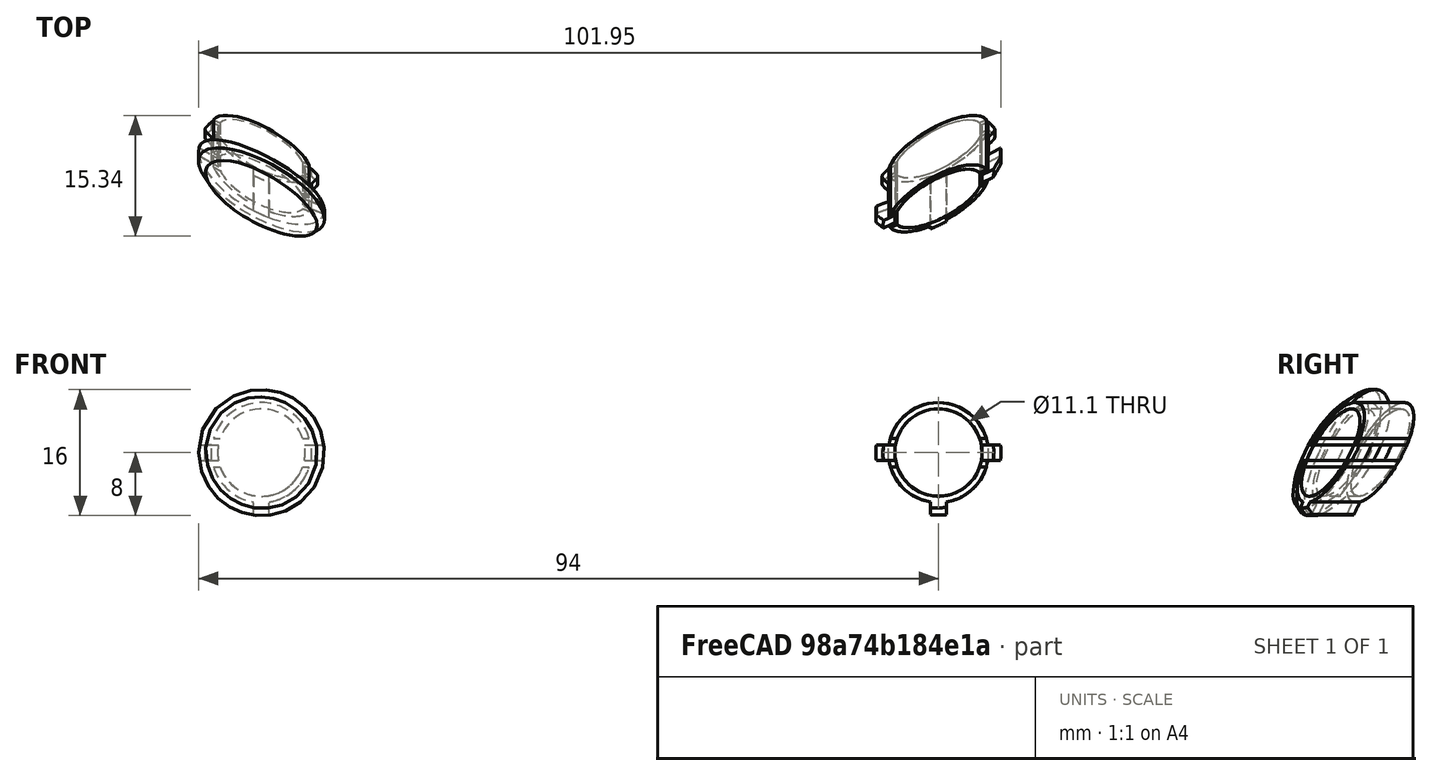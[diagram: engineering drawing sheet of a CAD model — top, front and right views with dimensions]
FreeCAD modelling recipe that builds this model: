
FCSTD DOCUMENT  (FreeCAD 0.19R24276 (Git))
Label: PB3D_XPortCover
License: All rights reserved
LicenseURL: http://en.wikipedia.org/wiki/All_rights_reserved
objects: Sketcher::SketchObject×71, PartDesign::Plane×12, PartDesign::Pad×11, PartDesign::Pocket×11, PartDesign::SubtractiveLoft×6, PartDesign::Chamfer×6, PartDesign::Body×6, PartDesign::Boolean×4, Mesh::Feature×2, Spreadsheet::Sheet×1, App::Part×1, Part::Mirroring×1
note: 162 computed .brp shape members not serialized (recipe doc carries the construction recipe); baked Part::Feature solids carry a one-line shape summary decoded from their .brp

FEATURE [Spreadsheet::Sheet] Spreadsheet  label="params"
  cells = A1=M2 Bolt Clearances; C1=M2.5 Bolt Clearances; E1=Standard Dims; A2=Hole Clear Diam; B2(m2_hole_clear_diam)==2.5mm; C2=Hole Clear Diam; D2(m25_hole_clear_diam)==2.8mm; E2=Std. Tol. Clear; F2(std_tol_clear)==0.3mm; A3=Head Clear Diam; B3(m2_head_clear_diam)==4mm; C3=Head Clear Diam; D3(m25_head_clear_diam)==5mm; E3=Std. Tol. Interfere; F3(std_tol_interfere)==0.2mm; A4=Head Min Depth; B4(m2_head_min_depth)==1.3mm; C4=Head Min Depth; D4(m25_head_min_depth)==1.6mm; E4=Std. Wall Thick; F4(std_wall_thick)==2mm; A5=Nut Clear Flat; B5(m2_nut_clear_flat)==4.2mm; C5=Nut Clear Flat; D5(m25_nut_clear_flat)==5.2mm; E5=Std. Min Wall Thick; F5(std_min_wall_thick)==0.8mm; A6=Nut Min Depth; B6(m2_nut_min_depth)==1.75mm; C6=Nut Min Depth; D6(m25_nut_min_depth)==2mm; A8=Bottom Plate Main Params; C8=Shell Main Params; E8=X Port Front; A9=Plate Length; B9(plate_length)==170mm; C9=Shell Height; D9(shell_totheight)==42mm; E9=XPort Diam; F9(xport_diam)==13mm; A10=Plate Width; B10(plate_width)==155mm; C10=Shell Vert Height; D10(shell_vertheight)==10mm; E10=XPort Height Loc; F10(xport_height_loc)==33.25mm; A11=Front Diameter; B11(front_diameter)==225mm; C11=Shell Overhang Length; D11(shell_overhang_leng)==14mm; E11=XPort Offset Loc; F11(xport_offset_loc)==43mm; A12=Tail Width; B12(tail_width)==50mm; C12=Shell Wall Thickness; D12(shell_wall_thick)==2mm; E12=XPort Plug Wall Thick; F12(xport_plug_wall_thick)==0.8mm; A13=Plate Thickness; B13(plate_thick)==3mm; E13=XPort Plug Diam; F13(xport_plug_diam)==xport_diam - std_tol_clear; C14=Shell Angled Height; D14(shell_overhang_height)==shell_totheight - shell_vertheight; E14=XPort Plug Plate Diam; F14(xport_plug_plate_diam)==16mm; A15=Front Vert. Edge; B15(front_vert_edge)==2mm; C15=Shell Angle; D15(shell_wall_angle)==atan(shell_overhang_leng / shell_overhang_height); E15=XPort Plug Plate Thick; F15(xport_plug_plate_thick)==1.6mm; A16=Back Vert. Edge; B16(back_vert_edge)==15mm; E16=XPort Clip Size; F16(xport_clip_size)==0.8mm; C17=Shell Angle Overhang Calc; A18=Std. Radius; B18(std_rad)==2mm; C18=Overhang Slope; D18(shell_overhang_slope)==shell_overhang_leng / (shell_totheight - shell_vertheight); A19=Wheel Well Radius; B19(wheel_well_rad)==7mm; C19=Overhang Offset; D19(shell_overhang_offset)==-1 * shell_vertheight * shell_overhang_slope; A20=Tail Radius; B20(tail_rad)==5mm; A22=Wheel Well Plate Width; B22(wheel_well_plate_width)==115mm; A23=Wheel Well Clearance; B23(wheel_well_clearance)==48mm; A24=Wheel Well Vert; B24(wheel_well_vert)==7mm
FEATURE [PartDesign::Plane] DatumPlane  label="Datum_ShellVert"
  AttachmentOffset = pos=(0,0,10) rot=(0,0,1;0rad)
  Length = 90.7688
  MapMode = 5
  Placement = pos=(0,0,10) rot=(0,0,1;0rad)
  ResizeMode = 0
  Support = -> [XY_Plane001]
  Width = 86.5183
  expr: .AttachmentOffset.Base.z = <<params>>.shell_vertheight
FEATURE [PartDesign::Plane] DatumPlane001  label="Datum_ShellTot"
  AttachmentOffset = pos=(0,0,42) rot=(0,0,1;0rad)
  Length = 90.7688
  MapMode = 5
  Placement = pos=(0,0,42) rot=(0,0,1;0rad)
  ResizeMode = 0
  Support = -> [XY_Plane001]
  Width = 86.5183
  expr: .AttachmentOffset.Base.z = <<params>>.shell_totheight
FEATURE [Sketcher::SketchObject] Sketch002  label="Sketch_Shell_Vert"
  FullyConstrained = true
  MapMode = 5
  Placement = pos=(0,0,10) rot=(0,0,1;0rad)
  Support = -> [DatumPlane]
  expr: Constraints[106] = <<params>>.xport_offset_loc
  expr: Constraints[121] = <<params>>.std_wall_thick
  expr: Constraints[103] = <<params>>.std_wall_thick
  expr: Constraints[63] = <<params>>.std_rad
  expr: Constraints[113] = <<params>>.xport_plug_plate_thick
  expr: Constraints[104] = <<params>>.plate_length / 2 + <<params>>.std_wall_thick
  expr: Constraints[47] = <<params>>.front_diameter
  expr: Constraints[40] = <<params>>.plate_length
  expr: Constraints[65] = <<params>>.std_rad
  expr: Constraints[76] = <<params>>.front_vert_edge
  expr: Constraints[80] = <<params>>.std_rad
  expr: Constraints[36] = <<params>>.wheel_well_plate_width
  expr: Constraints[77] = <<params>>.back_vert_edge
  expr: Constraints[78] = <<params>>.wheel_well_clearance
  expr: Constraints[42] = <<params>>.tail_width
  expr: Constraints[79] = <<params>>.plate_width
  expr: Constraints[81] = <<params>>.std_rad
  expr: Constraints[41] = <<params>>.tail_rad
  sketch-geometry (50):
    g0: LineSegment StartX=-57.5 StartY=17 StartZ=0 EndX=-57.5 EndY=-17 EndZ=0
    g1: LineSegment StartX=57.5 StartY=17 StartZ=0 EndX=57.5 EndY=-17 EndZ=0
    g2: LineSegment StartX=-57.5 StartY=0 StartZ=0 EndX=57.5 EndY=0 EndZ=0
    g3: LineSegment StartX=-64.5 StartY=-24 StartZ=0 EndX=64.5 EndY=-24 EndZ=0
    g4: LineSegment StartX=-64.5 StartY=24 StartZ=0 EndX=64.5 EndY=24 EndZ=0
    g5: LineSegment StartX=-64.5 StartY=-24 StartZ=0 EndX=-75.5 EndY=-24 EndZ=0
    g6: LineSegment StartX=64.5 StartY=-24 StartZ=0 EndX=75.5 EndY=-24 EndZ=0
    g7: ArcOfCircle CenterX=0 CenterY=52.6846 CenterZ=0 NormalX=0 NormalY=0 NormalZ=1 AngleXU=0 Radius=112.5 StartAngle=3.96017 EndAngle=5.4646
    g8: LineSegment StartX=-64.5 StartY=24 StartZ=0 EndX=-75.5 EndY=24 EndZ=0
    g9: LineSegment StartX=64.5 StartY=24 StartZ=0 EndX=75.5 EndY=24 EndZ=0
    g10: LineSegment StartX=-77.1162 StartY=42.1781 StartZ=0 EndX=-29.0404 EndY=108.13 EndZ=0
    g11: LineSegment StartX=-25 StartY=110.185 StartZ=0 EndX=25 EndY=110.185 EndZ=0
    g12: LineSegment StartX=29.0404 StartY=108.13 StartZ=0 EndX=77.1162 EndY=42.1781 EndZ=0
    g13: LineSegment StartX=0 StartY=0 StartZ=0 EndX=0 EndY=110.185 EndZ=0
    g14: ArcOfCircle CenterX=-25 CenterY=105.185 CenterZ=0 NormalX=0 NormalY=0 NormalZ=1 AngleXU=0 Radius=5 StartAngle=1.5708 EndAngle=2.5117
    g15: ArcOfCircle CenterX=25 CenterY=105.185 CenterZ=0 NormalX=0 NormalY=0 NormalZ=1 AngleXU=0 Radius=5 StartAngle=0.629894 EndAngle=1.5708
    g16: ArcOfCircle CenterX=-64.5 CenterY=17 CenterZ=0 NormalX=0 NormalY=0 NormalZ=1 AngleXU=0 Radius=7 StartAngle=0 EndAngle=1.5708
    g17: ArcOfCircle CenterX=-64.5 CenterY=-17 CenterZ=0 NormalX=0 NormalY=0 NormalZ=1 AngleXU=0 Radius=7 StartAngle=4.71239 EndAngle=6.28319
    g18: ArcOfCircle CenterX=64.5 CenterY=-17 CenterZ=0 NormalX=0 NormalY=0 NormalZ=1 AngleXU=0 Radius=7 StartAngle=3.14159 EndAngle=4.71239
    g19: ArcOfCircle CenterX=64.5 CenterY=17 CenterZ=0 NormalX=0 NormalY=0 NormalZ=1 AngleXU=0 Radius=7 StartAngle=1.5708 EndAngle=3.14159
    g20: GeomPoint X=0 Y=-59.8154 Z=0
    g21: Circle CenterX=0 CenterY=52.6846 CenterZ=0 NormalX=0 NormalY=0 NormalZ=1 AngleXU=0 Radius=112.5
    g22: LineSegment StartX=77.5 StartY=26 StartZ=0 EndX=77.5 EndY=41 EndZ=0
    g23: LineSegment StartX=77.5 StartY=-26 StartZ=0 EndX=77.5 EndY=-28 EndZ=0
    g24: LineSegment StartX=-77.5 StartY=-28 StartZ=0 EndX=-77.5 EndY=-26 EndZ=0
    g25: LineSegment StartX=-77.5 StartY=26 StartZ=0 EndX=-77.5 EndY=41 EndZ=0
    g26: ArcOfCircle CenterX=75.5 CenterY=-28 CenterZ=0 NormalX=0 NormalY=0 NormalZ=1 AngleXU=0 Radius=2 StartAngle=5.4646 EndAngle=6.28319
    g27: ArcOfCircle CenterX=75.5 CenterY=-26 CenterZ=0 NormalX=0 NormalY=0 NormalZ=1 AngleXU=0 Radius=2 StartAngle=4e-16 EndAngle=1.5708
    g28: ArcOfCircle CenterX=-75.5 CenterY=-28 CenterZ=0 NormalX=0 NormalY=0 NormalZ=1 AngleXU=0 Radius=2 StartAngle=3.14159 EndAngle=3.96017
    g29: ArcOfCircle CenterX=-75.5 CenterY=-26 CenterZ=0 NormalX=0 NormalY=0 NormalZ=1 AngleXU=0 Radius=2 StartAngle=1.5708 EndAngle=3.14159
    g30: ArcOfCircle CenterX=75.5 CenterY=26 CenterZ=0 NormalX=0 NormalY=0 NormalZ=1 AngleXU=0 Radius=2 StartAngle=4.71239 EndAngle=6.28319
    g31: ArcOfCircle CenterX=75.5 CenterY=41 CenterZ=0 NormalX=0 NormalY=0 NormalZ=1 AngleXU=0 Radius=2 StartAngle=-9e-16 EndAngle=0.629894
    g32: ArcOfCircle CenterX=-75.5 CenterY=26 CenterZ=0 NormalX=0 NormalY=0 NormalZ=1 AngleXU=0 Radius=2 StartAngle=3.14159 EndAngle=4.71239
    g33: ArcOfCircle CenterX=-75.5 CenterY=41 CenterZ=0 NormalX=0 NormalY=0 NormalZ=1 AngleXU=0 Radius=2 StartAngle=2.5117 EndAngle=3.14159
    g34: LineSegment StartX=77.5 StartY=26 StartZ=0 EndX=77.5 EndY=-26 EndZ=0
    g35: LineSegment StartX=-77.5 StartY=26 StartZ=0 EndX=-77.5 EndY=-26 EndZ=0
    g36: LineSegment StartX=77.5 StartY=41 StartZ=0 EndX=77.5 EndY=-28 EndZ=0
    g37: LineSegment StartX=-77.5 StartY=41 StartZ=0 EndX=-77.5 EndY=-28 EndZ=0
    g38: ArcOfCircle CenterX=0 CenterY=52.6846 CenterZ=0 NormalX=0 NormalY=0 NormalZ=1 AngleXU=0 Radius=112.5 StartAngle=4.71239 EndAngle=5.4646
    g39: LineSegment StartX=-2 StartY=2 StartZ=0 EndX=-2 EndY=-87 EndZ=0
    g40: LineSegment StartX=76.8665 StartY=-38.9967 StartZ=0 EndX=76.8665 EndY=-87 EndZ=0
    g41: LineSegment StartX=-2 StartY=-87 StartZ=0 EndX=76.8665 EndY=-87 EndZ=0
    g42: LineSegment StartX=76.8665 StartY=-29.4604 StartZ=0 EndX=76.8665 EndY=2 EndZ=0
    g43: LineSegment StartX=-2 StartY=2 StartZ=0 EndX=76.8665 EndY=2 EndZ=0
    g44: LineSegment StartX=0 StartY=-70.7909 StartZ=0 EndX=76.8665 EndY=-38.9967 EndZ=0
    g45: GeomPoint X=43 Y=-51.2734 Z=0
    g46: LineSegment StartX=0 StartY=52.6846 StartZ=0 EndX=43 EndY=-51.2734 EndZ=0
    g47: LineSegment StartX=43.6116 StartY=-52.7519 StartZ=0 EndX=43 EndY=-51.2734 EndZ=0
    g48: LineSegment StartX=76.8665 StartY=-38.9967 StartZ=0 EndX=76.8665 EndY=-29.4604 EndZ=0
    g49: LineSegment StartX=-2.07e-14 StartY=-59.8154 StartZ=0 EndX=0 EndY=-70.7909 EndZ=0
  constraints (122):
    c: Vertical(g0)
    c: Vertical(g1)
    c: Horizontal(g2)
    c: Symmetric(g2,g2,g-1)
    c: Horizontal(g3)
    c: Horizontal(g5)
    c: Horizontal(g6)
    c: PointOnObject(g7,g-2)
    c: Horizontal(g8)
    c: Horizontal(g9)
    c: Horizontal(g11)
    c: Coincident(g13,g-1)
    c: PointOnObject(g13,g-2)
    c: Tangent(g10,g14) = 1.5708
    c: Tangent(g11,g14) = 1.5708
    c: Tangent(g11,g15) = 1.5708
    c: Tangent(g12,g15) = 1.5708
    c: Tangent(g8,g16) = -1.5708
    c: Tangent(g0,g16) = 1.5708
    c: Tangent(g5,g17) = 1.5708
    c: Tangent(g0,g17) = 1.5708
    c: Tangent(g1,g18) = -1.5708
    c: Tangent(g6,g18) = -1.5708
    c: Tangent(g1,g19) = -1.5708
    c: Tangent(g9,g19) = 1.5708
    c: Equal(g15,g14)
    c: Symmetric(g11,g11,g13)
    c: Equal(g18,g19)
    c: Equal(g19,g16)
    c: Equal(g16,g17)
    c: PointOnObject(g20,g-2)
    c: PointOnObject(g20,g7)
    c: Coincident(g4,g8)
    c: Coincident(g4,g9)
    c: Coincident(g3,g6)
    c: Coincident(g3,g5)
    c: DistanceX(g2,g2) = 115
    c: Symmetric(g0,g0,g2)
    c: Symmetric(g1,g1,g2)
    c: Radius(g19) = 7
    c: DistanceY(g20,g11) = 170
    c: Radius(g15) = 5
    c: DistanceX(g11,g11) = 50
    c: Equal(g9,g8)
    c: Equal(g9,g6)
    c: Coincident(g21,g7)
    c: PointOnObject(g20,g21)
    c: Diameter(g21) = 225
    c: Vertical(g22)
    c: Vertical(g23)
    c: Vertical(g24)
    c: Vertical(g25)
    c: Equal(g5,g8)
    c: Equal(g10,g12)
    c: Tangent(g7,g26) = -1.5708
    c: Tangent(g23,g26) = 1.5708
    c: Tangent(g23,g27) = 1.5708
    c: Tangent(g6,g27) = 1.5708
    c: Tangent(g7,g28) = -1.5708
    c: Tangent(g24,g28) = 1.5708
    c: Tangent(g24,g29) = 1.5708
    c: Tangent(g5,g29) = -1.5708
    c: Equal(g29,g27)
    c: Radius(g27) = 2
    c: Equal(g26,g28)
    c: Radius(g26) = 2
    c: Tangent(g9,g30) = -1.5708
    c: Tangent(g22,g30) = -1.5708
    c: Tangent(g22,g31) = -1.5708
    c: Tangent(g12,g31) = 1.5708
    c: Tangent(g8,g32) = 1.5708
    c: Tangent(g25,g32) = 1.5708
    c: Tangent(g10,g33) = 1.5708
    c: Tangent(g25,g33) = 1.5708
    c: Equal(g30,g32)
    c: Equal(g31,g33)
    c: DistanceY(g23,g23) = 2
    c: DistanceY(g22,g22) = 15
    c: DistanceY(g6,g9) = 48
    c: DistanceX(g24,g23) = 155
    c: Radius(g30) = 2
    c: Radius(g31) = 2
    c: Coincident(g34,g22)
    c: Coincident(g34,g23)
    c: Coincident(g35,g25)
    c: Coincident(g35,g24)
    c: Coincident(g37,g28)
    c: Coincident(g37,g33)
    c: Coincident(g36,g31)
    c: Coincident(g36,g26)
    c: Coincident(g38,g7)
    c: PointOnObject(g38,g-2)
    c: Coincident(g38,g7)
    c: Vertical(g39)
    c: Vertical(g40)
    c: Coincident(g41,g39)
    c: Coincident(g41,g40)
    c: Horizontal(g41)
    c: Coincident(g42,g38)
    c: Vertical(g42)
    c: Coincident(g43,g39)
    c: Coincident(g43,g42)
    c: Horizontal(g43)
    c: DistanceY(g-1,g39) = 2
    c: DistanceY(g39,g-1) = 87
    c: PointOnObject(g45,g38)
    c: DistanceX(g-1,g45) = 43
    c: Coincident(g46,g45)
    c: Coincident(g46,g38)
    c: Coincident(g47,g45)
    c: PointOnObject(g47,g44)
    c: Parallel(g46,g47)
    c: Perpendicular(g47,g44)
    c: Distance(g47) = 1.6
    c: PointOnObject(g44,g-2)
    c: Coincident(g40,g44)
    c: Coincident(g48,g40)
    c: Coincident(g48,g38)
    c: Vertical(g48)
    c: Coincident(g49,g38)
    c: Coincident(g49,g44)
    c: DistanceX(g39,g44) = 2
FEATURE [Sketcher::SketchObject] Sketch003  label="Sketch_Shell_Top"
  FullyConstrained = true
  MapMode = 5
  Placement = pos=(0,0,42) rot=(0,0,1;0rad)
  Support = -> [DatumPlane001]
  expr: Constraints[132] = <<params>>.std_wall_thick
  expr: Constraints[133] = <<params>>.plate_length / 2 + <<params>>.std_wall_thick
  expr: Constraints[79] = <<params>>.plate_width
  expr: Constraints[36] = <<params>>.wheel_well_plate_width - 2 * Spreadsheet.shell_overhang_leng
  expr: Constraints[41] = <<params>>.tail_rad
  expr: Constraints[140] = <<params>>.xport_offset_loc
  expr: Constraints[81] = <<params>>.std_rad
  expr: Constraints[150] = <<params>>.xport_plug_plate_thick
  expr: Constraints[65] = <<params>>.std_rad
  expr: Constraints[40] = <<params>>.plate_length
  expr: Constraints[88] = Spreadsheet.shell_overhang_leng
  expr: Constraints[78] = <<params>>.wheel_well_clearance
  expr: Constraints[42] = <<params>>.tail_width
  expr: Constraints[151] = <<params>>.std_wall_thick
  expr: Constraints[77] = <<params>>.back_vert_edge
  expr: Constraints[76] = <<params>>.front_vert_edge
  expr: Constraints[47] = <<params>>.front_diameter
  expr: Constraints[113] = Spreadsheet.shell_overhang_leng
  expr: Constraints[114] = <<params>>.shell_overhang_leng
  expr: Constraints[63] = <<params>>.std_rad
  expr: Constraints[117] = <<params>>.shell_overhang_leng
  expr: Constraints[80] = <<params>>.std_rad
  expr: Constraints[152] = <<params>>.shell_overhang_leng
  sketch-geometry (64):
    g0: LineSegment StartX=-43.5 StartY=17 StartZ=0 EndX=-43.5 EndY=-17 EndZ=0
    g1: LineSegment StartX=43.5 StartY=17 StartZ=0 EndX=43.5 EndY=-17 EndZ=0
    g2: LineSegment StartX=-43.5 StartY=0 StartZ=0 EndX=43.5 EndY=0 EndZ=0
    g3: LineSegment StartX=-50.5 StartY=-24 StartZ=0 EndX=50.5 EndY=-24 EndZ=0
    g4: LineSegment StartX=-50.5 StartY=24 StartZ=0 EndX=50.5 EndY=24 EndZ=0
    g5: LineSegment StartX=-50.5 StartY=-24 StartZ=0 EndX=-75.5 EndY=-24 EndZ=0
    g6: LineSegment StartX=50.5 StartY=-24 StartZ=0 EndX=75.5 EndY=-24 EndZ=0
    g7: ArcOfCircle CenterX=0 CenterY=52.6846 CenterZ=0 NormalX=0 NormalY=0 NormalZ=1 AngleXU=0 Radius=112.5 StartAngle=3.96017 EndAngle=5.4646
    g8: LineSegment StartX=-50.5 StartY=24 StartZ=0 EndX=-75.5 EndY=24 EndZ=0
    g9: LineSegment StartX=50.5 StartY=24 StartZ=0 EndX=75.5 EndY=24 EndZ=0
    g10: LineSegment StartX=-77.1162 StartY=42.1781 StartZ=0 EndX=-29.0404 EndY=108.13 EndZ=0
    g11: LineSegment StartX=-25 StartY=110.185 StartZ=0 EndX=25 EndY=110.185 EndZ=0
    g12: LineSegment StartX=29.0404 StartY=108.13 StartZ=0 EndX=77.1162 EndY=42.1781 EndZ=0
    g13: LineSegment StartX=0 StartY=0 StartZ=0 EndX=0 EndY=110.185 EndZ=0
    g14: ArcOfCircle CenterX=-25 CenterY=105.185 CenterZ=0 NormalX=0 NormalY=0 NormalZ=1 AngleXU=0 Radius=5 StartAngle=1.5708 EndAngle=2.5117
    g15: ArcOfCircle CenterX=25 CenterY=105.185 CenterZ=0 NormalX=0 NormalY=0 NormalZ=1 AngleXU=0 Radius=5 StartAngle=0.629894 EndAngle=1.5708
    g16: ArcOfCircle CenterX=-50.5 CenterY=17 CenterZ=0 NormalX=0 NormalY=0 NormalZ=1 AngleXU=0 Radius=7 StartAngle=0 EndAngle=1.5708
    g17: ArcOfCircle CenterX=-50.5 CenterY=-17 CenterZ=0 NormalX=0 NormalY=0 NormalZ=1 AngleXU=0 Radius=7 StartAngle=4.71239 EndAngle=6.28319
    g18: ArcOfCircle CenterX=50.5 CenterY=-17 CenterZ=0 NormalX=0 NormalY=0 NormalZ=1 AngleXU=0 Radius=7 StartAngle=3.14159 EndAngle=4.71239
    g19: ArcOfCircle CenterX=50.5 CenterY=17 CenterZ=0 NormalX=0 NormalY=0 NormalZ=1 AngleXU=0 Radius=7 StartAngle=1.5708 EndAngle=3.14159
    g20: GeomPoint X=0 Y=-59.8154 Z=0
    g21: Circle CenterX=0 CenterY=52.6846 CenterZ=0 NormalX=0 NormalY=0 NormalZ=1 AngleXU=0 Radius=112.5
    g22: LineSegment StartX=77.5 StartY=26 StartZ=0 EndX=77.5 EndY=41 EndZ=0
    g23: LineSegment StartX=77.5 StartY=-26 StartZ=0 EndX=77.5 EndY=-28 EndZ=0
    g24: LineSegment StartX=-77.5 StartY=-28 StartZ=0 EndX=-77.5 EndY=-26 EndZ=0
    g25: LineSegment StartX=-77.5 StartY=26 StartZ=0 EndX=-77.5 EndY=41 EndZ=0
    g26: ArcOfCircle CenterX=75.5 CenterY=-28 CenterZ=0 NormalX=0 NormalY=0 NormalZ=1 AngleXU=0 Radius=2 StartAngle=5.4646 EndAngle=6.28319
    g27: ArcOfCircle CenterX=75.5 CenterY=-26 CenterZ=0 NormalX=0 NormalY=0 NormalZ=1 AngleXU=0 Radius=2 StartAngle=-9e-16 EndAngle=1.5708
    g28: ArcOfCircle CenterX=-75.5 CenterY=-28 CenterZ=0 NormalX=0 NormalY=0 NormalZ=1 AngleXU=0 Radius=2 StartAngle=3.14159 EndAngle=3.96017
    g29: ArcOfCircle CenterX=-75.5 CenterY=-26 CenterZ=0 NormalX=0 NormalY=0 NormalZ=1 AngleXU=0 Radius=2 StartAngle=1.5708 EndAngle=3.14159
    g30: ArcOfCircle CenterX=75.5 CenterY=26 CenterZ=0 NormalX=0 NormalY=0 NormalZ=1 AngleXU=0 Radius=2 StartAngle=4.71239 EndAngle=6.28319
    g31: ArcOfCircle CenterX=75.5 CenterY=41 CenterZ=0 NormalX=0 NormalY=0 NormalZ=1 AngleXU=0 Radius=2 StartAngle=1.7e-15 EndAngle=0.629894
    g32: ArcOfCircle CenterX=-75.5 CenterY=26 CenterZ=0 NormalX=0 NormalY=0 NormalZ=1 AngleXU=0 Radius=2 StartAngle=3.14159 EndAngle=4.71239
    g33: ArcOfCircle CenterX=-75.5 CenterY=41 CenterZ=0 NormalX=0 NormalY=0 NormalZ=1 AngleXU=0 Radius=2 StartAngle=2.5117 EndAngle=3.14159
    g34: LineSegment StartX=77.5 StartY=26 StartZ=0 EndX=77.5 EndY=-26 EndZ=0
    g35: LineSegment StartX=-77.5 StartY=26 StartZ=0 EndX=-77.5 EndY=-26 EndZ=0
    g36: LineSegment StartX=-17.8805 StartY=96.1846 StartZ=0 EndX=17.8805 EndY=96.1846 EndZ=0
    g37: GeomPoint X=0 Y=96.1846 Z=0
    g38: LineSegment StartX=-21.921 StartY=94.1299 StartZ=0 EndX=-63.1162 EndY=37.617 EndZ=0
    g39: LineSegment StartX=-63.5 StartY=36.4389 StartZ=0 EndX=-63.5 EndY=-21.6794 EndZ=0
    g40: LineSegment StartX=21.921 StartY=94.1299 StartZ=0 EndX=63.1162 EndY=37.617 EndZ=0
    g41: LineSegment StartX=63.5 StartY=36.4389 StartZ=0 EndX=63.5 EndY=-21.6794 EndZ=0
    g42: ArcOfCircle CenterX=0 CenterY=52.6846 CenterZ=0 NormalX=0 NormalY=0 NormalZ=1 AngleXU=0 Radius=98.5 StartAngle=4.02139 EndAngle=5.40339
    g43: LineSegment StartX=-63.5 StartY=36.4389 StartZ=0 EndX=63.5 EndY=36.4389 EndZ=0
    g44: GeomPoint X=0 Y=-45.8154 Z=0
    g45: ArcOfCircle CenterX=-17.8805 CenterY=91.1846 CenterZ=0 NormalX=0 NormalY=0 NormalZ=1 AngleXU=0 Radius=5 StartAngle=1.5708 EndAngle=2.5117
    g46: ArcOfCircle CenterX=17.8805 CenterY=91.1846 CenterZ=0 NormalX=0 NormalY=0 NormalZ=1 AngleXU=0 Radius=5 StartAngle=0.629894 EndAngle=1.5708
    g47: ArcOfCircle CenterX=61.5 CenterY=36.4389 CenterZ=0 NormalX=0 NormalY=0 NormalZ=1 AngleXU=0 Radius=2 StartAngle=-9e-16 EndAngle=0.629894
    g48: ArcOfCircle CenterX=-61.5 CenterY=36.4389 CenterZ=0 NormalX=0 NormalY=0 NormalZ=1 AngleXU=0 Radius=2 StartAngle=2.5117 EndAngle=3.14159
    g49: ArcOfCircle CenterX=-61.5 CenterY=-21.6794 CenterZ=0 NormalX=0 NormalY=0 NormalZ=1 AngleXU=0 Radius=2 StartAngle=3.14159 EndAngle=4.02139
    g50: LineSegment StartX=-29.0404 StartY=108.13 StartZ=0 EndX=-17.7272 EndY=99.883 EndZ=0
    g51: ArcOfCircle CenterX=0 CenterY=52.6846 CenterZ=0 NormalX=0 NormalY=0 NormalZ=1 AngleXU=0 Radius=98.5 StartAngle=4.71239 EndAngle=5.40339
    g52: LineSegment StartX=-2 StartY=2 StartZ=0 EndX=-2 EndY=-87 EndZ=0
    g53: LineSegment StartX=-2 StartY=-87 StartZ=0 EndX=62.7746 EndY=-87 EndZ=0
    g54: LineSegment StartX=62.7746 StartY=-87 StartZ=0 EndX=62.7746 EndY=-28.1173 EndZ=0
    g55: LineSegment StartX=62.7746 StartY=-23.2206 StartZ=0 EndX=62.7746 EndY=2 EndZ=0
    g56: LineSegment StartX=62.7746 StartY=2 StartZ=0 EndX=-2 EndY=2 EndZ=0
    g57: LineSegment StartX=0 StartY=-58.5771 StartZ=0 EndX=62.7746 EndY=-28.1173 EndZ=0
    g58: LineSegment StartX=62.7746 StartY=-23.2206 StartZ=0 EndX=62.7746 EndY=-28.1173 EndZ=0
    g59: GeomPoint X=43 Y=-35.934 Z=0
    g60: LineSegment StartX=0 StartY=52.6846 StartZ=0 EndX=43 EndY=-35.934 EndZ=0
    g61: LineSegment StartX=43 StartY=-35.934 StartZ=0 EndX=43.6985 EndY=-37.3735 EndZ=0
    g62: LineSegment StartX=0 StartY=-58.5771 StartZ=0 EndX=0 EndY=-45.8154 EndZ=0
    g63: ArcOfCircle CenterX=61.5 CenterY=-21.6794 CenterZ=0 NormalX=0 NormalY=0 NormalZ=1 AngleXU=0 Radius=2 StartAngle=5.40338 EndAngle=6.28319
  constraints (159):
    c: Vertical(g0)
    c: Vertical(g1)
    c: Horizontal(g2)
    c: Symmetric(g2,g2,g-1)
    c: Horizontal(g3)
    c: Horizontal(g5)
    c: Horizontal(g6)
    c: PointOnObject(g7,g-2)
    c: Horizontal(g8)
    c: Horizontal(g9)
    c: Horizontal(g11)
    c: Coincident(g13,g-1)
    c: PointOnObject(g13,g-2)
    c: Tangent(g10,g14) = 1.5708
    c: Tangent(g11,g14) = 1.5708
    c: Tangent(g11,g15) = 1.5708
    c: Tangent(g12,g15) = 1.5708
    c: Tangent(g8,g16) = -1.5708
    c: Tangent(g0,g16) = 1.5708
    c: Tangent(g5,g17) = 1.5708
    c: Tangent(g0,g17) = 1.5708
    c: Tangent(g1,g18) = -1.5708
    c: Tangent(g6,g18) = -1.5708
    c: Tangent(g1,g19) = -1.5708
    c: Tangent(g9,g19) = 1.5708
    c: Equal(g15,g14)
    c: Symmetric(g11,g11,g13)
    c: Equal(g18,g19)
    c: Equal(g19,g16)
    c: Equal(g16,g17)
    c: PointOnObject(g20,g-2)
    c: PointOnObject(g20,g7)
    c: Coincident(g4,g8)
    c: Coincident(g4,g9)
    c: Coincident(g3,g6)
    c: Coincident(g3,g5)
    c: DistanceX(g2,g2) = 87
    c: Symmetric(g0,g0,g2)
    c: Symmetric(g1,g1,g2)
    c: Radius(g19) = 7
    c: DistanceY(g20,g11) = 170
    c: Radius(g15) = 5
    c: DistanceX(g11,g11) = 50
    c: Equal(g9,g8)
    c: Equal(g9,g6)
    c: Coincident(g21,g7)
    c: PointOnObject(g20,g21)
    c: Diameter(g21) = 225
    c: Vertical(g22)
    c: Vertical(g23)
    c: Vertical(g24)
    c: Vertical(g25)
    c: Equal(g5,g8)
    c: Equal(g10,g12)
    c: Tangent(g7,g26) = -1.5708
    c: Tangent(g23,g26) = 1.5708
    c: Tangent(g23,g27) = 1.5708
    c: Tangent(g6,g27) = 1.5708
    c: Tangent(g7,g28) = -1.5708
    c: Tangent(g24,g28) = 1.5708
    c: Tangent(g24,g29) = 1.5708
    c: Tangent(g5,g29) = -1.5708
    c: Equal(g29,g27)
    c: Radius(g27) = 2
    c: Equal(g26,g28)
    c: Radius(g26) = 2
    c: Tangent(g9,g30) = -1.5708
    c: Tangent(g22,g30) = -1.5708
    c: Tangent(g22,g31) = -1.5708
    c: Tangent(g12,g31) = 1.5708
    c: Tangent(g8,g32) = 1.5708
    c: Tangent(g25,g32) = 1.5708
    c: Tangent(g10,g33) = 1.5708
    c: Tangent(g25,g33) = 1.5708
    c: Equal(g30,g32)
    c: Equal(g31,g33)
    c: DistanceY(g23,g23) = 2
    c: DistanceY(g22,g22) = 15
    c: DistanceY(g6,g9) = 48
    c: DistanceX(g24,g23) = 155
    c: Radius(g30) = 2
    c: Radius(g31) = 2
    c: Coincident(g34,g22)
    c: Coincident(g34,g23)
    c: Coincident(g35,g25)
    c: Coincident(g35,g24)
    c: Horizontal(g36)
    c: PointOnObject(g37,g13)
    c: DistanceY(g37,g13) = 14
    c: Vertical(g39)
    c: Vertical(g41)
    c: Horizontal(g43)
    c: Parallel(g40,g12)
    c: PointOnObject(g44,g-2)
    c: PointOnObject(g44,g42)
    c: Tangent(g38,g45) = -1.5708
    c: Tangent(g36,g45) = 1.5708
    c: Tangent(g40,g46) = 1.5708
    c: Tangent(g36,g46) = 1.5708
    c: Tangent(g41,g47) = 1.5708
    c: Tangent(g40,g47) = 1.5708
    c: Tangent(g39,g48) = -1.5708
    c: Tangent(g38,g48) = -1.5708
    c: Tangent(g42,g49) = -1.5708
    c: Tangent(g39,g49) = -1.5708
    c: Coincident(g43,g39)
    c: Coincident(g43,g41)
    c: Equal(g15,g46)
    c: Equal(g46,g45)
    c: Symmetric(g36,g36,g37)
    c: Equal(g31,g47)
    c: Equal(g49,g29)
    c: Equal(g48,g32)
    c: DistanceY(g20,g44) = 14
    c: DistanceX(g41,g22) = 14
    c: PointOnObject(g50,g38)
    c: Perpendicular(g38,g50)
    c: Distance(g50) = 14
    c: Coincident(g50,g10)
    c: Coincident(g51,g42)
    c: Coincident(g51,g42)
    c: PointOnObject(g51,g-2)
    c: Vertical(g52)
    c: Coincident(g53,g52)
    c: Horizontal(g53)
    c: Coincident(g54,g53)
    c: Vertical(g54)
    c: Coincident(g55,g51)
    c: Vertical(g55)
    c: Coincident(g56,g55)
    c: Coincident(g56,g52)
    c: Horizontal(g56)
    c: DistanceY(g-1,g52) = 2
    c: DistanceY(g52,g-1) = 87
    c: Coincident(g54,g57)
    c: Coincident(g58,g51)
    c: Coincident(g58,g54)
    c: Vertical(g58)
    c: PointOnObject(g57,g-2)
    c: PointOnObject(g59,g42)
    c: DistanceX(g-1,g59) = 43
    c: Coincident(g60,g51)
    c: Coincident(g60,g59)
    c: Coincident(g61,g59)
    c: PointOnObject(g61,g57)
    c: Parallel(g61,g60)
    c: Perpendicular(g57,g61)
    c: Vertical(g62)
    c: Coincident(g62,g51)
    c: PointOnObject(g62,g57)
    c: Distance(g61) = 1.6
    c: DistanceX(g52,g-1) = 2
    c: DistanceX(g25,g39) = 14
    c: Coincident(g63,g41)
    c: Coincident(g63,g51)
    c: Tangent(g63,g41)
    c: Tangent(g63,g51)
    c: Equal(g49,g63)
    c: Coincident(g51,g7)
FEATURE [Sketcher::SketchObject] Sketch
  FullyConstrained = true
  MapMode = 5
  Placement = pos=(0,0,0) rot=(1,0,0;1.5708rad)
  Support = -> [XZ_Plane001]
  expr: Constraints[2] = <<params>>.xport_height_loc
  expr: Constraints[1] = <<params>>.xport_offset_loc
  expr: Constraints[0] = <<params>>.xport_plug_plate_diam
  sketch-geometry (1):
    g0: Circle CenterX=43 CenterY=33.25 CenterZ=0 NormalX=0 NormalY=0 NormalZ=1 AngleXU=0 Radius=8
  constraints (3):
    c: Diameter(g0) = 16
    c: DistanceX(g-1,g0) = 43
    c: DistanceY(g-1,g0) = 33.25
FEATURE [PartDesign::Pad] Pad  label="Pad_CoverPlate"
  Direction = (1,1,1)
  Length = 85
  Length2 = 100
  Placement = pos=(0,0,0) rot=(1,0,0;1.5708rad)
  Profile = -> Sketch
  Type = 0
  expr: Length = <<params>>.plate_length / 2
FEATURE [PartDesign::Plane] DatumPlane002  label="Datum_ShellVert001"
  AttachmentOffset = pos=(0,0,10) rot=(0,0,1;0rad)
  Length = 90.6584
  MapMode = 5
  Placement = pos=(0,0,10) rot=(0,0,1;0rad)
  ResizeMode = 0
  Support = -> [XY_Plane002]
  Width = 85.9187
  expr: .AttachmentOffset.Base.z = <<params>>.shell_vertheight
FEATURE [Sketcher::SketchObject] Sketch004
  FullyConstrained = true
  MapMode = 5
  Placement = pos=(0,0,0) rot=(1,0,0;1.5708rad)
  Support = -> [XZ_Plane002]
  expr: Constraints[0] = <<params>>.xport_plug_diam
  expr: Constraints[1] = <<params>>.xport_offset_loc
  expr: Constraints[2] = <<params>>.xport_height_loc
  sketch-geometry (1):
    g0: Circle CenterX=43 CenterY=33.25 CenterZ=0 NormalX=0 NormalY=0 NormalZ=1 AngleXU=0 Radius=6.35
  constraints (3):
    c: Diameter(g0) = 12.7
    c: DistanceX(g-1,g0) = 43
    c: DistanceY(g-1,g0) = 33.25
FEATURE [Sketcher::SketchObject] Sketch005  label="Sketch_Shell_Vert001"
  FullyConstrained = true
  MapMode = 5
  Placement = pos=(0,0,10) rot=(0,0,1;0rad)
  Support = -> [DatumPlane002]
  expr: Constraints[41] = <<params>>.tail_rad
  expr: Constraints[81] = <<params>>.std_rad
  expr: Constraints[80] = <<params>>.std_rad
  expr: Constraints[77] = <<params>>.back_vert_edge
  expr: Constraints[76] = <<params>>.front_vert_edge
  expr: Constraints[63] = <<params>>.std_rad
  expr: Constraints[47] = <<params>>.front_diameter
  expr: Constraints[36] = <<params>>.wheel_well_plate_width
  expr: Constraints[79] = <<params>>.plate_width
  expr: Constraints[78] = <<params>>.wheel_well_clearance
  expr: Constraints[42] = <<params>>.tail_width
  expr: Constraints[65] = <<params>>.std_rad
  expr: Constraints[40] = <<params>>.plate_length
  sketch-geometry (38):
    g0: LineSegment StartX=-57.5 StartY=17 StartZ=0 EndX=-57.5 EndY=-17 EndZ=0
    g1: LineSegment StartX=57.5 StartY=17 StartZ=0 EndX=57.5 EndY=-17 EndZ=0
    g2: LineSegment StartX=-57.5 StartY=0 StartZ=0 EndX=57.5 EndY=0 EndZ=0
    g3: LineSegment StartX=-64.5 StartY=-24 StartZ=0 EndX=64.5 EndY=-24 EndZ=0
    g4: LineSegment StartX=-64.5 StartY=24 StartZ=0 EndX=64.5 EndY=24 EndZ=0
    g5: LineSegment StartX=-64.5 StartY=-24 StartZ=0 EndX=-75.5 EndY=-24 EndZ=0
    g6: LineSegment StartX=64.5 StartY=-24 StartZ=0 EndX=75.5 EndY=-24 EndZ=0
    g7: ArcOfCircle CenterX=0 CenterY=52.6846 CenterZ=0 NormalX=0 NormalY=0 NormalZ=1 AngleXU=0 Radius=112.5 StartAngle=3.96017 EndAngle=5.4646
    g8: LineSegment StartX=-64.5 StartY=24 StartZ=0 EndX=-75.5 EndY=24 EndZ=0
    g9: LineSegment StartX=64.5 StartY=24 StartZ=0 EndX=75.5 EndY=24 EndZ=0
    g10: LineSegment StartX=-77.1162 StartY=42.1781 StartZ=0 EndX=-29.0404 EndY=108.13 EndZ=0
    g11: LineSegment StartX=-25 StartY=110.185 StartZ=0 EndX=25 EndY=110.185 EndZ=0
    g12: LineSegment StartX=29.0404 StartY=108.13 StartZ=0 EndX=77.1162 EndY=42.1781 EndZ=0
    g13: LineSegment StartX=0 StartY=0 StartZ=0 EndX=0 EndY=110.185 EndZ=0
    g14: ArcOfCircle CenterX=-25 CenterY=105.185 CenterZ=0 NormalX=0 NormalY=0 NormalZ=1 AngleXU=0 Radius=5 StartAngle=1.5708 EndAngle=2.5117
    g15: ArcOfCircle CenterX=25 CenterY=105.185 CenterZ=0 NormalX=0 NormalY=0 NormalZ=1 AngleXU=0 Radius=5 StartAngle=0.629894 EndAngle=1.5708
    g16: ArcOfCircle CenterX=-64.5 CenterY=17 CenterZ=0 NormalX=0 NormalY=0 NormalZ=1 AngleXU=0 Radius=7 StartAngle=0 EndAngle=1.5708
    g17: ArcOfCircle CenterX=-64.5 CenterY=-17 CenterZ=0 NormalX=0 NormalY=0 NormalZ=1 AngleXU=0 Radius=7 StartAngle=4.71239 EndAngle=6.28319
    g18: ArcOfCircle CenterX=64.5 CenterY=-17 CenterZ=0 NormalX=0 NormalY=0 NormalZ=1 AngleXU=0 Radius=7 StartAngle=3.14159 EndAngle=4.71239
    g19: ArcOfCircle CenterX=64.5 CenterY=17 CenterZ=0 NormalX=0 NormalY=0 NormalZ=1 AngleXU=0 Radius=7 StartAngle=1.5708 EndAngle=3.14159
    g20: GeomPoint X=0 Y=-59.8154 Z=0
    g21: Circle CenterX=0 CenterY=52.6846 CenterZ=0 NormalX=0 NormalY=0 NormalZ=1 AngleXU=0 Radius=112.5
    g22: LineSegment StartX=77.5 StartY=26 StartZ=0 EndX=77.5 EndY=41 EndZ=0
    g23: LineSegment StartX=77.5 StartY=-26 StartZ=0 EndX=77.5 EndY=-28 EndZ=0
    g24: LineSegment StartX=-77.5 StartY=-28 StartZ=0 EndX=-77.5 EndY=-26 EndZ=0
    g25: LineSegment StartX=-77.5 StartY=26 StartZ=0 EndX=-77.5 EndY=41 EndZ=0
    g26: ArcOfCircle CenterX=75.5 CenterY=-28 CenterZ=0 NormalX=0 NormalY=0 NormalZ=1 AngleXU=0 Radius=2 StartAngle=5.4646 EndAngle=6.28319
    g27: ArcOfCircle CenterX=75.5 CenterY=-26 CenterZ=0 NormalX=0 NormalY=0 NormalZ=1 AngleXU=0 Radius=2 StartAngle=-9e-16 EndAngle=1.5708
    g28: ArcOfCircle CenterX=-75.5 CenterY=-28 CenterZ=0 NormalX=0 NormalY=0 NormalZ=1 AngleXU=0 Radius=2 StartAngle=3.14159 EndAngle=3.96017
    g29: ArcOfCircle CenterX=-75.5 CenterY=-26 CenterZ=0 NormalX=0 NormalY=0 NormalZ=1 AngleXU=0 Radius=2 StartAngle=1.5708 EndAngle=3.14159
    g30: ArcOfCircle CenterX=75.5 CenterY=26 CenterZ=0 NormalX=0 NormalY=0 NormalZ=1 AngleXU=0 Radius=2 StartAngle=4.71239 EndAngle=6.28319
    g31: ArcOfCircle CenterX=75.5 CenterY=41 CenterZ=0 NormalX=0 NormalY=0 NormalZ=1 AngleXU=0 Radius=2 StartAngle=0 EndAngle=0.629894
    g32: ArcOfCircle CenterX=-75.5 CenterY=26 CenterZ=0 NormalX=0 NormalY=0 NormalZ=1 AngleXU=0 Radius=2 StartAngle=3.14159 EndAngle=4.71239
    g33: ArcOfCircle CenterX=-75.5 CenterY=41 CenterZ=0 NormalX=0 NormalY=0 NormalZ=1 AngleXU=0 Radius=2 StartAngle=2.5117 EndAngle=3.14159
    g34: LineSegment StartX=77.5 StartY=26 StartZ=0 EndX=77.5 EndY=-26 EndZ=0
    g35: LineSegment StartX=-77.5 StartY=26 StartZ=0 EndX=-77.5 EndY=-26 EndZ=0
    g36: LineSegment StartX=77.5 StartY=41 StartZ=0 EndX=77.5 EndY=-28 EndZ=0
    g37: LineSegment StartX=-77.5 StartY=41 StartZ=0 EndX=-77.5 EndY=-28 EndZ=0
  constraints (90):
    c: Vertical(g0)
    c: Vertical(g1)
    c: Horizontal(g2)
    c: Symmetric(g2,g2,g-1)
    c: Horizontal(g3)
    c: Horizontal(g5)
    c: Horizontal(g6)
    c: PointOnObject(g7,g-2)
    c: Horizontal(g8)
    c: Horizontal(g9)
    c: Horizontal(g11)
    c: Coincident(g13,g-1)
    c: PointOnObject(g13,g-2)
    c: Tangent(g10,g14) = 1.5708
    c: Tangent(g11,g14) = 1.5708
    c: Tangent(g11,g15) = 1.5708
    c: Tangent(g12,g15) = 1.5708
    c: Tangent(g8,g16) = -1.5708
    c: Tangent(g0,g16) = 1.5708
    c: Tangent(g5,g17) = 1.5708
    c: Tangent(g0,g17) = 1.5708
    c: Tangent(g1,g18) = -1.5708
    c: Tangent(g6,g18) = -1.5708
    c: Tangent(g1,g19) = -1.5708
    c: Tangent(g9,g19) = 1.5708
    c: Equal(g15,g14)
    c: Symmetric(g11,g11,g13)
    c: Equal(g18,g19)
    c: Equal(g19,g16)
    c: Equal(g16,g17)
    c: PointOnObject(g20,g-2)
    c: PointOnObject(g20,g7)
    c: Coincident(g4,g8)
    c: Coincident(g4,g9)
    c: Coincident(g3,g6)
    c: Coincident(g3,g5)
    c: DistanceX(g2,g2) = 115
    c: Symmetric(g0,g0,g2)
    c: Symmetric(g1,g1,g2)
    c: Radius(g19) = 7
    c: DistanceY(g20,g11) = 170
    c: Radius(g15) = 5
    c: DistanceX(g11,g11) = 50
    c: Equal(g9,g8)
    c: Equal(g9,g6)
    c: Coincident(g21,g7)
    c: PointOnObject(g20,g21)
    c: Diameter(g21) = 225
    c: Vertical(g22)
    c: Vertical(g23)
    c: Vertical(g24)
    c: Vertical(g25)
    c: Equal(g5,g8)
    c: Equal(g10,g12)
    c: Tangent(g7,g26) = -1.5708
    c: Tangent(g23,g26) = 1.5708
    c: Tangent(g23,g27) = 1.5708
    c: Tangent(g6,g27) = 1.5708
    c: Tangent(g7,g28) = -1.5708
    c: Tangent(g24,g28) = 1.5708
    c: Tangent(g24,g29) = 1.5708
    c: Tangent(g5,g29) = -1.5708
    c: Equal(g29,g27)
    c: Radius(g27) = 2
    c: Equal(g26,g28)
    c: Radius(g26) = 2
    c: Tangent(g9,g30) = -1.5708
    c: Tangent(g22,g30) = -1.5708
    c: Tangent(g22,g31) = -1.5708
    c: Tangent(g12,g31) = 1.5708
    c: Tangent(g8,g32) = 1.5708
    c: Tangent(g25,g32) = 1.5708
    c: Tangent(g10,g33) = 1.5708
    c: Tangent(g25,g33) = 1.5708
    c: Equal(g30,g32)
    c: Equal(g31,g33)
    c: DistanceY(g23,g23) = 2
    c: DistanceY(g22,g22) = 15
    c: DistanceY(g6,g9) = 48
    c: DistanceX(g24,g23) = 155
    c: Radius(g30) = 2
    c: Radius(g31) = 2
    c: Coincident(g34,g22)
    c: Coincident(g34,g23)
    c: Coincident(g35,g25)
    c: Coincident(g35,g24)
    c: Coincident(g37,g28)
    c: Coincident(g37,g33)
    c: Coincident(g36,g31)
    c: Coincident(g36,g26)
FEATURE [PartDesign::Plane] DatumPlane003  label="Datum_ShellTot001"
  AttachmentOffset = pos=(0,0,42) rot=(0,0,1;0rad)
  Length = 90.6584
  MapMode = 5
  Placement = pos=(0,0,42) rot=(0,0,1;0rad)
  ResizeMode = 0
  Support = -> [XY_Plane002]
  Width = 85.9187
  expr: .AttachmentOffset.Base.z = <<params>>.shell_totheight
FEATURE [Sketcher::SketchObject] Sketch006  label="Sketch_Shell_Top001"
  FullyConstrained = true
  MapMode = 5
  Placement = pos=(0,0,42) rot=(0,0,1;0rad)
  Support = -> [DatumPlane003]
  expr: Constraints[123] = <<params>>.shell_overhang_leng
  expr: Constraints[119] = Spreadsheet.shell_overhang_leng
  expr: Constraints[80] = <<params>>.std_rad
  expr: Constraints[77] = <<params>>.back_vert_edge
  expr: Constraints[120] = Spreadsheet.shell_overhang_leng
  expr: Constraints[63] = <<params>>.std_rad
  expr: Constraints[81] = <<params>>.std_rad
  expr: Constraints[88] = Spreadsheet.shell_overhang_leng
  expr: Constraints[40] = <<params>>.plate_length
  expr: Constraints[65] = <<params>>.std_rad
  expr: Constraints[42] = <<params>>.tail_width
  expr: Constraints[78] = <<params>>.wheel_well_clearance
  expr: Constraints[79] = <<params>>.plate_width
  expr: Constraints[36] = <<params>>.wheel_well_plate_width - 2 * Spreadsheet.shell_overhang_leng
  expr: Constraints[47] = <<params>>.front_diameter
  expr: Constraints[76] = <<params>>.front_vert_edge
  expr: Constraints[41] = <<params>>.tail_rad
  sketch-geometry (52):
    g0: LineSegment StartX=-43.5 StartY=17 StartZ=0 EndX=-43.5 EndY=-17 EndZ=0
    g1: LineSegment StartX=43.5 StartY=17 StartZ=0 EndX=43.5 EndY=-17 EndZ=0
    g2: LineSegment StartX=-43.5 StartY=0 StartZ=0 EndX=43.5 EndY=0 EndZ=0
    g3: LineSegment StartX=-50.5 StartY=-24 StartZ=0 EndX=50.5 EndY=-24 EndZ=0
    g4: LineSegment StartX=-50.5 StartY=24 StartZ=0 EndX=50.5 EndY=24 EndZ=0
    g5: LineSegment StartX=-50.5 StartY=-24 StartZ=0 EndX=-75.5 EndY=-24 EndZ=0
    g6: LineSegment StartX=50.5 StartY=-24 StartZ=0 EndX=75.5 EndY=-24 EndZ=0
    g7: ArcOfCircle CenterX=0 CenterY=52.6846 CenterZ=0 NormalX=0 NormalY=0 NormalZ=1 AngleXU=0 Radius=112.5 StartAngle=3.96017 EndAngle=5.4646
    g8: LineSegment StartX=-50.5 StartY=24 StartZ=0 EndX=-75.5 EndY=24 EndZ=0
    g9: LineSegment StartX=50.5 StartY=24 StartZ=0 EndX=75.5 EndY=24 EndZ=0
    g10: LineSegment StartX=-77.1162 StartY=42.1781 StartZ=0 EndX=-29.0404 EndY=108.13 EndZ=0
    g11: LineSegment StartX=-25 StartY=110.185 StartZ=0 EndX=25 EndY=110.185 EndZ=0
    g12: LineSegment StartX=29.0404 StartY=108.13 StartZ=0 EndX=77.1162 EndY=42.1781 EndZ=0
    g13: LineSegment StartX=0 StartY=0 StartZ=0 EndX=0 EndY=110.185 EndZ=0
    g14: ArcOfCircle CenterX=-25 CenterY=105.185 CenterZ=0 NormalX=0 NormalY=0 NormalZ=1 AngleXU=0 Radius=5 StartAngle=1.5708 EndAngle=2.5117
    g15: ArcOfCircle CenterX=25 CenterY=105.185 CenterZ=0 NormalX=0 NormalY=0 NormalZ=1 AngleXU=0 Radius=5 StartAngle=0.629894 EndAngle=1.5708
    g16: ArcOfCircle CenterX=-50.5 CenterY=17 CenterZ=0 NormalX=0 NormalY=0 NormalZ=1 AngleXU=0 Radius=7 StartAngle=0 EndAngle=1.5708
    g17: ArcOfCircle CenterX=-50.5 CenterY=-17 CenterZ=0 NormalX=0 NormalY=0 NormalZ=1 AngleXU=0 Radius=7 StartAngle=4.71239 EndAngle=6.28319
    g18: ArcOfCircle CenterX=50.5 CenterY=-17 CenterZ=0 NormalX=0 NormalY=0 NormalZ=1 AngleXU=0 Radius=7 StartAngle=3.14159 EndAngle=4.71239
    g19: ArcOfCircle CenterX=50.5 CenterY=17 CenterZ=0 NormalX=0 NormalY=0 NormalZ=1 AngleXU=0 Radius=7 StartAngle=1.5708 EndAngle=3.14159
    g20: GeomPoint X=0 Y=-59.8154 Z=0
    g21: Circle CenterX=0 CenterY=52.6846 CenterZ=0 NormalX=0 NormalY=0 NormalZ=1 AngleXU=0 Radius=112.5
    g22: LineSegment StartX=77.5 StartY=26 StartZ=0 EndX=77.5 EndY=41 EndZ=0
    g23: LineSegment StartX=77.5 StartY=-26 StartZ=0 EndX=77.5 EndY=-28 EndZ=0
    g24: LineSegment StartX=-77.5 StartY=-28 StartZ=0 EndX=-77.5 EndY=-26 EndZ=0
    g25: LineSegment StartX=-77.5 StartY=26 StartZ=0 EndX=-77.5 EndY=41 EndZ=0
    g26: ArcOfCircle CenterX=75.5 CenterY=-28 CenterZ=0 NormalX=0 NormalY=0 NormalZ=1 AngleXU=0 Radius=2 StartAngle=5.4646 EndAngle=6.28319
    g27: ArcOfCircle CenterX=75.5 CenterY=-26 CenterZ=0 NormalX=0 NormalY=0 NormalZ=1 AngleXU=0 Radius=2 StartAngle=0 EndAngle=1.5708
    g28: ArcOfCircle CenterX=-75.5 CenterY=-28 CenterZ=0 NormalX=0 NormalY=0 NormalZ=1 AngleXU=0 Radius=2 StartAngle=3.14159 EndAngle=3.96017
    g29: ArcOfCircle CenterX=-75.5 CenterY=-26 CenterZ=0 NormalX=0 NormalY=0 NormalZ=1 AngleXU=0 Radius=2 StartAngle=1.5708 EndAngle=3.14159
    g30: ArcOfCircle CenterX=75.5 CenterY=26 CenterZ=0 NormalX=0 NormalY=0 NormalZ=1 AngleXU=0 Radius=2 StartAngle=4.71239 EndAngle=6.28319
    g31: ArcOfCircle CenterX=75.5 CenterY=41 CenterZ=0 NormalX=0 NormalY=0 NormalZ=1 AngleXU=0 Radius=2 StartAngle=4e-16 EndAngle=0.629894
    g32: ArcOfCircle CenterX=-75.5 CenterY=26 CenterZ=0 NormalX=0 NormalY=0 NormalZ=1 AngleXU=0 Radius=2 StartAngle=3.14159 EndAngle=4.71239
    g33: ArcOfCircle CenterX=-75.5 CenterY=41 CenterZ=0 NormalX=0 NormalY=0 NormalZ=1 AngleXU=0 Radius=2 StartAngle=2.5117 EndAngle=3.14159
    g34: LineSegment StartX=77.5 StartY=26 StartZ=0 EndX=77.5 EndY=-26 EndZ=0
    g35: LineSegment StartX=-77.5 StartY=26 StartZ=0 EndX=-77.5 EndY=-26 EndZ=0
    g36: LineSegment StartX=-17.8805 StartY=96.1846 StartZ=0 EndX=17.8805 EndY=96.1846 EndZ=0
    g37: GeomPoint X=0 Y=96.1846 Z=0
    g38: LineSegment StartX=-21.921 StartY=94.1299 StartZ=0 EndX=-63.1162 EndY=37.617 EndZ=0
    g39: LineSegment StartX=-63.5 StartY=36.4389 StartZ=0 EndX=-63.5 EndY=-24 EndZ=0
    g40: LineSegment StartX=21.921 StartY=94.1299 StartZ=0 EndX=63.1162 EndY=37.617 EndZ=0
    g41: LineSegment StartX=63.5 StartY=36.4389 StartZ=0 EndX=63.5 EndY=-24 EndZ=0
    g42: ArcOfCircle CenterX=0 CenterY=61.5293 CenterZ=0 NormalX=0 NormalY=0 NormalZ=1 AngleXU=0 Radius=107.345 StartAngle=4.08899 EndAngle=5.33579
    g43: LineSegment StartX=-63.5 StartY=36.4389 StartZ=0 EndX=63.5 EndY=36.4389 EndZ=0
    g44: GeomPoint X=0 Y=-45.8154 Z=0
    g45: ArcOfCircle CenterX=-17.8805 CenterY=91.1846 CenterZ=0 NormalX=0 NormalY=0 NormalZ=1 AngleXU=0 Radius=5 StartAngle=1.5708 EndAngle=2.5117
    g46: ArcOfCircle CenterX=17.8805 CenterY=91.1846 CenterZ=0 NormalX=0 NormalY=0 NormalZ=1 AngleXU=0 Radius=5 StartAngle=0.629894 EndAngle=1.5708
    g47: ArcOfCircle CenterX=61.5 CenterY=36.4389 CenterZ=0 NormalX=0 NormalY=0 NormalZ=1 AngleXU=0 Radius=2 StartAngle=-9e-16 EndAngle=0.629894
    g48: ArcOfCircle CenterX=-61.5 CenterY=36.4389 CenterZ=0 NormalX=0 NormalY=0 NormalZ=1 AngleXU=0 Radius=2 StartAngle=2.5117 EndAngle=3.14159
    g49: ArcOfCircle CenterX=61.5 CenterY=-24 CenterZ=0 NormalX=0 NormalY=0 NormalZ=1 AngleXU=0 Radius=2 StartAngle=5.33579 EndAngle=6.28319
    g50: ArcOfCircle CenterX=-61.5 CenterY=-24 CenterZ=0 NormalX=0 NormalY=0 NormalZ=1 AngleXU=0 Radius=2 StartAngle=3.14159 EndAngle=4.08899
    g51: LineSegment StartX=-29.0404 StartY=108.13 StartZ=0 EndX=-17.7272 EndY=99.883 EndZ=0
  constraints (125):
    c: Vertical(g0)
    c: Vertical(g1)
    c: Horizontal(g2)
    c: Symmetric(g2,g2,g-1)
    c: Horizontal(g3)
    c: Horizontal(g5)
    c: Horizontal(g6)
    c: PointOnObject(g7,g-2)
    c: Horizontal(g8)
    c: Horizontal(g9)
    c: Horizontal(g11)
    c: Coincident(g13,g-1)
    c: PointOnObject(g13,g-2)
    c: Tangent(g10,g14) = 1.5708
    c: Tangent(g11,g14) = 1.5708
    c: Tangent(g11,g15) = 1.5708
    c: Tangent(g12,g15) = 1.5708
    c: Tangent(g8,g16) = -1.5708
    c: Tangent(g0,g16) = 1.5708
    c: Tangent(g5,g17) = 1.5708
    c: Tangent(g0,g17) = 1.5708
    c: Tangent(g1,g18) = -1.5708
    c: Tangent(g6,g18) = -1.5708
    c: Tangent(g1,g19) = -1.5708
    c: Tangent(g9,g19) = 1.5708
    c: Equal(g15,g14)
    c: Symmetric(g11,g11,g13)
    c: Equal(g18,g19)
    c: Equal(g19,g16)
    c: Equal(g16,g17)
    c: PointOnObject(g20,g-2)
    c: PointOnObject(g20,g7)
    c: Coincident(g4,g8)
    c: Coincident(g4,g9)
    c: Coincident(g3,g6)
    c: Coincident(g3,g5)
    c: DistanceX(g2,g2) = 87
    c: Symmetric(g0,g0,g2)
    c: Symmetric(g1,g1,g2)
    c: Radius(g19) = 7
    c: DistanceY(g20,g11) = 170
    c: Radius(g15) = 5
    c: DistanceX(g11,g11) = 50
    c: Equal(g9,g8)
    c: Equal(g9,g6)
    c: Coincident(g21,g7)
    c: PointOnObject(g20,g21)
    c: Diameter(g21) = 225
    c: Vertical(g22)
    c: Vertical(g23)
    c: Vertical(g24)
    c: Vertical(g25)
    c: Equal(g5,g8)
    c: Equal(g10,g12)
    c: Tangent(g7,g26) = -1.5708
    c: Tangent(g23,g26) = 1.5708
    c: Tangent(g23,g27) = 1.5708
    c: Tangent(g6,g27) = 1.5708
    c: Tangent(g7,g28) = -1.5708
    c: Tangent(g24,g28) = 1.5708
    c: Tangent(g24,g29) = 1.5708
    c: Tangent(g5,g29) = -1.5708
    c: Equal(g29,g27)
    c: Radius(g27) = 2
    c: Equal(g26,g28)
    c: Radius(g26) = 2
    c: Tangent(g9,g30) = -1.5708
    c: Tangent(g22,g30) = -1.5708
    c: Tangent(g22,g31) = -1.5708
    c: Tangent(g12,g31) = 1.5708
    c: Tangent(g8,g32) = 1.5708
    c: Tangent(g25,g32) = 1.5708
    c: Tangent(g10,g33) = 1.5708
    c: Tangent(g25,g33) = 1.5708
    c: Equal(g30,g32)
    c: Equal(g31,g33)
    c: DistanceY(g23,g23) = 2
    c: DistanceY(g22,g22) = 15
    c: DistanceY(g6,g9) = 48
    c: DistanceX(g24,g23) = 155
    c: Radius(g30) = 2
    c: Radius(g31) = 2
    c: Coincident(g34,g22)
    c: Coincident(g34,g23)
    c: Coincident(g35,g25)
    c: Coincident(g35,g24)
    c: Horizontal(g36)
    c: PointOnObject(g37,g13)
    c: DistanceY(g37,g13) = 14
    c: Vertical(g39)
    c: Vertical(g41)
    c: PointOnObject(g42,g13)
    c: Horizontal(g43)
    c: Parallel(g40,g12)
    c: PointOnObject(g44,g-2)
    c: PointOnObject(g44,g42)
    c: Tangent(g38,g45) = -1.5708
    c: Tangent(g36,g45) = 1.5708
    c: Tangent(g40,g46) = 1.5708
    c: Tangent(g36,g46) = 1.5708
    c: Tangent(g41,g47) = 1.5708
    c: Tangent(g40,g47) = 1.5708
    c: Tangent(g39,g48) = -1.5708
    c: Tangent(g38,g48) = -1.5708
    c: Tangent(g42,g49) = -1.5708
    c: Tangent(g41,g49) = 1.5708
    c: Tangent(g42,g50) = -1.5708
    c: Tangent(g39,g50) = -1.5708
    c: Coincident(g43,g39)
    c: Coincident(g43,g41)
    c: Equal(g15,g46)
    c: Equal(g46,g45)
    c: Symmetric(g36,g36,g37)
    c: Equal(g31,g47)
    c: Equal(g26,g49)
    c: Equal(g50,g29)
    c: Equal(g48,g32)
    c: PointOnObject(g41,g6)
    c: PointOnObject(g50,g5)
    c: DistanceY(g20,g44) = 14
    c: DistanceX(g41,g22) = 14
    c: PointOnObject(g51,g38)
    c: Perpendicular(g38,g51)
    c: Distance(g51) = 14
    c: Coincident(g51,g10)
FEATURE [PartDesign::Pad] Pad001  label="Pad_Plug"
  Direction = (1,1,1)
  Length = 85
  Length2 = 100
  Placement = pos=(0,0,0) rot=(1,0,0;1.5708rad)
  Profile = -> Sketch004
  Type = 0
  expr: Length = <<params>>.plate_length / 2
FEATURE [PartDesign::SubtractiveLoft] SubtractiveLoft
  BaseFeature = -> Pad
  Closed = false
  Placement = pos=(0,0,0) rot=(1,0,0;1.5708rad)
  Profile = -> Sketch002
  Ruled = false
  Sections = -> [Sketch003]
FEATURE [Sketcher::SketchObject] Sketch009  label="Sketch_Shell_Top003"
  FullyConstrained = true
  MapMode = 5
  Placement = pos=(0,0,42) rot=(0,0,1;0rad)
  Support = -> [DatumPlane003]
  expr: Constraints[41] = <<params>>.tail_rad
  expr: Constraints[76] = <<params>>.front_vert_edge
  expr: Constraints[47] = <<params>>.front_diameter
  expr: Constraints[36] = <<params>>.wheel_well_plate_width - 2 * Spreadsheet.shell_overhang_leng
  expr: Constraints[79] = <<params>>.plate_width
  expr: Constraints[42] = <<params>>.tail_width
  expr: Constraints[78] = <<params>>.wheel_well_clearance
  expr: Constraints[65] = <<params>>.std_rad
  expr: Constraints[40] = <<params>>.plate_length
  expr: Constraints[88] = Spreadsheet.shell_overhang_leng
  expr: Constraints[81] = <<params>>.std_rad
  expr: Constraints[63] = <<params>>.std_rad
  expr: Constraints[77] = <<params>>.back_vert_edge
  expr: Constraints[120] = Spreadsheet.shell_overhang_leng
  expr: Constraints[80] = <<params>>.std_rad
  expr: Constraints[119] = Spreadsheet.shell_overhang_leng
  expr: Constraints[123] = <<params>>.shell_overhang_leng
  sketch-geometry (52):
    g0: LineSegment StartX=-43.5 StartY=17 StartZ=0 EndX=-43.5 EndY=-17 EndZ=0
    g1: LineSegment StartX=43.5 StartY=17 StartZ=0 EndX=43.5 EndY=-17 EndZ=0
    g2: LineSegment StartX=-43.5 StartY=0 StartZ=0 EndX=43.5 EndY=0 EndZ=0
    g3: LineSegment StartX=-50.5 StartY=-24 StartZ=0 EndX=50.5 EndY=-24 EndZ=0
    g4: LineSegment StartX=-50.5 StartY=24 StartZ=0 EndX=50.5 EndY=24 EndZ=0
    g5: LineSegment StartX=-50.5 StartY=-24 StartZ=0 EndX=-75.5 EndY=-24 EndZ=0
    g6: LineSegment StartX=50.5 StartY=-24 StartZ=0 EndX=75.5 EndY=-24 EndZ=0
    g7: ArcOfCircle CenterX=0 CenterY=52.6846 CenterZ=0 NormalX=0 NormalY=0 NormalZ=1 AngleXU=0 Radius=112.5 StartAngle=3.96017 EndAngle=5.4646
    g8: LineSegment StartX=-50.5 StartY=24 StartZ=0 EndX=-75.5 EndY=24 EndZ=0
    g9: LineSegment StartX=50.5 StartY=24 StartZ=0 EndX=75.5 EndY=24 EndZ=0
    g10: LineSegment StartX=-77.1162 StartY=42.1781 StartZ=0 EndX=-29.0404 EndY=108.13 EndZ=0
    g11: LineSegment StartX=-25 StartY=110.185 StartZ=0 EndX=25 EndY=110.185 EndZ=0
    g12: LineSegment StartX=29.0404 StartY=108.13 StartZ=0 EndX=77.1162 EndY=42.1781 EndZ=0
    g13: LineSegment StartX=0 StartY=0 StartZ=0 EndX=0 EndY=110.185 EndZ=0
    g14: ArcOfCircle CenterX=-25 CenterY=105.185 CenterZ=0 NormalX=0 NormalY=0 NormalZ=1 AngleXU=0 Radius=5 StartAngle=1.5708 EndAngle=2.5117
    g15: ArcOfCircle CenterX=25 CenterY=105.185 CenterZ=0 NormalX=0 NormalY=0 NormalZ=1 AngleXU=0 Radius=5 StartAngle=0.629894 EndAngle=1.5708
    g16: ArcOfCircle CenterX=-50.5 CenterY=17 CenterZ=0 NormalX=0 NormalY=0 NormalZ=1 AngleXU=0 Radius=7 StartAngle=0 EndAngle=1.5708
    g17: ArcOfCircle CenterX=-50.5 CenterY=-17 CenterZ=0 NormalX=0 NormalY=0 NormalZ=1 AngleXU=0 Radius=7 StartAngle=4.71239 EndAngle=6.28319
    g18: ArcOfCircle CenterX=50.5 CenterY=-17 CenterZ=0 NormalX=0 NormalY=0 NormalZ=1 AngleXU=0 Radius=7 StartAngle=3.14159 EndAngle=4.71239
    g19: ArcOfCircle CenterX=50.5 CenterY=17 CenterZ=0 NormalX=0 NormalY=0 NormalZ=1 AngleXU=0 Radius=7 StartAngle=1.5708 EndAngle=3.14159
    g20: GeomPoint X=0 Y=-59.8154 Z=0
    g21: Circle CenterX=0 CenterY=52.6846 CenterZ=0 NormalX=0 NormalY=0 NormalZ=1 AngleXU=0 Radius=112.5
    g22: LineSegment StartX=77.5 StartY=26 StartZ=0 EndX=77.5 EndY=41 EndZ=0
    g23: LineSegment StartX=77.5 StartY=-26 StartZ=0 EndX=77.5 EndY=-28 EndZ=0
    g24: LineSegment StartX=-77.5 StartY=-28 StartZ=0 EndX=-77.5 EndY=-26 EndZ=0
    g25: LineSegment StartX=-77.5 StartY=26 StartZ=0 EndX=-77.5 EndY=41 EndZ=0
    g26: ArcOfCircle CenterX=75.5 CenterY=-28 CenterZ=0 NormalX=0 NormalY=0 NormalZ=1 AngleXU=0 Radius=2 StartAngle=5.4646 EndAngle=6.28319
    g27: ArcOfCircle CenterX=75.5 CenterY=-26 CenterZ=0 NormalX=0 NormalY=0 NormalZ=1 AngleXU=0 Radius=2 StartAngle=-9e-16 EndAngle=1.5708
    g28: ArcOfCircle CenterX=-75.5 CenterY=-28 CenterZ=0 NormalX=0 NormalY=0 NormalZ=1 AngleXU=0 Radius=2 StartAngle=3.14159 EndAngle=3.96017
    g29: ArcOfCircle CenterX=-75.5 CenterY=-26 CenterZ=0 NormalX=0 NormalY=0 NormalZ=1 AngleXU=0 Radius=2 StartAngle=1.5708 EndAngle=3.14159
    g30: ArcOfCircle CenterX=75.5 CenterY=26 CenterZ=0 NormalX=0 NormalY=0 NormalZ=1 AngleXU=0 Radius=2 StartAngle=4.71239 EndAngle=6.28319
    g31: ArcOfCircle CenterX=75.5 CenterY=41 CenterZ=0 NormalX=0 NormalY=0 NormalZ=1 AngleXU=0 Radius=2 StartAngle=0 EndAngle=0.629894
    g32: ArcOfCircle CenterX=-75.5 CenterY=26 CenterZ=0 NormalX=0 NormalY=0 NormalZ=1 AngleXU=0 Radius=2 StartAngle=3.14159 EndAngle=4.71239
    g33: ArcOfCircle CenterX=-75.5 CenterY=41 CenterZ=0 NormalX=0 NormalY=0 NormalZ=1 AngleXU=0 Radius=2 StartAngle=2.5117 EndAngle=3.14159
    g34: LineSegment StartX=77.5 StartY=26 StartZ=0 EndX=77.5 EndY=-26 EndZ=0
    g35: LineSegment StartX=-77.5 StartY=26 StartZ=0 EndX=-77.5 EndY=-26 EndZ=0
    g36: LineSegment StartX=-17.8805 StartY=96.1846 StartZ=0 EndX=17.8805 EndY=96.1846 EndZ=0
    g37: GeomPoint X=0 Y=96.1846 Z=0
    g38: LineSegment StartX=-21.921 StartY=94.1299 StartZ=0 EndX=-63.1162 EndY=37.617 EndZ=0
    g39: LineSegment StartX=-63.5 StartY=36.4389 StartZ=0 EndX=-63.5 EndY=-24 EndZ=0
    g40: LineSegment StartX=21.921 StartY=94.1299 StartZ=0 EndX=63.1162 EndY=37.617 EndZ=0
    g41: LineSegment StartX=63.5 StartY=36.4389 StartZ=0 EndX=63.5 EndY=-24 EndZ=0
    g42: ArcOfCircle CenterX=0 CenterY=61.5293 CenterZ=0 NormalX=0 NormalY=0 NormalZ=1 AngleXU=0 Radius=107.345 StartAngle=4.08899 EndAngle=5.33579
    g43: LineSegment StartX=-63.5 StartY=36.4389 StartZ=0 EndX=63.5 EndY=36.4389 EndZ=0
    g44: GeomPoint X=0 Y=-45.8154 Z=0
    g45: ArcOfCircle CenterX=-17.8805 CenterY=91.1846 CenterZ=0 NormalX=0 NormalY=0 NormalZ=1 AngleXU=0 Radius=5 StartAngle=1.5708 EndAngle=2.5117
    g46: ArcOfCircle CenterX=17.8805 CenterY=91.1846 CenterZ=0 NormalX=0 NormalY=0 NormalZ=1 AngleXU=0 Radius=5 StartAngle=0.629894 EndAngle=1.5708
    g47: ArcOfCircle CenterX=61.5 CenterY=36.4389 CenterZ=0 NormalX=0 NormalY=0 NormalZ=1 AngleXU=0 Radius=2 StartAngle=-9e-16 EndAngle=0.629894
    g48: ArcOfCircle CenterX=-61.5 CenterY=36.4389 CenterZ=0 NormalX=0 NormalY=0 NormalZ=1 AngleXU=0 Radius=2 StartAngle=2.5117 EndAngle=3.14159
    g49: ArcOfCircle CenterX=61.5 CenterY=-24 CenterZ=0 NormalX=0 NormalY=0 NormalZ=1 AngleXU=0 Radius=2 StartAngle=5.33579 EndAngle=6.28319
    g50: ArcOfCircle CenterX=-61.5 CenterY=-24 CenterZ=0 NormalX=0 NormalY=0 NormalZ=1 AngleXU=0 Radius=2 StartAngle=3.14159 EndAngle=4.08899
    g51: LineSegment StartX=-29.0404 StartY=108.13 StartZ=0 EndX=-17.7272 EndY=99.883 EndZ=0
  constraints (125):
    c: Vertical(g0)
    c: Vertical(g1)
    c: Horizontal(g2)
    c: Symmetric(g2,g2,g-1)
    c: Horizontal(g3)
    c: Horizontal(g5)
    c: Horizontal(g6)
    c: PointOnObject(g7,g-2)
    c: Horizontal(g8)
    c: Horizontal(g9)
    c: Horizontal(g11)
    c: Coincident(g13,g-1)
    c: PointOnObject(g13,g-2)
    c: Tangent(g10,g14) = 1.5708
    c: Tangent(g11,g14) = 1.5708
    c: Tangent(g11,g15) = 1.5708
    c: Tangent(g12,g15) = 1.5708
    c: Tangent(g8,g16) = -1.5708
    c: Tangent(g0,g16) = 1.5708
    c: Tangent(g5,g17) = 1.5708
    c: Tangent(g0,g17) = 1.5708
    c: Tangent(g1,g18) = -1.5708
    c: Tangent(g6,g18) = -1.5708
    c: Tangent(g1,g19) = -1.5708
    c: Tangent(g9,g19) = 1.5708
    c: Equal(g15,g14)
    c: Symmetric(g11,g11,g13)
    c: Equal(g18,g19)
    c: Equal(g19,g16)
    c: Equal(g16,g17)
    c: PointOnObject(g20,g-2)
    c: PointOnObject(g20,g7)
    c: Coincident(g4,g8)
    c: Coincident(g4,g9)
    c: Coincident(g3,g6)
    c: Coincident(g3,g5)
    c: DistanceX(g2,g2) = 87
    c: Symmetric(g0,g0,g2)
    c: Symmetric(g1,g1,g2)
    c: Radius(g19) = 7
    c: DistanceY(g20,g11) = 170
    c: Radius(g15) = 5
    c: DistanceX(g11,g11) = 50
    c: Equal(g9,g8)
    c: Equal(g9,g6)
    c: Coincident(g21,g7)
    c: PointOnObject(g20,g21)
    c: Diameter(g21) = 225
    c: Vertical(g22)
    c: Vertical(g23)
    c: Vertical(g24)
    c: Vertical(g25)
    c: Equal(g5,g8)
    c: Equal(g10,g12)
    c: Tangent(g7,g26) = -1.5708
    c: Tangent(g23,g26) = 1.5708
    c: Tangent(g23,g27) = 1.5708
    c: Tangent(g6,g27) = 1.5708
    c: Tangent(g7,g28) = -1.5708
    c: Tangent(g24,g28) = 1.5708
    c: Tangent(g24,g29) = 1.5708
    c: Tangent(g5,g29) = -1.5708
    c: Equal(g29,g27)
    c: Radius(g27) = 2
    c: Equal(g26,g28)
    c: Radius(g26) = 2
    c: Tangent(g9,g30) = -1.5708
    c: Tangent(g22,g30) = -1.5708
    c: Tangent(g22,g31) = -1.5708
    c: Tangent(g12,g31) = 1.5708
    c: Tangent(g8,g32) = 1.5708
    c: Tangent(g25,g32) = 1.5708
    c: Tangent(g10,g33) = 1.5708
    c: Tangent(g25,g33) = 1.5708
    c: Equal(g30,g32)
    c: Equal(g31,g33)
    c: DistanceY(g23,g23) = 2
    c: DistanceY(g22,g22) = 15
    c: DistanceY(g6,g9) = 48
    c: DistanceX(g24,g23) = 155
    c: Radius(g30) = 2
    c: Radius(g31) = 2
    c: Coincident(g34,g22)
    c: Coincident(g34,g23)
    c: Coincident(g35,g25)
    c: Coincident(g35,g24)
    c: Horizontal(g36)
    c: PointOnObject(g37,g13)
    c: DistanceY(g37,g13) = 14
    c: Vertical(g39)
    c: Vertical(g41)
    c: PointOnObject(g42,g13)
    c: Horizontal(g43)
    c: Parallel(g40,g12)
    c: PointOnObject(g44,g-2)
    c: PointOnObject(g44,g42)
    c: Tangent(g38,g45) = -1.5708
    c: Tangent(g36,g45) = 1.5708
    c: Tangent(g40,g46) = 1.5708
    c: Tangent(g36,g46) = 1.5708
    c: Tangent(g41,g47) = 1.5708
    c: Tangent(g40,g47) = 1.5708
    c: Tangent(g39,g48) = -1.5708
    c: Tangent(g38,g48) = -1.5708
    c: Tangent(g42,g49) = -1.5708
    c: Tangent(g41,g49) = 1.5708
    c: Tangent(g42,g50) = -1.5708
    c: Tangent(g39,g50) = -1.5708
    c: Coincident(g43,g39)
    c: Coincident(g43,g41)
    c: Equal(g15,g46)
    c: Equal(g46,g45)
    c: Symmetric(g36,g36,g37)
    c: Equal(g31,g47)
    c: Equal(g26,g49)
    c: Equal(g50,g29)
    c: Equal(g48,g32)
    c: PointOnObject(g41,g6)
    c: PointOnObject(g50,g5)
    c: DistanceY(g20,g44) = 14
    c: DistanceX(g41,g22) = 14
    c: PointOnObject(g51,g38)
    c: Perpendicular(g38,g51)
    c: Distance(g51) = 14
    c: Coincident(g51,g10)
FEATURE [Sketcher::SketchObject] Sketch010  label="Sketch_Shell_Vert003"
  FullyConstrained = true
  MapMode = 5
  Placement = pos=(0,0,10) rot=(0,0,1;0rad)
  Support = -> [DatumPlane002]
  expr: Constraints[40] = <<params>>.plate_length
  expr: Constraints[65] = <<params>>.std_rad
  expr: Constraints[42] = <<params>>.tail_width
  expr: Constraints[78] = <<params>>.wheel_well_clearance
  expr: Constraints[79] = <<params>>.plate_width
  expr: Constraints[36] = <<params>>.wheel_well_plate_width
  expr: Constraints[47] = <<params>>.front_diameter
  expr: Constraints[63] = <<params>>.std_rad
  expr: Constraints[76] = <<params>>.front_vert_edge
  expr: Constraints[77] = <<params>>.back_vert_edge
  expr: Constraints[80] = <<params>>.std_rad
  expr: Constraints[81] = <<params>>.std_rad
  expr: Constraints[41] = <<params>>.tail_rad
  sketch-geometry (38):
    g0: LineSegment StartX=-57.5 StartY=17 StartZ=0 EndX=-57.5 EndY=-17 EndZ=0
    g1: LineSegment StartX=57.5 StartY=17 StartZ=0 EndX=57.5 EndY=-17 EndZ=0
    g2: LineSegment StartX=-57.5 StartY=0 StartZ=0 EndX=57.5 EndY=0 EndZ=0
    g3: LineSegment StartX=-64.5 StartY=-24 StartZ=0 EndX=64.5 EndY=-24 EndZ=0
    g4: LineSegment StartX=-64.5 StartY=24 StartZ=0 EndX=64.5 EndY=24 EndZ=0
    g5: LineSegment StartX=-64.5 StartY=-24 StartZ=0 EndX=-75.5 EndY=-24 EndZ=0
    g6: LineSegment StartX=64.5 StartY=-24 StartZ=0 EndX=75.5 EndY=-24 EndZ=0
    g7: ArcOfCircle CenterX=0 CenterY=52.6846 CenterZ=0 NormalX=0 NormalY=0 NormalZ=1 AngleXU=0 Radius=112.5 StartAngle=3.96017 EndAngle=5.4646
    g8: LineSegment StartX=-64.5 StartY=24 StartZ=0 EndX=-75.5 EndY=24 EndZ=0
    g9: LineSegment StartX=64.5 StartY=24 StartZ=0 EndX=75.5 EndY=24 EndZ=0
    g10: LineSegment StartX=-77.1162 StartY=42.1781 StartZ=0 EndX=-29.0404 EndY=108.13 EndZ=0
    g11: LineSegment StartX=-25 StartY=110.185 StartZ=0 EndX=25 EndY=110.185 EndZ=0
    g12: LineSegment StartX=29.0404 StartY=108.13 StartZ=0 EndX=77.1162 EndY=42.1781 EndZ=0
    g13: LineSegment StartX=0 StartY=0 StartZ=0 EndX=0 EndY=110.185 EndZ=0
    g14: ArcOfCircle CenterX=-25 CenterY=105.185 CenterZ=0 NormalX=0 NormalY=0 NormalZ=1 AngleXU=0 Radius=5 StartAngle=1.5708 EndAngle=2.5117
    g15: ArcOfCircle CenterX=25 CenterY=105.185 CenterZ=0 NormalX=0 NormalY=0 NormalZ=1 AngleXU=0 Radius=5 StartAngle=0.629894 EndAngle=1.5708
    g16: ArcOfCircle CenterX=-64.5 CenterY=17 CenterZ=0 NormalX=0 NormalY=0 NormalZ=1 AngleXU=0 Radius=7 StartAngle=0 EndAngle=1.5708
    g17: ArcOfCircle CenterX=-64.5 CenterY=-17 CenterZ=0 NormalX=0 NormalY=0 NormalZ=1 AngleXU=0 Radius=7 StartAngle=4.71239 EndAngle=6.28319
    g18: ArcOfCircle CenterX=64.5 CenterY=-17 CenterZ=0 NormalX=0 NormalY=0 NormalZ=1 AngleXU=0 Radius=7 StartAngle=3.14159 EndAngle=4.71239
    g19: ArcOfCircle CenterX=64.5 CenterY=17 CenterZ=0 NormalX=0 NormalY=0 NormalZ=1 AngleXU=0 Radius=7 StartAngle=1.5708 EndAngle=3.14159
    g20: GeomPoint X=0 Y=-59.8154 Z=0
    g21: Circle CenterX=0 CenterY=52.6846 CenterZ=0 NormalX=0 NormalY=0 NormalZ=1 AngleXU=0 Radius=112.5
    g22: LineSegment StartX=77.5 StartY=26 StartZ=0 EndX=77.5 EndY=41 EndZ=0
    g23: LineSegment StartX=77.5 StartY=-26 StartZ=0 EndX=77.5 EndY=-28 EndZ=0
    g24: LineSegment StartX=-77.5 StartY=-28 StartZ=0 EndX=-77.5 EndY=-26 EndZ=0
    g25: LineSegment StartX=-77.5 StartY=26 StartZ=0 EndX=-77.5 EndY=41 EndZ=0
    g26: ArcOfCircle CenterX=75.5 CenterY=-28 CenterZ=0 NormalX=0 NormalY=0 NormalZ=1 AngleXU=0 Radius=2 StartAngle=5.4646 EndAngle=6.28319
    g27: ArcOfCircle CenterX=75.5 CenterY=-26 CenterZ=0 NormalX=0 NormalY=0 NormalZ=1 AngleXU=0 Radius=2 StartAngle=-9e-16 EndAngle=1.5708
    g28: ArcOfCircle CenterX=-75.5 CenterY=-28 CenterZ=0 NormalX=0 NormalY=0 NormalZ=1 AngleXU=0 Radius=2 StartAngle=3.14159 EndAngle=3.96017
    g29: ArcOfCircle CenterX=-75.5 CenterY=-26 CenterZ=0 NormalX=0 NormalY=0 NormalZ=1 AngleXU=0 Radius=2 StartAngle=1.5708 EndAngle=3.14159
    g30: ArcOfCircle CenterX=75.5 CenterY=26 CenterZ=0 NormalX=0 NormalY=0 NormalZ=1 AngleXU=0 Radius=2 StartAngle=4.71239 EndAngle=6.28319
    g31: ArcOfCircle CenterX=75.5 CenterY=41 CenterZ=0 NormalX=0 NormalY=0 NormalZ=1 AngleXU=0 Radius=2 StartAngle=0 EndAngle=0.629894
    g32: ArcOfCircle CenterX=-75.5 CenterY=26 CenterZ=0 NormalX=0 NormalY=0 NormalZ=1 AngleXU=0 Radius=2 StartAngle=3.14159 EndAngle=4.71239
    g33: ArcOfCircle CenterX=-75.5 CenterY=41 CenterZ=0 NormalX=0 NormalY=0 NormalZ=1 AngleXU=0 Radius=2 StartAngle=2.5117 EndAngle=3.14159
    g34: LineSegment StartX=77.5 StartY=26 StartZ=0 EndX=77.5 EndY=-26 EndZ=0
    g35: LineSegment StartX=-77.5 StartY=26 StartZ=0 EndX=-77.5 EndY=-26 EndZ=0
    g36: LineSegment StartX=77.5 StartY=41 StartZ=0 EndX=77.5 EndY=-28 EndZ=0
    g37: LineSegment StartX=-77.5 StartY=41 StartZ=0 EndX=-77.5 EndY=-28 EndZ=0
  constraints (90):
    c: Vertical(g0)
    c: Vertical(g1)
    c: Horizontal(g2)
    c: Symmetric(g2,g2,g-1)
    c: Horizontal(g3)
    c: Horizontal(g5)
    c: Horizontal(g6)
    c: PointOnObject(g7,g-2)
    c: Horizontal(g8)
    c: Horizontal(g9)
    c: Horizontal(g11)
    c: Coincident(g13,g-1)
    c: PointOnObject(g13,g-2)
    c: Tangent(g10,g14) = 1.5708
    c: Tangent(g11,g14) = 1.5708
    c: Tangent(g11,g15) = 1.5708
    c: Tangent(g12,g15) = 1.5708
    c: Tangent(g8,g16) = -1.5708
    c: Tangent(g0,g16) = 1.5708
    c: Tangent(g5,g17) = 1.5708
    c: Tangent(g0,g17) = 1.5708
    c: Tangent(g1,g18) = -1.5708
    c: Tangent(g6,g18) = -1.5708
    c: Tangent(g1,g19) = -1.5708
    c: Tangent(g9,g19) = 1.5708
    c: Equal(g15,g14)
    c: Symmetric(g11,g11,g13)
    c: Equal(g18,g19)
    c: Equal(g19,g16)
    c: Equal(g16,g17)
    c: PointOnObject(g20,g-2)
    c: PointOnObject(g20,g7)
    c: Coincident(g4,g8)
    c: Coincident(g4,g9)
    c: Coincident(g3,g6)
    c: Coincident(g3,g5)
    c: DistanceX(g2,g2) = 115
    c: Symmetric(g0,g0,g2)
    c: Symmetric(g1,g1,g2)
    c: Radius(g19) = 7
    c: DistanceY(g20,g11) = 170
    c: Radius(g15) = 5
    c: DistanceX(g11,g11) = 50
    c: Equal(g9,g8)
    c: Equal(g9,g6)
    c: Coincident(g21,g7)
    c: PointOnObject(g20,g21)
    c: Diameter(g21) = 225
    c: Vertical(g22)
    c: Vertical(g23)
    c: Vertical(g24)
    c: Vertical(g25)
    c: Equal(g5,g8)
    c: Equal(g10,g12)
    c: Tangent(g7,g26) = -1.5708
    c: Tangent(g23,g26) = 1.5708
    c: Tangent(g23,g27) = 1.5708
    c: Tangent(g6,g27) = 1.5708
    c: Tangent(g7,g28) = -1.5708
    c: Tangent(g24,g28) = 1.5708
    c: Tangent(g24,g29) = 1.5708
    c: Tangent(g5,g29) = -1.5708
    c: Equal(g29,g27)
    c: Radius(g27) = 2
    c: Equal(g26,g28)
    c: Radius(g26) = 2
    c: Tangent(g9,g30) = -1.5708
    c: Tangent(g22,g30) = -1.5708
    c: Tangent(g22,g31) = -1.5708
    c: Tangent(g12,g31) = 1.5708
    c: Tangent(g8,g32) = 1.5708
    c: Tangent(g25,g32) = 1.5708
    c: Tangent(g10,g33) = 1.5708
    c: Tangent(g25,g33) = 1.5708
    c: Equal(g30,g32)
    c: Equal(g31,g33)
    c: DistanceY(g23,g23) = 2
    c: DistanceY(g22,g22) = 15
    c: DistanceY(g6,g9) = 48
    c: DistanceX(g24,g23) = 155
    c: Radius(g30) = 2
    c: Radius(g31) = 2
    c: Coincident(g34,g22)
    c: Coincident(g34,g23)
    c: Coincident(g35,g25)
    c: Coincident(g35,g24)
    c: Coincident(g37,g28)
    c: Coincident(g37,g33)
    c: Coincident(g36,g31)
    c: Coincident(g36,g26)
FEATURE [Sketcher::SketchObject] Sketch013  label="Sketch_ClipsToTrim"
  FullyConstrained = true
  MapMode = 5
  Placement = pos=(0,0,0) rot=(1,0,0;1.5708rad)
  Support = -> [XZ_Plane001]
  expr: Constraints[0] = <<params>>.xport_plug_plate_diam
  expr: Constraints[1] = <<params>>.xport_offset_loc
  expr: Constraints[2] = <<params>>.xport_height_loc
  sketch-geometry (1):
    g0: Circle CenterX=43 CenterY=33.25 CenterZ=0 NormalX=0 NormalY=0 NormalZ=1 AngleXU=0 Radius=8
  constraints (3):
    c: Diameter(g0) = 16
    c: DistanceX(g-1,g0) = 43
    c: DistanceY(g-1,g0) = 33.25
FEATURE [Sketcher::SketchObject] Sketch014  label="Sketch_Shell_Vert_CutPlug"
  FullyConstrained = true
  MapMode = 5
  Placement = pos=(0,0,10) rot=(0,0,1;0rad)
  Support = -> [DatumPlane]
  expr: Constraints[168] = <<params>>.xport_clip_size
  expr: Constraints[41] = <<params>>.tail_rad
  expr: Constraints[81] = <<params>>.std_rad
  expr: Constraints[100] = <<params>>.std_wall_thick
  expr: Constraints[76] = <<params>>.front_vert_edge
  expr: Constraints[118] = <<params>>.std_wall_thick
  expr: Constraints[79] = <<params>>.plate_width
  expr: Constraints[78] = <<params>>.wheel_well_clearance
  expr: Constraints[42] = <<params>>.tail_width
  expr: Constraints[135] = <<params>>.xport_plug_diam / 2
  expr: Constraints[65] = <<params>>.std_rad
  expr: Constraints[40] = <<params>>.plate_length
  expr: Constraints[36] = <<params>>.wheel_well_plate_width
  expr: Constraints[80] = <<params>>.std_rad
  expr: Constraints[101] = <<params>>.plate_length / 2 + <<params>>.std_wall_thick
  expr: Constraints[103] = <<params>>.xport_offset_loc
  expr: Constraints[63] = <<params>>.std_rad
  expr: Constraints[170] = <<params>>.xport_clip_size
  expr: Constraints[47] = <<params>>.front_diameter
  expr: Constraints[134] = <<params>>.xport_plug_diam / 2
  expr: Constraints[137] = <<params>>.shell_wall_thick + <<params>>.std_tol_clear
  expr: Constraints[77] = <<params>>.back_vert_edge
  expr: Constraints[110] = <<params>>.xport_plug_plate_thick
  sketch-geometry (68):
    g0: LineSegment StartX=-57.5 StartY=17 StartZ=0 EndX=-57.5 EndY=-17 EndZ=0
    g1: LineSegment StartX=57.5 StartY=17 StartZ=0 EndX=57.5 EndY=-17 EndZ=0
    g2: LineSegment StartX=-57.5 StartY=0 StartZ=0 EndX=57.5 EndY=0 EndZ=0
    g3: LineSegment StartX=-64.5 StartY=-24 StartZ=0 EndX=64.5 EndY=-24 EndZ=0
    g4: LineSegment StartX=-64.5 StartY=24 StartZ=0 EndX=64.5 EndY=24 EndZ=0
    g5: LineSegment StartX=-64.5 StartY=-24 StartZ=0 EndX=-75.5 EndY=-24 EndZ=0
    g6: LineSegment StartX=64.5 StartY=-24 StartZ=0 EndX=75.5 EndY=-24 EndZ=0
    g7: ArcOfCircle CenterX=0 CenterY=52.6846 CenterZ=0 NormalX=0 NormalY=0 NormalZ=1 AngleXU=0 Radius=112.5 StartAngle=3.96017 EndAngle=5.4646
    g8: LineSegment StartX=-64.5 StartY=24 StartZ=0 EndX=-75.5 EndY=24 EndZ=0
    g9: LineSegment StartX=64.5 StartY=24 StartZ=0 EndX=75.5 EndY=24 EndZ=0
    g10: LineSegment StartX=-77.1162 StartY=42.1781 StartZ=0 EndX=-29.0404 EndY=108.13 EndZ=0
    g11: LineSegment StartX=-25 StartY=110.185 StartZ=0 EndX=25 EndY=110.185 EndZ=0
    g12: LineSegment StartX=29.0404 StartY=108.13 StartZ=0 EndX=77.1162 EndY=42.1781 EndZ=0
    g13: LineSegment StartX=0 StartY=0 StartZ=0 EndX=0 EndY=110.185 EndZ=0
    g14: ArcOfCircle CenterX=-25 CenterY=105.185 CenterZ=0 NormalX=0 NormalY=0 NormalZ=1 AngleXU=0 Radius=5 StartAngle=1.5708 EndAngle=2.5117
    g15: ArcOfCircle CenterX=25 CenterY=105.185 CenterZ=0 NormalX=0 NormalY=0 NormalZ=1 AngleXU=0 Radius=5 StartAngle=0.629894 EndAngle=1.5708
    g16: ArcOfCircle CenterX=-64.5 CenterY=17 CenterZ=0 NormalX=0 NormalY=0 NormalZ=1 AngleXU=0 Radius=7 StartAngle=0 EndAngle=1.5708
    g17: ArcOfCircle CenterX=-64.5 CenterY=-17 CenterZ=0 NormalX=0 NormalY=0 NormalZ=1 AngleXU=0 Radius=7 StartAngle=4.71239 EndAngle=6.28319
    g18: ArcOfCircle CenterX=64.5 CenterY=-17 CenterZ=0 NormalX=0 NormalY=0 NormalZ=1 AngleXU=0 Radius=7 StartAngle=3.14159 EndAngle=4.71239
    g19: ArcOfCircle CenterX=64.5 CenterY=17 CenterZ=0 NormalX=0 NormalY=0 NormalZ=1 AngleXU=0 Radius=7 StartAngle=1.5708 EndAngle=3.14159
    g20: GeomPoint X=0 Y=-59.8154 Z=0
    g21: Circle CenterX=0 CenterY=52.6846 CenterZ=0 NormalX=0 NormalY=0 NormalZ=1 AngleXU=0 Radius=112.5
    g22: LineSegment StartX=77.5 StartY=26 StartZ=0 EndX=77.5 EndY=41 EndZ=0
    g23: LineSegment StartX=77.5 StartY=-26 StartZ=0 EndX=77.5 EndY=-28 EndZ=0
    g24: LineSegment StartX=-77.5 StartY=-28 StartZ=0 EndX=-77.5 EndY=-26 EndZ=0
    g25: LineSegment StartX=-77.5 StartY=26 StartZ=0 EndX=-77.5 EndY=41 EndZ=0
    g26: ArcOfCircle CenterX=75.5 CenterY=-28 CenterZ=0 NormalX=0 NormalY=0 NormalZ=1 AngleXU=0 Radius=2 StartAngle=5.4646 EndAngle=6.28319
    g27: ArcOfCircle CenterX=75.5 CenterY=-26 CenterZ=0 NormalX=0 NormalY=0 NormalZ=1 AngleXU=0 Radius=2 StartAngle=0 EndAngle=1.5708
    g28: ArcOfCircle CenterX=-75.5 CenterY=-28 CenterZ=0 NormalX=0 NormalY=0 NormalZ=1 AngleXU=0 Radius=2 StartAngle=3.14159 EndAngle=3.96017
    g29: ArcOfCircle CenterX=-75.5 CenterY=-26 CenterZ=0 NormalX=0 NormalY=0 NormalZ=1 AngleXU=0 Radius=2 StartAngle=1.5708 EndAngle=3.14159
    g30: ArcOfCircle CenterX=75.5 CenterY=26 CenterZ=0 NormalX=0 NormalY=0 NormalZ=1 AngleXU=0 Radius=2 StartAngle=4.71239 EndAngle=6.28319
    g31: ArcOfCircle CenterX=75.5 CenterY=41 CenterZ=0 NormalX=0 NormalY=0 NormalZ=1 AngleXU=0 Radius=2 StartAngle=4e-16 EndAngle=0.629894
    g32: ArcOfCircle CenterX=-75.5 CenterY=26 CenterZ=0 NormalX=0 NormalY=0 NormalZ=1 AngleXU=0 Radius=2 StartAngle=3.14159 EndAngle=4.71239
    g33: ArcOfCircle CenterX=-75.5 CenterY=41 CenterZ=0 NormalX=0 NormalY=0 NormalZ=1 AngleXU=0 Radius=2 StartAngle=2.5117 EndAngle=3.14159
    g34: LineSegment StartX=77.5 StartY=26 StartZ=0 EndX=77.5 EndY=-26 EndZ=0
    g35: LineSegment StartX=-77.5 StartY=26 StartZ=0 EndX=-77.5 EndY=-26 EndZ=0
    g36: LineSegment StartX=77.5 StartY=41 StartZ=0 EndX=77.5 EndY=-28 EndZ=0
    g37: LineSegment StartX=-77.5 StartY=41 StartZ=0 EndX=-77.5 EndY=-28 EndZ=0
    g38: ArcOfCircle CenterX=0 CenterY=52.6846 CenterZ=0 NormalX=0 NormalY=0 NormalZ=1 AngleXU=0 Radius=112.5 StartAngle=4.71239 EndAngle=5.4646
    g39: LineSegment StartX=-2 StartY=2 StartZ=0 EndX=-2 EndY=-87 EndZ=0
    g40: LineSegment StartX=76.8665 StartY=-38.9967 StartZ=0 EndX=76.8665 EndY=-87 EndZ=0
    g41: LineSegment StartX=-2 StartY=-87 StartZ=0 EndX=76.8665 EndY=-87 EndZ=0
    g42: LineSegment StartX=-2 StartY=2 StartZ=0 EndX=77.5 EndY=2 EndZ=0
    g43: LineSegment StartX=0 StartY=-70.7909 StartZ=0 EndX=76.8665 EndY=-38.9967 EndZ=0
    g44: GeomPoint X=43 Y=-51.2734 Z=0
    g45: LineSegment StartX=0 StartY=52.6846 StartZ=0 EndX=43 EndY=-51.2734 EndZ=0
    g46: LineSegment StartX=43.6116 StartY=-52.7519 StartZ=0 EndX=43 EndY=-51.2734 EndZ=0
    g47: LineSegment StartX=76.8665 StartY=-38.9967 StartZ=0 EndX=76.8665 EndY=-29.4604 EndZ=0
    g48: LineSegment StartX=-2.07e-14 StartY=-59.8154 StartZ=0 EndX=0 EndY=-70.7909 EndZ=0
    g49: LineSegment StartX=0 StartY=-70.7909 StartZ=0 EndX=-2.07e-14 EndY=-59.8154 EndZ=0
    g50: LineSegment StartX=77.5 StartY=2 StartZ=0 EndX=77.5 EndY=-28.863 EndZ=0
    g51: ArcOfCircle CenterX=0 CenterY=52.6846 CenterZ=0 NormalX=0 NormalY=0 NormalZ=1 AngleXU=0 Radius=112.5 StartAngle=4.71239 EndAngle=5.04422
    g52: ArcOfCircle CenterX=0 CenterY=52.6846 CenterZ=0 NormalX=0 NormalY=0 NormalZ=1 AngleXU=0 Radius=112.5 StartAngle=5.1665 EndAngle=5.47234
    g53: LineSegment StartX=36.65 StartY=-53.6781 StartZ=0 EndX=36.65 EndY=-51.3781 EndZ=0
    g54: LineSegment StartX=49.35 StartY=-48.4135 StartZ=0 EndX=49.35 EndY=-46.1135 EndZ=0
    g55: LineSegment StartX=36.65 StartY=-51.3781 StartZ=0 EndX=35.9672 EndY=-50.6953 EndZ=0
    g56: LineSegment StartX=35.9672 StartY=-50.1296 StartZ=0 EndX=36.65 EndY=-49.4468 EndZ=0
    g57: ArcOfCircle CenterX=36.25 CenterY=-50.4125 CenterZ=0 NormalX=0 NormalY=0 NormalZ=1 AngleXU=0 Radius=0.4 StartAngle=2.35619 EndAngle=3.92699
    g58: LineSegment StartX=49.35 StartY=-46.1135 StartZ=0 EndX=50.0328 EndY=-45.4307 EndZ=0
    g59: LineSegment StartX=50.0328 StartY=-44.865 StartZ=0 EndX=49.35 EndY=-44.1822 EndZ=0
    g60: ArcOfCircle CenterX=49.75 CenterY=-45.1479 CenterZ=0 NormalX=0 NormalY=0 NormalZ=1 AngleXU=0 Radius=0.4 StartAngle=5.49779 EndAngle=7.06858
    g61: LineSegment StartX=36.65 StartY=-51.3781 StartZ=0 EndX=36.65 EndY=-49.4468 EndZ=0
    g62: LineSegment StartX=49.35 StartY=-46.1135 StartZ=0 EndX=49.35 EndY=-44.1822 EndZ=0
    g63: LineSegment StartX=36.65 StartY=-49.4468 StartZ=0 EndX=49.35 EndY=-44.1822 EndZ=0
    g64: GeomPoint X=50.15 Y=-45.1479 Z=0
    g65: GeomPoint X=35.85 Y=-50.4125 Z=0
    g66: LineSegment StartX=35.85 StartY=-50.4125 StartZ=0 EndX=36.65 EndY=-50.4125 EndZ=0
    g67: LineSegment StartX=50.15 StartY=-45.1479 StartZ=0 EndX=49.35 EndY=-45.1479 EndZ=0
  constraints (171):
    c: Vertical(g0)
    c: Vertical(g1)
    c: Horizontal(g2)
    c: Symmetric(g2,g2,g-1)
    c: Horizontal(g3)
    c: Horizontal(g5)
    c: Horizontal(g6)
    c: PointOnObject(g7,g-2)
    c: Horizontal(g8)
    c: Horizontal(g9)
    c: Horizontal(g11)
    c: Coincident(g13,g-1)
    c: PointOnObject(g13,g-2)
    c: Tangent(g10,g14) = 1.5708
    c: Tangent(g11,g14) = 1.5708
    c: Tangent(g11,g15) = 1.5708
    c: Tangent(g12,g15) = 1.5708
    c: Tangent(g8,g16) = -1.5708
    c: Tangent(g0,g16) = 1.5708
    c: Tangent(g5,g17) = 1.5708
    c: Tangent(g0,g17) = 1.5708
    c: Tangent(g1,g18) = -1.5708
    c: Tangent(g6,g18) = -1.5708
    c: Tangent(g1,g19) = -1.5708
    c: Tangent(g9,g19) = 1.5708
    c: Equal(g15,g14)
    c: Symmetric(g11,g11,g13)
    c: Equal(g18,g19)
    c: Equal(g19,g16)
    c: Equal(g16,g17)
    c: PointOnObject(g20,g-2)
    c: PointOnObject(g20,g7)
    c: Coincident(g4,g8)
    c: Coincident(g4,g9)
    c: Coincident(g3,g6)
    c: Coincident(g3,g5)
    c: DistanceX(g2,g2) = 115
    c: Symmetric(g0,g0,g2)
    c: Symmetric(g1,g1,g2)
    c: Radius(g19) = 7
    c: DistanceY(g20,g11) = 170
    c: Radius(g15) = 5
    c: DistanceX(g11,g11) = 50
    c: Equal(g9,g8)
    c: Equal(g9,g6)
    c: Coincident(g21,g7)
    c: PointOnObject(g20,g21)
    c: Diameter(g21) = 225
    c: Vertical(g22)
    c: Vertical(g23)
    c: Vertical(g24)
    c: Vertical(g25)
    c: Equal(g5,g8)
    c: Equal(g10,g12)
    c: Tangent(g7,g26) = -1.5708
    c: Tangent(g23,g26) = 1.5708
    c: Tangent(g23,g27) = 1.5708
    c: Tangent(g6,g27) = 1.5708
    c: Tangent(g7,g28) = -1.5708
    c: Tangent(g24,g28) = 1.5708
    c: Tangent(g24,g29) = 1.5708
    c: Tangent(g5,g29) = -1.5708
    c: Equal(g29,g27)
    c: Radius(g27) = 2
    c: Equal(g26,g28)
    c: Radius(g26) = 2
    c: Tangent(g9,g30) = -1.5708
    c: Tangent(g22,g30) = -1.5708
    c: Tangent(g22,g31) = -1.5708
    c: Tangent(g12,g31) = 1.5708
    c: Tangent(g8,g32) = 1.5708
    c: Tangent(g25,g32) = 1.5708
    c: Tangent(g10,g33) = 1.5708
    c: Tangent(g25,g33) = 1.5708
    c: Equal(g30,g32)
    c: Equal(g31,g33)
    c: DistanceY(g23,g23) = 2
    c: DistanceY(g22,g22) = 15
    c: DistanceY(g6,g9) = 48
    c: DistanceX(g24,g23) = 155
    c: Radius(g30) = 2
    c: Radius(g31) = 2
    c: Coincident(g34,g22)
    c: Coincident(g34,g23)
    c: Coincident(g35,g25)
    c: Coincident(g35,g24)
    c: Coincident(g37,g28)
    c: Coincident(g37,g33)
    c: Coincident(g36,g31)
    c: Coincident(g36,g26)
    c: Coincident(g38,g7)
    c: PointOnObject(g38,g-2)
    c: Coincident(g38,g7)
    c: Vertical(g39)
    c: Vertical(g40)
    c: Coincident(g41,g39)
    c: Coincident(g41,g40)
    c: Horizontal(g41)
    c: Coincident(g42,g39)
    c: Horizontal(g42)
    c: DistanceY(g-1,g39) = 2
    c: DistanceY(g39,g-1) = 87
    c: PointOnObject(g44,g38)
    c: DistanceX(g-1,g44) = 43
    c: Coincident(g45,g44)
    c: Coincident(g45,g38)
    c: Coincident(g46,g44)
    c: PointOnObject(g46,g43)
    c: Parallel(g45,g46)
    c: Perpendicular(g46,g43)
    c: Distance(g46) = 1.6
    c: PointOnObject(g43,g-2)
    c: Coincident(g40,g43)
    c: Coincident(g47,g40)
    c: Coincident(g47,g38)
    c: Vertical(g47)
    c: Coincident(g48,g38)
    c: Coincident(g48,g43)
    c: DistanceX(g39,g43) = 2
    c: Coincident(g49,g43)
    c: PointOnObject(g49,g-2)
    c: PointOnObject(g42,g34)
    c: PointOnObject(g50,g34)
    c: Coincident(g50,g42)
    c: PointOnObject(g51,g13)
    c: Coincident(g51,g49)
    c: Coincident(g52,g51)
    c: Coincident(g52,g50)
    c: Coincident(g53,g51)
    c: Vertical(g53)
    c: Coincident(g54,g52)
    c: Vertical(g54)
    c: Equal(g51,g7)
    c: Equal(g52,g21)
    c: DistanceX(g51,g44) = 6.35
    c: DistanceX(g44,g52) = 6.35
    c: Equal(g54,g53)
    c: DistanceY(g54,g54) = 2.3
    c: PointOnObject(g49,g7)
    c: Coincident(g55,g53)
    c: Tangent(g55,g57) = 1.5708
    c: Tangent(g56,g57) = 1.5708
    c: Coincident(g58,g54)
    c: Tangent(g58,g60) = -1.5708
    c: Tangent(g59,g60) = -1.5708
    c: Coincident(g61,g53)
    c: Coincident(g61,g56)
    c: Vertical(g61)
    c: Coincident(g62,g54)
    c: Coincident(g62,g59)
    c: Vertical(g62)
    c: Equal(g58,g59)
    c: Equal(g55,g56)
    c: Equal(g60,g57)
    c: Coincident(g63,g56)
    c: Coincident(g63,g59)
    c: Angle(g59,g58) = 1.5708
    c: Angle(g55,g56) = 1.5708
    c: PointOnObject(g64,g60)
    c: PointOnObject(g65,g57)
    c: Coincident(g66,g65)
    c: PointOnObject(g66,g61)
    c: Horizontal(g66)
    c: PointOnObject(g57,g66)
    c: Coincident(g67,g64)
    c: PointOnObject(g67,g62)
    c: Horizontal(g67)
    c: PointOnObject(g60,g67)
    c: DistanceX(g67,g64) = 0.8
    c: Equal(g67,g66)
    c: Diameter(g60) = 0.8
FEATURE [Sketcher::SketchObject] Sketch015  label="Sketch_Shell_Top_CutPlug"
  FullyConstrained = true
  MapMode = 5
  Placement = pos=(0,0,42) rot=(0,0,1;0rad)
  Support = -> [DatumPlane001]
  expr: Constraints[47] = <<params>>.front_diameter
  expr: Constraints[36] = <<params>>.wheel_well_plate_width - 2 * Spreadsheet.shell_overhang_leng
  expr: Constraints[116] = Spreadsheet.shell_overhang_leng
  expr: Constraints[88] = Spreadsheet.shell_overhang_leng
  expr: Constraints[81] = <<params>>.std_rad
  expr: Constraints[65] = <<params>>.std_rad
  expr: Constraints[186] = <<params>>.xport_clip_size
  expr: Constraints[129] = <<params>>.std_wall_thick
  expr: Constraints[41] = <<params>>.tail_rad
  expr: Constraints[187] = <<params>>.xport_clip_size
  expr: Constraints[76] = <<params>>.front_vert_edge
  expr: Constraints[40] = <<params>>.plate_length
  expr: Constraints[189] = <<params>>.shell_overhang_leng
  expr: Constraints[80] = <<params>>.std_rad
  expr: Constraints[117] = <<params>>.shell_overhang_leng
  expr: Constraints[130] = <<params>>.plate_length / 2 + <<params>>.std_wall_thick
  expr: Constraints[152] = <<params>>.xport_plug_diam / 2
  expr: Constraints[153] = <<params>>.xport_plug_diam / 2
  expr: Constraints[78] = <<params>>.wheel_well_clearance
  expr: Constraints[42] = <<params>>.tail_width
  expr: Constraints[143] = <<params>>.std_wall_thick
  expr: Constraints[63] = <<params>>.std_rad
  expr: Constraints[155] = <<params>>.shell_wall_thick + <<params>>.std_tol_interfere
  expr: Constraints[77] = <<params>>.back_vert_edge
  expr: Constraints[120] = <<params>>.shell_overhang_leng
  expr: Constraints[136] = <<params>>.xport_offset_loc
  expr: Constraints[79] = <<params>>.plate_width
  expr: Constraints[142] = <<params>>.xport_plug_plate_thick
  sketch-geometry (80):
    g0: LineSegment StartX=-43.5 StartY=17 StartZ=0 EndX=-43.5 EndY=-17 EndZ=0
    g1: LineSegment StartX=43.5 StartY=17 StartZ=0 EndX=43.5 EndY=-17 EndZ=0
    g2: LineSegment StartX=-43.5 StartY=0 StartZ=0 EndX=43.5 EndY=0 EndZ=0
    g3: LineSegment StartX=-50.5 StartY=-24 StartZ=0 EndX=50.5 EndY=-24 EndZ=0
    g4: LineSegment StartX=-50.5 StartY=24 StartZ=0 EndX=50.5 EndY=24 EndZ=0
    g5: LineSegment StartX=-50.5 StartY=-24 StartZ=0 EndX=-75.5 EndY=-24 EndZ=0
    g6: LineSegment StartX=50.5 StartY=-24 StartZ=0 EndX=75.5 EndY=-24 EndZ=0
    g7: ArcOfCircle CenterX=0 CenterY=52.6846 CenterZ=0 NormalX=0 NormalY=0 NormalZ=1 AngleXU=0 Radius=112.5 StartAngle=3.96017 EndAngle=5.4646
    g8: LineSegment StartX=-50.5 StartY=24 StartZ=0 EndX=-75.5 EndY=24 EndZ=0
    g9: LineSegment StartX=50.5 StartY=24 StartZ=0 EndX=75.5 EndY=24 EndZ=0
    g10: LineSegment StartX=-77.1162 StartY=42.1781 StartZ=0 EndX=-29.0404 EndY=108.13 EndZ=0
    g11: LineSegment StartX=-25 StartY=110.185 StartZ=0 EndX=25 EndY=110.185 EndZ=0
    g12: LineSegment StartX=29.0404 StartY=108.13 StartZ=0 EndX=77.1162 EndY=42.1781 EndZ=0
    g13: LineSegment StartX=0 StartY=0 StartZ=0 EndX=0 EndY=110.185 EndZ=0
    g14: ArcOfCircle CenterX=-25 CenterY=105.185 CenterZ=0 NormalX=0 NormalY=0 NormalZ=1 AngleXU=0 Radius=5 StartAngle=1.5708 EndAngle=2.5117
    g15: ArcOfCircle CenterX=25 CenterY=105.185 CenterZ=0 NormalX=0 NormalY=0 NormalZ=1 AngleXU=0 Radius=5 StartAngle=0.629894 EndAngle=1.5708
    g16: ArcOfCircle CenterX=-50.5 CenterY=17 CenterZ=0 NormalX=0 NormalY=0 NormalZ=1 AngleXU=0 Radius=7 StartAngle=0 EndAngle=1.5708
    g17: ArcOfCircle CenterX=-50.5 CenterY=-17 CenterZ=0 NormalX=0 NormalY=0 NormalZ=1 AngleXU=0 Radius=7 StartAngle=4.71239 EndAngle=6.28319
    g18: ArcOfCircle CenterX=50.5 CenterY=-17 CenterZ=0 NormalX=0 NormalY=0 NormalZ=1 AngleXU=0 Radius=7 StartAngle=3.14159 EndAngle=4.71239
    g19: ArcOfCircle CenterX=50.5 CenterY=17 CenterZ=0 NormalX=0 NormalY=0 NormalZ=1 AngleXU=0 Radius=7 StartAngle=1.5708 EndAngle=3.14159
    g20: GeomPoint X=0 Y=-59.8154 Z=0
    g21: Circle CenterX=0 CenterY=52.6846 CenterZ=0 NormalX=0 NormalY=0 NormalZ=1 AngleXU=0 Radius=112.5
    g22: LineSegment StartX=77.5 StartY=26 StartZ=0 EndX=77.5 EndY=41 EndZ=0
    g23: LineSegment StartX=77.5 StartY=-26 StartZ=0 EndX=77.5 EndY=-28 EndZ=0
    g24: LineSegment StartX=-77.5 StartY=-28 StartZ=0 EndX=-77.5 EndY=-26 EndZ=0
    g25: LineSegment StartX=-77.5 StartY=26 StartZ=0 EndX=-77.5 EndY=41 EndZ=0
    g26: ArcOfCircle CenterX=75.5 CenterY=-28 CenterZ=0 NormalX=0 NormalY=0 NormalZ=1 AngleXU=0 Radius=2 StartAngle=5.4646 EndAngle=6.28319
    g27: ArcOfCircle CenterX=75.5 CenterY=-26 CenterZ=0 NormalX=0 NormalY=0 NormalZ=1 AngleXU=0 Radius=2 StartAngle=0 EndAngle=1.5708
    g28: ArcOfCircle CenterX=-75.5 CenterY=-28 CenterZ=0 NormalX=0 NormalY=0 NormalZ=1 AngleXU=0 Radius=2 StartAngle=3.14159 EndAngle=3.96017
    g29: ArcOfCircle CenterX=-75.5 CenterY=-26 CenterZ=0 NormalX=0 NormalY=0 NormalZ=1 AngleXU=0 Radius=2 StartAngle=1.5708 EndAngle=3.14159
    g30: ArcOfCircle CenterX=75.5 CenterY=26 CenterZ=0 NormalX=0 NormalY=0 NormalZ=1 AngleXU=0 Radius=2 StartAngle=4.71239 EndAngle=6.28319
    g31: ArcOfCircle CenterX=75.5 CenterY=41 CenterZ=0 NormalX=0 NormalY=0 NormalZ=1 AngleXU=0 Radius=2 StartAngle=9e-16 EndAngle=0.629894
    g32: ArcOfCircle CenterX=-75.5 CenterY=26 CenterZ=0 NormalX=0 NormalY=0 NormalZ=1 AngleXU=0 Radius=2 StartAngle=3.14159 EndAngle=4.71239
    g33: ArcOfCircle CenterX=-75.5 CenterY=41 CenterZ=0 NormalX=0 NormalY=0 NormalZ=1 AngleXU=0 Radius=2 StartAngle=2.5117 EndAngle=3.14159
    g34: LineSegment StartX=77.5 StartY=26 StartZ=0 EndX=77.5 EndY=-26 EndZ=0
    g35: LineSegment StartX=-77.5 StartY=26 StartZ=0 EndX=-77.5 EndY=-26 EndZ=0
    g36: LineSegment StartX=-17.8805 StartY=96.1846 StartZ=0 EndX=17.8805 EndY=96.1846 EndZ=0
    g37: GeomPoint X=0 Y=96.1846 Z=0
    g38: LineSegment StartX=-21.921 StartY=94.1299 StartZ=0 EndX=-63.1162 EndY=37.617 EndZ=0
    g39: LineSegment StartX=-63.5 StartY=36.4389 StartZ=0 EndX=-63.5 EndY=-21.6794 EndZ=0
    g40: LineSegment StartX=21.921 StartY=94.1299 StartZ=0 EndX=63.1162 EndY=37.617 EndZ=0
    g41: LineSegment StartX=63.5 StartY=36.4389 StartZ=0 EndX=63.5 EndY=-21.6794 EndZ=0
    g42: ArcOfCircle CenterX=0 CenterY=52.6846 CenterZ=0 NormalX=0 NormalY=0 NormalZ=1 AngleXU=0 Radius=98.5 StartAngle=4.02139 EndAngle=5.40339
    g43: LineSegment StartX=-63.5 StartY=36.4389 StartZ=0 EndX=63.5 EndY=36.4389 EndZ=0
    g44: GeomPoint X=0 Y=-45.8154 Z=0
    g45: ArcOfCircle CenterX=-17.8805 CenterY=91.1846 CenterZ=0 NormalX=0 NormalY=0 NormalZ=1 AngleXU=0 Radius=5 StartAngle=1.5708 EndAngle=2.5117
    g46: ArcOfCircle CenterX=17.8805 CenterY=91.1846 CenterZ=0 NormalX=0 NormalY=0 NormalZ=1 AngleXU=0 Radius=5 StartAngle=0.629894 EndAngle=1.5708
    g47: ArcOfCircle CenterX=61.5 CenterY=36.4389 CenterZ=0 NormalX=0 NormalY=0 NormalZ=1 AngleXU=0 Radius=2 StartAngle=0 EndAngle=0.629894
    g48: ArcOfCircle CenterX=-61.5 CenterY=36.4389 CenterZ=0 NormalX=0 NormalY=0 NormalZ=1 AngleXU=0 Radius=2 StartAngle=2.5117 EndAngle=3.14159
    g49: ArcOfCircle CenterX=61.5 CenterY=-21.6794 CenterZ=0 NormalX=0 NormalY=0 NormalZ=1 AngleXU=0 Radius=2 StartAngle=5.40339 EndAngle=6.28319
    g50: ArcOfCircle CenterX=-61.5 CenterY=-21.6794 CenterZ=0 NormalX=0 NormalY=0 NormalZ=1 AngleXU=0 Radius=2 StartAngle=3.14159 EndAngle=4.02139
    g51: LineSegment StartX=-29.0404 StartY=108.13 StartZ=0 EndX=-17.7272 EndY=99.883 EndZ=0
    g52: LineSegment StartX=-2 StartY=2 StartZ=0 EndX=-2 EndY=-87 EndZ=0
    g53: LineSegment StartX=-2 StartY=-87 StartZ=0 EndX=63.5 EndY=-87 EndZ=0
    g54: LineSegment StartX=63.5 StartY=-87 StartZ=0 EndX=63.5 EndY=-27.7653 EndZ=0
    g55: LineSegment StartX=63.5 StartY=2 StartZ=0 EndX=-2 EndY=2 EndZ=0
    g56: LineSegment StartX=0 StartY=-58.5771 StartZ=0 EndX=63.5 EndY=-27.7653 EndZ=0
    g57: LineSegment StartX=63.5 StartY=-22.6148 StartZ=0 EndX=63.5 EndY=-27.7653 EndZ=0
    g58: GeomPoint X=43 Y=-35.934 Z=0
    g59: LineSegment StartX=0 StartY=52.6846 StartZ=0 EndX=43 EndY=-35.934 EndZ=0
    g60: LineSegment StartX=43 StartY=-35.934 StartZ=0 EndX=43.6985 EndY=-37.3735 EndZ=0
    g61: LineSegment StartX=0 StartY=-58.5771 StartZ=0 EndX=-1.81e-14 EndY=-45.8154 EndZ=0
    g62: LineSegment StartX=63.5 StartY=2 StartZ=0 EndX=63.5 EndY=-22.6148 EndZ=0
    g63: LineSegment StartX=36.65 StartY=-38.7431 StartZ=0 EndX=36.65 EndY=-36.5431 EndZ=0
    g64: LineSegment StartX=49.35 StartY=-30.3611 StartZ=0 EndX=49.35 EndY=-32.5611 EndZ=0
    g65: LineSegment StartX=36.65 StartY=-36.5431 StartZ=0 EndX=35.9672 EndY=-35.8603 EndZ=0
    g66: LineSegment StartX=35.9672 StartY=-35.2946 StartZ=0 EndX=36.65 EndY=-34.6118 EndZ=0
    g67: LineSegment StartX=49.35 StartY=-30.3611 StartZ=0 EndX=50.0328 EndY=-29.6783 EndZ=0
    g68: LineSegment StartX=50.0328 StartY=-29.1126 StartZ=0 EndX=49.35 EndY=-28.4297 EndZ=0
    g69: LineSegment StartX=49.35 StartY=-28.4297 StartZ=0 EndX=36.65 EndY=-34.6118 EndZ=0
    g70: ArcOfCircle CenterX=36.25 CenterY=-35.5775 CenterZ=0 NormalX=0 NormalY=0 NormalZ=1 AngleXU=0 Radius=0.4 StartAngle=2.35619 EndAngle=3.92699
    g71: ArcOfCircle CenterX=49.75 CenterY=-29.3954 CenterZ=0 NormalX=0 NormalY=0 NormalZ=1 AngleXU=0 Radius=0.4 StartAngle=5.49779 EndAngle=7.06858
    g72: LineSegment StartX=36.65 StartY=-36.5431 StartZ=0 EndX=36.65 EndY=-34.6118 EndZ=0
    g73: GeomPoint X=35.85 Y=-35.5775 Z=0
    g74: GeomPoint X=50.15 Y=-29.3954 Z=0
    g75: LineSegment StartX=49.35 StartY=-30.3611 StartZ=0 EndX=49.35 EndY=-28.4297 EndZ=0
    g76: LineSegment StartX=50.15 StartY=-29.3954 StartZ=0 EndX=49.35 EndY=-29.3954 EndZ=0
    g77: LineSegment StartX=36.65 StartY=-35.5775 StartZ=0 EndX=35.85 EndY=-35.5775 EndZ=0
    g78: ArcOfCircle CenterX=0 CenterY=52.6846 CenterZ=0 NormalX=0 NormalY=0 NormalZ=1 AngleXU=0 Radius=98.5 StartAngle=4.71239 EndAngle=5.09364
    g79: ArcOfCircle CenterX=0 CenterY=52.6846 CenterZ=0 NormalX=0 NormalY=0 NormalZ=1 AngleXU=0 Radius=98.5 StartAngle=5.23716 EndAngle=5.41298
  constraints (201):
    c: Vertical(g0)
    c: Vertical(g1)
    c: Horizontal(g2)
    c: Symmetric(g2,g2,g-1)
    c: Horizontal(g3)
    c: Horizontal(g5)
    c: Horizontal(g6)
    c: PointOnObject(g7,g-2)
    c: Horizontal(g8)
    c: Horizontal(g9)
    c: Horizontal(g11)
    c: Coincident(g13,g-1)
    c: PointOnObject(g13,g-2)
    c: Tangent(g10,g14) = 1.5708
    c: Tangent(g11,g14) = 1.5708
    c: Tangent(g11,g15) = 1.5708
    c: Tangent(g12,g15) = 1.5708
    c: Tangent(g8,g16) = -1.5708
    c: Tangent(g0,g16) = 1.5708
    c: Tangent(g5,g17) = 1.5708
    c: Tangent(g0,g17) = 1.5708
    c: Tangent(g1,g18) = -1.5708
    c: Tangent(g6,g18) = -1.5708
    c: Tangent(g1,g19) = -1.5708
    c: Tangent(g9,g19) = 1.5708
    c: Equal(g15,g14)
    c: Symmetric(g11,g11,g13)
    c: Equal(g18,g19)
    c: Equal(g19,g16)
    c: Equal(g16,g17)
    c: PointOnObject(g20,g-2)
    c: PointOnObject(g20,g7)
    c: Coincident(g4,g8)
    c: Coincident(g4,g9)
    c: Coincident(g3,g6)
    c: Coincident(g3,g5)
    c: DistanceX(g2,g2) = 87
    c: Symmetric(g0,g0,g2)
    c: Symmetric(g1,g1,g2)
    c: Radius(g19) = 7
    c: DistanceY(g20,g11) = 170
    c: Radius(g15) = 5
    c: DistanceX(g11,g11) = 50
    c: Equal(g9,g8)
    c: Equal(g9,g6)
    c: Coincident(g21,g7)
    c: PointOnObject(g20,g21)
    c: Diameter(g21) = 225
    c: Vertical(g22)
    c: Vertical(g23)
    c: Vertical(g24)
    c: Vertical(g25)
    c: Equal(g5,g8)
    c: Equal(g10,g12)
    c: Tangent(g7,g26) = -1.5708
    c: Tangent(g23,g26) = 1.5708
    c: Tangent(g23,g27) = 1.5708
    c: Tangent(g6,g27) = 1.5708
    c: Tangent(g7,g28) = -1.5708
    c: Tangent(g24,g28) = 1.5708
    c: Tangent(g24,g29) = 1.5708
    c: Tangent(g5,g29) = -1.5708
    c: Equal(g29,g27)
    c: Radius(g27) = 2
    c: Equal(g26,g28)
    c: Radius(g26) = 2
    c: Tangent(g9,g30) = -1.5708
    c: Tangent(g22,g30) = -1.5708
    c: Tangent(g22,g31) = -1.5708
    c: Tangent(g12,g31) = 1.5708
    c: Tangent(g8,g32) = 1.5708
    c: Tangent(g25,g32) = 1.5708
    c: Tangent(g10,g33) = 1.5708
    c: Tangent(g25,g33) = 1.5708
    c: Equal(g30,g32)
    c: Equal(g31,g33)
    c: DistanceY(g23,g23) = 2
    c: DistanceY(g22,g22) = 15
    c: DistanceY(g6,g9) = 48
    c: DistanceX(g24,g23) = 155
    c: Radius(g30) = 2
    c: Radius(g31) = 2
    c: Coincident(g34,g22)
    c: Coincident(g34,g23)
    c: Coincident(g35,g25)
    c: Coincident(g35,g24)
    c: Horizontal(g36)
    c: PointOnObject(g37,g13)
    c: DistanceY(g37,g13) = 14
    c: Vertical(g39)
    c: Vertical(g41)
    c: Horizontal(g43)
    c: Parallel(g40,g12)
    c: PointOnObject(g44,g-2)
    c: PointOnObject(g44,g42)
    c: Tangent(g38,g45) = -1.5708
    c: Tangent(g36,g45) = 1.5708
    c: Tangent(g40,g46) = 1.5708
    c: Tangent(g36,g46) = 1.5708
    c: Tangent(g41,g47) = 1.5708
    c: Tangent(g40,g47) = 1.5708
    c: Tangent(g39,g48) = -1.5708
    c: Tangent(g38,g48) = -1.5708
    c: Tangent(g42,g49) = -1.5708
    c: Tangent(g41,g49) = 1.5708
    c: Tangent(g42,g50) = -1.5708
    c: Tangent(g39,g50) = -1.5708
    c: Coincident(g43,g39)
    c: Coincident(g43,g41)
    c: Equal(g15,g46)
    c: Equal(g46,g45)
    c: Symmetric(g36,g36,g37)
    c: Equal(g31,g47)
    c: Equal(g26,g49)
    c: Equal(g50,g29)
    c: Equal(g48,g32)
    c: DistanceY(g20,g44) = 14
    c: DistanceX(g41,g22) = 14
    c: PointOnObject(g51,g38)
    c: Perpendicular(g38,g51)
    c: Distance(g51) = 14
    c: Coincident(g51,g10)
    c: Vertical(g52)
    c: Coincident(g53,g52)
    c: Horizontal(g53)
    c: Coincident(g54,g53)
    c: Vertical(g54)
    c: Coincident(g55,g52)
    c: Horizontal(g55)
    c: DistanceY(g-1,g52) = 2
    c: DistanceY(g52,g-1) = 87
    c: Coincident(g54,g56)
    c: Coincident(g57,g54)
    c: Vertical(g57)
    c: PointOnObject(g56,g-2)
    c: PointOnObject(g58,g42)
    c: DistanceX(g-1,g58) = 43
    c: Coincident(g59,g58)
    c: Coincident(g60,g58)
    c: PointOnObject(g60,g56)
    c: Parallel(g60,g59)
    c: Perpendicular(g56,g60)
    c: Distance(g60) = 1.6
    c: DistanceX(g52,g-1) = 2
    c: Coincident(g61,g56)
    c: PointOnObject(g61,g-2)
    c: Vertical(g62)
    c: Coincident(g62,g55)
    c: PointOnObject(g55,g41)
    c: Vertical(g63)
    c: Vertical(g64)
    c: Equal(g64,g63)
    c: DistanceX(g63,g58) = 6.35
    c: DistanceX(g58,g64) = 6.35
    c: PointOnObject(g61,g42)
    c: DistanceY(g64,g64) = 2.2
    c: Coincident(g65,g63)
    c: Coincident(g67,g64)
    c: Coincident(g69,g68)
    c: Coincident(g69,g66)
    c: Tangent(g65,g70) = 1.5708
    c: Tangent(g66,g70) = 1.5708
    c: Tangent(g67,g71) = -1.5708
    c: Tangent(g68,g71) = -1.5708
    c: Coincident(g72,g63)
    c: Coincident(g72,g66)
    c: PointOnObject(g73,g70)
    c: PointOnObject(g74,g71)
    c: Coincident(g75,g64)
    c: Coincident(g75,g68)
    c: Vertical(g75)
    c: Coincident(g76,g74)
    c: PointOnObject(g76,g75)
    c: Horizontal(g76)
    c: PointOnObject(g71,g76)
    c: Equal(g67,g68)
    c: Equal(g68,g66)
    c: Equal(g65,g66)
    c: Equal(g71,g70)
    c: Vertical(g72)
    c: PointOnObject(g77,g72)
    c: Coincident(g77,g73)
    c: Horizontal(g77)
    c: PointOnObject(g70,g77)
    c: Angle(g65,g66) = 1.5708
    c: Angle(g68,g67) = 1.5708
    c: DistanceX(g76,g74) = 0.8
    c: Diameter(g71) = 0.8
    c: Coincident(g42,g7)
    c: DistanceX(g25,g39) = 14
    c: Coincident(g59,g7)
    c: Coincident(g57,g62)
    c: PointOnObject(g63,g42)
    c: PointOnObject(g64,g42)
    c: PointOnObject(g62,g42)
    c: Coincident(g78,g7)
    c: Coincident(g79,g78)
    c: Coincident(g79,g62)
    c: Coincident(g78,g61)
    c: PointOnObject(g78,g63)
    c: PointOnObject(g79,g64)
FEATURE [Sketcher::SketchObject] Sketch016  label="Sketch_HollowPlug"
  FullyConstrained = true
  MapMode = 5
  Placement = pos=(0,0,0) rot=(1,0,0;1.5708rad)
  Support = -> [XZ_Plane002]
  expr: Constraints[2] = <<params>>.xport_height_loc
  expr: Constraints[1] = <<params>>.xport_offset_loc
  expr: Constraints[0] = <<params>>.xport_plug_diam - 2 * <<params>>.xport_plug_wall_thick
  sketch-geometry (1):
    g0: Circle CenterX=43 CenterY=33.25 CenterZ=0 NormalX=0 NormalY=0 NormalZ=1 AngleXU=0 Radius=5.55
  constraints (3):
    c: Diameter(g0) = 11.1
    c: DistanceX(g-1,g0) = 43
    c: DistanceY(g-1,g0) = 33.25
FEATURE [Sketcher::SketchObject] Sketch017  label="Sketch_ClipsToTrim001"
  FullyConstrained = true
  MapMode = 5
  Placement = pos=(0,0,0) rot=(1,0,0;1.5708rad)
  Support = -> [XZ_Plane002]
  expr: Constraints[34] = <<params>>.std_wall_thick
  expr: Constraints[0] = <<params>>.xport_plug_diam + 4 * <<params>>.xport_clip_size
  expr: Constraints[1] = <<params>>.xport_offset_loc
  expr: Constraints[2] = <<params>>.xport_height_loc
  expr: Constraints[15] = <<params>>.std_wall_thick
  sketch-geometry (11):
    g0: Circle CenterX=43 CenterY=33.25 CenterZ=0 NormalX=0 NormalY=0 NormalZ=1 AngleXU=0 Radius=7.95
    g1: LineSegment StartX=35.1131 StartY=34.25 StartZ=0 EndX=50.8869 EndY=34.25 EndZ=0
    g2: LineSegment StartX=35.1131 StartY=32.25 StartZ=0 EndX=50.8869 EndY=32.25 EndZ=0
    g3: ArcOfCircle CenterX=43 CenterY=33.25 CenterZ=0 NormalX=0 NormalY=0 NormalZ=1 AngleXU=0 Radius=7.95 StartAngle=3.01547 EndAngle=3.26771
    g4: ArcOfCircle CenterX=43 CenterY=33.25 CenterZ=0 NormalX=0 NormalY=0 NormalZ=1 AngleXU=0 Radius=7.95 StartAngle=6.15707 EndAngle=6.40931
    g5: LineSegment StartX=35.1131 StartY=32.25 StartZ=0 EndX=42 EndY=32.25 EndZ=0
    g6: LineSegment StartX=44 StartY=32.25 StartZ=0 EndX=50.8869 EndY=32.25 EndZ=0
    g7: LineSegment StartX=43 StartY=33.25 StartZ=0 EndX=43 EndY=32.25 EndZ=0
    g8: LineSegment StartX=42 StartY=32.25 StartZ=0 EndX=42 EndY=25.3631 EndZ=0
    g9: LineSegment StartX=44 StartY=32.25 StartZ=0 EndX=44 EndY=25.3631 EndZ=0
    g10: ArcOfCircle CenterX=43 CenterY=33.25 CenterZ=0 NormalX=0 NormalY=0 NormalZ=1 AngleXU=0 Radius=7.95 StartAngle=4.58627 EndAngle=4.83851
  constraints (35):
    c: Diameter(g0) = 15.9
    c: DistanceX(g-1,g0) = 43
    c: DistanceY(g-1,g0) = 33.25
    c: PointOnObject(g1,g0)
    c: PointOnObject(g1,g0)
    c: Horizontal(g1)
    c: PointOnObject(g2,g0)
    c: Horizontal(g2)
    c: Symmetric(g1,g2,g0)
    c: Coincident(g3,g0)
    c: Coincident(g4,g3)
    c: Coincident(g3,g1)
    c: Coincident(g4,g1)
    c: PointOnObject(g4,g2)
    c: PointOnObject(g3,g2)
    c: DistanceY(g2,g1) = 2
    c: Horizontal(g5)
    c: Horizontal(g6)
    c: Coincident(g7,g3)
    c: PointOnObject(g7,g2)
    c: Vertical(g7)
    c: Symmetric(g5,g6,g7)
    c: PointOnObject(g5,g2)
    c: PointOnObject(g5,g0)
    c: PointOnObject(g6,g0)
    c: Coincident(g8,g5)
    c: PointOnObject(g8,g0)
    c: Vertical(g8)
    c: Coincident(g9,g6)
    c: Vertical(g9)
    c: PointOnObject(g9,g0)
    c: Coincident(g10,g3)
    c: Coincident(g10,g8)
    c: PointOnObject(g10,g9)
    c: DistanceX(g8,g9) = 2
FEATURE [PartDesign::Pad] Pad002  label="Pad_ClipsToTrim"
  BaseFeature = -> Pad001
  Direction = (1,1,1)
  Length = 85
  Length2 = 100
  Placement = pos=(0,0,0) rot=(1,0,0;1.5708rad)
  Profile = -> Sketch017
  Type = 0
  expr: Length = <<params>>.plate_length / 2
FEATURE [PartDesign::Pocket] Pocket  label="Pocket_HollowTube"
  BaseFeature = -> Pad002
  Length = 5
  Length2 = 100
  Midplane = true
  Placement = pos=(0,0,0) rot=(1,0,0;1.5708rad)
  Profile = -> Sketch016
  Type = 1
FEATURE [PartDesign::SubtractiveLoft] SubtractiveLoft001  label="SubtractiveLoft_CutClips"
  BaseFeature = -> Pocket
  Closed = false
  Placement = pos=(0,0,0) rot=(1,0,0;1.5708rad)
  Profile = -> Sketch014
  Ruled = false
  Sections = -> [Sketch015]
FEATURE [Sketcher::SketchObject] Sketch018  label="Sketch_SplitPlug_P1_1"
  FullyConstrained = true
  MapMode = 5
  Placement = pos=(0,0,0) rot=(1,0,0;1.5708rad)
  Support = -> [XZ_Plane002]
  expr: Constraints[6] = <<params>>.std_wall_thick / 2 + <<params>>.std_min_wall_thick
  expr: Constraints[2] = <<params>>.xport_height_loc
  expr: Constraints[1] = <<params>>.xport_offset_loc
  expr: Constraints[0] = <<params>>.xport_plug_diam + 4 * <<params>>.xport_clip_size
  sketch-geometry (3):
    g0: Circle CenterX=43 CenterY=33.25 CenterZ=0 NormalX=0 NormalY=0 NormalZ=1 AngleXU=0 Radius=7.95
    g1: LineSegment StartX=35.2565 StartY=35.05 StartZ=0 EndX=50.7435 EndY=35.05 EndZ=0
    g2: ArcOfCircle CenterX=43 CenterY=33.25 CenterZ=0 NormalX=0 NormalY=0 NormalZ=1 AngleXU=0 Radius=7.95 StartAngle=2.9132 EndAngle=6.51158
  constraints (10):
    c: Diameter(g0) = 15.9
    c: DistanceX(g-1,g0) = 43
    c: DistanceY(g-1,g0) = 33.25
    c: PointOnObject(g1,g0)
    c: PointOnObject(g1,g0)
    c: Horizontal(g1)
    c: DistanceY(g0,g1) = 1.8
    c: Coincident(g2,g0)
    c: Coincident(g2,g1)
    c: PointOnObject(g2,g1)
FEATURE [Sketcher::SketchObject] Sketch053  label="Sketch_SplitPlug_P2_001"
  FullyConstrained = true
  MapMode = 5
  Placement = pos=(0,0,0) rot=(1,0,0;1.5708rad)
  Support = -> [XZ_Plane002]
  expr: Constraints[2] = <<params>>.xport_height_loc
  expr: Constraints[1] = <<params>>.xport_offset_loc
  expr: Constraints[0] = <<params>>.xport_plug_diam + 4 * <<params>>.xport_clip_size
  expr: Constraints[15] = <<params>>.std_wall_thick
  sketch-geometry (5):
    g0: Circle CenterX=43 CenterY=33.25 CenterZ=0 NormalX=0 NormalY=0 NormalZ=1 AngleXU=0 Radius=7.95
    g1: LineSegment StartX=35.1131 StartY=34.25 StartZ=0 EndX=50.8869 EndY=34.25 EndZ=0
    g2: LineSegment StartX=35.1131 StartY=32.25 StartZ=0 EndX=50.8869 EndY=32.25 EndZ=0
    g3: ArcOfCircle CenterX=43 CenterY=33.25 CenterZ=0 NormalX=0 NormalY=0 NormalZ=1 AngleXU=0 Radius=7.95 StartAngle=0.12612 EndAngle=3.01547
    g4: ArcOfCircle CenterX=43 CenterY=33.25 CenterZ=0 NormalX=0 NormalY=0 NormalZ=1 AngleXU=0 Radius=7.95 StartAngle=3.26771 EndAngle=6.15707
  constraints (16):
    c: Diameter(g0) = 15.9
    c: DistanceX(g-1,g0) = 43
    c: DistanceY(g-1,g0) = 33.25
    c: PointOnObject(g1,g0)
    c: PointOnObject(g1,g0)
    c: Horizontal(g1)
    c: PointOnObject(g2,g0)
    c: Horizontal(g2)
    c: Coincident(g3,g0)
    c: Coincident(g4,g3)
    c: Coincident(g3,g1)
    c: PointOnObject(g3,g1)
    c: Coincident(g4,g2)
    c: PointOnObject(g4,g2)
    c: Symmetric(g1,g2,g3)
    c: DistanceY(g2,g1) = 2
FEATURE [Sketcher::SketchObject] Sketch054  label="Sketch_SplitPlug_P2_002"
  FullyConstrained = true
  MapMode = 5
  Placement = pos=(0,0,0) rot=(1,0,0;1.5708rad)
  Support = -> [XZ_Plane002]
  expr: Constraints[15] = <<params>>.std_wall_thick
  expr: Constraints[0] = <<params>>.xport_plug_diam + 4 * <<params>>.xport_clip_size
  expr: Constraints[1] = <<params>>.xport_offset_loc
  expr: Constraints[2] = <<params>>.xport_height_loc
  sketch-geometry (8):
    g0: Circle CenterX=43 CenterY=33.25 CenterZ=0 NormalX=0 NormalY=0 NormalZ=1 AngleXU=0 Radius=7.95
    g1: LineSegment StartX=35.1131 StartY=34.25 StartZ=0 EndX=50.8869 EndY=34.25 EndZ=0
    g2: LineSegment StartX=35.1131 StartY=32.25 StartZ=0 EndX=50.8869 EndY=32.25 EndZ=0
    g3: ArcOfCircle CenterX=43 CenterY=33.25 CenterZ=0 NormalX=0 NormalY=0 NormalZ=1 AngleXU=0 Radius=7.95 StartAngle=0.12612 EndAngle=3.01547
    g4: ArcOfCircle CenterX=43 CenterY=33.25 CenterZ=0 NormalX=0 NormalY=0 NormalZ=1 AngleXU=0 Radius=7.95 StartAngle=3.26771 EndAngle=6.15707
    g5: LineSegment StartX=35.1131 StartY=32.25 StartZ=0 EndX=43 EndY=32.25 EndZ=0
    g6: LineSegment StartX=43 StartY=32.25 StartZ=0 EndX=43 EndY=41.2 EndZ=0
    g7: ArcOfCircle CenterX=43 CenterY=33.25 CenterZ=0 NormalX=0 NormalY=0 NormalZ=1 AngleXU=0 Radius=7.95 StartAngle=6.15707 EndAngle=7.85398
  constraints (26):
    c: Diameter(g0) = 15.9
    c: DistanceX(g-1,g0) = 43
    c: DistanceY(g-1,g0) = 33.25
    c: PointOnObject(g1,g0)
    c: PointOnObject(g1,g0)
    c: Horizontal(g1)
    c: PointOnObject(g2,g0)
    c: Horizontal(g2)
    c: Coincident(g3,g0)
    c: Coincident(g4,g3)
    c: Coincident(g3,g1)
    c: PointOnObject(g3,g1)
    c: Coincident(g4,g2)
    c: PointOnObject(g4,g2)
    c: Symmetric(g1,g2,g3)
    c: DistanceY(g2,g1) = 2
    c: Horizontal(g5)
    c: PointOnObject(g6,g0)
    c: Vertical(g6)
    c: PointOnObject(g4,g6)
    c: Coincident(g6,g5)
    c: PointOnObject(g5,g2)
    c: PointOnObject(g5,g4)
    c: Coincident(g7,g4)
    c: Coincident(g7,g6)
    c: PointOnObject(g7,g2)
FEATURE [Sketcher::SketchObject] Sketch055  label="Sketch_SplitPlug_P3_001"
  FullyConstrained = true
  MapMode = 5
  Placement = pos=(0,0,0) rot=(1,0,0;1.5708rad)
  Support = -> [XZ_Plane002]
  expr: Constraints[15] = <<params>>.std_wall_thick
  expr: Constraints[0] = <<params>>.xport_plug_diam + 4 * <<params>>.xport_clip_size
  expr: Constraints[1] = <<params>>.xport_offset_loc
  expr: Constraints[2] = <<params>>.xport_height_loc
  sketch-geometry (5):
    g0: Circle CenterX=43 CenterY=33.25 CenterZ=0 NormalX=0 NormalY=0 NormalZ=1 AngleXU=0 Radius=7.95
    g1: LineSegment StartX=35.1131 StartY=34.25 StartZ=0 EndX=50.8869 EndY=34.25 EndZ=0
    g2: LineSegment StartX=35.1131 StartY=32.25 StartZ=0 EndX=50.8869 EndY=32.25 EndZ=0
    g3: ArcOfCircle CenterX=43 CenterY=33.25 CenterZ=0 NormalX=0 NormalY=0 NormalZ=1 AngleXU=0 Radius=7.95 StartAngle=0.12612 EndAngle=3.01547
    g4: ArcOfCircle CenterX=43 CenterY=33.25 CenterZ=0 NormalX=0 NormalY=0 NormalZ=1 AngleXU=0 Radius=7.95 StartAngle=3.26771 EndAngle=6.15707
  constraints (16):
    c: Diameter(g0) = 15.9
    c: DistanceX(g-1,g0) = 43
    c: DistanceY(g-1,g0) = 33.25
    c: PointOnObject(g1,g0)
    c: PointOnObject(g1,g0)
    c: Horizontal(g1)
    c: PointOnObject(g2,g0)
    c: Horizontal(g2)
    c: Coincident(g3,g0)
    c: Coincident(g4,g3)
    c: Coincident(g3,g1)
    c: PointOnObject(g3,g1)
    c: Coincident(g4,g2)
    c: PointOnObject(g4,g2)
    c: Symmetric(g1,g2,g3)
    c: DistanceY(g2,g1) = 2
FEATURE [Sketcher::SketchObject] Sketch056  label="Sketch_SplitPlug_P3_002"
  FullyConstrained = true
  MapMode = 5
  Placement = pos=(0,0,0) rot=(1,0,0;1.5708rad)
  Support = -> [XZ_Plane002]
  expr: Constraints[2] = <<params>>.xport_height_loc
  expr: Constraints[1] = <<params>>.xport_offset_loc
  expr: Constraints[0] = <<params>>.xport_plug_diam + 4 * <<params>>.xport_clip_size
  expr: Constraints[15] = <<params>>.std_wall_thick
  sketch-geometry (8):
    g0: Circle CenterX=43 CenterY=33.25 CenterZ=0 NormalX=0 NormalY=0 NormalZ=1 AngleXU=0 Radius=7.95
    g1: LineSegment StartX=35.1131 StartY=34.25 StartZ=0 EndX=50.8869 EndY=34.25 EndZ=0
    g2: LineSegment StartX=35.1131 StartY=32.25 StartZ=0 EndX=50.8869 EndY=32.25 EndZ=0
    g3: ArcOfCircle CenterX=43 CenterY=33.25 CenterZ=0 NormalX=0 NormalY=0 NormalZ=1 AngleXU=0 Radius=7.95 StartAngle=0.12612 EndAngle=3.01547
    g4: ArcOfCircle CenterX=43 CenterY=33.25 CenterZ=0 NormalX=0 NormalY=0 NormalZ=1 AngleXU=0 Radius=7.95 StartAngle=3.26771 EndAngle=6.15707
    g5: ArcOfCircle CenterX=43 CenterY=33.25 CenterZ=0 NormalX=0 NormalY=0 NormalZ=1 AngleXU=0 Radius=7.95 StartAngle=1.5708 EndAngle=3.26771
    g6: LineSegment StartX=43 StartY=32.25 StartZ=0 EndX=43 EndY=41.2 EndZ=0
    g7: LineSegment StartX=43 StartY=32.25 StartZ=0 EndX=50.8869 EndY=32.25 EndZ=0
  constraints (26):
    c: Diameter(g0) = 15.9
    c: DistanceX(g-1,g0) = 43
    c: DistanceY(g-1,g0) = 33.25
    c: PointOnObject(g1,g0)
    c: PointOnObject(g1,g0)
    c: Horizontal(g1)
    c: PointOnObject(g2,g0)
    c: Horizontal(g2)
    c: Coincident(g3,g0)
    c: Coincident(g4,g3)
    c: Coincident(g3,g1)
    c: PointOnObject(g3,g1)
    c: Coincident(g4,g2)
    c: PointOnObject(g4,g2)
    c: Symmetric(g1,g2,g3)
    c: DistanceY(g2,g1) = 2
    c: Coincident(g5,g4)
    c: Coincident(g5,g4)
    c: PointOnObject(g6,g2)
    c: PointOnObject(g6,g3)
    c: Vertical(g6)
    c: PointOnObject(g4,g6)
    c: PointOnObject(g5,g6)
    c: Horizontal(g7)
    c: Coincident(g7,g6)
    c: PointOnObject(g7,g0)
FEATURE [Sketcher::SketchObject] Sketch057  label="Sketch_SplitPlug_P4_1"
  FullyConstrained = true
  MapMode = 5
  Placement = pos=(0,0,0) rot=(1,0,0;1.5708rad)
  Support = -> [XZ_Plane002]
  expr: Constraints[9] = <<params>>.std_wall_thick / 2 + <<params>>.std_min_wall_thick
  expr: Constraints[2] = <<params>>.xport_height_loc
  expr: Constraints[1] = <<params>>.xport_offset_loc
  expr: Constraints[0] = <<params>>.xport_plug_diam + 4 * <<params>>.xport_clip_size
  sketch-geometry (3):
    g0: Circle CenterX=43 CenterY=33.25 CenterZ=0 NormalX=0 NormalY=0 NormalZ=1 AngleXU=0 Radius=7.95
    g1: LineSegment StartX=35.2565 StartY=31.45 StartZ=0 EndX=50.7435 EndY=31.45 EndZ=0
    g2: ArcOfCircle CenterX=43 CenterY=33.25 CenterZ=0 NormalX=0 NormalY=0 NormalZ=1 AngleXU=0 Radius=7.95 StartAngle=6.05479 EndAngle=9.65317
  constraints (10):
    c: Diameter(g0) = 15.9
    c: DistanceX(g-1,g0) = 43
    c: DistanceY(g-1,g0) = 33.25
    c: PointOnObject(g1,g0)
    c: PointOnObject(g1,g0)
    c: Horizontal(g1)
    c: Coincident(g2,g0)
    c: Coincident(g2,g1)
    c: PointOnObject(g2,g1)
    c: DistanceY(g1,g2) = 1.8
FEATURE [PartDesign::Chamfer] Chamfer  label="Chamfer_PlateEdge"
  Angle = 45
  Base = -> SubtractiveLoft [Edge5,Edge4]
  BaseFeature = -> SubtractiveLoft
  ChamferType = 0
  FlipDirection = false
  Placement = pos=(0,0,0) rot=(1,0,0;1.5708rad)
  Size = 1
  Size2 = 1
  SupportTransform = false
FEATURE [PartDesign::Chamfer] Chamfer001  label="Chamfer_FrontEdge"
  Angle = 45
  Base = -> SubtractiveLoft001 [Edge13,Edge17,Edge8]
  BaseFeature = -> SubtractiveLoft001
  ChamferType = 0
  FlipDirection = false
  Placement = pos=(0,0,0) rot=(1,0,0;1.5708rad)
  Size = 1
  Size2 = 1
  SupportTransform = false
FEATURE [PartDesign::Body] Body001  label="PB3D_XPort_CoverPlug_Template"
  Group = -> [DatumPlane002,DatumPlane003,Sketch005,Sketch006,Sketch004,Pad001,Sketch014,Sketch015,Sketch016,Sketch017,Pad002,Pocket,SubtractiveLoft001,Sketch018,Sketch053,Sketch054,Sketch055,Sketch056,Sketch057,Chamfer001]
  Origin = -> Origin002
  Tip = -> Chamfer001
FEATURE [Sketcher::SketchObject] Sketch058  label="Sketch_HollowPlug001"
  FullyConstrained = true
  MapMode = 5
  Placement = pos=(0,0,0) rot=(1,0,0;1.5708rad)
  Support = -> [XZ_Plane003]
  expr: Constraints[0] = <<params>>.xport_plug_diam - 2 * <<params>>.xport_plug_wall_thick
  expr: Constraints[1] = <<params>>.xport_offset_loc
  expr: Constraints[2] = <<params>>.xport_height_loc
  sketch-geometry (1):
    g0: Circle CenterX=43 CenterY=33.25 CenterZ=0 NormalX=0 NormalY=0 NormalZ=1 AngleXU=0 Radius=5.55
  constraints (3):
    c: Diameter(g0) = 11.1
    c: DistanceX(g-1,g0) = 43
    c: DistanceY(g-1,g0) = 33.25
FEATURE [Sketcher::SketchObject] Sketch059  label="Sketch_Shell_Top_CutPlug001"
  FullyConstrained = true
  MapMode = 5
  Placement = pos=(0,0,42) rot=(0,0,1;0rad)
  expr: Constraints[142] = <<params>>.xport_plug_plate_thick
  expr: Constraints[79] = <<params>>.plate_width
  expr: Constraints[136] = <<params>>.xport_offset_loc
  expr: Constraints[120] = <<params>>.shell_overhang_leng
  expr: Constraints[77] = <<params>>.back_vert_edge
  expr: Constraints[155] = <<params>>.shell_wall_thick + <<params>>.std_tol_interfere
  expr: Constraints[63] = <<params>>.std_rad
  expr: Constraints[143] = <<params>>.std_wall_thick
  expr: Constraints[42] = <<params>>.tail_width
  expr: Constraints[78] = <<params>>.wheel_well_clearance
  expr: Constraints[153] = <<params>>.xport_plug_diam / 2
  expr: Constraints[152] = <<params>>.xport_plug_diam / 2
  expr: Constraints[80] = <<params>>.std_rad
  expr: Constraints[117] = <<params>>.shell_overhang_leng
  expr: Constraints[76] = <<params>>.front_vert_edge
  expr: Constraints[130] = <<params>>.plate_length / 2 + <<params>>.std_wall_thick
  expr: Constraints[41] = <<params>>.tail_rad
  expr: Constraints[187] = <<params>>.xport_clip_size
  expr: Constraints[129] = <<params>>.std_wall_thick
  expr: Constraints[40] = <<params>>.plate_length
  expr: Constraints[189] = <<params>>.shell_overhang_leng
  expr: Constraints[65] = <<params>>.std_rad
  expr: Constraints[186] = <<params>>.xport_clip_size
  expr: Constraints[81] = <<params>>.std_rad
  expr: Constraints[88] = Spreadsheet.shell_overhang_leng
  expr: Constraints[116] = Spreadsheet.shell_overhang_leng
  expr: Constraints[36] = <<params>>.wheel_well_plate_width - 2 * Spreadsheet.shell_overhang_leng
  expr: Constraints[47] = <<params>>.front_diameter
  sketch-geometry (80):
    g0: LineSegment StartX=-43.5 StartY=17 StartZ=0 EndX=-43.5 EndY=-17 EndZ=0
    g1: LineSegment StartX=43.5 StartY=17 StartZ=0 EndX=43.5 EndY=-17 EndZ=0
    g2: LineSegment StartX=-43.5 StartY=0 StartZ=0 EndX=43.5 EndY=0 EndZ=0
    g3: LineSegment StartX=-50.5 StartY=-24 StartZ=0 EndX=50.5 EndY=-24 EndZ=0
    g4: LineSegment StartX=-50.5 StartY=24 StartZ=0 EndX=50.5 EndY=24 EndZ=0
    g5: LineSegment StartX=-50.5 StartY=-24 StartZ=0 EndX=-75.5 EndY=-24 EndZ=0
    g6: LineSegment StartX=50.5 StartY=-24 StartZ=0 EndX=75.5 EndY=-24 EndZ=0
    g7: ArcOfCircle CenterX=0 CenterY=52.6846 CenterZ=0 NormalX=0 NormalY=0 NormalZ=1 AngleXU=0 Radius=112.5 StartAngle=3.96017 EndAngle=5.4646
    g8: LineSegment StartX=-50.5 StartY=24 StartZ=0 EndX=-75.5 EndY=24 EndZ=0
    g9: LineSegment StartX=50.5 StartY=24 StartZ=0 EndX=75.5 EndY=24 EndZ=0
    g10: LineSegment StartX=-77.1162 StartY=42.1781 StartZ=0 EndX=-29.0404 EndY=108.13 EndZ=0
    g11: LineSegment StartX=-25 StartY=110.185 StartZ=0 EndX=25 EndY=110.185 EndZ=0
    g12: LineSegment StartX=29.0404 StartY=108.13 StartZ=0 EndX=77.1162 EndY=42.1781 EndZ=0
    g13: LineSegment StartX=0 StartY=0 StartZ=0 EndX=0 EndY=110.185 EndZ=0
    g14: ArcOfCircle CenterX=-25 CenterY=105.185 CenterZ=0 NormalX=0 NormalY=0 NormalZ=1 AngleXU=0 Radius=5 StartAngle=1.5708 EndAngle=2.5117
    g15: ArcOfCircle CenterX=25 CenterY=105.185 CenterZ=0 NormalX=0 NormalY=0 NormalZ=1 AngleXU=0 Radius=5 StartAngle=0.629894 EndAngle=1.5708
    g16: ArcOfCircle CenterX=-50.5 CenterY=17 CenterZ=0 NormalX=0 NormalY=0 NormalZ=1 AngleXU=0 Radius=7 StartAngle=0 EndAngle=1.5708
    g17: ArcOfCircle CenterX=-50.5 CenterY=-17 CenterZ=0 NormalX=0 NormalY=0 NormalZ=1 AngleXU=0 Radius=7 StartAngle=4.71239 EndAngle=6.28319
    g18: ArcOfCircle CenterX=50.5 CenterY=-17 CenterZ=0 NormalX=0 NormalY=0 NormalZ=1 AngleXU=0 Radius=7 StartAngle=3.14159 EndAngle=4.71239
    g19: ArcOfCircle CenterX=50.5 CenterY=17 CenterZ=0 NormalX=0 NormalY=0 NormalZ=1 AngleXU=0 Radius=7 StartAngle=1.5708 EndAngle=3.14159
    g20: GeomPoint X=0 Y=-59.8154 Z=0
    g21: Circle CenterX=0 CenterY=52.6846 CenterZ=0 NormalX=0 NormalY=0 NormalZ=1 AngleXU=0 Radius=112.5
    g22: LineSegment StartX=77.5 StartY=26 StartZ=0 EndX=77.5 EndY=41 EndZ=0
    g23: LineSegment StartX=77.5 StartY=-26 StartZ=0 EndX=77.5 EndY=-28 EndZ=0
    g24: LineSegment StartX=-77.5 StartY=-28 StartZ=0 EndX=-77.5 EndY=-26 EndZ=0
    g25: LineSegment StartX=-77.5 StartY=26 StartZ=0 EndX=-77.5 EndY=41 EndZ=0
    g26: ArcOfCircle CenterX=75.5 CenterY=-28 CenterZ=0 NormalX=0 NormalY=0 NormalZ=1 AngleXU=0 Radius=2 StartAngle=5.4646 EndAngle=6.28319
    g27: ArcOfCircle CenterX=75.5 CenterY=-26 CenterZ=0 NormalX=0 NormalY=0 NormalZ=1 AngleXU=0 Radius=2 StartAngle=0 EndAngle=1.5708
    g28: ArcOfCircle CenterX=-75.5 CenterY=-28 CenterZ=0 NormalX=0 NormalY=0 NormalZ=1 AngleXU=0 Radius=2 StartAngle=3.14159 EndAngle=3.96017
    g29: ArcOfCircle CenterX=-75.5 CenterY=-26 CenterZ=0 NormalX=0 NormalY=0 NormalZ=1 AngleXU=0 Radius=2 StartAngle=1.5708 EndAngle=3.14159
    g30: ArcOfCircle CenterX=75.5 CenterY=26 CenterZ=0 NormalX=0 NormalY=0 NormalZ=1 AngleXU=0 Radius=2 StartAngle=4.71239 EndAngle=6.28319
    g31: ArcOfCircle CenterX=75.5 CenterY=41 CenterZ=0 NormalX=0 NormalY=0 NormalZ=1 AngleXU=0 Radius=2 StartAngle=9e-16 EndAngle=0.629894
    g32: ArcOfCircle CenterX=-75.5 CenterY=26 CenterZ=0 NormalX=0 NormalY=0 NormalZ=1 AngleXU=0 Radius=2 StartAngle=3.14159 EndAngle=4.71239
    g33: ArcOfCircle CenterX=-75.5 CenterY=41 CenterZ=0 NormalX=0 NormalY=0 NormalZ=1 AngleXU=0 Radius=2 StartAngle=2.5117 EndAngle=3.14159
    g34: LineSegment StartX=77.5 StartY=26 StartZ=0 EndX=77.5 EndY=-26 EndZ=0
    g35: LineSegment StartX=-77.5 StartY=26 StartZ=0 EndX=-77.5 EndY=-26 EndZ=0
    g36: LineSegment StartX=-17.8805 StartY=96.1846 StartZ=0 EndX=17.8805 EndY=96.1846 EndZ=0
    g37: GeomPoint X=0 Y=96.1846 Z=0
    g38: LineSegment StartX=-21.921 StartY=94.1299 StartZ=0 EndX=-63.1162 EndY=37.617 EndZ=0
    g39: LineSegment StartX=-63.5 StartY=36.4389 StartZ=0 EndX=-63.5 EndY=-21.6794 EndZ=0
    g40: LineSegment StartX=21.921 StartY=94.1299 StartZ=0 EndX=63.1162 EndY=37.617 EndZ=0
    g41: LineSegment StartX=63.5 StartY=36.4389 StartZ=0 EndX=63.5 EndY=-21.6794 EndZ=0
    g42: ArcOfCircle CenterX=0 CenterY=52.6846 CenterZ=0 NormalX=0 NormalY=0 NormalZ=1 AngleXU=0 Radius=98.5 StartAngle=4.02139 EndAngle=5.40339
    g43: LineSegment StartX=-63.5 StartY=36.4389 StartZ=0 EndX=63.5 EndY=36.4389 EndZ=0
    g44: GeomPoint X=0 Y=-45.8154 Z=0
    g45: ArcOfCircle CenterX=-17.8805 CenterY=91.1846 CenterZ=0 NormalX=0 NormalY=0 NormalZ=1 AngleXU=0 Radius=5 StartAngle=1.5708 EndAngle=2.5117
    g46: ArcOfCircle CenterX=17.8805 CenterY=91.1846 CenterZ=0 NormalX=0 NormalY=0 NormalZ=1 AngleXU=0 Radius=5 StartAngle=0.629894 EndAngle=1.5708
    g47: ArcOfCircle CenterX=61.5 CenterY=36.4389 CenterZ=0 NormalX=0 NormalY=0 NormalZ=1 AngleXU=0 Radius=2 StartAngle=0 EndAngle=0.629894
    g48: ArcOfCircle CenterX=-61.5 CenterY=36.4389 CenterZ=0 NormalX=0 NormalY=0 NormalZ=1 AngleXU=0 Radius=2 StartAngle=2.5117 EndAngle=3.14159
    g49: ArcOfCircle CenterX=61.5 CenterY=-21.6794 CenterZ=0 NormalX=0 NormalY=0 NormalZ=1 AngleXU=0 Radius=2 StartAngle=5.40339 EndAngle=6.28319
    g50: ArcOfCircle CenterX=-61.5 CenterY=-21.6794 CenterZ=0 NormalX=0 NormalY=0 NormalZ=1 AngleXU=0 Radius=2 StartAngle=3.14159 EndAngle=4.02139
    g51: LineSegment StartX=-29.0404 StartY=108.13 StartZ=0 EndX=-17.7272 EndY=99.883 EndZ=0
    g52: LineSegment StartX=-2 StartY=2 StartZ=0 EndX=-2 EndY=-87 EndZ=0
    g53: LineSegment StartX=-2 StartY=-87 StartZ=0 EndX=63.5 EndY=-87 EndZ=0
    g54: LineSegment StartX=63.5 StartY=-87 StartZ=0 EndX=63.5 EndY=-27.7653 EndZ=0
    g55: LineSegment StartX=63.5 StartY=2 StartZ=0 EndX=-2 EndY=2 EndZ=0
    g56: LineSegment StartX=0 StartY=-58.5771 StartZ=0 EndX=63.5 EndY=-27.7653 EndZ=0
    g57: LineSegment StartX=63.5 StartY=-22.6148 StartZ=0 EndX=63.5 EndY=-27.7653 EndZ=0
    g58: GeomPoint X=43 Y=-35.934 Z=0
    g59: LineSegment StartX=0 StartY=52.6846 StartZ=0 EndX=43 EndY=-35.934 EndZ=0
    g60: LineSegment StartX=43 StartY=-35.934 StartZ=0 EndX=43.6985 EndY=-37.3735 EndZ=0
    g61: LineSegment StartX=0 StartY=-58.5771 StartZ=0 EndX=-1.81e-14 EndY=-45.8154 EndZ=0
    g62: LineSegment StartX=63.5 StartY=2 StartZ=0 EndX=63.5 EndY=-22.6148 EndZ=0
    g63: LineSegment StartX=36.65 StartY=-38.7431 StartZ=0 EndX=36.65 EndY=-36.5431 EndZ=0
    g64: LineSegment StartX=49.35 StartY=-30.3611 StartZ=0 EndX=49.35 EndY=-32.5611 EndZ=0
    g65: LineSegment StartX=36.65 StartY=-36.5431 StartZ=0 EndX=35.9672 EndY=-35.8603 EndZ=0
    g66: LineSegment StartX=35.9672 StartY=-35.2946 StartZ=0 EndX=36.65 EndY=-34.6118 EndZ=0
    g67: LineSegment StartX=49.35 StartY=-30.3611 StartZ=0 EndX=50.0328 EndY=-29.6783 EndZ=0
    g68: LineSegment StartX=50.0328 StartY=-29.1126 StartZ=0 EndX=49.35 EndY=-28.4297 EndZ=0
    g69: LineSegment StartX=49.35 StartY=-28.4297 StartZ=0 EndX=36.65 EndY=-34.6118 EndZ=0
    g70: ArcOfCircle CenterX=36.25 CenterY=-35.5775 CenterZ=0 NormalX=0 NormalY=0 NormalZ=1 AngleXU=0 Radius=0.4 StartAngle=2.35619 EndAngle=3.92699
    g71: ArcOfCircle CenterX=49.75 CenterY=-29.3954 CenterZ=0 NormalX=0 NormalY=0 NormalZ=1 AngleXU=0 Radius=0.4 StartAngle=5.49779 EndAngle=7.06858
    g72: LineSegment StartX=36.65 StartY=-36.5431 StartZ=0 EndX=36.65 EndY=-34.6118 EndZ=0
    g73: GeomPoint X=35.85 Y=-35.5775 Z=0
    g74: GeomPoint X=50.15 Y=-29.3954 Z=0
    g75: LineSegment StartX=49.35 StartY=-30.3611 StartZ=0 EndX=49.35 EndY=-28.4297 EndZ=0
    g76: LineSegment StartX=50.15 StartY=-29.3954 StartZ=0 EndX=49.35 EndY=-29.3954 EndZ=0
    g77: LineSegment StartX=36.65 StartY=-35.5775 StartZ=0 EndX=35.85 EndY=-35.5775 EndZ=0
    g78: ArcOfCircle CenterX=0 CenterY=52.6846 CenterZ=0 NormalX=0 NormalY=0 NormalZ=1 AngleXU=0 Radius=98.5 StartAngle=4.71239 EndAngle=5.09364
    g79: ArcOfCircle CenterX=0 CenterY=52.6846 CenterZ=0 NormalX=0 NormalY=0 NormalZ=1 AngleXU=0 Radius=98.5 StartAngle=5.23716 EndAngle=5.41298
  constraints (201):
    c: Vertical(g0)
    c: Vertical(g1)
    c: Horizontal(g2)
    c: Symmetric(g2,g2,g-1)
    c: Horizontal(g3)
    c: Horizontal(g5)
    c: Horizontal(g6)
    c: PointOnObject(g7,g-2)
    c: Horizontal(g8)
    c: Horizontal(g9)
    c: Horizontal(g11)
    c: Coincident(g13,g-1)
    c: PointOnObject(g13,g-2)
    c: Tangent(g10,g14) = 1.5708
    c: Tangent(g11,g14) = 1.5708
    c: Tangent(g11,g15) = 1.5708
    c: Tangent(g12,g15) = 1.5708
    c: Tangent(g8,g16) = -1.5708
    c: Tangent(g0,g16) = 1.5708
    c: Tangent(g5,g17) = 1.5708
    c: Tangent(g0,g17) = 1.5708
    c: Tangent(g1,g18) = -1.5708
    c: Tangent(g6,g18) = -1.5708
    c: Tangent(g1,g19) = -1.5708
    c: Tangent(g9,g19) = 1.5708
    c: Equal(g15,g14)
    c: Symmetric(g11,g11,g13)
    c: Equal(g18,g19)
    c: Equal(g19,g16)
    c: Equal(g16,g17)
    c: PointOnObject(g20,g-2)
    c: PointOnObject(g20,g7)
    c: Coincident(g4,g8)
    c: Coincident(g4,g9)
    c: Coincident(g3,g6)
    c: Coincident(g3,g5)
    c: DistanceX(g2,g2) = 87
    c: Symmetric(g0,g0,g2)
    c: Symmetric(g1,g1,g2)
    c: Radius(g19) = 7
    c: DistanceY(g20,g11) = 170
    c: Radius(g15) = 5
    c: DistanceX(g11,g11) = 50
    c: Equal(g9,g8)
    c: Equal(g9,g6)
    c: Coincident(g21,g7)
    c: PointOnObject(g20,g21)
    c: Diameter(g21) = 225
    c: Vertical(g22)
    c: Vertical(g23)
    c: Vertical(g24)
    c: Vertical(g25)
    c: Equal(g5,g8)
    c: Equal(g10,g12)
    c: Tangent(g7,g26) = -1.5708
    c: Tangent(g23,g26) = 1.5708
    c: Tangent(g23,g27) = 1.5708
    c: Tangent(g6,g27) = 1.5708
    c: Tangent(g7,g28) = -1.5708
    c: Tangent(g24,g28) = 1.5708
    c: Tangent(g24,g29) = 1.5708
    c: Tangent(g5,g29) = -1.5708
    c: Equal(g29,g27)
    c: Radius(g27) = 2
    c: Equal(g26,g28)
    c: Radius(g26) = 2
    c: Tangent(g9,g30) = -1.5708
    c: Tangent(g22,g30) = -1.5708
    c: Tangent(g22,g31) = -1.5708
    c: Tangent(g12,g31) = 1.5708
    c: Tangent(g8,g32) = 1.5708
    c: Tangent(g25,g32) = 1.5708
    c: Tangent(g10,g33) = 1.5708
    c: Tangent(g25,g33) = 1.5708
    c: Equal(g30,g32)
    c: Equal(g31,g33)
    c: DistanceY(g23,g23) = 2
    c: DistanceY(g22,g22) = 15
    c: DistanceY(g6,g9) = 48
    c: DistanceX(g24,g23) = 155
    c: Radius(g30) = 2
    c: Radius(g31) = 2
    c: Coincident(g34,g22)
    c: Coincident(g34,g23)
    c: Coincident(g35,g25)
    c: Coincident(g35,g24)
    c: Horizontal(g36)
    c: PointOnObject(g37,g13)
    c: DistanceY(g37,g13) = 14
    c: Vertical(g39)
    c: Vertical(g41)
    c: Horizontal(g43)
    c: Parallel(g40,g12)
    c: PointOnObject(g44,g-2)
    c: PointOnObject(g44,g42)
    c: Tangent(g38,g45) = -1.5708
    c: Tangent(g36,g45) = 1.5708
    c: Tangent(g40,g46) = 1.5708
    c: Tangent(g36,g46) = 1.5708
    c: Tangent(g41,g47) = 1.5708
    c: Tangent(g40,g47) = 1.5708
    c: Tangent(g39,g48) = -1.5708
    c: Tangent(g38,g48) = -1.5708
    c: Tangent(g42,g49) = -1.5708
    c: Tangent(g41,g49) = 1.5708
    c: Tangent(g42,g50) = -1.5708
    c: Tangent(g39,g50) = -1.5708
    c: Coincident(g43,g39)
    c: Coincident(g43,g41)
    c: Equal(g15,g46)
    c: Equal(g46,g45)
    c: Symmetric(g36,g36,g37)
    c: Equal(g31,g47)
    c: Equal(g26,g49)
    c: Equal(g50,g29)
    c: Equal(g48,g32)
    c: DistanceY(g20,g44) = 14
    c: DistanceX(g41,g22) = 14
    c: PointOnObject(g51,g38)
    c: Perpendicular(g38,g51)
    c: Distance(g51) = 14
    c: Coincident(g51,g10)
    c: Vertical(g52)
    c: Coincident(g53,g52)
    c: Horizontal(g53)
    c: Coincident(g54,g53)
    c: Vertical(g54)
    c: Coincident(g55,g52)
    c: Horizontal(g55)
    c: DistanceY(g-1,g52) = 2
    c: DistanceY(g52,g-1) = 87
    c: Coincident(g54,g56)
    c: Coincident(g57,g54)
    c: Vertical(g57)
    c: PointOnObject(g56,g-2)
    c: PointOnObject(g58,g42)
    c: DistanceX(g-1,g58) = 43
    c: Coincident(g59,g58)
    c: Coincident(g60,g58)
    c: PointOnObject(g60,g56)
    c: Parallel(g60,g59)
    c: Perpendicular(g56,g60)
    c: Distance(g60) = 1.6
    c: DistanceX(g52,g-1) = 2
    c: Coincident(g61,g56)
    c: PointOnObject(g61,g-2)
    c: Vertical(g62)
    c: Coincident(g62,g55)
    c: PointOnObject(g55,g41)
    c: Vertical(g63)
    c: Vertical(g64)
    c: Equal(g64,g63)
    c: DistanceX(g63,g58) = 6.35
    c: DistanceX(g58,g64) = 6.35
    c: PointOnObject(g61,g42)
    c: DistanceY(g64,g64) = 2.2
    c: Coincident(g65,g63)
    c: Coincident(g67,g64)
    c: Coincident(g69,g68)
    c: Coincident(g69,g66)
    c: Tangent(g65,g70) = 1.5708
    c: Tangent(g66,g70) = 1.5708
    c: Tangent(g67,g71) = -1.5708
    c: Tangent(g68,g71) = -1.5708
    c: Coincident(g72,g63)
    c: Coincident(g72,g66)
    c: PointOnObject(g73,g70)
    c: PointOnObject(g74,g71)
    c: Coincident(g75,g64)
    c: Coincident(g75,g68)
    c: Vertical(g75)
    c: Coincident(g76,g74)
    c: PointOnObject(g76,g75)
    c: Horizontal(g76)
    c: PointOnObject(g71,g76)
    c: Equal(g67,g68)
    c: Equal(g68,g66)
    c: Equal(g65,g66)
    c: Equal(g71,g70)
    c: Vertical(g72)
    c: PointOnObject(g77,g72)
    c: Coincident(g77,g73)
    c: Horizontal(g77)
    c: PointOnObject(g70,g77)
    c: Angle(g65,g66) = 1.5708
    c: Angle(g68,g67) = 1.5708
    c: DistanceX(g76,g74) = 0.8
    c: Diameter(g71) = 0.8
    c: Coincident(g42,g7)
    c: DistanceX(g25,g39) = 14
    c: Coincident(g59,g7)
    c: Coincident(g57,g62)
    c: PointOnObject(g63,g42)
    c: PointOnObject(g64,g42)
    c: PointOnObject(g62,g42)
    c: Coincident(g78,g7)
    c: Coincident(g79,g78)
    c: Coincident(g79,g62)
    c: Coincident(g78,g61)
    c: PointOnObject(g78,g63)
    c: PointOnObject(g79,g64)
FEATURE [Sketcher::SketchObject] Sketch062  label="Sketch_Shell_Vert_CutPlug001"
  FullyConstrained = true
  MapMode = 5
  Placement = pos=(0,0,10) rot=(0,0,1;0rad)
  expr: Constraints[110] = <<params>>.xport_plug_plate_thick
  expr: Constraints[77] = <<params>>.back_vert_edge
  expr: Constraints[137] = <<params>>.shell_wall_thick + <<params>>.std_tol_clear
  expr: Constraints[134] = <<params>>.xport_plug_diam / 2
  expr: Constraints[47] = <<params>>.front_diameter
  expr: Constraints[170] = <<params>>.xport_clip_size
  expr: Constraints[63] = <<params>>.std_rad
  expr: Constraints[103] = <<params>>.xport_offset_loc
  expr: Constraints[101] = <<params>>.plate_length / 2 + <<params>>.std_wall_thick
  expr: Constraints[80] = <<params>>.std_rad
  expr: Constraints[36] = <<params>>.wheel_well_plate_width
  expr: Constraints[40] = <<params>>.plate_length
  expr: Constraints[65] = <<params>>.std_rad
  expr: Constraints[78] = <<params>>.wheel_well_clearance
  expr: Constraints[42] = <<params>>.tail_width
  expr: Constraints[135] = <<params>>.xport_plug_diam / 2
  expr: Constraints[79] = <<params>>.plate_width
  expr: Constraints[76] = <<params>>.front_vert_edge
  expr: Constraints[118] = <<params>>.std_wall_thick
  expr: Constraints[100] = <<params>>.std_wall_thick
  expr: Constraints[81] = <<params>>.std_rad
  expr: Constraints[41] = <<params>>.tail_rad
  expr: Constraints[168] = <<params>>.xport_clip_size
  sketch-geometry (68):
    g0: LineSegment StartX=-57.5 StartY=17 StartZ=0 EndX=-57.5 EndY=-17 EndZ=0
    g1: LineSegment StartX=57.5 StartY=17 StartZ=0 EndX=57.5 EndY=-17 EndZ=0
    g2: LineSegment StartX=-57.5 StartY=0 StartZ=0 EndX=57.5 EndY=0 EndZ=0
    g3: LineSegment StartX=-64.5 StartY=-24 StartZ=0 EndX=64.5 EndY=-24 EndZ=0
    g4: LineSegment StartX=-64.5 StartY=24 StartZ=0 EndX=64.5 EndY=24 EndZ=0
    g5: LineSegment StartX=-64.5 StartY=-24 StartZ=0 EndX=-75.5 EndY=-24 EndZ=0
    g6: LineSegment StartX=64.5 StartY=-24 StartZ=0 EndX=75.5 EndY=-24 EndZ=0
    g7: ArcOfCircle CenterX=0 CenterY=52.6846 CenterZ=0 NormalX=0 NormalY=0 NormalZ=1 AngleXU=0 Radius=112.5 StartAngle=3.96017 EndAngle=5.4646
    g8: LineSegment StartX=-64.5 StartY=24 StartZ=0 EndX=-75.5 EndY=24 EndZ=0
    g9: LineSegment StartX=64.5 StartY=24 StartZ=0 EndX=75.5 EndY=24 EndZ=0
    g10: LineSegment StartX=-77.1162 StartY=42.1781 StartZ=0 EndX=-29.0404 EndY=108.13 EndZ=0
    g11: LineSegment StartX=-25 StartY=110.185 StartZ=0 EndX=25 EndY=110.185 EndZ=0
    g12: LineSegment StartX=29.0404 StartY=108.13 StartZ=0 EndX=77.1162 EndY=42.1781 EndZ=0
    g13: LineSegment StartX=0 StartY=0 StartZ=0 EndX=0 EndY=110.185 EndZ=0
    g14: ArcOfCircle CenterX=-25 CenterY=105.185 CenterZ=0 NormalX=0 NormalY=0 NormalZ=1 AngleXU=0 Radius=5 StartAngle=1.5708 EndAngle=2.5117
    g15: ArcOfCircle CenterX=25 CenterY=105.185 CenterZ=0 NormalX=0 NormalY=0 NormalZ=1 AngleXU=0 Radius=5 StartAngle=0.629894 EndAngle=1.5708
    g16: ArcOfCircle CenterX=-64.5 CenterY=17 CenterZ=0 NormalX=0 NormalY=0 NormalZ=1 AngleXU=0 Radius=7 StartAngle=0 EndAngle=1.5708
    g17: ArcOfCircle CenterX=-64.5 CenterY=-17 CenterZ=0 NormalX=0 NormalY=0 NormalZ=1 AngleXU=0 Radius=7 StartAngle=4.71239 EndAngle=6.28319
    g18: ArcOfCircle CenterX=64.5 CenterY=-17 CenterZ=0 NormalX=0 NormalY=0 NormalZ=1 AngleXU=0 Radius=7 StartAngle=3.14159 EndAngle=4.71239
    g19: ArcOfCircle CenterX=64.5 CenterY=17 CenterZ=0 NormalX=0 NormalY=0 NormalZ=1 AngleXU=0 Radius=7 StartAngle=1.5708 EndAngle=3.14159
    g20: GeomPoint X=0 Y=-59.8154 Z=0
    g21: Circle CenterX=0 CenterY=52.6846 CenterZ=0 NormalX=0 NormalY=0 NormalZ=1 AngleXU=0 Radius=112.5
    g22: LineSegment StartX=77.5 StartY=26 StartZ=0 EndX=77.5 EndY=41 EndZ=0
    g23: LineSegment StartX=77.5 StartY=-26 StartZ=0 EndX=77.5 EndY=-28 EndZ=0
    g24: LineSegment StartX=-77.5 StartY=-28 StartZ=0 EndX=-77.5 EndY=-26 EndZ=0
    g25: LineSegment StartX=-77.5 StartY=26 StartZ=0 EndX=-77.5 EndY=41 EndZ=0
    g26: ArcOfCircle CenterX=75.5 CenterY=-28 CenterZ=0 NormalX=0 NormalY=0 NormalZ=1 AngleXU=0 Radius=2 StartAngle=5.4646 EndAngle=6.28319
    g27: ArcOfCircle CenterX=75.5 CenterY=-26 CenterZ=0 NormalX=0 NormalY=0 NormalZ=1 AngleXU=0 Radius=2 StartAngle=0 EndAngle=1.5708
    g28: ArcOfCircle CenterX=-75.5 CenterY=-28 CenterZ=0 NormalX=0 NormalY=0 NormalZ=1 AngleXU=0 Radius=2 StartAngle=3.14159 EndAngle=3.96017
    g29: ArcOfCircle CenterX=-75.5 CenterY=-26 CenterZ=0 NormalX=0 NormalY=0 NormalZ=1 AngleXU=0 Radius=2 StartAngle=1.5708 EndAngle=3.14159
    g30: ArcOfCircle CenterX=75.5 CenterY=26 CenterZ=0 NormalX=0 NormalY=0 NormalZ=1 AngleXU=0 Radius=2 StartAngle=4.71239 EndAngle=6.28319
    g31: ArcOfCircle CenterX=75.5 CenterY=41 CenterZ=0 NormalX=0 NormalY=0 NormalZ=1 AngleXU=0 Radius=2 StartAngle=4e-16 EndAngle=0.629894
    g32: ArcOfCircle CenterX=-75.5 CenterY=26 CenterZ=0 NormalX=0 NormalY=0 NormalZ=1 AngleXU=0 Radius=2 StartAngle=3.14159 EndAngle=4.71239
    g33: ArcOfCircle CenterX=-75.5 CenterY=41 CenterZ=0 NormalX=0 NormalY=0 NormalZ=1 AngleXU=0 Radius=2 StartAngle=2.5117 EndAngle=3.14159
    g34: LineSegment StartX=77.5 StartY=26 StartZ=0 EndX=77.5 EndY=-26 EndZ=0
    g35: LineSegment StartX=-77.5 StartY=26 StartZ=0 EndX=-77.5 EndY=-26 EndZ=0
    g36: LineSegment StartX=77.5 StartY=41 StartZ=0 EndX=77.5 EndY=-28 EndZ=0
    g37: LineSegment StartX=-77.5 StartY=41 StartZ=0 EndX=-77.5 EndY=-28 EndZ=0
    g38: ArcOfCircle CenterX=0 CenterY=52.6846 CenterZ=0 NormalX=0 NormalY=0 NormalZ=1 AngleXU=0 Radius=112.5 StartAngle=4.71239 EndAngle=5.4646
    g39: LineSegment StartX=-2 StartY=2 StartZ=0 EndX=-2 EndY=-87 EndZ=0
    g40: LineSegment StartX=76.8665 StartY=-38.9967 StartZ=0 EndX=76.8665 EndY=-87 EndZ=0
    g41: LineSegment StartX=-2 StartY=-87 StartZ=0 EndX=76.8665 EndY=-87 EndZ=0
    g42: LineSegment StartX=-2 StartY=2 StartZ=0 EndX=77.5 EndY=2 EndZ=0
    g43: LineSegment StartX=0 StartY=-70.7909 StartZ=0 EndX=76.8665 EndY=-38.9967 EndZ=0
    g44: GeomPoint X=43 Y=-51.2734 Z=0
    g45: LineSegment StartX=0 StartY=52.6846 StartZ=0 EndX=43 EndY=-51.2734 EndZ=0
    g46: LineSegment StartX=43.6116 StartY=-52.7519 StartZ=0 EndX=43 EndY=-51.2734 EndZ=0
    g47: LineSegment StartX=76.8665 StartY=-38.9967 StartZ=0 EndX=76.8665 EndY=-29.4604 EndZ=0
    g48: LineSegment StartX=-2.07e-14 StartY=-59.8154 StartZ=0 EndX=0 EndY=-70.7909 EndZ=0
    g49: LineSegment StartX=0 StartY=-70.7909 StartZ=0 EndX=-2.07e-14 EndY=-59.8154 EndZ=0
    g50: LineSegment StartX=77.5 StartY=2 StartZ=0 EndX=77.5 EndY=-28.863 EndZ=0
    g51: ArcOfCircle CenterX=0 CenterY=52.6846 CenterZ=0 NormalX=0 NormalY=0 NormalZ=1 AngleXU=0 Radius=112.5 StartAngle=4.71239 EndAngle=5.04422
    g52: ArcOfCircle CenterX=0 CenterY=52.6846 CenterZ=0 NormalX=0 NormalY=0 NormalZ=1 AngleXU=0 Radius=112.5 StartAngle=5.1665 EndAngle=5.47234
    g53: LineSegment StartX=36.65 StartY=-53.6781 StartZ=0 EndX=36.65 EndY=-51.3781 EndZ=0
    g54: LineSegment StartX=49.35 StartY=-48.4135 StartZ=0 EndX=49.35 EndY=-46.1135 EndZ=0
    g55: LineSegment StartX=36.65 StartY=-51.3781 StartZ=0 EndX=35.9672 EndY=-50.6953 EndZ=0
    g56: LineSegment StartX=35.9672 StartY=-50.1296 StartZ=0 EndX=36.65 EndY=-49.4468 EndZ=0
    g57: ArcOfCircle CenterX=36.25 CenterY=-50.4125 CenterZ=0 NormalX=0 NormalY=0 NormalZ=1 AngleXU=0 Radius=0.4 StartAngle=2.35619 EndAngle=3.92699
    g58: LineSegment StartX=49.35 StartY=-46.1135 StartZ=0 EndX=50.0328 EndY=-45.4307 EndZ=0
    g59: LineSegment StartX=50.0328 StartY=-44.865 StartZ=0 EndX=49.35 EndY=-44.1822 EndZ=0
    g60: ArcOfCircle CenterX=49.75 CenterY=-45.1479 CenterZ=0 NormalX=0 NormalY=0 NormalZ=1 AngleXU=0 Radius=0.4 StartAngle=5.49779 EndAngle=7.06858
    g61: LineSegment StartX=36.65 StartY=-51.3781 StartZ=0 EndX=36.65 EndY=-49.4468 EndZ=0
    g62: LineSegment StartX=49.35 StartY=-46.1135 StartZ=0 EndX=49.35 EndY=-44.1822 EndZ=0
    g63: LineSegment StartX=36.65 StartY=-49.4468 StartZ=0 EndX=49.35 EndY=-44.1822 EndZ=0
    g64: GeomPoint X=50.15 Y=-45.1479 Z=0
    g65: GeomPoint X=35.85 Y=-50.4125 Z=0
    g66: LineSegment StartX=35.85 StartY=-50.4125 StartZ=0 EndX=36.65 EndY=-50.4125 EndZ=0
    g67: LineSegment StartX=50.15 StartY=-45.1479 StartZ=0 EndX=49.35 EndY=-45.1479 EndZ=0
  constraints (171):
    c: Vertical(g0)
    c: Vertical(g1)
    c: Horizontal(g2)
    c: Symmetric(g2,g2,g-1)
    c: Horizontal(g3)
    c: Horizontal(g5)
    c: Horizontal(g6)
    c: PointOnObject(g7,g-2)
    c: Horizontal(g8)
    c: Horizontal(g9)
    c: Horizontal(g11)
    c: Coincident(g13,g-1)
    c: PointOnObject(g13,g-2)
    c: Tangent(g10,g14) = 1.5708
    c: Tangent(g11,g14) = 1.5708
    c: Tangent(g11,g15) = 1.5708
    c: Tangent(g12,g15) = 1.5708
    c: Tangent(g8,g16) = -1.5708
    c: Tangent(g0,g16) = 1.5708
    c: Tangent(g5,g17) = 1.5708
    c: Tangent(g0,g17) = 1.5708
    c: Tangent(g1,g18) = -1.5708
    c: Tangent(g6,g18) = -1.5708
    c: Tangent(g1,g19) = -1.5708
    c: Tangent(g9,g19) = 1.5708
    c: Equal(g15,g14)
    c: Symmetric(g11,g11,g13)
    c: Equal(g18,g19)
    c: Equal(g19,g16)
    c: Equal(g16,g17)
    c: PointOnObject(g20,g-2)
    c: PointOnObject(g20,g7)
    c: Coincident(g4,g8)
    c: Coincident(g4,g9)
    c: Coincident(g3,g6)
    c: Coincident(g3,g5)
    c: DistanceX(g2,g2) = 115
    c: Symmetric(g0,g0,g2)
    c: Symmetric(g1,g1,g2)
    c: Radius(g19) = 7
    c: DistanceY(g20,g11) = 170
    c: Radius(g15) = 5
    c: DistanceX(g11,g11) = 50
    c: Equal(g9,g8)
    c: Equal(g9,g6)
    c: Coincident(g21,g7)
    c: PointOnObject(g20,g21)
    c: Diameter(g21) = 225
    c: Vertical(g22)
    c: Vertical(g23)
    c: Vertical(g24)
    c: Vertical(g25)
    c: Equal(g5,g8)
    c: Equal(g10,g12)
    c: Tangent(g7,g26) = -1.5708
    c: Tangent(g23,g26) = 1.5708
    c: Tangent(g23,g27) = 1.5708
    c: Tangent(g6,g27) = 1.5708
    c: Tangent(g7,g28) = -1.5708
    c: Tangent(g24,g28) = 1.5708
    c: Tangent(g24,g29) = 1.5708
    c: Tangent(g5,g29) = -1.5708
    c: Equal(g29,g27)
    c: Radius(g27) = 2
    c: Equal(g26,g28)
    c: Radius(g26) = 2
    c: Tangent(g9,g30) = -1.5708
    c: Tangent(g22,g30) = -1.5708
    c: Tangent(g22,g31) = -1.5708
    c: Tangent(g12,g31) = 1.5708
    c: Tangent(g8,g32) = 1.5708
    c: Tangent(g25,g32) = 1.5708
    c: Tangent(g10,g33) = 1.5708
    c: Tangent(g25,g33) = 1.5708
    c: Equal(g30,g32)
    c: Equal(g31,g33)
    c: DistanceY(g23,g23) = 2
    c: DistanceY(g22,g22) = 15
    c: DistanceY(g6,g9) = 48
    c: DistanceX(g24,g23) = 155
    c: Radius(g30) = 2
    c: Radius(g31) = 2
    c: Coincident(g34,g22)
    c: Coincident(g34,g23)
    c: Coincident(g35,g25)
    c: Coincident(g35,g24)
    c: Coincident(g37,g28)
    c: Coincident(g37,g33)
    c: Coincident(g36,g31)
    c: Coincident(g36,g26)
    c: Coincident(g38,g7)
    c: PointOnObject(g38,g-2)
    c: Coincident(g38,g7)
    c: Vertical(g39)
    c: Vertical(g40)
    c: Coincident(g41,g39)
    c: Coincident(g41,g40)
    c: Horizontal(g41)
    c: Coincident(g42,g39)
    c: Horizontal(g42)
    c: DistanceY(g-1,g39) = 2
    c: DistanceY(g39,g-1) = 87
    c: PointOnObject(g44,g38)
    c: DistanceX(g-1,g44) = 43
    c: Coincident(g45,g44)
    c: Coincident(g45,g38)
    c: Coincident(g46,g44)
    c: PointOnObject(g46,g43)
    c: Parallel(g45,g46)
    c: Perpendicular(g46,g43)
    c: Distance(g46) = 1.6
    c: PointOnObject(g43,g-2)
    c: Coincident(g40,g43)
    c: Coincident(g47,g40)
    c: Coincident(g47,g38)
    c: Vertical(g47)
    c: Coincident(g48,g38)
    c: Coincident(g48,g43)
    c: DistanceX(g39,g43) = 2
    c: Coincident(g49,g43)
    c: PointOnObject(g49,g-2)
    c: PointOnObject(g42,g34)
    c: PointOnObject(g50,g34)
    c: Coincident(g50,g42)
    c: PointOnObject(g51,g13)
    c: Coincident(g51,g49)
    c: Coincident(g52,g51)
    c: Coincident(g52,g50)
    c: Coincident(g53,g51)
    c: Vertical(g53)
    c: Coincident(g54,g52)
    c: Vertical(g54)
    c: Equal(g51,g7)
    c: Equal(g52,g21)
    c: DistanceX(g51,g44) = 6.35
    c: DistanceX(g44,g52) = 6.35
    c: Equal(g54,g53)
    c: DistanceY(g54,g54) = 2.3
    c: PointOnObject(g49,g7)
    c: Coincident(g55,g53)
    c: Tangent(g55,g57) = 1.5708
    c: Tangent(g56,g57) = 1.5708
    c: Coincident(g58,g54)
    c: Tangent(g58,g60) = -1.5708
    c: Tangent(g59,g60) = -1.5708
    c: Coincident(g61,g53)
    c: Coincident(g61,g56)
    c: Vertical(g61)
    c: Coincident(g62,g54)
    c: Coincident(g62,g59)
    c: Vertical(g62)
    c: Equal(g58,g59)
    c: Equal(g55,g56)
    c: Equal(g60,g57)
    c: Coincident(g63,g56)
    c: Coincident(g63,g59)
    c: Angle(g59,g58) = 1.5708
    c: Angle(g55,g56) = 1.5708
    c: PointOnObject(g64,g60)
    c: PointOnObject(g65,g57)
    c: Coincident(g66,g65)
    c: PointOnObject(g66,g61)
    c: Horizontal(g66)
    c: PointOnObject(g57,g66)
    c: Coincident(g67,g64)
    c: PointOnObject(g67,g62)
    c: Horizontal(g67)
    c: PointOnObject(g60,g67)
    c: DistanceX(g67,g64) = 0.8
    c: Equal(g67,g66)
    c: Diameter(g60) = 0.8
FEATURE [Sketcher::SketchObject] Sketch063  label="Sketch_ClipsToTrim002"
  FullyConstrained = true
  MapMode = 5
  Placement = pos=(0,0,0) rot=(1,0,0;1.5708rad)
  Support = -> [XZ_Plane003]
  expr: Constraints[15] = <<params>>.std_wall_thick
  expr: Constraints[2] = <<params>>.xport_height_loc
  expr: Constraints[1] = <<params>>.xport_offset_loc
  expr: Constraints[0] = <<params>>.xport_plug_diam + 4 * <<params>>.xport_clip_size
  expr: Constraints[34] = <<params>>.std_wall_thick
  sketch-geometry (11):
    g0: Circle CenterX=43 CenterY=33.25 CenterZ=0 NormalX=0 NormalY=0 NormalZ=1 AngleXU=0 Radius=7.95
    g1: LineSegment StartX=35.1131 StartY=34.25 StartZ=0 EndX=50.8869 EndY=34.25 EndZ=0
    g2: LineSegment StartX=35.1131 StartY=32.25 StartZ=0 EndX=50.8869 EndY=32.25 EndZ=0
    g3: ArcOfCircle CenterX=43 CenterY=33.25 CenterZ=0 NormalX=0 NormalY=0 NormalZ=1 AngleXU=0 Radius=7.95 StartAngle=3.01547 EndAngle=3.26771
    g4: ArcOfCircle CenterX=43 CenterY=33.25 CenterZ=0 NormalX=0 NormalY=0 NormalZ=1 AngleXU=0 Radius=7.95 StartAngle=6.15707 EndAngle=6.40931
    g5: LineSegment StartX=35.1131 StartY=32.25 StartZ=0 EndX=42 EndY=32.25 EndZ=0
    g6: LineSegment StartX=44 StartY=32.25 StartZ=0 EndX=50.8869 EndY=32.25 EndZ=0
    g7: LineSegment StartX=43 StartY=33.25 StartZ=0 EndX=43 EndY=32.25 EndZ=0
    g8: LineSegment StartX=42 StartY=32.25 StartZ=0 EndX=42 EndY=25.3631 EndZ=0
    g9: LineSegment StartX=44 StartY=32.25 StartZ=0 EndX=44 EndY=25.3631 EndZ=0
    g10: ArcOfCircle CenterX=43 CenterY=33.25 CenterZ=0 NormalX=0 NormalY=0 NormalZ=1 AngleXU=0 Radius=7.95 StartAngle=4.58627 EndAngle=4.83851
  constraints (35):
    c: Diameter(g0) = 15.9
    c: DistanceX(g-1,g0) = 43
    c: DistanceY(g-1,g0) = 33.25
    c: PointOnObject(g1,g0)
    c: PointOnObject(g1,g0)
    c: Horizontal(g1)
    c: PointOnObject(g2,g0)
    c: Horizontal(g2)
    c: Symmetric(g1,g2,g0)
    c: Coincident(g3,g0)
    c: Coincident(g4,g3)
    c: Coincident(g3,g1)
    c: Coincident(g4,g1)
    c: PointOnObject(g4,g2)
    c: PointOnObject(g3,g2)
    c: DistanceY(g2,g1) = 2
    c: Horizontal(g5)
    c: Horizontal(g6)
    c: Coincident(g7,g3)
    c: PointOnObject(g7,g2)
    c: Vertical(g7)
    c: Symmetric(g5,g6,g7)
    c: PointOnObject(g5,g2)
    c: PointOnObject(g5,g0)
    c: PointOnObject(g6,g0)
    c: Coincident(g8,g5)
    c: PointOnObject(g8,g0)
    c: Vertical(g8)
    c: Coincident(g9,g6)
    c: Vertical(g9)
    c: PointOnObject(g9,g0)
    c: Coincident(g10,g3)
    c: Coincident(g10,g8)
    c: PointOnObject(g10,g9)
    c: DistanceX(g8,g9) = 2
FEATURE [Sketcher::SketchObject] Sketch064  label="Sketch_SplitPlug_P2_003"
  FullyConstrained = true
  MapMode = 5
  Placement = pos=(0,0,0) rot=(1,0,0;1.5708rad)
  Support = -> [XZ_Plane003]
  expr: Constraints[15] = <<params>>.std_wall_thick
  expr: Constraints[0] = <<params>>.xport_plug_diam + 4 * <<params>>.xport_clip_size
  expr: Constraints[1] = <<params>>.xport_offset_loc
  expr: Constraints[2] = <<params>>.xport_height_loc
  sketch-geometry (5):
    g0: Circle CenterX=43 CenterY=33.25 CenterZ=0 NormalX=0 NormalY=0 NormalZ=1 AngleXU=0 Radius=7.95
    g1: LineSegment StartX=35.1131 StartY=34.25 StartZ=0 EndX=50.8869 EndY=34.25 EndZ=0
    g2: LineSegment StartX=35.1131 StartY=32.25 StartZ=0 EndX=50.8869 EndY=32.25 EndZ=0
    g3: ArcOfCircle CenterX=43 CenterY=33.25 CenterZ=0 NormalX=0 NormalY=0 NormalZ=1 AngleXU=0 Radius=7.95 StartAngle=0.12612 EndAngle=3.01547
    g4: ArcOfCircle CenterX=43 CenterY=33.25 CenterZ=0 NormalX=0 NormalY=0 NormalZ=1 AngleXU=0 Radius=7.95 StartAngle=3.26771 EndAngle=6.15707
  constraints (16):
    c: Diameter(g0) = 15.9
    c: DistanceX(g-1,g0) = 43
    c: DistanceY(g-1,g0) = 33.25
    c: PointOnObject(g1,g0)
    c: PointOnObject(g1,g0)
    c: Horizontal(g1)
    c: PointOnObject(g2,g0)
    c: Horizontal(g2)
    c: Coincident(g3,g0)
    c: Coincident(g4,g3)
    c: Coincident(g3,g1)
    c: PointOnObject(g3,g1)
    c: Coincident(g4,g2)
    c: PointOnObject(g4,g2)
    c: Symmetric(g1,g2,g3)
    c: DistanceY(g2,g1) = 2
FEATURE [Sketcher::SketchObject] Sketch065  label="Sketch_SplitPlug_P3_003"
  FullyConstrained = true
  MapMode = 5
  Placement = pos=(0,0,0) rot=(1,0,0;1.5708rad)
  Support = -> [XZ_Plane003]
  expr: Constraints[15] = <<params>>.std_wall_thick
  expr: Constraints[0] = <<params>>.xport_plug_diam + 4 * <<params>>.xport_clip_size
  expr: Constraints[1] = <<params>>.xport_offset_loc
  expr: Constraints[2] = <<params>>.xport_height_loc
  sketch-geometry (8):
    g0: Circle CenterX=43 CenterY=33.25 CenterZ=0 NormalX=0 NormalY=0 NormalZ=1 AngleXU=0 Radius=7.95
    g1: LineSegment StartX=35.1131 StartY=34.25 StartZ=0 EndX=50.8869 EndY=34.25 EndZ=0
    g2: LineSegment StartX=35.1131 StartY=32.25 StartZ=0 EndX=50.8869 EndY=32.25 EndZ=0
    g3: ArcOfCircle CenterX=43 CenterY=33.25 CenterZ=0 NormalX=0 NormalY=0 NormalZ=1 AngleXU=0 Radius=7.95 StartAngle=0.12612 EndAngle=3.01547
    g4: ArcOfCircle CenterX=43 CenterY=33.25 CenterZ=0 NormalX=0 NormalY=0 NormalZ=1 AngleXU=0 Radius=7.95 StartAngle=3.26771 EndAngle=6.15707
    g5: ArcOfCircle CenterX=43 CenterY=33.25 CenterZ=0 NormalX=0 NormalY=0 NormalZ=1 AngleXU=0 Radius=7.95 StartAngle=1.5708 EndAngle=3.26771
    g6: LineSegment StartX=43 StartY=32.25 StartZ=0 EndX=43 EndY=41.2 EndZ=0
    g7: LineSegment StartX=43 StartY=32.25 StartZ=0 EndX=50.8869 EndY=32.25 EndZ=0
  constraints (26):
    c: Diameter(g0) = 15.9
    c: DistanceX(g-1,g0) = 43
    c: DistanceY(g-1,g0) = 33.25
    c: PointOnObject(g1,g0)
    c: PointOnObject(g1,g0)
    c: Horizontal(g1)
    c: PointOnObject(g2,g0)
    c: Horizontal(g2)
    c: Coincident(g3,g0)
    c: Coincident(g4,g3)
    c: Coincident(g3,g1)
    c: PointOnObject(g3,g1)
    c: Coincident(g4,g2)
    c: PointOnObject(g4,g2)
    c: Symmetric(g1,g2,g3)
    c: DistanceY(g2,g1) = 2
    c: Coincident(g5,g4)
    c: Coincident(g5,g4)
    c: PointOnObject(g6,g2)
    c: PointOnObject(g6,g3)
    c: Vertical(g6)
    c: PointOnObject(g4,g6)
    c: PointOnObject(g5,g6)
    c: Horizontal(g7)
    c: Coincident(g7,g6)
    c: PointOnObject(g7,g0)
FEATURE [Sketcher::SketchObject] Sketch066  label="Sketch_SplitPlug_P2_004"
  FullyConstrained = true
  MapMode = 5
  Placement = pos=(0,0,0) rot=(1,0,0;1.5708rad)
  Support = -> [XZ_Plane003]
  expr: Constraints[2] = <<params>>.xport_height_loc
  expr: Constraints[1] = <<params>>.xport_offset_loc
  expr: Constraints[0] = <<params>>.xport_plug_diam + 4 * <<params>>.xport_clip_size
  expr: Constraints[15] = <<params>>.std_wall_thick
  sketch-geometry (8):
    g0: Circle CenterX=43 CenterY=33.25 CenterZ=0 NormalX=0 NormalY=0 NormalZ=1 AngleXU=0 Radius=7.95
    g1: LineSegment StartX=35.1131 StartY=34.25 StartZ=0 EndX=50.8869 EndY=34.25 EndZ=0
    g2: LineSegment StartX=35.1131 StartY=32.25 StartZ=0 EndX=50.8869 EndY=32.25 EndZ=0
    g3: ArcOfCircle CenterX=43 CenterY=33.25 CenterZ=0 NormalX=0 NormalY=0 NormalZ=1 AngleXU=0 Radius=7.95 StartAngle=0.12612 EndAngle=3.01547
    g4: ArcOfCircle CenterX=43 CenterY=33.25 CenterZ=0 NormalX=0 NormalY=0 NormalZ=1 AngleXU=0 Radius=7.95 StartAngle=3.26771 EndAngle=6.15707
    g5: LineSegment StartX=35.1131 StartY=32.25 StartZ=0 EndX=43 EndY=32.25 EndZ=0
    g6: LineSegment StartX=43 StartY=32.25 StartZ=0 EndX=43 EndY=41.2 EndZ=0
    g7: ArcOfCircle CenterX=43 CenterY=33.25 CenterZ=0 NormalX=0 NormalY=0 NormalZ=1 AngleXU=0 Radius=7.95 StartAngle=6.15707 EndAngle=7.85398
  constraints (26):
    c: Diameter(g0) = 15.9
    c: DistanceX(g-1,g0) = 43
    c: DistanceY(g-1,g0) = 33.25
    c: PointOnObject(g1,g0)
    c: PointOnObject(g1,g0)
    c: Horizontal(g1)
    c: PointOnObject(g2,g0)
    c: Horizontal(g2)
    c: Coincident(g3,g0)
    c: Coincident(g4,g3)
    c: Coincident(g3,g1)
    c: PointOnObject(g3,g1)
    c: Coincident(g4,g2)
    c: PointOnObject(g4,g2)
    c: Symmetric(g1,g2,g3)
    c: DistanceY(g2,g1) = 2
    c: Horizontal(g5)
    c: PointOnObject(g6,g0)
    c: Vertical(g6)
    c: PointOnObject(g4,g6)
    c: Coincident(g6,g5)
    c: PointOnObject(g5,g2)
    c: PointOnObject(g5,g4)
    c: Coincident(g7,g4)
    c: Coincident(g7,g6)
    c: PointOnObject(g7,g2)
FEATURE [Sketcher::SketchObject] Sketch067  label="Sketch_SplitPlug_P1_002"
  FullyConstrained = true
  MapMode = 5
  Placement = pos=(0,0,0) rot=(1,0,0;1.5708rad)
  Support = -> [XZ_Plane003]
  expr: Constraints[0] = <<params>>.xport_plug_diam + 4 * <<params>>.xport_clip_size
  expr: Constraints[1] = <<params>>.xport_offset_loc
  expr: Constraints[2] = <<params>>.xport_height_loc
  expr: Constraints[6] = <<params>>.std_wall_thick / 2 + <<params>>.std_min_wall_thick
  sketch-geometry (3):
    g0: Circle CenterX=43 CenterY=33.25 CenterZ=0 NormalX=0 NormalY=0 NormalZ=1 AngleXU=0 Radius=7.95
    g1: LineSegment StartX=35.2565 StartY=35.05 StartZ=0 EndX=50.7435 EndY=35.05 EndZ=0
    g2: ArcOfCircle CenterX=43 CenterY=33.25 CenterZ=0 NormalX=0 NormalY=0 NormalZ=1 AngleXU=0 Radius=7.95 StartAngle=2.9132 EndAngle=6.51158
  constraints (10):
    c: Diameter(g0) = 15.9
    c: DistanceX(g-1,g0) = 43
    c: DistanceY(g-1,g0) = 33.25
    c: PointOnObject(g1,g0)
    c: PointOnObject(g1,g0)
    c: Horizontal(g1)
    c: DistanceY(g0,g1) = 1.8
    c: Coincident(g2,g0)
    c: Coincident(g2,g1)
    c: PointOnObject(g2,g1)
FEATURE [Sketcher::SketchObject] Sketch068  label="Sketch_SplitPlug_P3_004"
  FullyConstrained = true
  MapMode = 5
  Placement = pos=(0,0,0) rot=(1,0,0;1.5708rad)
  Support = -> [XZ_Plane003]
  expr: Constraints[2] = <<params>>.xport_height_loc
  expr: Constraints[1] = <<params>>.xport_offset_loc
  expr: Constraints[0] = <<params>>.xport_plug_diam + 4 * <<params>>.xport_clip_size
  expr: Constraints[15] = <<params>>.std_wall_thick
  sketch-geometry (5):
    g0: Circle CenterX=43 CenterY=33.25 CenterZ=0 NormalX=0 NormalY=0 NormalZ=1 AngleXU=0 Radius=7.95
    g1: LineSegment StartX=35.1131 StartY=34.25 StartZ=0 EndX=50.8869 EndY=34.25 EndZ=0
    g2: LineSegment StartX=35.1131 StartY=32.25 StartZ=0 EndX=50.8869 EndY=32.25 EndZ=0
    g3: ArcOfCircle CenterX=43 CenterY=33.25 CenterZ=0 NormalX=0 NormalY=0 NormalZ=1 AngleXU=0 Radius=7.95 StartAngle=0.12612 EndAngle=3.01547
    g4: ArcOfCircle CenterX=43 CenterY=33.25 CenterZ=0 NormalX=0 NormalY=0 NormalZ=1 AngleXU=0 Radius=7.95 StartAngle=3.26771 EndAngle=6.15707
  constraints (16):
    c: Diameter(g0) = 15.9
    c: DistanceX(g-1,g0) = 43
    c: DistanceY(g-1,g0) = 33.25
    c: PointOnObject(g1,g0)
    c: PointOnObject(g1,g0)
    c: Horizontal(g1)
    c: PointOnObject(g2,g0)
    c: Horizontal(g2)
    c: Coincident(g3,g0)
    c: Coincident(g4,g3)
    c: Coincident(g3,g1)
    c: PointOnObject(g3,g1)
    c: Coincident(g4,g2)
    c: PointOnObject(g4,g2)
    c: Symmetric(g1,g2,g3)
    c: DistanceY(g2,g1) = 2
FEATURE [Sketcher::SketchObject] Sketch069  label="Sketch_SplitPlug_P4_002"
  FullyConstrained = true
  MapMode = 5
  Placement = pos=(0,0,0) rot=(1,0,0;1.5708rad)
  Support = -> [XZ_Plane003]
  expr: Constraints[0] = <<params>>.xport_plug_diam + 4 * <<params>>.xport_clip_size
  expr: Constraints[1] = <<params>>.xport_offset_loc
  expr: Constraints[2] = <<params>>.xport_height_loc
  expr: Constraints[9] = <<params>>.std_wall_thick / 2 + <<params>>.std_min_wall_thick
  sketch-geometry (3):
    g0: Circle CenterX=43 CenterY=33.25 CenterZ=0 NormalX=0 NormalY=0 NormalZ=1 AngleXU=0 Radius=7.95
    g1: LineSegment StartX=35.2565 StartY=31.45 StartZ=0 EndX=50.7435 EndY=31.45 EndZ=0
    g2: ArcOfCircle CenterX=43 CenterY=33.25 CenterZ=0 NormalX=0 NormalY=0 NormalZ=1 AngleXU=0 Radius=7.95 StartAngle=6.05479 EndAngle=9.65317
  constraints (10):
    c: Diameter(g0) = 15.9
    c: DistanceX(g-1,g0) = 43
    c: DistanceY(g-1,g0) = 33.25
    c: PointOnObject(g1,g0)
    c: PointOnObject(g1,g0)
    c: Horizontal(g1)
    c: Coincident(g2,g0)
    c: Coincident(g2,g1)
    c: PointOnObject(g2,g1)
    c: DistanceY(g1,g2) = 1.8
FEATURE [Sketcher::SketchObject] Sketch070
  FullyConstrained = true
  MapMode = 5
  Placement = pos=(0,0,0) rot=(1,0,0;1.5708rad)
  Support = -> [XZ_Plane003]
  expr: Constraints[2] = <<params>>.xport_height_loc
  expr: Constraints[1] = <<params>>.xport_offset_loc
  expr: Constraints[0] = <<params>>.xport_plug_diam
  sketch-geometry (1):
    g0: Circle CenterX=43 CenterY=33.25 CenterZ=0 NormalX=0 NormalY=0 NormalZ=1 AngleXU=0 Radius=6.35
  constraints (3):
    c: Diameter(g0) = 12.7
    c: DistanceX(g-1,g0) = 43
    c: DistanceY(g-1,g0) = 33.25
FEATURE [PartDesign::Pad] Pad004  label="Pad_Plug001"
  Direction = (1,1,1)
  Length = 85
  Length2 = 100
  Placement = pos=(0,0,0) rot=(1,0,0;1.5708rad)
  Profile = -> Sketch070
  Type = 0
  expr: Length = <<params>>.plate_length / 2
FEATURE [PartDesign::Pad] Pad003  label="Pad_ClipsToTrim001"
  BaseFeature = -> Pad004
  Direction = (1,1,1)
  Length = 85
  Length2 = 100
  Placement = pos=(0,0,0) rot=(1,0,0;1.5708rad)
  Profile = -> Sketch063
  Type = 0
  expr: Length = <<params>>.plate_length / 2
FEATURE [PartDesign::Pocket] Pocket001  label="Pocket_HollowTube001"
  BaseFeature = -> Pad003
  Length = 5
  Length2 = 100
  Midplane = true
  Placement = pos=(0,0,0) rot=(1,0,0;1.5708rad)
  Profile = -> Sketch058
  Type = 1
FEATURE [PartDesign::SubtractiveLoft] SubtractiveLoft002  label="SubtractiveLoft_CutClips001"
  BaseFeature = -> Pocket001
  Closed = false
  Placement = pos=(0,0,0) rot=(1,0,0;1.5708rad)
  Profile = -> Sketch062
  Ruled = false
  Sections = -> [Sketch059]
FEATURE [PartDesign::Chamfer] Chamfer002  label="Chamfer_FrontEdge001"
  Angle = 45
  Base = -> SubtractiveLoft002 [Edge13,Edge17,Edge8]
  BaseFeature = -> SubtractiveLoft002
  ChamferType = 0
  FlipDirection = false
  Placement = pos=(0,0,0) rot=(1,0,0;1.5708rad)
  Size = 1
  Size2 = 1
  SupportTransform = false
FEATURE [PartDesign::Plane] DatumPlane006  label="Datum_ShellVert003"
  AttachmentOffset = pos=(0,0,10) rot=(0,0,1;0rad)
  Length = 88.3878
  MapMode = 5
  Placement = pos=(0,0,10) rot=(0,0,1;0rad)
  ResizeMode = 0
  Support = -> [XY_Plane003]
  Width = 83.2826
  expr: .AttachmentOffset.Base.z = <<params>>.shell_vertheight
FEATURE [Sketcher::SketchObject] Sketch060  label="Sketch_Shell_Vert004"
  FullyConstrained = true
  MapMode = 5
  Placement = pos=(0,0,10) rot=(0,0,1;0rad)
  Support = -> [DatumPlane006]
  expr: Constraints[40] = <<params>>.plate_length
  expr: Constraints[65] = <<params>>.std_rad
  expr: Constraints[42] = <<params>>.tail_width
  expr: Constraints[78] = <<params>>.wheel_well_clearance
  expr: Constraints[79] = <<params>>.plate_width
  expr: Constraints[36] = <<params>>.wheel_well_plate_width
  expr: Constraints[47] = <<params>>.front_diameter
  expr: Constraints[63] = <<params>>.std_rad
  expr: Constraints[76] = <<params>>.front_vert_edge
  expr: Constraints[77] = <<params>>.back_vert_edge
  expr: Constraints[80] = <<params>>.std_rad
  expr: Constraints[81] = <<params>>.std_rad
  expr: Constraints[41] = <<params>>.tail_rad
  sketch-geometry (38):
    g0: LineSegment StartX=-57.5 StartY=17 StartZ=0 EndX=-57.5 EndY=-17 EndZ=0
    g1: LineSegment StartX=57.5 StartY=17 StartZ=0 EndX=57.5 EndY=-17 EndZ=0
    g2: LineSegment StartX=-57.5 StartY=0 StartZ=0 EndX=57.5 EndY=0 EndZ=0
    g3: LineSegment StartX=-64.5 StartY=-24 StartZ=0 EndX=64.5 EndY=-24 EndZ=0
    g4: LineSegment StartX=-64.5 StartY=24 StartZ=0 EndX=64.5 EndY=24 EndZ=0
    g5: LineSegment StartX=-64.5 StartY=-24 StartZ=0 EndX=-75.5 EndY=-24 EndZ=0
    g6: LineSegment StartX=64.5 StartY=-24 StartZ=0 EndX=75.5 EndY=-24 EndZ=0
    g7: ArcOfCircle CenterX=0 CenterY=52.6846 CenterZ=0 NormalX=0 NormalY=0 NormalZ=1 AngleXU=0 Radius=112.5 StartAngle=3.96017 EndAngle=5.4646
    g8: LineSegment StartX=-64.5 StartY=24 StartZ=0 EndX=-75.5 EndY=24 EndZ=0
    g9: LineSegment StartX=64.5 StartY=24 StartZ=0 EndX=75.5 EndY=24 EndZ=0
    g10: LineSegment StartX=-77.1162 StartY=42.1781 StartZ=0 EndX=-29.0404 EndY=108.13 EndZ=0
    g11: LineSegment StartX=-25 StartY=110.185 StartZ=0 EndX=25 EndY=110.185 EndZ=0
    g12: LineSegment StartX=29.0404 StartY=108.13 StartZ=0 EndX=77.1162 EndY=42.1781 EndZ=0
    g13: LineSegment StartX=0 StartY=0 StartZ=0 EndX=0 EndY=110.185 EndZ=0
    g14: ArcOfCircle CenterX=-25 CenterY=105.185 CenterZ=0 NormalX=0 NormalY=0 NormalZ=1 AngleXU=0 Radius=5 StartAngle=1.5708 EndAngle=2.5117
    g15: ArcOfCircle CenterX=25 CenterY=105.185 CenterZ=0 NormalX=0 NormalY=0 NormalZ=1 AngleXU=0 Radius=5 StartAngle=0.629894 EndAngle=1.5708
    g16: ArcOfCircle CenterX=-64.5 CenterY=17 CenterZ=0 NormalX=0 NormalY=0 NormalZ=1 AngleXU=0 Radius=7 StartAngle=0 EndAngle=1.5708
    g17: ArcOfCircle CenterX=-64.5 CenterY=-17 CenterZ=0 NormalX=0 NormalY=0 NormalZ=1 AngleXU=0 Radius=7 StartAngle=4.71239 EndAngle=6.28319
    g18: ArcOfCircle CenterX=64.5 CenterY=-17 CenterZ=0 NormalX=0 NormalY=0 NormalZ=1 AngleXU=0 Radius=7 StartAngle=3.14159 EndAngle=4.71239
    g19: ArcOfCircle CenterX=64.5 CenterY=17 CenterZ=0 NormalX=0 NormalY=0 NormalZ=1 AngleXU=0 Radius=7 StartAngle=1.5708 EndAngle=3.14159
    g20: GeomPoint X=0 Y=-59.8154 Z=0
    g21: Circle CenterX=0 CenterY=52.6846 CenterZ=0 NormalX=0 NormalY=0 NormalZ=1 AngleXU=0 Radius=112.5
    g22: LineSegment StartX=77.5 StartY=26 StartZ=0 EndX=77.5 EndY=41 EndZ=0
    g23: LineSegment StartX=77.5 StartY=-26 StartZ=0 EndX=77.5 EndY=-28 EndZ=0
    g24: LineSegment StartX=-77.5 StartY=-28 StartZ=0 EndX=-77.5 EndY=-26 EndZ=0
    g25: LineSegment StartX=-77.5 StartY=26 StartZ=0 EndX=-77.5 EndY=41 EndZ=0
    g26: ArcOfCircle CenterX=75.5 CenterY=-28 CenterZ=0 NormalX=0 NormalY=0 NormalZ=1 AngleXU=0 Radius=2 StartAngle=5.4646 EndAngle=6.28319
    g27: ArcOfCircle CenterX=75.5 CenterY=-26 CenterZ=0 NormalX=0 NormalY=0 NormalZ=1 AngleXU=0 Radius=2 StartAngle=-9e-16 EndAngle=1.5708
    g28: ArcOfCircle CenterX=-75.5 CenterY=-28 CenterZ=0 NormalX=0 NormalY=0 NormalZ=1 AngleXU=0 Radius=2 StartAngle=3.14159 EndAngle=3.96017
    g29: ArcOfCircle CenterX=-75.5 CenterY=-26 CenterZ=0 NormalX=0 NormalY=0 NormalZ=1 AngleXU=0 Radius=2 StartAngle=1.5708 EndAngle=3.14159
    g30: ArcOfCircle CenterX=75.5 CenterY=26 CenterZ=0 NormalX=0 NormalY=0 NormalZ=1 AngleXU=0 Radius=2 StartAngle=4.71239 EndAngle=6.28319
    g31: ArcOfCircle CenterX=75.5 CenterY=41 CenterZ=0 NormalX=0 NormalY=0 NormalZ=1 AngleXU=0 Radius=2 StartAngle=0 EndAngle=0.629894
    g32: ArcOfCircle CenterX=-75.5 CenterY=26 CenterZ=0 NormalX=0 NormalY=0 NormalZ=1 AngleXU=0 Radius=2 StartAngle=3.14159 EndAngle=4.71239
    g33: ArcOfCircle CenterX=-75.5 CenterY=41 CenterZ=0 NormalX=0 NormalY=0 NormalZ=1 AngleXU=0 Radius=2 StartAngle=2.5117 EndAngle=3.14159
    g34: LineSegment StartX=77.5 StartY=26 StartZ=0 EndX=77.5 EndY=-26 EndZ=0
    g35: LineSegment StartX=-77.5 StartY=26 StartZ=0 EndX=-77.5 EndY=-26 EndZ=0
    g36: LineSegment StartX=77.5 StartY=41 StartZ=0 EndX=77.5 EndY=-28 EndZ=0
    g37: LineSegment StartX=-77.5 StartY=41 StartZ=0 EndX=-77.5 EndY=-28 EndZ=0
  constraints (90):
    c: Vertical(g0)
    c: Vertical(g1)
    c: Horizontal(g2)
    c: Symmetric(g2,g2,g-1)
    c: Horizontal(g3)
    c: Horizontal(g5)
    c: Horizontal(g6)
    c: PointOnObject(g7,g-2)
    c: Horizontal(g8)
    c: Horizontal(g9)
    c: Horizontal(g11)
    c: Coincident(g13,g-1)
    c: PointOnObject(g13,g-2)
    c: Tangent(g10,g14) = 1.5708
    c: Tangent(g11,g14) = 1.5708
    c: Tangent(g11,g15) = 1.5708
    c: Tangent(g12,g15) = 1.5708
    c: Tangent(g8,g16) = -1.5708
    c: Tangent(g0,g16) = 1.5708
    c: Tangent(g5,g17) = 1.5708
    c: Tangent(g0,g17) = 1.5708
    c: Tangent(g1,g18) = -1.5708
    c: Tangent(g6,g18) = -1.5708
    c: Tangent(g1,g19) = -1.5708
    c: Tangent(g9,g19) = 1.5708
    c: Equal(g15,g14)
    c: Symmetric(g11,g11,g13)
    c: Equal(g18,g19)
    c: Equal(g19,g16)
    c: Equal(g16,g17)
    c: PointOnObject(g20,g-2)
    c: PointOnObject(g20,g7)
    c: Coincident(g4,g8)
    c: Coincident(g4,g9)
    c: Coincident(g3,g6)
    c: Coincident(g3,g5)
    c: DistanceX(g2,g2) = 115
    c: Symmetric(g0,g0,g2)
    c: Symmetric(g1,g1,g2)
    c: Radius(g19) = 7
    c: DistanceY(g20,g11) = 170
    c: Radius(g15) = 5
    c: DistanceX(g11,g11) = 50
    c: Equal(g9,g8)
    c: Equal(g9,g6)
    c: Coincident(g21,g7)
    c: PointOnObject(g20,g21)
    c: Diameter(g21) = 225
    c: Vertical(g22)
    c: Vertical(g23)
    c: Vertical(g24)
    c: Vertical(g25)
    c: Equal(g5,g8)
    c: Equal(g10,g12)
    c: Tangent(g7,g26) = -1.5708
    c: Tangent(g23,g26) = 1.5708
    c: Tangent(g23,g27) = 1.5708
    c: Tangent(g6,g27) = 1.5708
    c: Tangent(g7,g28) = -1.5708
    c: Tangent(g24,g28) = 1.5708
    c: Tangent(g24,g29) = 1.5708
    c: Tangent(g5,g29) = -1.5708
    c: Equal(g29,g27)
    c: Radius(g27) = 2
    c: Equal(g26,g28)
    c: Radius(g26) = 2
    c: Tangent(g9,g30) = -1.5708
    c: Tangent(g22,g30) = -1.5708
    c: Tangent(g22,g31) = -1.5708
    c: Tangent(g12,g31) = 1.5708
    c: Tangent(g8,g32) = 1.5708
    c: Tangent(g25,g32) = 1.5708
    c: Tangent(g10,g33) = 1.5708
    c: Tangent(g25,g33) = 1.5708
    c: Equal(g30,g32)
    c: Equal(g31,g33)
    c: DistanceY(g23,g23) = 2
    c: DistanceY(g22,g22) = 15
    c: DistanceY(g6,g9) = 48
    c: DistanceX(g24,g23) = 155
    c: Radius(g30) = 2
    c: Radius(g31) = 2
    c: Coincident(g34,g22)
    c: Coincident(g34,g23)
    c: Coincident(g35,g25)
    c: Coincident(g35,g24)
    c: Coincident(g37,g28)
    c: Coincident(g37,g33)
    c: Coincident(g36,g31)
    c: Coincident(g36,g26)
FEATURE [PartDesign::Plane] DatumPlane007  label="Datum_ShellTot003"
  AttachmentOffset = pos=(0,0,42) rot=(0,0,1;0rad)
  Length = 88.3878
  MapMode = 5
  Placement = pos=(0,0,42) rot=(0,0,1;0rad)
  ResizeMode = 0
  Support = -> [XY_Plane003]
  Width = 83.2826
  expr: .AttachmentOffset.Base.z = <<params>>.shell_totheight
FEATURE [Sketcher::SketchObject] Sketch061  label="Sketch_Shell_Top004"
  FullyConstrained = true
  MapMode = 5
  Placement = pos=(0,0,42) rot=(0,0,1;0rad)
  Support = -> [DatumPlane007]
  expr: Constraints[41] = <<params>>.tail_rad
  expr: Constraints[76] = <<params>>.front_vert_edge
  expr: Constraints[47] = <<params>>.front_diameter
  expr: Constraints[36] = <<params>>.wheel_well_plate_width - 2 * Spreadsheet.shell_overhang_leng
  expr: Constraints[79] = <<params>>.plate_width
  expr: Constraints[42] = <<params>>.tail_width
  expr: Constraints[78] = <<params>>.wheel_well_clearance
  expr: Constraints[65] = <<params>>.std_rad
  expr: Constraints[40] = <<params>>.plate_length
  expr: Constraints[88] = Spreadsheet.shell_overhang_leng
  expr: Constraints[81] = <<params>>.std_rad
  expr: Constraints[63] = <<params>>.std_rad
  expr: Constraints[77] = <<params>>.back_vert_edge
  expr: Constraints[120] = Spreadsheet.shell_overhang_leng
  expr: Constraints[80] = <<params>>.std_rad
  expr: Constraints[119] = Spreadsheet.shell_overhang_leng
  expr: Constraints[123] = <<params>>.shell_overhang_leng
  sketch-geometry (52):
    g0: LineSegment StartX=-43.5 StartY=17 StartZ=0 EndX=-43.5 EndY=-17 EndZ=0
    g1: LineSegment StartX=43.5 StartY=17 StartZ=0 EndX=43.5 EndY=-17 EndZ=0
    g2: LineSegment StartX=-43.5 StartY=0 StartZ=0 EndX=43.5 EndY=0 EndZ=0
    g3: LineSegment StartX=-50.5 StartY=-24 StartZ=0 EndX=50.5 EndY=-24 EndZ=0
    g4: LineSegment StartX=-50.5 StartY=24 StartZ=0 EndX=50.5 EndY=24 EndZ=0
    g5: LineSegment StartX=-50.5 StartY=-24 StartZ=0 EndX=-75.5 EndY=-24 EndZ=0
    g6: LineSegment StartX=50.5 StartY=-24 StartZ=0 EndX=75.5 EndY=-24 EndZ=0
    g7: ArcOfCircle CenterX=0 CenterY=52.6846 CenterZ=0 NormalX=0 NormalY=0 NormalZ=1 AngleXU=0 Radius=112.5 StartAngle=3.96017 EndAngle=5.4646
    g8: LineSegment StartX=-50.5 StartY=24 StartZ=0 EndX=-75.5 EndY=24 EndZ=0
    g9: LineSegment StartX=50.5 StartY=24 StartZ=0 EndX=75.5 EndY=24 EndZ=0
    g10: LineSegment StartX=-77.1162 StartY=42.1781 StartZ=0 EndX=-29.0404 EndY=108.13 EndZ=0
    g11: LineSegment StartX=-25 StartY=110.185 StartZ=0 EndX=25 EndY=110.185 EndZ=0
    g12: LineSegment StartX=29.0404 StartY=108.13 StartZ=0 EndX=77.1162 EndY=42.1781 EndZ=0
    g13: LineSegment StartX=0 StartY=0 StartZ=0 EndX=0 EndY=110.185 EndZ=0
    g14: ArcOfCircle CenterX=-25 CenterY=105.185 CenterZ=0 NormalX=0 NormalY=0 NormalZ=1 AngleXU=0 Radius=5 StartAngle=1.5708 EndAngle=2.5117
    g15: ArcOfCircle CenterX=25 CenterY=105.185 CenterZ=0 NormalX=0 NormalY=0 NormalZ=1 AngleXU=0 Radius=5 StartAngle=0.629894 EndAngle=1.5708
    g16: ArcOfCircle CenterX=-50.5 CenterY=17 CenterZ=0 NormalX=0 NormalY=0 NormalZ=1 AngleXU=0 Radius=7 StartAngle=0 EndAngle=1.5708
    g17: ArcOfCircle CenterX=-50.5 CenterY=-17 CenterZ=0 NormalX=0 NormalY=0 NormalZ=1 AngleXU=0 Radius=7 StartAngle=4.71239 EndAngle=6.28319
    g18: ArcOfCircle CenterX=50.5 CenterY=-17 CenterZ=0 NormalX=0 NormalY=0 NormalZ=1 AngleXU=0 Radius=7 StartAngle=3.14159 EndAngle=4.71239
    g19: ArcOfCircle CenterX=50.5 CenterY=17 CenterZ=0 NormalX=0 NormalY=0 NormalZ=1 AngleXU=0 Radius=7 StartAngle=1.5708 EndAngle=3.14159
    g20: GeomPoint X=0 Y=-59.8154 Z=0
    g21: Circle CenterX=0 CenterY=52.6846 CenterZ=0 NormalX=0 NormalY=0 NormalZ=1 AngleXU=0 Radius=112.5
    g22: LineSegment StartX=77.5 StartY=26 StartZ=0 EndX=77.5 EndY=41 EndZ=0
    g23: LineSegment StartX=77.5 StartY=-26 StartZ=0 EndX=77.5 EndY=-28 EndZ=0
    g24: LineSegment StartX=-77.5 StartY=-28 StartZ=0 EndX=-77.5 EndY=-26 EndZ=0
    g25: LineSegment StartX=-77.5 StartY=26 StartZ=0 EndX=-77.5 EndY=41 EndZ=0
    g26: ArcOfCircle CenterX=75.5 CenterY=-28 CenterZ=0 NormalX=0 NormalY=0 NormalZ=1 AngleXU=0 Radius=2 StartAngle=5.4646 EndAngle=6.28319
    g27: ArcOfCircle CenterX=75.5 CenterY=-26 CenterZ=0 NormalX=0 NormalY=0 NormalZ=1 AngleXU=0 Radius=2 StartAngle=0 EndAngle=1.5708
    g28: ArcOfCircle CenterX=-75.5 CenterY=-28 CenterZ=0 NormalX=0 NormalY=0 NormalZ=1 AngleXU=0 Radius=2 StartAngle=3.14159 EndAngle=3.96017
    g29: ArcOfCircle CenterX=-75.5 CenterY=-26 CenterZ=0 NormalX=0 NormalY=0 NormalZ=1 AngleXU=0 Radius=2 StartAngle=1.5708 EndAngle=3.14159
    g30: ArcOfCircle CenterX=75.5 CenterY=26 CenterZ=0 NormalX=0 NormalY=0 NormalZ=1 AngleXU=0 Radius=2 StartAngle=4.71239 EndAngle=6.28319
    g31: ArcOfCircle CenterX=75.5 CenterY=41 CenterZ=0 NormalX=0 NormalY=0 NormalZ=1 AngleXU=0 Radius=2 StartAngle=4e-16 EndAngle=0.629894
    g32: ArcOfCircle CenterX=-75.5 CenterY=26 CenterZ=0 NormalX=0 NormalY=0 NormalZ=1 AngleXU=0 Radius=2 StartAngle=3.14159 EndAngle=4.71239
    g33: ArcOfCircle CenterX=-75.5 CenterY=41 CenterZ=0 NormalX=0 NormalY=0 NormalZ=1 AngleXU=0 Radius=2 StartAngle=2.5117 EndAngle=3.14159
    g34: LineSegment StartX=77.5 StartY=26 StartZ=0 EndX=77.5 EndY=-26 EndZ=0
    g35: LineSegment StartX=-77.5 StartY=26 StartZ=0 EndX=-77.5 EndY=-26 EndZ=0
    g36: LineSegment StartX=-17.8805 StartY=96.1846 StartZ=0 EndX=17.8805 EndY=96.1846 EndZ=0
    g37: GeomPoint X=0 Y=96.1846 Z=0
    g38: LineSegment StartX=-21.921 StartY=94.1299 StartZ=0 EndX=-63.1162 EndY=37.617 EndZ=0
    g39: LineSegment StartX=-63.5 StartY=36.4389 StartZ=0 EndX=-63.5 EndY=-24 EndZ=0
    g40: LineSegment StartX=21.921 StartY=94.1299 StartZ=0 EndX=63.1162 EndY=37.617 EndZ=0
    g41: LineSegment StartX=63.5 StartY=36.4389 StartZ=0 EndX=63.5 EndY=-24 EndZ=0
    g42: ArcOfCircle CenterX=0 CenterY=61.5293 CenterZ=0 NormalX=0 NormalY=0 NormalZ=1 AngleXU=0 Radius=107.345 StartAngle=4.08899 EndAngle=5.33579
    g43: LineSegment StartX=-63.5 StartY=36.4389 StartZ=0 EndX=63.5 EndY=36.4389 EndZ=0
    g44: GeomPoint X=0 Y=-45.8154 Z=0
    g45: ArcOfCircle CenterX=-17.8805 CenterY=91.1846 CenterZ=0 NormalX=0 NormalY=0 NormalZ=1 AngleXU=0 Radius=5 StartAngle=1.5708 EndAngle=2.5117
    g46: ArcOfCircle CenterX=17.8805 CenterY=91.1846 CenterZ=0 NormalX=0 NormalY=0 NormalZ=1 AngleXU=0 Radius=5 StartAngle=0.629894 EndAngle=1.5708
    g47: ArcOfCircle CenterX=61.5 CenterY=36.4389 CenterZ=0 NormalX=0 NormalY=0 NormalZ=1 AngleXU=0 Radius=2 StartAngle=-9e-16 EndAngle=0.629894
    g48: ArcOfCircle CenterX=-61.5 CenterY=36.4389 CenterZ=0 NormalX=0 NormalY=0 NormalZ=1 AngleXU=0 Radius=2 StartAngle=2.5117 EndAngle=3.14159
    g49: ArcOfCircle CenterX=61.5 CenterY=-24 CenterZ=0 NormalX=0 NormalY=0 NormalZ=1 AngleXU=0 Radius=2 StartAngle=5.33579 EndAngle=6.28319
    g50: ArcOfCircle CenterX=-61.5 CenterY=-24 CenterZ=0 NormalX=0 NormalY=0 NormalZ=1 AngleXU=0 Radius=2 StartAngle=3.14159 EndAngle=4.08899
    g51: LineSegment StartX=-29.0404 StartY=108.13 StartZ=0 EndX=-17.7272 EndY=99.883 EndZ=0
  constraints (125):
    c: Vertical(g0)
    c: Vertical(g1)
    c: Horizontal(g2)
    c: Symmetric(g2,g2,g-1)
    c: Horizontal(g3)
    c: Horizontal(g5)
    c: Horizontal(g6)
    c: PointOnObject(g7,g-2)
    c: Horizontal(g8)
    c: Horizontal(g9)
    c: Horizontal(g11)
    c: Coincident(g13,g-1)
    c: PointOnObject(g13,g-2)
    c: Tangent(g10,g14) = 1.5708
    c: Tangent(g11,g14) = 1.5708
    c: Tangent(g11,g15) = 1.5708
    c: Tangent(g12,g15) = 1.5708
    c: Tangent(g8,g16) = -1.5708
    c: Tangent(g0,g16) = 1.5708
    c: Tangent(g5,g17) = 1.5708
    c: Tangent(g0,g17) = 1.5708
    c: Tangent(g1,g18) = -1.5708
    c: Tangent(g6,g18) = -1.5708
    c: Tangent(g1,g19) = -1.5708
    c: Tangent(g9,g19) = 1.5708
    c: Equal(g15,g14)
    c: Symmetric(g11,g11,g13)
    c: Equal(g18,g19)
    c: Equal(g19,g16)
    c: Equal(g16,g17)
    c: PointOnObject(g20,g-2)
    c: PointOnObject(g20,g7)
    c: Coincident(g4,g8)
    c: Coincident(g4,g9)
    c: Coincident(g3,g6)
    c: Coincident(g3,g5)
    c: DistanceX(g2,g2) = 87
    c: Symmetric(g0,g0,g2)
    c: Symmetric(g1,g1,g2)
    c: Radius(g19) = 7
    c: DistanceY(g20,g11) = 170
    c: Radius(g15) = 5
    c: DistanceX(g11,g11) = 50
    c: Equal(g9,g8)
    c: Equal(g9,g6)
    c: Coincident(g21,g7)
    c: PointOnObject(g20,g21)
    c: Diameter(g21) = 225
    c: Vertical(g22)
    c: Vertical(g23)
    c: Vertical(g24)
    c: Vertical(g25)
    c: Equal(g5,g8)
    c: Equal(g10,g12)
    c: Tangent(g7,g26) = -1.5708
    c: Tangent(g23,g26) = 1.5708
    c: Tangent(g23,g27) = 1.5708
    c: Tangent(g6,g27) = 1.5708
    c: Tangent(g7,g28) = -1.5708
    c: Tangent(g24,g28) = 1.5708
    c: Tangent(g24,g29) = 1.5708
    c: Tangent(g5,g29) = -1.5708
    c: Equal(g29,g27)
    c: Radius(g27) = 2
    c: Equal(g26,g28)
    c: Radius(g26) = 2
    c: Tangent(g9,g30) = -1.5708
    c: Tangent(g22,g30) = -1.5708
    c: Tangent(g22,g31) = -1.5708
    c: Tangent(g12,g31) = 1.5708
    c: Tangent(g8,g32) = 1.5708
    c: Tangent(g25,g32) = 1.5708
    c: Tangent(g10,g33) = 1.5708
    c: Tangent(g25,g33) = 1.5708
    c: Equal(g30,g32)
    c: Equal(g31,g33)
    c: DistanceY(g23,g23) = 2
    c: DistanceY(g22,g22) = 15
    c: DistanceY(g6,g9) = 48
    c: DistanceX(g24,g23) = 155
    c: Radius(g30) = 2
    c: Radius(g31) = 2
    c: Coincident(g34,g22)
    c: Coincident(g34,g23)
    c: Coincident(g35,g25)
    c: Coincident(g35,g24)
    c: Horizontal(g36)
    c: PointOnObject(g37,g13)
    c: DistanceY(g37,g13) = 14
    c: Vertical(g39)
    c: Vertical(g41)
    c: PointOnObject(g42,g13)
    c: Horizontal(g43)
    c: Parallel(g40,g12)
    c: PointOnObject(g44,g-2)
    c: PointOnObject(g44,g42)
    c: Tangent(g38,g45) = -1.5708
    c: Tangent(g36,g45) = 1.5708
    c: Tangent(g40,g46) = 1.5708
    c: Tangent(g36,g46) = 1.5708
    c: Tangent(g41,g47) = 1.5708
    c: Tangent(g40,g47) = 1.5708
    c: Tangent(g39,g48) = -1.5708
    c: Tangent(g38,g48) = -1.5708
    c: Tangent(g42,g49) = -1.5708
    c: Tangent(g41,g49) = 1.5708
    c: Tangent(g42,g50) = -1.5708
    c: Tangent(g39,g50) = -1.5708
    c: Coincident(g43,g39)
    c: Coincident(g43,g41)
    c: Equal(g15,g46)
    c: Equal(g46,g45)
    c: Symmetric(g36,g36,g37)
    c: Equal(g31,g47)
    c: Equal(g26,g49)
    c: Equal(g50,g29)
    c: Equal(g48,g32)
    c: PointOnObject(g41,g6)
    c: PointOnObject(g50,g5)
    c: DistanceY(g20,g44) = 14
    c: DistanceX(g41,g22) = 14
    c: PointOnObject(g51,g38)
    c: Perpendicular(g38,g51)
    c: Distance(g51) = 14
    c: Coincident(g51,g10)
FEATURE [Sketcher::SketchObject] Sketch071  label="Sketch_HollowPlug002"
  FullyConstrained = true
  MapMode = 5
  Placement = pos=(0,0,0) rot=(1,0,0;1.5708rad)
  Support = -> [XZ_Plane004]
  expr: Constraints[0] = <<params>>.xport_plug_diam - 2 * <<params>>.xport_plug_wall_thick
  expr: Constraints[1] = <<params>>.xport_offset_loc
  expr: Constraints[2] = <<params>>.xport_height_loc
  sketch-geometry (1):
    g0: Circle CenterX=43 CenterY=33.25 CenterZ=0 NormalX=0 NormalY=0 NormalZ=1 AngleXU=0 Radius=5.55
  constraints (3):
    c: Diameter(g0) = 11.1
    c: DistanceX(g-1,g0) = 43
    c: DistanceY(g-1,g0) = 33.25
FEATURE [Sketcher::SketchObject] Sketch072  label="Sketch_Shell_Top_CutPlug002"
  FullyConstrained = true
  MapMode = 5
  Placement = pos=(0,0,42) rot=(0,0,1;0rad)
  expr: Constraints[142] = <<params>>.xport_plug_plate_thick
  expr: Constraints[79] = <<params>>.plate_width
  expr: Constraints[136] = <<params>>.xport_offset_loc
  expr: Constraints[120] = <<params>>.shell_overhang_leng
  expr: Constraints[77] = <<params>>.back_vert_edge
  expr: Constraints[155] = <<params>>.shell_wall_thick + <<params>>.std_tol_interfere
  expr: Constraints[63] = <<params>>.std_rad
  expr: Constraints[143] = <<params>>.std_wall_thick
  expr: Constraints[42] = <<params>>.tail_width
  expr: Constraints[78] = <<params>>.wheel_well_clearance
  expr: Constraints[153] = <<params>>.xport_plug_diam / 2
  expr: Constraints[152] = <<params>>.xport_plug_diam / 2
  expr: Constraints[80] = <<params>>.std_rad
  expr: Constraints[117] = <<params>>.shell_overhang_leng
  expr: Constraints[76] = <<params>>.front_vert_edge
  expr: Constraints[130] = <<params>>.plate_length / 2 + <<params>>.std_wall_thick
  expr: Constraints[41] = <<params>>.tail_rad
  expr: Constraints[187] = <<params>>.xport_clip_size
  expr: Constraints[129] = <<params>>.std_wall_thick
  expr: Constraints[40] = <<params>>.plate_length
  expr: Constraints[189] = <<params>>.shell_overhang_leng
  expr: Constraints[65] = <<params>>.std_rad
  expr: Constraints[186] = <<params>>.xport_clip_size
  expr: Constraints[81] = <<params>>.std_rad
  expr: Constraints[88] = Spreadsheet.shell_overhang_leng
  expr: Constraints[116] = Spreadsheet.shell_overhang_leng
  expr: Constraints[36] = <<params>>.wheel_well_plate_width - 2 * Spreadsheet.shell_overhang_leng
  expr: Constraints[47] = <<params>>.front_diameter
  sketch-geometry (80):
    g0: LineSegment StartX=-43.5 StartY=17 StartZ=0 EndX=-43.5 EndY=-17 EndZ=0
    g1: LineSegment StartX=43.5 StartY=17 StartZ=0 EndX=43.5 EndY=-17 EndZ=0
    g2: LineSegment StartX=-43.5 StartY=0 StartZ=0 EndX=43.5 EndY=0 EndZ=0
    g3: LineSegment StartX=-50.5 StartY=-24 StartZ=0 EndX=50.5 EndY=-24 EndZ=0
    g4: LineSegment StartX=-50.5 StartY=24 StartZ=0 EndX=50.5 EndY=24 EndZ=0
    g5: LineSegment StartX=-50.5 StartY=-24 StartZ=0 EndX=-75.5 EndY=-24 EndZ=0
    g6: LineSegment StartX=50.5 StartY=-24 StartZ=0 EndX=75.5 EndY=-24 EndZ=0
    g7: ArcOfCircle CenterX=0 CenterY=52.6846 CenterZ=0 NormalX=0 NormalY=0 NormalZ=1 AngleXU=0 Radius=112.5 StartAngle=3.96017 EndAngle=5.4646
    g8: LineSegment StartX=-50.5 StartY=24 StartZ=0 EndX=-75.5 EndY=24 EndZ=0
    g9: LineSegment StartX=50.5 StartY=24 StartZ=0 EndX=75.5 EndY=24 EndZ=0
    g10: LineSegment StartX=-77.1162 StartY=42.1781 StartZ=0 EndX=-29.0404 EndY=108.13 EndZ=0
    g11: LineSegment StartX=-25 StartY=110.185 StartZ=0 EndX=25 EndY=110.185 EndZ=0
    g12: LineSegment StartX=29.0404 StartY=108.13 StartZ=0 EndX=77.1162 EndY=42.1781 EndZ=0
    g13: LineSegment StartX=0 StartY=0 StartZ=0 EndX=0 EndY=110.185 EndZ=0
    g14: ArcOfCircle CenterX=-25 CenterY=105.185 CenterZ=0 NormalX=0 NormalY=0 NormalZ=1 AngleXU=0 Radius=5 StartAngle=1.5708 EndAngle=2.5117
    g15: ArcOfCircle CenterX=25 CenterY=105.185 CenterZ=0 NormalX=0 NormalY=0 NormalZ=1 AngleXU=0 Radius=5 StartAngle=0.629894 EndAngle=1.5708
    g16: ArcOfCircle CenterX=-50.5 CenterY=17 CenterZ=0 NormalX=0 NormalY=0 NormalZ=1 AngleXU=0 Radius=7 StartAngle=0 EndAngle=1.5708
    g17: ArcOfCircle CenterX=-50.5 CenterY=-17 CenterZ=0 NormalX=0 NormalY=0 NormalZ=1 AngleXU=0 Radius=7 StartAngle=4.71239 EndAngle=6.28319
    g18: ArcOfCircle CenterX=50.5 CenterY=-17 CenterZ=0 NormalX=0 NormalY=0 NormalZ=1 AngleXU=0 Radius=7 StartAngle=3.14159 EndAngle=4.71239
    g19: ArcOfCircle CenterX=50.5 CenterY=17 CenterZ=0 NormalX=0 NormalY=0 NormalZ=1 AngleXU=0 Radius=7 StartAngle=1.5708 EndAngle=3.14159
    g20: GeomPoint X=0 Y=-59.8154 Z=0
    g21: Circle CenterX=0 CenterY=52.6846 CenterZ=0 NormalX=0 NormalY=0 NormalZ=1 AngleXU=0 Radius=112.5
    g22: LineSegment StartX=77.5 StartY=26 StartZ=0 EndX=77.5 EndY=41 EndZ=0
    g23: LineSegment StartX=77.5 StartY=-26 StartZ=0 EndX=77.5 EndY=-28 EndZ=0
    g24: LineSegment StartX=-77.5 StartY=-28 StartZ=0 EndX=-77.5 EndY=-26 EndZ=0
    g25: LineSegment StartX=-77.5 StartY=26 StartZ=0 EndX=-77.5 EndY=41 EndZ=0
    g26: ArcOfCircle CenterX=75.5 CenterY=-28 CenterZ=0 NormalX=0 NormalY=0 NormalZ=1 AngleXU=0 Radius=2 StartAngle=5.4646 EndAngle=6.28319
    g27: ArcOfCircle CenterX=75.5 CenterY=-26 CenterZ=0 NormalX=0 NormalY=0 NormalZ=1 AngleXU=0 Radius=2 StartAngle=0 EndAngle=1.5708
    g28: ArcOfCircle CenterX=-75.5 CenterY=-28 CenterZ=0 NormalX=0 NormalY=0 NormalZ=1 AngleXU=0 Radius=2 StartAngle=3.14159 EndAngle=3.96017
    g29: ArcOfCircle CenterX=-75.5 CenterY=-26 CenterZ=0 NormalX=0 NormalY=0 NormalZ=1 AngleXU=0 Radius=2 StartAngle=1.5708 EndAngle=3.14159
    g30: ArcOfCircle CenterX=75.5 CenterY=26 CenterZ=0 NormalX=0 NormalY=0 NormalZ=1 AngleXU=0 Radius=2 StartAngle=4.71239 EndAngle=6.28319
    g31: ArcOfCircle CenterX=75.5 CenterY=41 CenterZ=0 NormalX=0 NormalY=0 NormalZ=1 AngleXU=0 Radius=2 StartAngle=9e-16 EndAngle=0.629894
    g32: ArcOfCircle CenterX=-75.5 CenterY=26 CenterZ=0 NormalX=0 NormalY=0 NormalZ=1 AngleXU=0 Radius=2 StartAngle=3.14159 EndAngle=4.71239
    g33: ArcOfCircle CenterX=-75.5 CenterY=41 CenterZ=0 NormalX=0 NormalY=0 NormalZ=1 AngleXU=0 Radius=2 StartAngle=2.5117 EndAngle=3.14159
    g34: LineSegment StartX=77.5 StartY=26 StartZ=0 EndX=77.5 EndY=-26 EndZ=0
    g35: LineSegment StartX=-77.5 StartY=26 StartZ=0 EndX=-77.5 EndY=-26 EndZ=0
    g36: LineSegment StartX=-17.8805 StartY=96.1846 StartZ=0 EndX=17.8805 EndY=96.1846 EndZ=0
    g37: GeomPoint X=0 Y=96.1846 Z=0
    g38: LineSegment StartX=-21.921 StartY=94.1299 StartZ=0 EndX=-63.1162 EndY=37.617 EndZ=0
    g39: LineSegment StartX=-63.5 StartY=36.4389 StartZ=0 EndX=-63.5 EndY=-21.6794 EndZ=0
    g40: LineSegment StartX=21.921 StartY=94.1299 StartZ=0 EndX=63.1162 EndY=37.617 EndZ=0
    g41: LineSegment StartX=63.5 StartY=36.4389 StartZ=0 EndX=63.5 EndY=-21.6794 EndZ=0
    g42: ArcOfCircle CenterX=0 CenterY=52.6846 CenterZ=0 NormalX=0 NormalY=0 NormalZ=1 AngleXU=0 Radius=98.5 StartAngle=4.02139 EndAngle=5.40339
    g43: LineSegment StartX=-63.5 StartY=36.4389 StartZ=0 EndX=63.5 EndY=36.4389 EndZ=0
    g44: GeomPoint X=0 Y=-45.8154 Z=0
    g45: ArcOfCircle CenterX=-17.8805 CenterY=91.1846 CenterZ=0 NormalX=0 NormalY=0 NormalZ=1 AngleXU=0 Radius=5 StartAngle=1.5708 EndAngle=2.5117
    g46: ArcOfCircle CenterX=17.8805 CenterY=91.1846 CenterZ=0 NormalX=0 NormalY=0 NormalZ=1 AngleXU=0 Radius=5 StartAngle=0.629894 EndAngle=1.5708
    g47: ArcOfCircle CenterX=61.5 CenterY=36.4389 CenterZ=0 NormalX=0 NormalY=0 NormalZ=1 AngleXU=0 Radius=2 StartAngle=0 EndAngle=0.629894
    g48: ArcOfCircle CenterX=-61.5 CenterY=36.4389 CenterZ=0 NormalX=0 NormalY=0 NormalZ=1 AngleXU=0 Radius=2 StartAngle=2.5117 EndAngle=3.14159
    g49: ArcOfCircle CenterX=61.5 CenterY=-21.6794 CenterZ=0 NormalX=0 NormalY=0 NormalZ=1 AngleXU=0 Radius=2 StartAngle=5.40339 EndAngle=6.28319
    g50: ArcOfCircle CenterX=-61.5 CenterY=-21.6794 CenterZ=0 NormalX=0 NormalY=0 NormalZ=1 AngleXU=0 Radius=2 StartAngle=3.14159 EndAngle=4.02139
    g51: LineSegment StartX=-29.0404 StartY=108.13 StartZ=0 EndX=-17.7272 EndY=99.883 EndZ=0
    g52: LineSegment StartX=-2 StartY=2 StartZ=0 EndX=-2 EndY=-87 EndZ=0
    g53: LineSegment StartX=-2 StartY=-87 StartZ=0 EndX=63.5 EndY=-87 EndZ=0
    g54: LineSegment StartX=63.5 StartY=-87 StartZ=0 EndX=63.5 EndY=-27.7653 EndZ=0
    g55: LineSegment StartX=63.5 StartY=2 StartZ=0 EndX=-2 EndY=2 EndZ=0
    g56: LineSegment StartX=0 StartY=-58.5771 StartZ=0 EndX=63.5 EndY=-27.7653 EndZ=0
    g57: LineSegment StartX=63.5 StartY=-22.6148 StartZ=0 EndX=63.5 EndY=-27.7653 EndZ=0
    g58: GeomPoint X=43 Y=-35.934 Z=0
    g59: LineSegment StartX=0 StartY=52.6846 StartZ=0 EndX=43 EndY=-35.934 EndZ=0
    g60: LineSegment StartX=43 StartY=-35.934 StartZ=0 EndX=43.6985 EndY=-37.3735 EndZ=0
    g61: LineSegment StartX=0 StartY=-58.5771 StartZ=0 EndX=-1.81e-14 EndY=-45.8154 EndZ=0
    g62: LineSegment StartX=63.5 StartY=2 StartZ=0 EndX=63.5 EndY=-22.6148 EndZ=0
    g63: LineSegment StartX=36.65 StartY=-38.7431 StartZ=0 EndX=36.65 EndY=-36.5431 EndZ=0
    g64: LineSegment StartX=49.35 StartY=-30.3611 StartZ=0 EndX=49.35 EndY=-32.5611 EndZ=0
    g65: LineSegment StartX=36.65 StartY=-36.5431 StartZ=0 EndX=35.9672 EndY=-35.8603 EndZ=0
    g66: LineSegment StartX=35.9672 StartY=-35.2946 StartZ=0 EndX=36.65 EndY=-34.6118 EndZ=0
    g67: LineSegment StartX=49.35 StartY=-30.3611 StartZ=0 EndX=50.0328 EndY=-29.6783 EndZ=0
    g68: LineSegment StartX=50.0328 StartY=-29.1126 StartZ=0 EndX=49.35 EndY=-28.4297 EndZ=0
    g69: LineSegment StartX=49.35 StartY=-28.4297 StartZ=0 EndX=36.65 EndY=-34.6118 EndZ=0
    g70: ArcOfCircle CenterX=36.25 CenterY=-35.5775 CenterZ=0 NormalX=0 NormalY=0 NormalZ=1 AngleXU=0 Radius=0.4 StartAngle=2.35619 EndAngle=3.92699
    g71: ArcOfCircle CenterX=49.75 CenterY=-29.3954 CenterZ=0 NormalX=0 NormalY=0 NormalZ=1 AngleXU=0 Radius=0.4 StartAngle=5.49779 EndAngle=7.06858
    g72: LineSegment StartX=36.65 StartY=-36.5431 StartZ=0 EndX=36.65 EndY=-34.6118 EndZ=0
    g73: GeomPoint X=35.85 Y=-35.5775 Z=0
    g74: GeomPoint X=50.15 Y=-29.3954 Z=0
    g75: LineSegment StartX=49.35 StartY=-30.3611 StartZ=0 EndX=49.35 EndY=-28.4297 EndZ=0
    g76: LineSegment StartX=50.15 StartY=-29.3954 StartZ=0 EndX=49.35 EndY=-29.3954 EndZ=0
    g77: LineSegment StartX=36.65 StartY=-35.5775 StartZ=0 EndX=35.85 EndY=-35.5775 EndZ=0
    g78: ArcOfCircle CenterX=0 CenterY=52.6846 CenterZ=0 NormalX=0 NormalY=0 NormalZ=1 AngleXU=0 Radius=98.5 StartAngle=4.71239 EndAngle=5.09364
    g79: ArcOfCircle CenterX=0 CenterY=52.6846 CenterZ=0 NormalX=0 NormalY=0 NormalZ=1 AngleXU=0 Radius=98.5 StartAngle=5.23716 EndAngle=5.41298
  constraints (201):
    c: Vertical(g0)
    c: Vertical(g1)
    c: Horizontal(g2)
    c: Symmetric(g2,g2,g-1)
    c: Horizontal(g3)
    c: Horizontal(g5)
    c: Horizontal(g6)
    c: PointOnObject(g7,g-2)
    c: Horizontal(g8)
    c: Horizontal(g9)
    c: Horizontal(g11)
    c: Coincident(g13,g-1)
    c: PointOnObject(g13,g-2)
    c: Tangent(g10,g14) = 1.5708
    c: Tangent(g11,g14) = 1.5708
    c: Tangent(g11,g15) = 1.5708
    c: Tangent(g12,g15) = 1.5708
    c: Tangent(g8,g16) = -1.5708
    c: Tangent(g0,g16) = 1.5708
    c: Tangent(g5,g17) = 1.5708
    c: Tangent(g0,g17) = 1.5708
    c: Tangent(g1,g18) = -1.5708
    c: Tangent(g6,g18) = -1.5708
    c: Tangent(g1,g19) = -1.5708
    c: Tangent(g9,g19) = 1.5708
    c: Equal(g15,g14)
    c: Symmetric(g11,g11,g13)
    c: Equal(g18,g19)
    c: Equal(g19,g16)
    c: Equal(g16,g17)
    c: PointOnObject(g20,g-2)
    c: PointOnObject(g20,g7)
    c: Coincident(g4,g8)
    c: Coincident(g4,g9)
    c: Coincident(g3,g6)
    c: Coincident(g3,g5)
    c: DistanceX(g2,g2) = 87
    c: Symmetric(g0,g0,g2)
    c: Symmetric(g1,g1,g2)
    c: Radius(g19) = 7
    c: DistanceY(g20,g11) = 170
    c: Radius(g15) = 5
    c: DistanceX(g11,g11) = 50
    c: Equal(g9,g8)
    c: Equal(g9,g6)
    c: Coincident(g21,g7)
    c: PointOnObject(g20,g21)
    c: Diameter(g21) = 225
    c: Vertical(g22)
    c: Vertical(g23)
    c: Vertical(g24)
    c: Vertical(g25)
    c: Equal(g5,g8)
    c: Equal(g10,g12)
    c: Tangent(g7,g26) = -1.5708
    c: Tangent(g23,g26) = 1.5708
    c: Tangent(g23,g27) = 1.5708
    c: Tangent(g6,g27) = 1.5708
    c: Tangent(g7,g28) = -1.5708
    c: Tangent(g24,g28) = 1.5708
    c: Tangent(g24,g29) = 1.5708
    c: Tangent(g5,g29) = -1.5708
    c: Equal(g29,g27)
    c: Radius(g27) = 2
    c: Equal(g26,g28)
    c: Radius(g26) = 2
    c: Tangent(g9,g30) = -1.5708
    c: Tangent(g22,g30) = -1.5708
    c: Tangent(g22,g31) = -1.5708
    c: Tangent(g12,g31) = 1.5708
    c: Tangent(g8,g32) = 1.5708
    c: Tangent(g25,g32) = 1.5708
    c: Tangent(g10,g33) = 1.5708
    c: Tangent(g25,g33) = 1.5708
    c: Equal(g30,g32)
    c: Equal(g31,g33)
    c: DistanceY(g23,g23) = 2
    c: DistanceY(g22,g22) = 15
    c: DistanceY(g6,g9) = 48
    c: DistanceX(g24,g23) = 155
    c: Radius(g30) = 2
    c: Radius(g31) = 2
    c: Coincident(g34,g22)
    c: Coincident(g34,g23)
    c: Coincident(g35,g25)
    c: Coincident(g35,g24)
    c: Horizontal(g36)
    c: PointOnObject(g37,g13)
    c: DistanceY(g37,g13) = 14
    c: Vertical(g39)
    c: Vertical(g41)
    c: Horizontal(g43)
    c: Parallel(g40,g12)
    c: PointOnObject(g44,g-2)
    c: PointOnObject(g44,g42)
    c: Tangent(g38,g45) = -1.5708
    c: Tangent(g36,g45) = 1.5708
    c: Tangent(g40,g46) = 1.5708
    c: Tangent(g36,g46) = 1.5708
    c: Tangent(g41,g47) = 1.5708
    c: Tangent(g40,g47) = 1.5708
    c: Tangent(g39,g48) = -1.5708
    c: Tangent(g38,g48) = -1.5708
    c: Tangent(g42,g49) = -1.5708
    c: Tangent(g41,g49) = 1.5708
    c: Tangent(g42,g50) = -1.5708
    c: Tangent(g39,g50) = -1.5708
    c: Coincident(g43,g39)
    c: Coincident(g43,g41)
    c: Equal(g15,g46)
    c: Equal(g46,g45)
    c: Symmetric(g36,g36,g37)
    c: Equal(g31,g47)
    c: Equal(g26,g49)
    c: Equal(g50,g29)
    c: Equal(g48,g32)
    c: DistanceY(g20,g44) = 14
    c: DistanceX(g41,g22) = 14
    c: PointOnObject(g51,g38)
    c: Perpendicular(g38,g51)
    c: Distance(g51) = 14
    c: Coincident(g51,g10)
    c: Vertical(g52)
    c: Coincident(g53,g52)
    c: Horizontal(g53)
    c: Coincident(g54,g53)
    c: Vertical(g54)
    c: Coincident(g55,g52)
    c: Horizontal(g55)
    c: DistanceY(g-1,g52) = 2
    c: DistanceY(g52,g-1) = 87
    c: Coincident(g54,g56)
    c: Coincident(g57,g54)
    c: Vertical(g57)
    c: PointOnObject(g56,g-2)
    c: PointOnObject(g58,g42)
    c: DistanceX(g-1,g58) = 43
    c: Coincident(g59,g58)
    c: Coincident(g60,g58)
    c: PointOnObject(g60,g56)
    c: Parallel(g60,g59)
    c: Perpendicular(g56,g60)
    c: Distance(g60) = 1.6
    c: DistanceX(g52,g-1) = 2
    c: Coincident(g61,g56)
    c: PointOnObject(g61,g-2)
    c: Vertical(g62)
    c: Coincident(g62,g55)
    c: PointOnObject(g55,g41)
    c: Vertical(g63)
    c: Vertical(g64)
    c: Equal(g64,g63)
    c: DistanceX(g63,g58) = 6.35
    c: DistanceX(g58,g64) = 6.35
    c: PointOnObject(g61,g42)
    c: DistanceY(g64,g64) = 2.2
    c: Coincident(g65,g63)
    c: Coincident(g67,g64)
    c: Coincident(g69,g68)
    c: Coincident(g69,g66)
    c: Tangent(g65,g70) = 1.5708
    c: Tangent(g66,g70) = 1.5708
    c: Tangent(g67,g71) = -1.5708
    c: Tangent(g68,g71) = -1.5708
    c: Coincident(g72,g63)
    c: Coincident(g72,g66)
    c: PointOnObject(g73,g70)
    c: PointOnObject(g74,g71)
    c: Coincident(g75,g64)
    c: Coincident(g75,g68)
    c: Vertical(g75)
    c: Coincident(g76,g74)
    c: PointOnObject(g76,g75)
    c: Horizontal(g76)
    c: PointOnObject(g71,g76)
    c: Equal(g67,g68)
    c: Equal(g68,g66)
    c: Equal(g65,g66)
    c: Equal(g71,g70)
    c: Vertical(g72)
    c: PointOnObject(g77,g72)
    c: Coincident(g77,g73)
    c: Horizontal(g77)
    c: PointOnObject(g70,g77)
    c: Angle(g65,g66) = 1.5708
    c: Angle(g68,g67) = 1.5708
    c: DistanceX(g76,g74) = 0.8
    c: Diameter(g71) = 0.8
    c: Coincident(g42,g7)
    c: DistanceX(g25,g39) = 14
    c: Coincident(g59,g7)
    c: Coincident(g57,g62)
    c: PointOnObject(g63,g42)
    c: PointOnObject(g64,g42)
    c: PointOnObject(g62,g42)
    c: Coincident(g78,g7)
    c: Coincident(g79,g78)
    c: Coincident(g79,g62)
    c: Coincident(g78,g61)
    c: PointOnObject(g78,g63)
    c: PointOnObject(g79,g64)
FEATURE [Sketcher::SketchObject] Sketch075  label="Sketch_Shell_Vert_CutPlug002"
  FullyConstrained = true
  MapMode = 5
  Placement = pos=(0,0,10) rot=(0,0,1;0rad)
  expr: Constraints[110] = <<params>>.xport_plug_plate_thick
  expr: Constraints[77] = <<params>>.back_vert_edge
  expr: Constraints[137] = <<params>>.shell_wall_thick + <<params>>.std_tol_clear
  expr: Constraints[134] = <<params>>.xport_plug_diam / 2
  expr: Constraints[47] = <<params>>.front_diameter
  expr: Constraints[170] = <<params>>.xport_clip_size
  expr: Constraints[63] = <<params>>.std_rad
  expr: Constraints[103] = <<params>>.xport_offset_loc
  expr: Constraints[101] = <<params>>.plate_length / 2 + <<params>>.std_wall_thick
  expr: Constraints[80] = <<params>>.std_rad
  expr: Constraints[36] = <<params>>.wheel_well_plate_width
  expr: Constraints[40] = <<params>>.plate_length
  expr: Constraints[65] = <<params>>.std_rad
  expr: Constraints[78] = <<params>>.wheel_well_clearance
  expr: Constraints[42] = <<params>>.tail_width
  expr: Constraints[135] = <<params>>.xport_plug_diam / 2
  expr: Constraints[79] = <<params>>.plate_width
  expr: Constraints[76] = <<params>>.front_vert_edge
  expr: Constraints[118] = <<params>>.std_wall_thick
  expr: Constraints[100] = <<params>>.std_wall_thick
  expr: Constraints[81] = <<params>>.std_rad
  expr: Constraints[41] = <<params>>.tail_rad
  expr: Constraints[168] = <<params>>.xport_clip_size
  sketch-geometry (68):
    g0: LineSegment StartX=-57.5 StartY=17 StartZ=0 EndX=-57.5 EndY=-17 EndZ=0
    g1: LineSegment StartX=57.5 StartY=17 StartZ=0 EndX=57.5 EndY=-17 EndZ=0
    g2: LineSegment StartX=-57.5 StartY=0 StartZ=0 EndX=57.5 EndY=0 EndZ=0
    g3: LineSegment StartX=-64.5 StartY=-24 StartZ=0 EndX=64.5 EndY=-24 EndZ=0
    g4: LineSegment StartX=-64.5 StartY=24 StartZ=0 EndX=64.5 EndY=24 EndZ=0
    g5: LineSegment StartX=-64.5 StartY=-24 StartZ=0 EndX=-75.5 EndY=-24 EndZ=0
    g6: LineSegment StartX=64.5 StartY=-24 StartZ=0 EndX=75.5 EndY=-24 EndZ=0
    g7: ArcOfCircle CenterX=0 CenterY=52.6846 CenterZ=0 NormalX=0 NormalY=0 NormalZ=1 AngleXU=0 Radius=112.5 StartAngle=3.96017 EndAngle=5.4646
    g8: LineSegment StartX=-64.5 StartY=24 StartZ=0 EndX=-75.5 EndY=24 EndZ=0
    g9: LineSegment StartX=64.5 StartY=24 StartZ=0 EndX=75.5 EndY=24 EndZ=0
    g10: LineSegment StartX=-77.1162 StartY=42.1781 StartZ=0 EndX=-29.0404 EndY=108.13 EndZ=0
    g11: LineSegment StartX=-25 StartY=110.185 StartZ=0 EndX=25 EndY=110.185 EndZ=0
    g12: LineSegment StartX=29.0404 StartY=108.13 StartZ=0 EndX=77.1162 EndY=42.1781 EndZ=0
    g13: LineSegment StartX=0 StartY=0 StartZ=0 EndX=0 EndY=110.185 EndZ=0
    g14: ArcOfCircle CenterX=-25 CenterY=105.185 CenterZ=0 NormalX=0 NormalY=0 NormalZ=1 AngleXU=0 Radius=5 StartAngle=1.5708 EndAngle=2.5117
    g15: ArcOfCircle CenterX=25 CenterY=105.185 CenterZ=0 NormalX=0 NormalY=0 NormalZ=1 AngleXU=0 Radius=5 StartAngle=0.629894 EndAngle=1.5708
    g16: ArcOfCircle CenterX=-64.5 CenterY=17 CenterZ=0 NormalX=0 NormalY=0 NormalZ=1 AngleXU=0 Radius=7 StartAngle=0 EndAngle=1.5708
    g17: ArcOfCircle CenterX=-64.5 CenterY=-17 CenterZ=0 NormalX=0 NormalY=0 NormalZ=1 AngleXU=0 Radius=7 StartAngle=4.71239 EndAngle=6.28319
    g18: ArcOfCircle CenterX=64.5 CenterY=-17 CenterZ=0 NormalX=0 NormalY=0 NormalZ=1 AngleXU=0 Radius=7 StartAngle=3.14159 EndAngle=4.71239
    g19: ArcOfCircle CenterX=64.5 CenterY=17 CenterZ=0 NormalX=0 NormalY=0 NormalZ=1 AngleXU=0 Radius=7 StartAngle=1.5708 EndAngle=3.14159
    g20: GeomPoint X=0 Y=-59.8154 Z=0
    g21: Circle CenterX=0 CenterY=52.6846 CenterZ=0 NormalX=0 NormalY=0 NormalZ=1 AngleXU=0 Radius=112.5
    g22: LineSegment StartX=77.5 StartY=26 StartZ=0 EndX=77.5 EndY=41 EndZ=0
    g23: LineSegment StartX=77.5 StartY=-26 StartZ=0 EndX=77.5 EndY=-28 EndZ=0
    g24: LineSegment StartX=-77.5 StartY=-28 StartZ=0 EndX=-77.5 EndY=-26 EndZ=0
    g25: LineSegment StartX=-77.5 StartY=26 StartZ=0 EndX=-77.5 EndY=41 EndZ=0
    g26: ArcOfCircle CenterX=75.5 CenterY=-28 CenterZ=0 NormalX=0 NormalY=0 NormalZ=1 AngleXU=0 Radius=2 StartAngle=5.4646 EndAngle=6.28319
    g27: ArcOfCircle CenterX=75.5 CenterY=-26 CenterZ=0 NormalX=0 NormalY=0 NormalZ=1 AngleXU=0 Radius=2 StartAngle=0 EndAngle=1.5708
    g28: ArcOfCircle CenterX=-75.5 CenterY=-28 CenterZ=0 NormalX=0 NormalY=0 NormalZ=1 AngleXU=0 Radius=2 StartAngle=3.14159 EndAngle=3.96017
    g29: ArcOfCircle CenterX=-75.5 CenterY=-26 CenterZ=0 NormalX=0 NormalY=0 NormalZ=1 AngleXU=0 Radius=2 StartAngle=1.5708 EndAngle=3.14159
    g30: ArcOfCircle CenterX=75.5 CenterY=26 CenterZ=0 NormalX=0 NormalY=0 NormalZ=1 AngleXU=0 Radius=2 StartAngle=4.71239 EndAngle=6.28319
    g31: ArcOfCircle CenterX=75.5 CenterY=41 CenterZ=0 NormalX=0 NormalY=0 NormalZ=1 AngleXU=0 Radius=2 StartAngle=4e-16 EndAngle=0.629894
    g32: ArcOfCircle CenterX=-75.5 CenterY=26 CenterZ=0 NormalX=0 NormalY=0 NormalZ=1 AngleXU=0 Radius=2 StartAngle=3.14159 EndAngle=4.71239
    g33: ArcOfCircle CenterX=-75.5 CenterY=41 CenterZ=0 NormalX=0 NormalY=0 NormalZ=1 AngleXU=0 Radius=2 StartAngle=2.5117 EndAngle=3.14159
    g34: LineSegment StartX=77.5 StartY=26 StartZ=0 EndX=77.5 EndY=-26 EndZ=0
    g35: LineSegment StartX=-77.5 StartY=26 StartZ=0 EndX=-77.5 EndY=-26 EndZ=0
    g36: LineSegment StartX=77.5 StartY=41 StartZ=0 EndX=77.5 EndY=-28 EndZ=0
    g37: LineSegment StartX=-77.5 StartY=41 StartZ=0 EndX=-77.5 EndY=-28 EndZ=0
    g38: ArcOfCircle CenterX=0 CenterY=52.6846 CenterZ=0 NormalX=0 NormalY=0 NormalZ=1 AngleXU=0 Radius=112.5 StartAngle=4.71239 EndAngle=5.4646
    g39: LineSegment StartX=-2 StartY=2 StartZ=0 EndX=-2 EndY=-87 EndZ=0
    g40: LineSegment StartX=76.8665 StartY=-38.9967 StartZ=0 EndX=76.8665 EndY=-87 EndZ=0
    g41: LineSegment StartX=-2 StartY=-87 StartZ=0 EndX=76.8665 EndY=-87 EndZ=0
    g42: LineSegment StartX=-2 StartY=2 StartZ=0 EndX=77.5 EndY=2 EndZ=0
    g43: LineSegment StartX=0 StartY=-70.7909 StartZ=0 EndX=76.8665 EndY=-38.9967 EndZ=0
    g44: GeomPoint X=43 Y=-51.2734 Z=0
    g45: LineSegment StartX=0 StartY=52.6846 StartZ=0 EndX=43 EndY=-51.2734 EndZ=0
    g46: LineSegment StartX=43.6116 StartY=-52.7519 StartZ=0 EndX=43 EndY=-51.2734 EndZ=0
    g47: LineSegment StartX=76.8665 StartY=-38.9967 StartZ=0 EndX=76.8665 EndY=-29.4604 EndZ=0
    g48: LineSegment StartX=-2.07e-14 StartY=-59.8154 StartZ=0 EndX=0 EndY=-70.7909 EndZ=0
    g49: LineSegment StartX=0 StartY=-70.7909 StartZ=0 EndX=-2.07e-14 EndY=-59.8154 EndZ=0
    g50: LineSegment StartX=77.5 StartY=2 StartZ=0 EndX=77.5 EndY=-28.863 EndZ=0
    g51: ArcOfCircle CenterX=0 CenterY=52.6846 CenterZ=0 NormalX=0 NormalY=0 NormalZ=1 AngleXU=0 Radius=112.5 StartAngle=4.71239 EndAngle=5.04422
    g52: ArcOfCircle CenterX=0 CenterY=52.6846 CenterZ=0 NormalX=0 NormalY=0 NormalZ=1 AngleXU=0 Radius=112.5 StartAngle=5.1665 EndAngle=5.47234
    g53: LineSegment StartX=36.65 StartY=-53.6781 StartZ=0 EndX=36.65 EndY=-51.3781 EndZ=0
    g54: LineSegment StartX=49.35 StartY=-48.4135 StartZ=0 EndX=49.35 EndY=-46.1135 EndZ=0
    g55: LineSegment StartX=36.65 StartY=-51.3781 StartZ=0 EndX=35.9672 EndY=-50.6953 EndZ=0
    g56: LineSegment StartX=35.9672 StartY=-50.1296 StartZ=0 EndX=36.65 EndY=-49.4468 EndZ=0
    g57: ArcOfCircle CenterX=36.25 CenterY=-50.4125 CenterZ=0 NormalX=0 NormalY=0 NormalZ=1 AngleXU=0 Radius=0.4 StartAngle=2.35619 EndAngle=3.92699
    g58: LineSegment StartX=49.35 StartY=-46.1135 StartZ=0 EndX=50.0328 EndY=-45.4307 EndZ=0
    g59: LineSegment StartX=50.0328 StartY=-44.865 StartZ=0 EndX=49.35 EndY=-44.1822 EndZ=0
    g60: ArcOfCircle CenterX=49.75 CenterY=-45.1479 CenterZ=0 NormalX=0 NormalY=0 NormalZ=1 AngleXU=0 Radius=0.4 StartAngle=5.49779 EndAngle=7.06858
    g61: LineSegment StartX=36.65 StartY=-51.3781 StartZ=0 EndX=36.65 EndY=-49.4468 EndZ=0
    g62: LineSegment StartX=49.35 StartY=-46.1135 StartZ=0 EndX=49.35 EndY=-44.1822 EndZ=0
    g63: LineSegment StartX=36.65 StartY=-49.4468 StartZ=0 EndX=49.35 EndY=-44.1822 EndZ=0
    g64: GeomPoint X=50.15 Y=-45.1479 Z=0
    g65: GeomPoint X=35.85 Y=-50.4125 Z=0
    g66: LineSegment StartX=35.85 StartY=-50.4125 StartZ=0 EndX=36.65 EndY=-50.4125 EndZ=0
    g67: LineSegment StartX=50.15 StartY=-45.1479 StartZ=0 EndX=49.35 EndY=-45.1479 EndZ=0
  constraints (171):
    c: Vertical(g0)
    c: Vertical(g1)
    c: Horizontal(g2)
    c: Symmetric(g2,g2,g-1)
    c: Horizontal(g3)
    c: Horizontal(g5)
    c: Horizontal(g6)
    c: PointOnObject(g7,g-2)
    c: Horizontal(g8)
    c: Horizontal(g9)
    c: Horizontal(g11)
    c: Coincident(g13,g-1)
    c: PointOnObject(g13,g-2)
    c: Tangent(g10,g14) = 1.5708
    c: Tangent(g11,g14) = 1.5708
    c: Tangent(g11,g15) = 1.5708
    c: Tangent(g12,g15) = 1.5708
    c: Tangent(g8,g16) = -1.5708
    c: Tangent(g0,g16) = 1.5708
    c: Tangent(g5,g17) = 1.5708
    c: Tangent(g0,g17) = 1.5708
    c: Tangent(g1,g18) = -1.5708
    c: Tangent(g6,g18) = -1.5708
    c: Tangent(g1,g19) = -1.5708
    c: Tangent(g9,g19) = 1.5708
    c: Equal(g15,g14)
    c: Symmetric(g11,g11,g13)
    c: Equal(g18,g19)
    c: Equal(g19,g16)
    c: Equal(g16,g17)
    c: PointOnObject(g20,g-2)
    c: PointOnObject(g20,g7)
    c: Coincident(g4,g8)
    c: Coincident(g4,g9)
    c: Coincident(g3,g6)
    c: Coincident(g3,g5)
    c: DistanceX(g2,g2) = 115
    c: Symmetric(g0,g0,g2)
    c: Symmetric(g1,g1,g2)
    c: Radius(g19) = 7
    c: DistanceY(g20,g11) = 170
    c: Radius(g15) = 5
    c: DistanceX(g11,g11) = 50
    c: Equal(g9,g8)
    c: Equal(g9,g6)
    c: Coincident(g21,g7)
    c: PointOnObject(g20,g21)
    c: Diameter(g21) = 225
    c: Vertical(g22)
    c: Vertical(g23)
    c: Vertical(g24)
    c: Vertical(g25)
    c: Equal(g5,g8)
    c: Equal(g10,g12)
    c: Tangent(g7,g26) = -1.5708
    c: Tangent(g23,g26) = 1.5708
    c: Tangent(g23,g27) = 1.5708
    c: Tangent(g6,g27) = 1.5708
    c: Tangent(g7,g28) = -1.5708
    c: Tangent(g24,g28) = 1.5708
    c: Tangent(g24,g29) = 1.5708
    c: Tangent(g5,g29) = -1.5708
    c: Equal(g29,g27)
    c: Radius(g27) = 2
    c: Equal(g26,g28)
    c: Radius(g26) = 2
    c: Tangent(g9,g30) = -1.5708
    c: Tangent(g22,g30) = -1.5708
    c: Tangent(g22,g31) = -1.5708
    c: Tangent(g12,g31) = 1.5708
    c: Tangent(g8,g32) = 1.5708
    c: Tangent(g25,g32) = 1.5708
    c: Tangent(g10,g33) = 1.5708
    c: Tangent(g25,g33) = 1.5708
    c: Equal(g30,g32)
    c: Equal(g31,g33)
    c: DistanceY(g23,g23) = 2
    c: DistanceY(g22,g22) = 15
    c: DistanceY(g6,g9) = 48
    c: DistanceX(g24,g23) = 155
    c: Radius(g30) = 2
    c: Radius(g31) = 2
    c: Coincident(g34,g22)
    c: Coincident(g34,g23)
    c: Coincident(g35,g25)
    c: Coincident(g35,g24)
    c: Coincident(g37,g28)
    c: Coincident(g37,g33)
    c: Coincident(g36,g31)
    c: Coincident(g36,g26)
    c: Coincident(g38,g7)
    c: PointOnObject(g38,g-2)
    c: Coincident(g38,g7)
    c: Vertical(g39)
    c: Vertical(g40)
    c: Coincident(g41,g39)
    c: Coincident(g41,g40)
    c: Horizontal(g41)
    c: Coincident(g42,g39)
    c: Horizontal(g42)
    c: DistanceY(g-1,g39) = 2
    c: DistanceY(g39,g-1) = 87
    c: PointOnObject(g44,g38)
    c: DistanceX(g-1,g44) = 43
    c: Coincident(g45,g44)
    c: Coincident(g45,g38)
    c: Coincident(g46,g44)
    c: PointOnObject(g46,g43)
    c: Parallel(g45,g46)
    c: Perpendicular(g46,g43)
    c: Distance(g46) = 1.6
    c: PointOnObject(g43,g-2)
    c: Coincident(g40,g43)
    c: Coincident(g47,g40)
    c: Coincident(g47,g38)
    c: Vertical(g47)
    c: Coincident(g48,g38)
    c: Coincident(g48,g43)
    c: DistanceX(g39,g43) = 2
    c: Coincident(g49,g43)
    c: PointOnObject(g49,g-2)
    c: PointOnObject(g42,g34)
    c: PointOnObject(g50,g34)
    c: Coincident(g50,g42)
    c: PointOnObject(g51,g13)
    c: Coincident(g51,g49)
    c: Coincident(g52,g51)
    c: Coincident(g52,g50)
    c: Coincident(g53,g51)
    c: Vertical(g53)
    c: Coincident(g54,g52)
    c: Vertical(g54)
    c: Equal(g51,g7)
    c: Equal(g52,g21)
    c: DistanceX(g51,g44) = 6.35
    c: DistanceX(g44,g52) = 6.35
    c: Equal(g54,g53)
    c: DistanceY(g54,g54) = 2.3
    c: PointOnObject(g49,g7)
    c: Coincident(g55,g53)
    c: Tangent(g55,g57) = 1.5708
    c: Tangent(g56,g57) = 1.5708
    c: Coincident(g58,g54)
    c: Tangent(g58,g60) = -1.5708
    c: Tangent(g59,g60) = -1.5708
    c: Coincident(g61,g53)
    c: Coincident(g61,g56)
    c: Vertical(g61)
    c: Coincident(g62,g54)
    c: Coincident(g62,g59)
    c: Vertical(g62)
    c: Equal(g58,g59)
    c: Equal(g55,g56)
    c: Equal(g60,g57)
    c: Coincident(g63,g56)
    c: Coincident(g63,g59)
    c: Angle(g59,g58) = 1.5708
    c: Angle(g55,g56) = 1.5708
    c: PointOnObject(g64,g60)
    c: PointOnObject(g65,g57)
    c: Coincident(g66,g65)
    c: PointOnObject(g66,g61)
    c: Horizontal(g66)
    c: PointOnObject(g57,g66)
    c: Coincident(g67,g64)
    c: PointOnObject(g67,g62)
    c: Horizontal(g67)
    c: PointOnObject(g60,g67)
    c: DistanceX(g67,g64) = 0.8
    c: Equal(g67,g66)
    c: Diameter(g60) = 0.8
FEATURE [Sketcher::SketchObject] Sketch076  label="Sketch_ClipsToTrim003"
  FullyConstrained = true
  MapMode = 5
  Placement = pos=(0,0,0) rot=(1,0,0;1.5708rad)
  Support = -> [XZ_Plane004]
  expr: Constraints[15] = <<params>>.std_wall_thick
  expr: Constraints[2] = <<params>>.xport_height_loc
  expr: Constraints[1] = <<params>>.xport_offset_loc
  expr: Constraints[0] = <<params>>.xport_plug_diam + 4 * <<params>>.xport_clip_size
  expr: Constraints[34] = <<params>>.std_wall_thick
  sketch-geometry (11):
    g0: Circle CenterX=43 CenterY=33.25 CenterZ=0 NormalX=0 NormalY=0 NormalZ=1 AngleXU=0 Radius=7.95
    g1: LineSegment StartX=35.1131 StartY=34.25 StartZ=0 EndX=50.8869 EndY=34.25 EndZ=0
    g2: LineSegment StartX=35.1131 StartY=32.25 StartZ=0 EndX=50.8869 EndY=32.25 EndZ=0
    g3: ArcOfCircle CenterX=43 CenterY=33.25 CenterZ=0 NormalX=0 NormalY=0 NormalZ=1 AngleXU=0 Radius=7.95 StartAngle=3.01547 EndAngle=3.26771
    g4: ArcOfCircle CenterX=43 CenterY=33.25 CenterZ=0 NormalX=0 NormalY=0 NormalZ=1 AngleXU=0 Radius=7.95 StartAngle=6.15707 EndAngle=6.40931
    g5: LineSegment StartX=35.1131 StartY=32.25 StartZ=0 EndX=42 EndY=32.25 EndZ=0
    g6: LineSegment StartX=44 StartY=32.25 StartZ=0 EndX=50.8869 EndY=32.25 EndZ=0
    g7: LineSegment StartX=43 StartY=33.25 StartZ=0 EndX=43 EndY=32.25 EndZ=0
    g8: LineSegment StartX=42 StartY=32.25 StartZ=0 EndX=42 EndY=25.3631 EndZ=0
    g9: LineSegment StartX=44 StartY=32.25 StartZ=0 EndX=44 EndY=25.3631 EndZ=0
    g10: ArcOfCircle CenterX=43 CenterY=33.25 CenterZ=0 NormalX=0 NormalY=0 NormalZ=1 AngleXU=0 Radius=7.95 StartAngle=4.58627 EndAngle=4.83851
  constraints (35):
    c: Diameter(g0) = 15.9
    c: DistanceX(g-1,g0) = 43
    c: DistanceY(g-1,g0) = 33.25
    c: PointOnObject(g1,g0)
    c: PointOnObject(g1,g0)
    c: Horizontal(g1)
    c: PointOnObject(g2,g0)
    c: Horizontal(g2)
    c: Symmetric(g1,g2,g0)
    c: Coincident(g3,g0)
    c: Coincident(g4,g3)
    c: Coincident(g3,g1)
    c: Coincident(g4,g1)
    c: PointOnObject(g4,g2)
    c: PointOnObject(g3,g2)
    c: DistanceY(g2,g1) = 2
    c: Horizontal(g5)
    c: Horizontal(g6)
    c: Coincident(g7,g3)
    c: PointOnObject(g7,g2)
    c: Vertical(g7)
    c: Symmetric(g5,g6,g7)
    c: PointOnObject(g5,g2)
    c: PointOnObject(g5,g0)
    c: PointOnObject(g6,g0)
    c: Coincident(g8,g5)
    c: PointOnObject(g8,g0)
    c: Vertical(g8)
    c: Coincident(g9,g6)
    c: Vertical(g9)
    c: PointOnObject(g9,g0)
    c: Coincident(g10,g3)
    c: Coincident(g10,g8)
    c: PointOnObject(g10,g9)
    c: DistanceX(g8,g9) = 2
FEATURE [Sketcher::SketchObject] Sketch077  label="Sketch_SplitPlug_P2_005"
  FullyConstrained = true
  MapMode = 5
  Placement = pos=(0,0,0) rot=(1,0,0;1.5708rad)
  Support = -> [XZ_Plane004]
  expr: Constraints[15] = <<params>>.std_wall_thick
  expr: Constraints[0] = <<params>>.xport_plug_diam + 4 * <<params>>.xport_clip_size
  expr: Constraints[1] = <<params>>.xport_offset_loc
  expr: Constraints[2] = <<params>>.xport_height_loc
  sketch-geometry (5):
    g0: Circle CenterX=43 CenterY=33.25 CenterZ=0 NormalX=0 NormalY=0 NormalZ=1 AngleXU=0 Radius=7.95
    g1: LineSegment StartX=35.1131 StartY=34.25 StartZ=0 EndX=50.8869 EndY=34.25 EndZ=0
    g2: LineSegment StartX=35.1131 StartY=32.25 StartZ=0 EndX=50.8869 EndY=32.25 EndZ=0
    g3: ArcOfCircle CenterX=43 CenterY=33.25 CenterZ=0 NormalX=0 NormalY=0 NormalZ=1 AngleXU=0 Radius=7.95 StartAngle=0.12612 EndAngle=3.01547
    g4: ArcOfCircle CenterX=43 CenterY=33.25 CenterZ=0 NormalX=0 NormalY=0 NormalZ=1 AngleXU=0 Radius=7.95 StartAngle=3.26771 EndAngle=6.15707
  constraints (16):
    c: Diameter(g0) = 15.9
    c: DistanceX(g-1,g0) = 43
    c: DistanceY(g-1,g0) = 33.25
    c: PointOnObject(g1,g0)
    c: PointOnObject(g1,g0)
    c: Horizontal(g1)
    c: PointOnObject(g2,g0)
    c: Horizontal(g2)
    c: Coincident(g3,g0)
    c: Coincident(g4,g3)
    c: Coincident(g3,g1)
    c: PointOnObject(g3,g1)
    c: Coincident(g4,g2)
    c: PointOnObject(g4,g2)
    c: Symmetric(g1,g2,g3)
    c: DistanceY(g2,g1) = 2
FEATURE [Sketcher::SketchObject] Sketch078  label="Sketch_SplitPlug_P3_005"
  FullyConstrained = true
  MapMode = 5
  Placement = pos=(0,0,0) rot=(1,0,0;1.5708rad)
  Support = -> [XZ_Plane004]
  expr: Constraints[15] = <<params>>.std_wall_thick
  expr: Constraints[0] = <<params>>.xport_plug_diam + 4 * <<params>>.xport_clip_size
  expr: Constraints[1] = <<params>>.xport_offset_loc
  expr: Constraints[2] = <<params>>.xport_height_loc
  sketch-geometry (8):
    g0: Circle CenterX=43 CenterY=33.25 CenterZ=0 NormalX=0 NormalY=0 NormalZ=1 AngleXU=0 Radius=7.95
    g1: LineSegment StartX=35.1131 StartY=34.25 StartZ=0 EndX=50.8869 EndY=34.25 EndZ=0
    g2: LineSegment StartX=35.1131 StartY=32.25 StartZ=0 EndX=50.8869 EndY=32.25 EndZ=0
    g3: ArcOfCircle CenterX=43 CenterY=33.25 CenterZ=0 NormalX=0 NormalY=0 NormalZ=1 AngleXU=0 Radius=7.95 StartAngle=0.12612 EndAngle=3.01547
    g4: ArcOfCircle CenterX=43 CenterY=33.25 CenterZ=0 NormalX=0 NormalY=0 NormalZ=1 AngleXU=0 Radius=7.95 StartAngle=3.26771 EndAngle=6.15707
    g5: ArcOfCircle CenterX=43 CenterY=33.25 CenterZ=0 NormalX=0 NormalY=0 NormalZ=1 AngleXU=0 Radius=7.95 StartAngle=1.5708 EndAngle=3.26771
    g6: LineSegment StartX=43 StartY=32.25 StartZ=0 EndX=43 EndY=41.2 EndZ=0
    g7: LineSegment StartX=43 StartY=32.25 StartZ=0 EndX=50.8869 EndY=32.25 EndZ=0
  constraints (26):
    c: Diameter(g0) = 15.9
    c: DistanceX(g-1,g0) = 43
    c: DistanceY(g-1,g0) = 33.25
    c: PointOnObject(g1,g0)
    c: PointOnObject(g1,g0)
    c: Horizontal(g1)
    c: PointOnObject(g2,g0)
    c: Horizontal(g2)
    c: Coincident(g3,g0)
    c: Coincident(g4,g3)
    c: Coincident(g3,g1)
    c: PointOnObject(g3,g1)
    c: Coincident(g4,g2)
    c: PointOnObject(g4,g2)
    c: Symmetric(g1,g2,g3)
    c: DistanceY(g2,g1) = 2
    c: Coincident(g5,g4)
    c: Coincident(g5,g4)
    c: PointOnObject(g6,g2)
    c: PointOnObject(g6,g3)
    c: Vertical(g6)
    c: PointOnObject(g4,g6)
    c: PointOnObject(g5,g6)
    c: Horizontal(g7)
    c: Coincident(g7,g6)
    c: PointOnObject(g7,g0)
FEATURE [Sketcher::SketchObject] Sketch079  label="Sketch_SplitPlug_P2_006"
  FullyConstrained = true
  MapMode = 5
  Placement = pos=(0,0,0) rot=(1,0,0;1.5708rad)
  Support = -> [XZ_Plane004]
  expr: Constraints[2] = <<params>>.xport_height_loc
  expr: Constraints[1] = <<params>>.xport_offset_loc
  expr: Constraints[0] = <<params>>.xport_plug_diam + 4 * <<params>>.xport_clip_size
  expr: Constraints[15] = <<params>>.std_wall_thick
  sketch-geometry (8):
    g0: Circle CenterX=43 CenterY=33.25 CenterZ=0 NormalX=0 NormalY=0 NormalZ=1 AngleXU=0 Radius=7.95
    g1: LineSegment StartX=35.1131 StartY=34.25 StartZ=0 EndX=50.8869 EndY=34.25 EndZ=0
    g2: LineSegment StartX=35.1131 StartY=32.25 StartZ=0 EndX=50.8869 EndY=32.25 EndZ=0
    g3: ArcOfCircle CenterX=43 CenterY=33.25 CenterZ=0 NormalX=0 NormalY=0 NormalZ=1 AngleXU=0 Radius=7.95 StartAngle=0.12612 EndAngle=3.01547
    g4: ArcOfCircle CenterX=43 CenterY=33.25 CenterZ=0 NormalX=0 NormalY=0 NormalZ=1 AngleXU=0 Radius=7.95 StartAngle=3.26771 EndAngle=6.15707
    g5: LineSegment StartX=35.1131 StartY=32.25 StartZ=0 EndX=43 EndY=32.25 EndZ=0
    g6: LineSegment StartX=43 StartY=32.25 StartZ=0 EndX=43 EndY=41.2 EndZ=0
    g7: ArcOfCircle CenterX=43 CenterY=33.25 CenterZ=0 NormalX=0 NormalY=0 NormalZ=1 AngleXU=0 Radius=7.95 StartAngle=6.15707 EndAngle=7.85398
  constraints (26):
    c: Diameter(g0) = 15.9
    c: DistanceX(g-1,g0) = 43
    c: DistanceY(g-1,g0) = 33.25
    c: PointOnObject(g1,g0)
    c: PointOnObject(g1,g0)
    c: Horizontal(g1)
    c: PointOnObject(g2,g0)
    c: Horizontal(g2)
    c: Coincident(g3,g0)
    c: Coincident(g4,g3)
    c: Coincident(g3,g1)
    c: PointOnObject(g3,g1)
    c: Coincident(g4,g2)
    c: PointOnObject(g4,g2)
    c: Symmetric(g1,g2,g3)
    c: DistanceY(g2,g1) = 2
    c: Horizontal(g5)
    c: PointOnObject(g6,g0)
    c: Vertical(g6)
    c: PointOnObject(g4,g6)
    c: Coincident(g6,g5)
    c: PointOnObject(g5,g2)
    c: PointOnObject(g5,g4)
    c: Coincident(g7,g4)
    c: Coincident(g7,g6)
    c: PointOnObject(g7,g2)
FEATURE [Sketcher::SketchObject] Sketch080  label="Sketch_SplitPlug_P1_003"
  FullyConstrained = true
  MapMode = 5
  Placement = pos=(0,0,0) rot=(1,0,0;1.5708rad)
  Support = -> [XZ_Plane004]
  expr: Constraints[0] = <<params>>.xport_plug_diam + 4 * <<params>>.xport_clip_size
  expr: Constraints[1] = <<params>>.xport_offset_loc
  expr: Constraints[2] = <<params>>.xport_height_loc
  expr: Constraints[6] = <<params>>.std_wall_thick / 2 + <<params>>.std_min_wall_thick
  sketch-geometry (3):
    g0: Circle CenterX=43 CenterY=33.25 CenterZ=0 NormalX=0 NormalY=0 NormalZ=1 AngleXU=0 Radius=7.95
    g1: LineSegment StartX=35.2565 StartY=35.05 StartZ=0 EndX=50.7435 EndY=35.05 EndZ=0
    g2: ArcOfCircle CenterX=43 CenterY=33.25 CenterZ=0 NormalX=0 NormalY=0 NormalZ=1 AngleXU=0 Radius=7.95 StartAngle=2.9132 EndAngle=6.51158
  constraints (10):
    c: Diameter(g0) = 15.9
    c: DistanceX(g-1,g0) = 43
    c: DistanceY(g-1,g0) = 33.25
    c: PointOnObject(g1,g0)
    c: PointOnObject(g1,g0)
    c: Horizontal(g1)
    c: DistanceY(g0,g1) = 1.8
    c: Coincident(g2,g0)
    c: Coincident(g2,g1)
    c: PointOnObject(g2,g1)
FEATURE [Sketcher::SketchObject] Sketch081  label="Sketch_SplitPlug_P3_006"
  FullyConstrained = true
  MapMode = 5
  Placement = pos=(0,0,0) rot=(1,0,0;1.5708rad)
  Support = -> [XZ_Plane004]
  expr: Constraints[2] = <<params>>.xport_height_loc
  expr: Constraints[1] = <<params>>.xport_offset_loc
  expr: Constraints[0] = <<params>>.xport_plug_diam + 4 * <<params>>.xport_clip_size
  expr: Constraints[15] = <<params>>.std_wall_thick
  sketch-geometry (5):
    g0: Circle CenterX=43 CenterY=33.25 CenterZ=0 NormalX=0 NormalY=0 NormalZ=1 AngleXU=0 Radius=7.95
    g1: LineSegment StartX=35.1131 StartY=34.25 StartZ=0 EndX=50.8869 EndY=34.25 EndZ=0
    g2: LineSegment StartX=35.1131 StartY=32.25 StartZ=0 EndX=50.8869 EndY=32.25 EndZ=0
    g3: ArcOfCircle CenterX=43 CenterY=33.25 CenterZ=0 NormalX=0 NormalY=0 NormalZ=1 AngleXU=0 Radius=7.95 StartAngle=0.12612 EndAngle=3.01547
    g4: ArcOfCircle CenterX=43 CenterY=33.25 CenterZ=0 NormalX=0 NormalY=0 NormalZ=1 AngleXU=0 Radius=7.95 StartAngle=3.26771 EndAngle=6.15707
  constraints (16):
    c: Diameter(g0) = 15.9
    c: DistanceX(g-1,g0) = 43
    c: DistanceY(g-1,g0) = 33.25
    c: PointOnObject(g1,g0)
    c: PointOnObject(g1,g0)
    c: Horizontal(g1)
    c: PointOnObject(g2,g0)
    c: Horizontal(g2)
    c: Coincident(g3,g0)
    c: Coincident(g4,g3)
    c: Coincident(g3,g1)
    c: PointOnObject(g3,g1)
    c: Coincident(g4,g2)
    c: PointOnObject(g4,g2)
    c: Symmetric(g1,g2,g3)
    c: DistanceY(g2,g1) = 2
FEATURE [Sketcher::SketchObject] Sketch082  label="Sketch_SplitPlug_P4_003"
  FullyConstrained = true
  MapMode = 5
  Placement = pos=(0,0,0) rot=(1,0,0;1.5708rad)
  Support = -> [XZ_Plane004]
  expr: Constraints[0] = <<params>>.xport_plug_diam + 4 * <<params>>.xport_clip_size
  expr: Constraints[1] = <<params>>.xport_offset_loc
  expr: Constraints[2] = <<params>>.xport_height_loc
  expr: Constraints[9] = <<params>>.std_wall_thick / 2 + <<params>>.std_min_wall_thick
  sketch-geometry (3):
    g0: Circle CenterX=43 CenterY=33.25 CenterZ=0 NormalX=0 NormalY=0 NormalZ=1 AngleXU=0 Radius=7.95
    g1: LineSegment StartX=35.2565 StartY=31.45 StartZ=0 EndX=50.7435 EndY=31.45 EndZ=0
    g2: ArcOfCircle CenterX=43 CenterY=33.25 CenterZ=0 NormalX=0 NormalY=0 NormalZ=1 AngleXU=0 Radius=7.95 StartAngle=6.05479 EndAngle=9.65317
  constraints (10):
    c: Diameter(g0) = 15.9
    c: DistanceX(g-1,g0) = 43
    c: DistanceY(g-1,g0) = 33.25
    c: PointOnObject(g1,g0)
    c: PointOnObject(g1,g0)
    c: Horizontal(g1)
    c: Coincident(g2,g0)
    c: Coincident(g2,g1)
    c: PointOnObject(g2,g1)
    c: DistanceY(g1,g2) = 1.8
FEATURE [Sketcher::SketchObject] Sketch083
  FullyConstrained = true
  MapMode = 5
  Placement = pos=(0,0,0) rot=(1,0,0;1.5708rad)
  Support = -> [XZ_Plane004]
  expr: Constraints[2] = <<params>>.xport_height_loc
  expr: Constraints[1] = <<params>>.xport_offset_loc
  expr: Constraints[0] = <<params>>.xport_plug_diam
  sketch-geometry (1):
    g0: Circle CenterX=43 CenterY=33.25 CenterZ=0 NormalX=0 NormalY=0 NormalZ=1 AngleXU=0 Radius=6.35
  constraints (3):
    c: Diameter(g0) = 12.7
    c: DistanceX(g-1,g0) = 43
    c: DistanceY(g-1,g0) = 33.25
FEATURE [PartDesign::Pad] Pad006  label="Pad_Plug002"
  Direction = (1,1,1)
  Length = 85
  Length2 = 100
  Placement = pos=(0,0,0) rot=(1,0,0;1.5708rad)
  Profile = -> Sketch083
  Type = 0
  expr: Length = <<params>>.plate_length / 2
FEATURE [PartDesign::Pad] Pad005  label="Pad_ClipsToTrim002"
  BaseFeature = -> Pad006
  Direction = (1,1,1)
  Length = 85
  Length2 = 100
  Placement = pos=(0,0,0) rot=(1,0,0;1.5708rad)
  Profile = -> Sketch076
  Type = 0
  expr: Length = <<params>>.plate_length / 2
FEATURE [PartDesign::Pocket] Pocket002  label="Pocket_HollowTube002"
  BaseFeature = -> Pad005
  Length = 5
  Length2 = 100
  Midplane = true
  Placement = pos=(0,0,0) rot=(1,0,0;1.5708rad)
  Profile = -> Sketch071
  Type = 1
FEATURE [PartDesign::SubtractiveLoft] SubtractiveLoft003  label="SubtractiveLoft_CutClips002"
  BaseFeature = -> Pocket002
  Closed = false
  Placement = pos=(0,0,0) rot=(1,0,0;1.5708rad)
  Profile = -> Sketch075
  Ruled = false
  Sections = -> [Sketch072]
FEATURE [PartDesign::Chamfer] Chamfer003  label="Chamfer_FrontEdge002"
  Angle = 45
  Base = -> SubtractiveLoft003 [Edge13,Edge17,Edge8]
  BaseFeature = -> SubtractiveLoft003
  ChamferType = 0
  FlipDirection = false
  Placement = pos=(0,0,0) rot=(1,0,0;1.5708rad)
  Size = 1
  Size2 = 1
  SupportTransform = false
FEATURE [PartDesign::Plane] DatumPlane010  label="Datum_ShellVert005"
  AttachmentOffset = pos=(0,0,10) rot=(0,0,1;0rad)
  Length = 75.8412
  MapMode = 5
  Placement = pos=(0,0,10) rot=(0,0,1;0rad)
  ResizeMode = 0
  Support = -> [XY_Plane005]
  Width = 84.0135
  expr: .AttachmentOffset.Base.z = <<params>>.shell_vertheight
FEATURE [Sketcher::SketchObject] Sketch073  label="Sketch_Shell_Vert005"
  FullyConstrained = true
  MapMode = 5
  Placement = pos=(0,0,10) rot=(0,0,1;0rad)
  Support = -> [DatumPlane010]
  expr: Constraints[40] = <<params>>.plate_length
  expr: Constraints[65] = <<params>>.std_rad
  expr: Constraints[42] = <<params>>.tail_width
  expr: Constraints[78] = <<params>>.wheel_well_clearance
  expr: Constraints[79] = <<params>>.plate_width
  expr: Constraints[36] = <<params>>.wheel_well_plate_width
  expr: Constraints[47] = <<params>>.front_diameter
  expr: Constraints[63] = <<params>>.std_rad
  expr: Constraints[76] = <<params>>.front_vert_edge
  expr: Constraints[77] = <<params>>.back_vert_edge
  expr: Constraints[80] = <<params>>.std_rad
  expr: Constraints[81] = <<params>>.std_rad
  expr: Constraints[41] = <<params>>.tail_rad
  sketch-geometry (38):
    g0: LineSegment StartX=-57.5 StartY=17 StartZ=0 EndX=-57.5 EndY=-17 EndZ=0
    g1: LineSegment StartX=57.5 StartY=17 StartZ=0 EndX=57.5 EndY=-17 EndZ=0
    g2: LineSegment StartX=-57.5 StartY=0 StartZ=0 EndX=57.5 EndY=0 EndZ=0
    g3: LineSegment StartX=-64.5 StartY=-24 StartZ=0 EndX=64.5 EndY=-24 EndZ=0
    g4: LineSegment StartX=-64.5 StartY=24 StartZ=0 EndX=64.5 EndY=24 EndZ=0
    g5: LineSegment StartX=-64.5 StartY=-24 StartZ=0 EndX=-75.5 EndY=-24 EndZ=0
    g6: LineSegment StartX=64.5 StartY=-24 StartZ=0 EndX=75.5 EndY=-24 EndZ=0
    g7: ArcOfCircle CenterX=0 CenterY=52.6846 CenterZ=0 NormalX=0 NormalY=0 NormalZ=1 AngleXU=0 Radius=112.5 StartAngle=3.96017 EndAngle=5.4646
    g8: LineSegment StartX=-64.5 StartY=24 StartZ=0 EndX=-75.5 EndY=24 EndZ=0
    g9: LineSegment StartX=64.5 StartY=24 StartZ=0 EndX=75.5 EndY=24 EndZ=0
    g10: LineSegment StartX=-77.1162 StartY=42.1781 StartZ=0 EndX=-29.0404 EndY=108.13 EndZ=0
    g11: LineSegment StartX=-25 StartY=110.185 StartZ=0 EndX=25 EndY=110.185 EndZ=0
    g12: LineSegment StartX=29.0404 StartY=108.13 StartZ=0 EndX=77.1162 EndY=42.1781 EndZ=0
    g13: LineSegment StartX=0 StartY=0 StartZ=0 EndX=0 EndY=110.185 EndZ=0
    g14: ArcOfCircle CenterX=-25 CenterY=105.185 CenterZ=0 NormalX=0 NormalY=0 NormalZ=1 AngleXU=0 Radius=5 StartAngle=1.5708 EndAngle=2.5117
    g15: ArcOfCircle CenterX=25 CenterY=105.185 CenterZ=0 NormalX=0 NormalY=0 NormalZ=1 AngleXU=0 Radius=5 StartAngle=0.629894 EndAngle=1.5708
    g16: ArcOfCircle CenterX=-64.5 CenterY=17 CenterZ=0 NormalX=0 NormalY=0 NormalZ=1 AngleXU=0 Radius=7 StartAngle=0 EndAngle=1.5708
    g17: ArcOfCircle CenterX=-64.5 CenterY=-17 CenterZ=0 NormalX=0 NormalY=0 NormalZ=1 AngleXU=0 Radius=7 StartAngle=4.71239 EndAngle=6.28319
    g18: ArcOfCircle CenterX=64.5 CenterY=-17 CenterZ=0 NormalX=0 NormalY=0 NormalZ=1 AngleXU=0 Radius=7 StartAngle=3.14159 EndAngle=4.71239
    g19: ArcOfCircle CenterX=64.5 CenterY=17 CenterZ=0 NormalX=0 NormalY=0 NormalZ=1 AngleXU=0 Radius=7 StartAngle=1.5708 EndAngle=3.14159
    g20: GeomPoint X=0 Y=-59.8154 Z=0
    g21: Circle CenterX=0 CenterY=52.6846 CenterZ=0 NormalX=0 NormalY=0 NormalZ=1 AngleXU=0 Radius=112.5
    g22: LineSegment StartX=77.5 StartY=26 StartZ=0 EndX=77.5 EndY=41 EndZ=0
    g23: LineSegment StartX=77.5 StartY=-26 StartZ=0 EndX=77.5 EndY=-28 EndZ=0
    g24: LineSegment StartX=-77.5 StartY=-28 StartZ=0 EndX=-77.5 EndY=-26 EndZ=0
    g25: LineSegment StartX=-77.5 StartY=26 StartZ=0 EndX=-77.5 EndY=41 EndZ=0
    g26: ArcOfCircle CenterX=75.5 CenterY=-28 CenterZ=0 NormalX=0 NormalY=0 NormalZ=1 AngleXU=0 Radius=2 StartAngle=5.4646 EndAngle=6.28319
    g27: ArcOfCircle CenterX=75.5 CenterY=-26 CenterZ=0 NormalX=0 NormalY=0 NormalZ=1 AngleXU=0 Radius=2 StartAngle=-9e-16 EndAngle=1.5708
    g28: ArcOfCircle CenterX=-75.5 CenterY=-28 CenterZ=0 NormalX=0 NormalY=0 NormalZ=1 AngleXU=0 Radius=2 StartAngle=3.14159 EndAngle=3.96017
    g29: ArcOfCircle CenterX=-75.5 CenterY=-26 CenterZ=0 NormalX=0 NormalY=0 NormalZ=1 AngleXU=0 Radius=2 StartAngle=1.5708 EndAngle=3.14159
    g30: ArcOfCircle CenterX=75.5 CenterY=26 CenterZ=0 NormalX=0 NormalY=0 NormalZ=1 AngleXU=0 Radius=2 StartAngle=4.71239 EndAngle=6.28319
    g31: ArcOfCircle CenterX=75.5 CenterY=41 CenterZ=0 NormalX=0 NormalY=0 NormalZ=1 AngleXU=0 Radius=2 StartAngle=0 EndAngle=0.629894
    g32: ArcOfCircle CenterX=-75.5 CenterY=26 CenterZ=0 NormalX=0 NormalY=0 NormalZ=1 AngleXU=0 Radius=2 StartAngle=3.14159 EndAngle=4.71239
    g33: ArcOfCircle CenterX=-75.5 CenterY=41 CenterZ=0 NormalX=0 NormalY=0 NormalZ=1 AngleXU=0 Radius=2 StartAngle=2.5117 EndAngle=3.14159
    g34: LineSegment StartX=77.5 StartY=26 StartZ=0 EndX=77.5 EndY=-26 EndZ=0
    g35: LineSegment StartX=-77.5 StartY=26 StartZ=0 EndX=-77.5 EndY=-26 EndZ=0
    g36: LineSegment StartX=77.5 StartY=41 StartZ=0 EndX=77.5 EndY=-28 EndZ=0
    g37: LineSegment StartX=-77.5 StartY=41 StartZ=0 EndX=-77.5 EndY=-28 EndZ=0
  constraints (90):
    c: Vertical(g0)
    c: Vertical(g1)
    c: Horizontal(g2)
    c: Symmetric(g2,g2,g-1)
    c: Horizontal(g3)
    c: Horizontal(g5)
    c: Horizontal(g6)
    c: PointOnObject(g7,g-2)
    c: Horizontal(g8)
    c: Horizontal(g9)
    c: Horizontal(g11)
    c: Coincident(g13,g-1)
    c: PointOnObject(g13,g-2)
    c: Tangent(g10,g14) = 1.5708
    c: Tangent(g11,g14) = 1.5708
    c: Tangent(g11,g15) = 1.5708
    c: Tangent(g12,g15) = 1.5708
    c: Tangent(g8,g16) = -1.5708
    c: Tangent(g0,g16) = 1.5708
    c: Tangent(g5,g17) = 1.5708
    c: Tangent(g0,g17) = 1.5708
    c: Tangent(g1,g18) = -1.5708
    c: Tangent(g6,g18) = -1.5708
    c: Tangent(g1,g19) = -1.5708
    c: Tangent(g9,g19) = 1.5708
    c: Equal(g15,g14)
    c: Symmetric(g11,g11,g13)
    c: Equal(g18,g19)
    c: Equal(g19,g16)
    c: Equal(g16,g17)
    c: PointOnObject(g20,g-2)
    c: PointOnObject(g20,g7)
    c: Coincident(g4,g8)
    c: Coincident(g4,g9)
    c: Coincident(g3,g6)
    c: Coincident(g3,g5)
    c: DistanceX(g2,g2) = 115
    c: Symmetric(g0,g0,g2)
    c: Symmetric(g1,g1,g2)
    c: Radius(g19) = 7
    c: DistanceY(g20,g11) = 170
    c: Radius(g15) = 5
    c: DistanceX(g11,g11) = 50
    c: Equal(g9,g8)
    c: Equal(g9,g6)
    c: Coincident(g21,g7)
    c: PointOnObject(g20,g21)
    c: Diameter(g21) = 225
    c: Vertical(g22)
    c: Vertical(g23)
    c: Vertical(g24)
    c: Vertical(g25)
    c: Equal(g5,g8)
    c: Equal(g10,g12)
    c: Tangent(g7,g26) = -1.5708
    c: Tangent(g23,g26) = 1.5708
    c: Tangent(g23,g27) = 1.5708
    c: Tangent(g6,g27) = 1.5708
    c: Tangent(g7,g28) = -1.5708
    c: Tangent(g24,g28) = 1.5708
    c: Tangent(g24,g29) = 1.5708
    c: Tangent(g5,g29) = -1.5708
    c: Equal(g29,g27)
    c: Radius(g27) = 2
    c: Equal(g26,g28)
    c: Radius(g26) = 2
    c: Tangent(g9,g30) = -1.5708
    c: Tangent(g22,g30) = -1.5708
    c: Tangent(g22,g31) = -1.5708
    c: Tangent(g12,g31) = 1.5708
    c: Tangent(g8,g32) = 1.5708
    c: Tangent(g25,g32) = 1.5708
    c: Tangent(g10,g33) = 1.5708
    c: Tangent(g25,g33) = 1.5708
    c: Equal(g30,g32)
    c: Equal(g31,g33)
    c: DistanceY(g23,g23) = 2
    c: DistanceY(g22,g22) = 15
    c: DistanceY(g6,g9) = 48
    c: DistanceX(g24,g23) = 155
    c: Radius(g30) = 2
    c: Radius(g31) = 2
    c: Coincident(g34,g22)
    c: Coincident(g34,g23)
    c: Coincident(g35,g25)
    c: Coincident(g35,g24)
    c: Coincident(g37,g28)
    c: Coincident(g37,g33)
    c: Coincident(g36,g31)
    c: Coincident(g36,g26)
FEATURE [PartDesign::Plane] DatumPlane011  label="Datum_ShellTot005"
  AttachmentOffset = pos=(0,0,42) rot=(0,0,1;0rad)
  Length = 75.8412
  MapMode = 5
  Placement = pos=(0,0,42) rot=(0,0,1;0rad)
  ResizeMode = 0
  Support = -> [XY_Plane005]
  Width = 84.0135
  expr: .AttachmentOffset.Base.z = <<params>>.shell_totheight
FEATURE [Sketcher::SketchObject] Sketch074  label="Sketch_Shell_Top005"
  FullyConstrained = true
  MapMode = 5
  Placement = pos=(0,0,42) rot=(0,0,1;0rad)
  Support = -> [DatumPlane011]
  expr: Constraints[41] = <<params>>.tail_rad
  expr: Constraints[76] = <<params>>.front_vert_edge
  expr: Constraints[47] = <<params>>.front_diameter
  expr: Constraints[36] = <<params>>.wheel_well_plate_width - 2 * Spreadsheet.shell_overhang_leng
  expr: Constraints[79] = <<params>>.plate_width
  expr: Constraints[42] = <<params>>.tail_width
  expr: Constraints[78] = <<params>>.wheel_well_clearance
  expr: Constraints[65] = <<params>>.std_rad
  expr: Constraints[40] = <<params>>.plate_length
  expr: Constraints[88] = Spreadsheet.shell_overhang_leng
  expr: Constraints[81] = <<params>>.std_rad
  expr: Constraints[63] = <<params>>.std_rad
  expr: Constraints[77] = <<params>>.back_vert_edge
  expr: Constraints[120] = Spreadsheet.shell_overhang_leng
  expr: Constraints[80] = <<params>>.std_rad
  expr: Constraints[119] = Spreadsheet.shell_overhang_leng
  expr: Constraints[123] = <<params>>.shell_overhang_leng
  sketch-geometry (52):
    g0: LineSegment StartX=-43.5 StartY=17 StartZ=0 EndX=-43.5 EndY=-17 EndZ=0
    g1: LineSegment StartX=43.5 StartY=17 StartZ=0 EndX=43.5 EndY=-17 EndZ=0
    g2: LineSegment StartX=-43.5 StartY=0 StartZ=0 EndX=43.5 EndY=0 EndZ=0
    g3: LineSegment StartX=-50.5 StartY=-24 StartZ=0 EndX=50.5 EndY=-24 EndZ=0
    g4: LineSegment StartX=-50.5 StartY=24 StartZ=0 EndX=50.5 EndY=24 EndZ=0
    g5: LineSegment StartX=-50.5 StartY=-24 StartZ=0 EndX=-75.5 EndY=-24 EndZ=0
    g6: LineSegment StartX=50.5 StartY=-24 StartZ=0 EndX=75.5 EndY=-24 EndZ=0
    g7: ArcOfCircle CenterX=0 CenterY=52.6846 CenterZ=0 NormalX=0 NormalY=0 NormalZ=1 AngleXU=0 Radius=112.5 StartAngle=3.96017 EndAngle=5.4646
    g8: LineSegment StartX=-50.5 StartY=24 StartZ=0 EndX=-75.5 EndY=24 EndZ=0
    g9: LineSegment StartX=50.5 StartY=24 StartZ=0 EndX=75.5 EndY=24 EndZ=0
    g10: LineSegment StartX=-77.1162 StartY=42.1781 StartZ=0 EndX=-29.0404 EndY=108.13 EndZ=0
    g11: LineSegment StartX=-25 StartY=110.185 StartZ=0 EndX=25 EndY=110.185 EndZ=0
    g12: LineSegment StartX=29.0404 StartY=108.13 StartZ=0 EndX=77.1162 EndY=42.1781 EndZ=0
    g13: LineSegment StartX=0 StartY=0 StartZ=0 EndX=0 EndY=110.185 EndZ=0
    g14: ArcOfCircle CenterX=-25 CenterY=105.185 CenterZ=0 NormalX=0 NormalY=0 NormalZ=1 AngleXU=0 Radius=5 StartAngle=1.5708 EndAngle=2.5117
    g15: ArcOfCircle CenterX=25 CenterY=105.185 CenterZ=0 NormalX=0 NormalY=0 NormalZ=1 AngleXU=0 Radius=5 StartAngle=0.629894 EndAngle=1.5708
    g16: ArcOfCircle CenterX=-50.5 CenterY=17 CenterZ=0 NormalX=0 NormalY=0 NormalZ=1 AngleXU=0 Radius=7 StartAngle=0 EndAngle=1.5708
    g17: ArcOfCircle CenterX=-50.5 CenterY=-17 CenterZ=0 NormalX=0 NormalY=0 NormalZ=1 AngleXU=0 Radius=7 StartAngle=4.71239 EndAngle=6.28319
    g18: ArcOfCircle CenterX=50.5 CenterY=-17 CenterZ=0 NormalX=0 NormalY=0 NormalZ=1 AngleXU=0 Radius=7 StartAngle=3.14159 EndAngle=4.71239
    g19: ArcOfCircle CenterX=50.5 CenterY=17 CenterZ=0 NormalX=0 NormalY=0 NormalZ=1 AngleXU=0 Radius=7 StartAngle=1.5708 EndAngle=3.14159
    g20: GeomPoint X=0 Y=-59.8154 Z=0
    g21: Circle CenterX=0 CenterY=52.6846 CenterZ=0 NormalX=0 NormalY=0 NormalZ=1 AngleXU=0 Radius=112.5
    g22: LineSegment StartX=77.5 StartY=26 StartZ=0 EndX=77.5 EndY=41 EndZ=0
    g23: LineSegment StartX=77.5 StartY=-26 StartZ=0 EndX=77.5 EndY=-28 EndZ=0
    g24: LineSegment StartX=-77.5 StartY=-28 StartZ=0 EndX=-77.5 EndY=-26 EndZ=0
    g25: LineSegment StartX=-77.5 StartY=26 StartZ=0 EndX=-77.5 EndY=41 EndZ=0
    g26: ArcOfCircle CenterX=75.5 CenterY=-28 CenterZ=0 NormalX=0 NormalY=0 NormalZ=1 AngleXU=0 Radius=2 StartAngle=5.4646 EndAngle=6.28319
    g27: ArcOfCircle CenterX=75.5 CenterY=-26 CenterZ=0 NormalX=0 NormalY=0 NormalZ=1 AngleXU=0 Radius=2 StartAngle=0 EndAngle=1.5708
    g28: ArcOfCircle CenterX=-75.5 CenterY=-28 CenterZ=0 NormalX=0 NormalY=0 NormalZ=1 AngleXU=0 Radius=2 StartAngle=3.14159 EndAngle=3.96017
    g29: ArcOfCircle CenterX=-75.5 CenterY=-26 CenterZ=0 NormalX=0 NormalY=0 NormalZ=1 AngleXU=0 Radius=2 StartAngle=1.5708 EndAngle=3.14159
    g30: ArcOfCircle CenterX=75.5 CenterY=26 CenterZ=0 NormalX=0 NormalY=0 NormalZ=1 AngleXU=0 Radius=2 StartAngle=4.71239 EndAngle=6.28319
    g31: ArcOfCircle CenterX=75.5 CenterY=41 CenterZ=0 NormalX=0 NormalY=0 NormalZ=1 AngleXU=0 Radius=2 StartAngle=4e-16 EndAngle=0.629894
    g32: ArcOfCircle CenterX=-75.5 CenterY=26 CenterZ=0 NormalX=0 NormalY=0 NormalZ=1 AngleXU=0 Radius=2 StartAngle=3.14159 EndAngle=4.71239
    g33: ArcOfCircle CenterX=-75.5 CenterY=41 CenterZ=0 NormalX=0 NormalY=0 NormalZ=1 AngleXU=0 Radius=2 StartAngle=2.5117 EndAngle=3.14159
    g34: LineSegment StartX=77.5 StartY=26 StartZ=0 EndX=77.5 EndY=-26 EndZ=0
    g35: LineSegment StartX=-77.5 StartY=26 StartZ=0 EndX=-77.5 EndY=-26 EndZ=0
    g36: LineSegment StartX=-17.8805 StartY=96.1846 StartZ=0 EndX=17.8805 EndY=96.1846 EndZ=0
    g37: GeomPoint X=0 Y=96.1846 Z=0
    g38: LineSegment StartX=-21.921 StartY=94.1299 StartZ=0 EndX=-63.1162 EndY=37.617 EndZ=0
    g39: LineSegment StartX=-63.5 StartY=36.4389 StartZ=0 EndX=-63.5 EndY=-24 EndZ=0
    g40: LineSegment StartX=21.921 StartY=94.1299 StartZ=0 EndX=63.1162 EndY=37.617 EndZ=0
    g41: LineSegment StartX=63.5 StartY=36.4389 StartZ=0 EndX=63.5 EndY=-24 EndZ=0
    g42: ArcOfCircle CenterX=0 CenterY=61.5293 CenterZ=0 NormalX=0 NormalY=0 NormalZ=1 AngleXU=0 Radius=107.345 StartAngle=4.08899 EndAngle=5.33579
    g43: LineSegment StartX=-63.5 StartY=36.4389 StartZ=0 EndX=63.5 EndY=36.4389 EndZ=0
    g44: GeomPoint X=0 Y=-45.8154 Z=0
    g45: ArcOfCircle CenterX=-17.8805 CenterY=91.1846 CenterZ=0 NormalX=0 NormalY=0 NormalZ=1 AngleXU=0 Radius=5 StartAngle=1.5708 EndAngle=2.5117
    g46: ArcOfCircle CenterX=17.8805 CenterY=91.1846 CenterZ=0 NormalX=0 NormalY=0 NormalZ=1 AngleXU=0 Radius=5 StartAngle=0.629894 EndAngle=1.5708
    g47: ArcOfCircle CenterX=61.5 CenterY=36.4389 CenterZ=0 NormalX=0 NormalY=0 NormalZ=1 AngleXU=0 Radius=2 StartAngle=-9e-16 EndAngle=0.629894
    g48: ArcOfCircle CenterX=-61.5 CenterY=36.4389 CenterZ=0 NormalX=0 NormalY=0 NormalZ=1 AngleXU=0 Radius=2 StartAngle=2.5117 EndAngle=3.14159
    g49: ArcOfCircle CenterX=61.5 CenterY=-24 CenterZ=0 NormalX=0 NormalY=0 NormalZ=1 AngleXU=0 Radius=2 StartAngle=5.33579 EndAngle=6.28319
    g50: ArcOfCircle CenterX=-61.5 CenterY=-24 CenterZ=0 NormalX=0 NormalY=0 NormalZ=1 AngleXU=0 Radius=2 StartAngle=3.14159 EndAngle=4.08899
    g51: LineSegment StartX=-29.0404 StartY=108.13 StartZ=0 EndX=-17.7272 EndY=99.883 EndZ=0
  constraints (125):
    c: Vertical(g0)
    c: Vertical(g1)
    c: Horizontal(g2)
    c: Symmetric(g2,g2,g-1)
    c: Horizontal(g3)
    c: Horizontal(g5)
    c: Horizontal(g6)
    c: PointOnObject(g7,g-2)
    c: Horizontal(g8)
    c: Horizontal(g9)
    c: Horizontal(g11)
    c: Coincident(g13,g-1)
    c: PointOnObject(g13,g-2)
    c: Tangent(g10,g14) = 1.5708
    c: Tangent(g11,g14) = 1.5708
    c: Tangent(g11,g15) = 1.5708
    c: Tangent(g12,g15) = 1.5708
    c: Tangent(g8,g16) = -1.5708
    c: Tangent(g0,g16) = 1.5708
    c: Tangent(g5,g17) = 1.5708
    c: Tangent(g0,g17) = 1.5708
    c: Tangent(g1,g18) = -1.5708
    c: Tangent(g6,g18) = -1.5708
    c: Tangent(g1,g19) = -1.5708
    c: Tangent(g9,g19) = 1.5708
    c: Equal(g15,g14)
    c: Symmetric(g11,g11,g13)
    c: Equal(g18,g19)
    c: Equal(g19,g16)
    c: Equal(g16,g17)
    c: PointOnObject(g20,g-2)
    c: PointOnObject(g20,g7)
    c: Coincident(g4,g8)
    c: Coincident(g4,g9)
    c: Coincident(g3,g6)
    c: Coincident(g3,g5)
    c: DistanceX(g2,g2) = 87
    c: Symmetric(g0,g0,g2)
    c: Symmetric(g1,g1,g2)
    c: Radius(g19) = 7
    c: DistanceY(g20,g11) = 170
    c: Radius(g15) = 5
    c: DistanceX(g11,g11) = 50
    c: Equal(g9,g8)
    c: Equal(g9,g6)
    c: Coincident(g21,g7)
    c: PointOnObject(g20,g21)
    c: Diameter(g21) = 225
    c: Vertical(g22)
    c: Vertical(g23)
    c: Vertical(g24)
    c: Vertical(g25)
    c: Equal(g5,g8)
    c: Equal(g10,g12)
    c: Tangent(g7,g26) = -1.5708
    c: Tangent(g23,g26) = 1.5708
    c: Tangent(g23,g27) = 1.5708
    c: Tangent(g6,g27) = 1.5708
    c: Tangent(g7,g28) = -1.5708
    c: Tangent(g24,g28) = 1.5708
    c: Tangent(g24,g29) = 1.5708
    c: Tangent(g5,g29) = -1.5708
    c: Equal(g29,g27)
    c: Radius(g27) = 2
    c: Equal(g26,g28)
    c: Radius(g26) = 2
    c: Tangent(g9,g30) = -1.5708
    c: Tangent(g22,g30) = -1.5708
    c: Tangent(g22,g31) = -1.5708
    c: Tangent(g12,g31) = 1.5708
    c: Tangent(g8,g32) = 1.5708
    c: Tangent(g25,g32) = 1.5708
    c: Tangent(g10,g33) = 1.5708
    c: Tangent(g25,g33) = 1.5708
    c: Equal(g30,g32)
    c: Equal(g31,g33)
    c: DistanceY(g23,g23) = 2
    c: DistanceY(g22,g22) = 15
    c: DistanceY(g6,g9) = 48
    c: DistanceX(g24,g23) = 155
    c: Radius(g30) = 2
    c: Radius(g31) = 2
    c: Coincident(g34,g22)
    c: Coincident(g34,g23)
    c: Coincident(g35,g25)
    c: Coincident(g35,g24)
    c: Horizontal(g36)
    c: PointOnObject(g37,g13)
    c: DistanceY(g37,g13) = 14
    c: Vertical(g39)
    c: Vertical(g41)
    c: PointOnObject(g42,g13)
    c: Horizontal(g43)
    c: Parallel(g40,g12)
    c: PointOnObject(g44,g-2)
    c: PointOnObject(g44,g42)
    c: Tangent(g38,g45) = -1.5708
    c: Tangent(g36,g45) = 1.5708
    c: Tangent(g40,g46) = 1.5708
    c: Tangent(g36,g46) = 1.5708
    c: Tangent(g41,g47) = 1.5708
    c: Tangent(g40,g47) = 1.5708
    c: Tangent(g39,g48) = -1.5708
    c: Tangent(g38,g48) = -1.5708
    c: Tangent(g42,g49) = -1.5708
    c: Tangent(g41,g49) = 1.5708
    c: Tangent(g42,g50) = -1.5708
    c: Tangent(g39,g50) = -1.5708
    c: Coincident(g43,g39)
    c: Coincident(g43,g41)
    c: Equal(g15,g46)
    c: Equal(g46,g45)
    c: Symmetric(g36,g36,g37)
    c: Equal(g31,g47)
    c: Equal(g26,g49)
    c: Equal(g50,g29)
    c: Equal(g48,g32)
    c: PointOnObject(g41,g6)
    c: PointOnObject(g50,g5)
    c: DistanceY(g20,g44) = 14
    c: DistanceX(g41,g22) = 14
    c: PointOnObject(g51,g38)
    c: Perpendicular(g38,g51)
    c: Distance(g51) = 14
    c: Coincident(g51,g10)
FEATURE [Sketcher::SketchObject] Sketch084  label="Sketch_HollowPlug003"
  FullyConstrained = true
  MapMode = 5
  Placement = pos=(0,0,0) rot=(1,0,0;1.5708rad)
  Support = -> [XZ_Plane005]
  expr: Constraints[0] = <<params>>.xport_plug_diam - 2 * <<params>>.xport_plug_wall_thick
  expr: Constraints[1] = <<params>>.xport_offset_loc
  expr: Constraints[2] = <<params>>.xport_height_loc
  sketch-geometry (1):
    g0: Circle CenterX=43 CenterY=33.25 CenterZ=0 NormalX=0 NormalY=0 NormalZ=1 AngleXU=0 Radius=5.55
  constraints (3):
    c: Diameter(g0) = 11.1
    c: DistanceX(g-1,g0) = 43
    c: DistanceY(g-1,g0) = 33.25
FEATURE [Sketcher::SketchObject] Sketch085  label="Sketch_Shell_Top_CutPlug003"
  FullyConstrained = true
  MapMode = 5
  Placement = pos=(0,0,42) rot=(0,0,1;0rad)
  expr: Constraints[142] = <<params>>.xport_plug_plate_thick
  expr: Constraints[79] = <<params>>.plate_width
  expr: Constraints[136] = <<params>>.xport_offset_loc
  expr: Constraints[120] = <<params>>.shell_overhang_leng
  expr: Constraints[77] = <<params>>.back_vert_edge
  expr: Constraints[155] = <<params>>.shell_wall_thick + <<params>>.std_tol_interfere
  expr: Constraints[63] = <<params>>.std_rad
  expr: Constraints[143] = <<params>>.std_wall_thick
  expr: Constraints[42] = <<params>>.tail_width
  expr: Constraints[78] = <<params>>.wheel_well_clearance
  expr: Constraints[153] = <<params>>.xport_plug_diam / 2
  expr: Constraints[152] = <<params>>.xport_plug_diam / 2
  expr: Constraints[80] = <<params>>.std_rad
  expr: Constraints[117] = <<params>>.shell_overhang_leng
  expr: Constraints[76] = <<params>>.front_vert_edge
  expr: Constraints[130] = <<params>>.plate_length / 2 + <<params>>.std_wall_thick
  expr: Constraints[41] = <<params>>.tail_rad
  expr: Constraints[187] = <<params>>.xport_clip_size
  expr: Constraints[129] = <<params>>.std_wall_thick
  expr: Constraints[40] = <<params>>.plate_length
  expr: Constraints[189] = <<params>>.shell_overhang_leng
  expr: Constraints[65] = <<params>>.std_rad
  expr: Constraints[186] = <<params>>.xport_clip_size
  expr: Constraints[81] = <<params>>.std_rad
  expr: Constraints[88] = Spreadsheet.shell_overhang_leng
  expr: Constraints[116] = Spreadsheet.shell_overhang_leng
  expr: Constraints[36] = <<params>>.wheel_well_plate_width - 2 * Spreadsheet.shell_overhang_leng
  expr: Constraints[47] = <<params>>.front_diameter
  sketch-geometry (80):
    g0: LineSegment StartX=-43.5 StartY=17 StartZ=0 EndX=-43.5 EndY=-17 EndZ=0
    g1: LineSegment StartX=43.5 StartY=17 StartZ=0 EndX=43.5 EndY=-17 EndZ=0
    g2: LineSegment StartX=-43.5 StartY=0 StartZ=0 EndX=43.5 EndY=0 EndZ=0
    g3: LineSegment StartX=-50.5 StartY=-24 StartZ=0 EndX=50.5 EndY=-24 EndZ=0
    g4: LineSegment StartX=-50.5 StartY=24 StartZ=0 EndX=50.5 EndY=24 EndZ=0
    g5: LineSegment StartX=-50.5 StartY=-24 StartZ=0 EndX=-75.5 EndY=-24 EndZ=0
    g6: LineSegment StartX=50.5 StartY=-24 StartZ=0 EndX=75.5 EndY=-24 EndZ=0
    g7: ArcOfCircle CenterX=0 CenterY=52.6846 CenterZ=0 NormalX=0 NormalY=0 NormalZ=1 AngleXU=0 Radius=112.5 StartAngle=3.96017 EndAngle=5.4646
    g8: LineSegment StartX=-50.5 StartY=24 StartZ=0 EndX=-75.5 EndY=24 EndZ=0
    g9: LineSegment StartX=50.5 StartY=24 StartZ=0 EndX=75.5 EndY=24 EndZ=0
    g10: LineSegment StartX=-77.1162 StartY=42.1781 StartZ=0 EndX=-29.0404 EndY=108.13 EndZ=0
    g11: LineSegment StartX=-25 StartY=110.185 StartZ=0 EndX=25 EndY=110.185 EndZ=0
    g12: LineSegment StartX=29.0404 StartY=108.13 StartZ=0 EndX=77.1162 EndY=42.1781 EndZ=0
    g13: LineSegment StartX=0 StartY=0 StartZ=0 EndX=0 EndY=110.185 EndZ=0
    g14: ArcOfCircle CenterX=-25 CenterY=105.185 CenterZ=0 NormalX=0 NormalY=0 NormalZ=1 AngleXU=0 Radius=5 StartAngle=1.5708 EndAngle=2.5117
    g15: ArcOfCircle CenterX=25 CenterY=105.185 CenterZ=0 NormalX=0 NormalY=0 NormalZ=1 AngleXU=0 Radius=5 StartAngle=0.629894 EndAngle=1.5708
    g16: ArcOfCircle CenterX=-50.5 CenterY=17 CenterZ=0 NormalX=0 NormalY=0 NormalZ=1 AngleXU=0 Radius=7 StartAngle=0 EndAngle=1.5708
    g17: ArcOfCircle CenterX=-50.5 CenterY=-17 CenterZ=0 NormalX=0 NormalY=0 NormalZ=1 AngleXU=0 Radius=7 StartAngle=4.71239 EndAngle=6.28319
    g18: ArcOfCircle CenterX=50.5 CenterY=-17 CenterZ=0 NormalX=0 NormalY=0 NormalZ=1 AngleXU=0 Radius=7 StartAngle=3.14159 EndAngle=4.71239
    g19: ArcOfCircle CenterX=50.5 CenterY=17 CenterZ=0 NormalX=0 NormalY=0 NormalZ=1 AngleXU=0 Radius=7 StartAngle=1.5708 EndAngle=3.14159
    g20: GeomPoint X=0 Y=-59.8154 Z=0
    g21: Circle CenterX=0 CenterY=52.6846 CenterZ=0 NormalX=0 NormalY=0 NormalZ=1 AngleXU=0 Radius=112.5
    g22: LineSegment StartX=77.5 StartY=26 StartZ=0 EndX=77.5 EndY=41 EndZ=0
    g23: LineSegment StartX=77.5 StartY=-26 StartZ=0 EndX=77.5 EndY=-28 EndZ=0
    g24: LineSegment StartX=-77.5 StartY=-28 StartZ=0 EndX=-77.5 EndY=-26 EndZ=0
    g25: LineSegment StartX=-77.5 StartY=26 StartZ=0 EndX=-77.5 EndY=41 EndZ=0
    g26: ArcOfCircle CenterX=75.5 CenterY=-28 CenterZ=0 NormalX=0 NormalY=0 NormalZ=1 AngleXU=0 Radius=2 StartAngle=5.4646 EndAngle=6.28319
    g27: ArcOfCircle CenterX=75.5 CenterY=-26 CenterZ=0 NormalX=0 NormalY=0 NormalZ=1 AngleXU=0 Radius=2 StartAngle=0 EndAngle=1.5708
    g28: ArcOfCircle CenterX=-75.5 CenterY=-28 CenterZ=0 NormalX=0 NormalY=0 NormalZ=1 AngleXU=0 Radius=2 StartAngle=3.14159 EndAngle=3.96017
    g29: ArcOfCircle CenterX=-75.5 CenterY=-26 CenterZ=0 NormalX=0 NormalY=0 NormalZ=1 AngleXU=0 Radius=2 StartAngle=1.5708 EndAngle=3.14159
    g30: ArcOfCircle CenterX=75.5 CenterY=26 CenterZ=0 NormalX=0 NormalY=0 NormalZ=1 AngleXU=0 Radius=2 StartAngle=4.71239 EndAngle=6.28319
    g31: ArcOfCircle CenterX=75.5 CenterY=41 CenterZ=0 NormalX=0 NormalY=0 NormalZ=1 AngleXU=0 Radius=2 StartAngle=9e-16 EndAngle=0.629894
    g32: ArcOfCircle CenterX=-75.5 CenterY=26 CenterZ=0 NormalX=0 NormalY=0 NormalZ=1 AngleXU=0 Radius=2 StartAngle=3.14159 EndAngle=4.71239
    g33: ArcOfCircle CenterX=-75.5 CenterY=41 CenterZ=0 NormalX=0 NormalY=0 NormalZ=1 AngleXU=0 Radius=2 StartAngle=2.5117 EndAngle=3.14159
    g34: LineSegment StartX=77.5 StartY=26 StartZ=0 EndX=77.5 EndY=-26 EndZ=0
    g35: LineSegment StartX=-77.5 StartY=26 StartZ=0 EndX=-77.5 EndY=-26 EndZ=0
    g36: LineSegment StartX=-17.8805 StartY=96.1846 StartZ=0 EndX=17.8805 EndY=96.1846 EndZ=0
    g37: GeomPoint X=0 Y=96.1846 Z=0
    g38: LineSegment StartX=-21.921 StartY=94.1299 StartZ=0 EndX=-63.1162 EndY=37.617 EndZ=0
    g39: LineSegment StartX=-63.5 StartY=36.4389 StartZ=0 EndX=-63.5 EndY=-21.6794 EndZ=0
    g40: LineSegment StartX=21.921 StartY=94.1299 StartZ=0 EndX=63.1162 EndY=37.617 EndZ=0
    g41: LineSegment StartX=63.5 StartY=36.4389 StartZ=0 EndX=63.5 EndY=-21.6794 EndZ=0
    g42: ArcOfCircle CenterX=0 CenterY=52.6846 CenterZ=0 NormalX=0 NormalY=0 NormalZ=1 AngleXU=0 Radius=98.5 StartAngle=4.02139 EndAngle=5.40339
    g43: LineSegment StartX=-63.5 StartY=36.4389 StartZ=0 EndX=63.5 EndY=36.4389 EndZ=0
    g44: GeomPoint X=0 Y=-45.8154 Z=0
    g45: ArcOfCircle CenterX=-17.8805 CenterY=91.1846 CenterZ=0 NormalX=0 NormalY=0 NormalZ=1 AngleXU=0 Radius=5 StartAngle=1.5708 EndAngle=2.5117
    g46: ArcOfCircle CenterX=17.8805 CenterY=91.1846 CenterZ=0 NormalX=0 NormalY=0 NormalZ=1 AngleXU=0 Radius=5 StartAngle=0.629894 EndAngle=1.5708
    g47: ArcOfCircle CenterX=61.5 CenterY=36.4389 CenterZ=0 NormalX=0 NormalY=0 NormalZ=1 AngleXU=0 Radius=2 StartAngle=0 EndAngle=0.629894
    g48: ArcOfCircle CenterX=-61.5 CenterY=36.4389 CenterZ=0 NormalX=0 NormalY=0 NormalZ=1 AngleXU=0 Radius=2 StartAngle=2.5117 EndAngle=3.14159
    g49: ArcOfCircle CenterX=61.5 CenterY=-21.6794 CenterZ=0 NormalX=0 NormalY=0 NormalZ=1 AngleXU=0 Radius=2 StartAngle=5.40339 EndAngle=6.28319
    g50: ArcOfCircle CenterX=-61.5 CenterY=-21.6794 CenterZ=0 NormalX=0 NormalY=0 NormalZ=1 AngleXU=0 Radius=2 StartAngle=3.14159 EndAngle=4.02139
    g51: LineSegment StartX=-29.0404 StartY=108.13 StartZ=0 EndX=-17.7272 EndY=99.883 EndZ=0
    g52: LineSegment StartX=-2 StartY=2 StartZ=0 EndX=-2 EndY=-87 EndZ=0
    g53: LineSegment StartX=-2 StartY=-87 StartZ=0 EndX=63.5 EndY=-87 EndZ=0
    g54: LineSegment StartX=63.5 StartY=-87 StartZ=0 EndX=63.5 EndY=-27.7653 EndZ=0
    g55: LineSegment StartX=63.5 StartY=2 StartZ=0 EndX=-2 EndY=2 EndZ=0
    g56: LineSegment StartX=0 StartY=-58.5771 StartZ=0 EndX=63.5 EndY=-27.7653 EndZ=0
    g57: LineSegment StartX=63.5 StartY=-22.6148 StartZ=0 EndX=63.5 EndY=-27.7653 EndZ=0
    g58: GeomPoint X=43 Y=-35.934 Z=0
    g59: LineSegment StartX=0 StartY=52.6846 StartZ=0 EndX=43 EndY=-35.934 EndZ=0
    g60: LineSegment StartX=43 StartY=-35.934 StartZ=0 EndX=43.6985 EndY=-37.3735 EndZ=0
    g61: LineSegment StartX=0 StartY=-58.5771 StartZ=0 EndX=-1.81e-14 EndY=-45.8154 EndZ=0
    g62: LineSegment StartX=63.5 StartY=2 StartZ=0 EndX=63.5 EndY=-22.6148 EndZ=0
    g63: LineSegment StartX=36.65 StartY=-38.7431 StartZ=0 EndX=36.65 EndY=-36.5431 EndZ=0
    g64: LineSegment StartX=49.35 StartY=-30.3611 StartZ=0 EndX=49.35 EndY=-32.5611 EndZ=0
    g65: LineSegment StartX=36.65 StartY=-36.5431 StartZ=0 EndX=35.9672 EndY=-35.8603 EndZ=0
    g66: LineSegment StartX=35.9672 StartY=-35.2946 StartZ=0 EndX=36.65 EndY=-34.6118 EndZ=0
    g67: LineSegment StartX=49.35 StartY=-30.3611 StartZ=0 EndX=50.0328 EndY=-29.6783 EndZ=0
    g68: LineSegment StartX=50.0328 StartY=-29.1126 StartZ=0 EndX=49.35 EndY=-28.4297 EndZ=0
    g69: LineSegment StartX=49.35 StartY=-28.4297 StartZ=0 EndX=36.65 EndY=-34.6118 EndZ=0
    g70: ArcOfCircle CenterX=36.25 CenterY=-35.5775 CenterZ=0 NormalX=0 NormalY=0 NormalZ=1 AngleXU=0 Radius=0.4 StartAngle=2.35619 EndAngle=3.92699
    g71: ArcOfCircle CenterX=49.75 CenterY=-29.3954 CenterZ=0 NormalX=0 NormalY=0 NormalZ=1 AngleXU=0 Radius=0.4 StartAngle=5.49779 EndAngle=7.06858
    g72: LineSegment StartX=36.65 StartY=-36.5431 StartZ=0 EndX=36.65 EndY=-34.6118 EndZ=0
    g73: GeomPoint X=35.85 Y=-35.5775 Z=0
    g74: GeomPoint X=50.15 Y=-29.3954 Z=0
    g75: LineSegment StartX=49.35 StartY=-30.3611 StartZ=0 EndX=49.35 EndY=-28.4297 EndZ=0
    g76: LineSegment StartX=50.15 StartY=-29.3954 StartZ=0 EndX=49.35 EndY=-29.3954 EndZ=0
    g77: LineSegment StartX=36.65 StartY=-35.5775 StartZ=0 EndX=35.85 EndY=-35.5775 EndZ=0
    g78: ArcOfCircle CenterX=0 CenterY=52.6846 CenterZ=0 NormalX=0 NormalY=0 NormalZ=1 AngleXU=0 Radius=98.5 StartAngle=4.71239 EndAngle=5.09364
    g79: ArcOfCircle CenterX=0 CenterY=52.6846 CenterZ=0 NormalX=0 NormalY=0 NormalZ=1 AngleXU=0 Radius=98.5 StartAngle=5.23716 EndAngle=5.41298
  constraints (201):
    c: Vertical(g0)
    c: Vertical(g1)
    c: Horizontal(g2)
    c: Symmetric(g2,g2,g-1)
    c: Horizontal(g3)
    c: Horizontal(g5)
    c: Horizontal(g6)
    c: PointOnObject(g7,g-2)
    c: Horizontal(g8)
    c: Horizontal(g9)
    c: Horizontal(g11)
    c: Coincident(g13,g-1)
    c: PointOnObject(g13,g-2)
    c: Tangent(g10,g14) = 1.5708
    c: Tangent(g11,g14) = 1.5708
    c: Tangent(g11,g15) = 1.5708
    c: Tangent(g12,g15) = 1.5708
    c: Tangent(g8,g16) = -1.5708
    c: Tangent(g0,g16) = 1.5708
    c: Tangent(g5,g17) = 1.5708
    c: Tangent(g0,g17) = 1.5708
    c: Tangent(g1,g18) = -1.5708
    c: Tangent(g6,g18) = -1.5708
    c: Tangent(g1,g19) = -1.5708
    c: Tangent(g9,g19) = 1.5708
    c: Equal(g15,g14)
    c: Symmetric(g11,g11,g13)
    c: Equal(g18,g19)
    c: Equal(g19,g16)
    c: Equal(g16,g17)
    c: PointOnObject(g20,g-2)
    c: PointOnObject(g20,g7)
    c: Coincident(g4,g8)
    c: Coincident(g4,g9)
    c: Coincident(g3,g6)
    c: Coincident(g3,g5)
    c: DistanceX(g2,g2) = 87
    c: Symmetric(g0,g0,g2)
    c: Symmetric(g1,g1,g2)
    c: Radius(g19) = 7
    c: DistanceY(g20,g11) = 170
    c: Radius(g15) = 5
    c: DistanceX(g11,g11) = 50
    c: Equal(g9,g8)
    c: Equal(g9,g6)
    c: Coincident(g21,g7)
    c: PointOnObject(g20,g21)
    c: Diameter(g21) = 225
    c: Vertical(g22)
    c: Vertical(g23)
    c: Vertical(g24)
    c: Vertical(g25)
    c: Equal(g5,g8)
    c: Equal(g10,g12)
    c: Tangent(g7,g26) = -1.5708
    c: Tangent(g23,g26) = 1.5708
    c: Tangent(g23,g27) = 1.5708
    c: Tangent(g6,g27) = 1.5708
    c: Tangent(g7,g28) = -1.5708
    c: Tangent(g24,g28) = 1.5708
    c: Tangent(g24,g29) = 1.5708
    c: Tangent(g5,g29) = -1.5708
    c: Equal(g29,g27)
    c: Radius(g27) = 2
    c: Equal(g26,g28)
    c: Radius(g26) = 2
    c: Tangent(g9,g30) = -1.5708
    c: Tangent(g22,g30) = -1.5708
    c: Tangent(g22,g31) = -1.5708
    c: Tangent(g12,g31) = 1.5708
    c: Tangent(g8,g32) = 1.5708
    c: Tangent(g25,g32) = 1.5708
    c: Tangent(g10,g33) = 1.5708
    c: Tangent(g25,g33) = 1.5708
    c: Equal(g30,g32)
    c: Equal(g31,g33)
    c: DistanceY(g23,g23) = 2
    c: DistanceY(g22,g22) = 15
    c: DistanceY(g6,g9) = 48
    c: DistanceX(g24,g23) = 155
    c: Radius(g30) = 2
    c: Radius(g31) = 2
    c: Coincident(g34,g22)
    c: Coincident(g34,g23)
    c: Coincident(g35,g25)
    c: Coincident(g35,g24)
    c: Horizontal(g36)
    c: PointOnObject(g37,g13)
    c: DistanceY(g37,g13) = 14
    c: Vertical(g39)
    c: Vertical(g41)
    c: Horizontal(g43)
    c: Parallel(g40,g12)
    c: PointOnObject(g44,g-2)
    c: PointOnObject(g44,g42)
    c: Tangent(g38,g45) = -1.5708
    c: Tangent(g36,g45) = 1.5708
    c: Tangent(g40,g46) = 1.5708
    c: Tangent(g36,g46) = 1.5708
    c: Tangent(g41,g47) = 1.5708
    c: Tangent(g40,g47) = 1.5708
    c: Tangent(g39,g48) = -1.5708
    c: Tangent(g38,g48) = -1.5708
    c: Tangent(g42,g49) = -1.5708
    c: Tangent(g41,g49) = 1.5708
    c: Tangent(g42,g50) = -1.5708
    c: Tangent(g39,g50) = -1.5708
    c: Coincident(g43,g39)
    c: Coincident(g43,g41)
    c: Equal(g15,g46)
    c: Equal(g46,g45)
    c: Symmetric(g36,g36,g37)
    c: Equal(g31,g47)
    c: Equal(g26,g49)
    c: Equal(g50,g29)
    c: Equal(g48,g32)
    c: DistanceY(g20,g44) = 14
    c: DistanceX(g41,g22) = 14
    c: PointOnObject(g51,g38)
    c: Perpendicular(g38,g51)
    c: Distance(g51) = 14
    c: Coincident(g51,g10)
    c: Vertical(g52)
    c: Coincident(g53,g52)
    c: Horizontal(g53)
    c: Coincident(g54,g53)
    c: Vertical(g54)
    c: Coincident(g55,g52)
    c: Horizontal(g55)
    c: DistanceY(g-1,g52) = 2
    c: DistanceY(g52,g-1) = 87
    c: Coincident(g54,g56)
    c: Coincident(g57,g54)
    c: Vertical(g57)
    c: PointOnObject(g56,g-2)
    c: PointOnObject(g58,g42)
    c: DistanceX(g-1,g58) = 43
    c: Coincident(g59,g58)
    c: Coincident(g60,g58)
    c: PointOnObject(g60,g56)
    c: Parallel(g60,g59)
    c: Perpendicular(g56,g60)
    c: Distance(g60) = 1.6
    c: DistanceX(g52,g-1) = 2
    c: Coincident(g61,g56)
    c: PointOnObject(g61,g-2)
    c: Vertical(g62)
    c: Coincident(g62,g55)
    c: PointOnObject(g55,g41)
    c: Vertical(g63)
    c: Vertical(g64)
    c: Equal(g64,g63)
    c: DistanceX(g63,g58) = 6.35
    c: DistanceX(g58,g64) = 6.35
    c: PointOnObject(g61,g42)
    c: DistanceY(g64,g64) = 2.2
    c: Coincident(g65,g63)
    c: Coincident(g67,g64)
    c: Coincident(g69,g68)
    c: Coincident(g69,g66)
    c: Tangent(g65,g70) = 1.5708
    c: Tangent(g66,g70) = 1.5708
    c: Tangent(g67,g71) = -1.5708
    c: Tangent(g68,g71) = -1.5708
    c: Coincident(g72,g63)
    c: Coincident(g72,g66)
    c: PointOnObject(g73,g70)
    c: PointOnObject(g74,g71)
    c: Coincident(g75,g64)
    c: Coincident(g75,g68)
    c: Vertical(g75)
    c: Coincident(g76,g74)
    c: PointOnObject(g76,g75)
    c: Horizontal(g76)
    c: PointOnObject(g71,g76)
    c: Equal(g67,g68)
    c: Equal(g68,g66)
    c: Equal(g65,g66)
    c: Equal(g71,g70)
    c: Vertical(g72)
    c: PointOnObject(g77,g72)
    c: Coincident(g77,g73)
    c: Horizontal(g77)
    c: PointOnObject(g70,g77)
    c: Angle(g65,g66) = 1.5708
    c: Angle(g68,g67) = 1.5708
    c: DistanceX(g76,g74) = 0.8
    c: Diameter(g71) = 0.8
    c: Coincident(g42,g7)
    c: DistanceX(g25,g39) = 14
    c: Coincident(g59,g7)
    c: Coincident(g57,g62)
    c: PointOnObject(g63,g42)
    c: PointOnObject(g64,g42)
    c: PointOnObject(g62,g42)
    c: Coincident(g78,g7)
    c: Coincident(g79,g78)
    c: Coincident(g79,g62)
    c: Coincident(g78,g61)
    c: PointOnObject(g78,g63)
    c: PointOnObject(g79,g64)
FEATURE [Sketcher::SketchObject] Sketch088  label="Sketch_Shell_Vert_CutPlug003"
  FullyConstrained = true
  MapMode = 5
  Placement = pos=(0,0,10) rot=(0,0,1;0rad)
  expr: Constraints[110] = <<params>>.xport_plug_plate_thick
  expr: Constraints[77] = <<params>>.back_vert_edge
  expr: Constraints[137] = <<params>>.shell_wall_thick + <<params>>.std_tol_clear
  expr: Constraints[134] = <<params>>.xport_plug_diam / 2
  expr: Constraints[47] = <<params>>.front_diameter
  expr: Constraints[170] = <<params>>.xport_clip_size
  expr: Constraints[63] = <<params>>.std_rad
  expr: Constraints[103] = <<params>>.xport_offset_loc
  expr: Constraints[101] = <<params>>.plate_length / 2 + <<params>>.std_wall_thick
  expr: Constraints[80] = <<params>>.std_rad
  expr: Constraints[36] = <<params>>.wheel_well_plate_width
  expr: Constraints[40] = <<params>>.plate_length
  expr: Constraints[65] = <<params>>.std_rad
  expr: Constraints[78] = <<params>>.wheel_well_clearance
  expr: Constraints[42] = <<params>>.tail_width
  expr: Constraints[135] = <<params>>.xport_plug_diam / 2
  expr: Constraints[79] = <<params>>.plate_width
  expr: Constraints[76] = <<params>>.front_vert_edge
  expr: Constraints[118] = <<params>>.std_wall_thick
  expr: Constraints[100] = <<params>>.std_wall_thick
  expr: Constraints[81] = <<params>>.std_rad
  expr: Constraints[41] = <<params>>.tail_rad
  expr: Constraints[168] = <<params>>.xport_clip_size
  sketch-geometry (68):
    g0: LineSegment StartX=-57.5 StartY=17 StartZ=0 EndX=-57.5 EndY=-17 EndZ=0
    g1: LineSegment StartX=57.5 StartY=17 StartZ=0 EndX=57.5 EndY=-17 EndZ=0
    g2: LineSegment StartX=-57.5 StartY=0 StartZ=0 EndX=57.5 EndY=0 EndZ=0
    g3: LineSegment StartX=-64.5 StartY=-24 StartZ=0 EndX=64.5 EndY=-24 EndZ=0
    g4: LineSegment StartX=-64.5 StartY=24 StartZ=0 EndX=64.5 EndY=24 EndZ=0
    g5: LineSegment StartX=-64.5 StartY=-24 StartZ=0 EndX=-75.5 EndY=-24 EndZ=0
    g6: LineSegment StartX=64.5 StartY=-24 StartZ=0 EndX=75.5 EndY=-24 EndZ=0
    g7: ArcOfCircle CenterX=0 CenterY=52.6846 CenterZ=0 NormalX=0 NormalY=0 NormalZ=1 AngleXU=0 Radius=112.5 StartAngle=3.96017 EndAngle=5.4646
    g8: LineSegment StartX=-64.5 StartY=24 StartZ=0 EndX=-75.5 EndY=24 EndZ=0
    g9: LineSegment StartX=64.5 StartY=24 StartZ=0 EndX=75.5 EndY=24 EndZ=0
    g10: LineSegment StartX=-77.1162 StartY=42.1781 StartZ=0 EndX=-29.0404 EndY=108.13 EndZ=0
    g11: LineSegment StartX=-25 StartY=110.185 StartZ=0 EndX=25 EndY=110.185 EndZ=0
    g12: LineSegment StartX=29.0404 StartY=108.13 StartZ=0 EndX=77.1162 EndY=42.1781 EndZ=0
    g13: LineSegment StartX=0 StartY=0 StartZ=0 EndX=0 EndY=110.185 EndZ=0
    g14: ArcOfCircle CenterX=-25 CenterY=105.185 CenterZ=0 NormalX=0 NormalY=0 NormalZ=1 AngleXU=0 Radius=5 StartAngle=1.5708 EndAngle=2.5117
    g15: ArcOfCircle CenterX=25 CenterY=105.185 CenterZ=0 NormalX=0 NormalY=0 NormalZ=1 AngleXU=0 Radius=5 StartAngle=0.629894 EndAngle=1.5708
    g16: ArcOfCircle CenterX=-64.5 CenterY=17 CenterZ=0 NormalX=0 NormalY=0 NormalZ=1 AngleXU=0 Radius=7 StartAngle=0 EndAngle=1.5708
    g17: ArcOfCircle CenterX=-64.5 CenterY=-17 CenterZ=0 NormalX=0 NormalY=0 NormalZ=1 AngleXU=0 Radius=7 StartAngle=4.71239 EndAngle=6.28319
    g18: ArcOfCircle CenterX=64.5 CenterY=-17 CenterZ=0 NormalX=0 NormalY=0 NormalZ=1 AngleXU=0 Radius=7 StartAngle=3.14159 EndAngle=4.71239
    g19: ArcOfCircle CenterX=64.5 CenterY=17 CenterZ=0 NormalX=0 NormalY=0 NormalZ=1 AngleXU=0 Radius=7 StartAngle=1.5708 EndAngle=3.14159
    g20: GeomPoint X=0 Y=-59.8154 Z=0
    g21: Circle CenterX=0 CenterY=52.6846 CenterZ=0 NormalX=0 NormalY=0 NormalZ=1 AngleXU=0 Radius=112.5
    g22: LineSegment StartX=77.5 StartY=26 StartZ=0 EndX=77.5 EndY=41 EndZ=0
    g23: LineSegment StartX=77.5 StartY=-26 StartZ=0 EndX=77.5 EndY=-28 EndZ=0
    g24: LineSegment StartX=-77.5 StartY=-28 StartZ=0 EndX=-77.5 EndY=-26 EndZ=0
    g25: LineSegment StartX=-77.5 StartY=26 StartZ=0 EndX=-77.5 EndY=41 EndZ=0
    g26: ArcOfCircle CenterX=75.5 CenterY=-28 CenterZ=0 NormalX=0 NormalY=0 NormalZ=1 AngleXU=0 Radius=2 StartAngle=5.4646 EndAngle=6.28319
    g27: ArcOfCircle CenterX=75.5 CenterY=-26 CenterZ=0 NormalX=0 NormalY=0 NormalZ=1 AngleXU=0 Radius=2 StartAngle=0 EndAngle=1.5708
    g28: ArcOfCircle CenterX=-75.5 CenterY=-28 CenterZ=0 NormalX=0 NormalY=0 NormalZ=1 AngleXU=0 Radius=2 StartAngle=3.14159 EndAngle=3.96017
    g29: ArcOfCircle CenterX=-75.5 CenterY=-26 CenterZ=0 NormalX=0 NormalY=0 NormalZ=1 AngleXU=0 Radius=2 StartAngle=1.5708 EndAngle=3.14159
    g30: ArcOfCircle CenterX=75.5 CenterY=26 CenterZ=0 NormalX=0 NormalY=0 NormalZ=1 AngleXU=0 Radius=2 StartAngle=4.71239 EndAngle=6.28319
    g31: ArcOfCircle CenterX=75.5 CenterY=41 CenterZ=0 NormalX=0 NormalY=0 NormalZ=1 AngleXU=0 Radius=2 StartAngle=4e-16 EndAngle=0.629894
    g32: ArcOfCircle CenterX=-75.5 CenterY=26 CenterZ=0 NormalX=0 NormalY=0 NormalZ=1 AngleXU=0 Radius=2 StartAngle=3.14159 EndAngle=4.71239
    g33: ArcOfCircle CenterX=-75.5 CenterY=41 CenterZ=0 NormalX=0 NormalY=0 NormalZ=1 AngleXU=0 Radius=2 StartAngle=2.5117 EndAngle=3.14159
    g34: LineSegment StartX=77.5 StartY=26 StartZ=0 EndX=77.5 EndY=-26 EndZ=0
    g35: LineSegment StartX=-77.5 StartY=26 StartZ=0 EndX=-77.5 EndY=-26 EndZ=0
    g36: LineSegment StartX=77.5 StartY=41 StartZ=0 EndX=77.5 EndY=-28 EndZ=0
    g37: LineSegment StartX=-77.5 StartY=41 StartZ=0 EndX=-77.5 EndY=-28 EndZ=0
    g38: ArcOfCircle CenterX=0 CenterY=52.6846 CenterZ=0 NormalX=0 NormalY=0 NormalZ=1 AngleXU=0 Radius=112.5 StartAngle=4.71239 EndAngle=5.4646
    g39: LineSegment StartX=-2 StartY=2 StartZ=0 EndX=-2 EndY=-87 EndZ=0
    g40: LineSegment StartX=76.8665 StartY=-38.9967 StartZ=0 EndX=76.8665 EndY=-87 EndZ=0
    g41: LineSegment StartX=-2 StartY=-87 StartZ=0 EndX=76.8665 EndY=-87 EndZ=0
    g42: LineSegment StartX=-2 StartY=2 StartZ=0 EndX=77.5 EndY=2 EndZ=0
    g43: LineSegment StartX=0 StartY=-70.7909 StartZ=0 EndX=76.8665 EndY=-38.9967 EndZ=0
    g44: GeomPoint X=43 Y=-51.2734 Z=0
    g45: LineSegment StartX=0 StartY=52.6846 StartZ=0 EndX=43 EndY=-51.2734 EndZ=0
    g46: LineSegment StartX=43.6116 StartY=-52.7519 StartZ=0 EndX=43 EndY=-51.2734 EndZ=0
    g47: LineSegment StartX=76.8665 StartY=-38.9967 StartZ=0 EndX=76.8665 EndY=-29.4604 EndZ=0
    g48: LineSegment StartX=-2.07e-14 StartY=-59.8154 StartZ=0 EndX=0 EndY=-70.7909 EndZ=0
    g49: LineSegment StartX=0 StartY=-70.7909 StartZ=0 EndX=-2.07e-14 EndY=-59.8154 EndZ=0
    g50: LineSegment StartX=77.5 StartY=2 StartZ=0 EndX=77.5 EndY=-28.863 EndZ=0
    g51: ArcOfCircle CenterX=0 CenterY=52.6846 CenterZ=0 NormalX=0 NormalY=0 NormalZ=1 AngleXU=0 Radius=112.5 StartAngle=4.71239 EndAngle=5.04422
    g52: ArcOfCircle CenterX=0 CenterY=52.6846 CenterZ=0 NormalX=0 NormalY=0 NormalZ=1 AngleXU=0 Radius=112.5 StartAngle=5.1665 EndAngle=5.47234
    g53: LineSegment StartX=36.65 StartY=-53.6781 StartZ=0 EndX=36.65 EndY=-51.3781 EndZ=0
    g54: LineSegment StartX=49.35 StartY=-48.4135 StartZ=0 EndX=49.35 EndY=-46.1135 EndZ=0
    g55: LineSegment StartX=36.65 StartY=-51.3781 StartZ=0 EndX=35.9672 EndY=-50.6953 EndZ=0
    g56: LineSegment StartX=35.9672 StartY=-50.1296 StartZ=0 EndX=36.65 EndY=-49.4468 EndZ=0
    g57: ArcOfCircle CenterX=36.25 CenterY=-50.4125 CenterZ=0 NormalX=0 NormalY=0 NormalZ=1 AngleXU=0 Radius=0.4 StartAngle=2.35619 EndAngle=3.92699
    g58: LineSegment StartX=49.35 StartY=-46.1135 StartZ=0 EndX=50.0328 EndY=-45.4307 EndZ=0
    g59: LineSegment StartX=50.0328 StartY=-44.865 StartZ=0 EndX=49.35 EndY=-44.1822 EndZ=0
    g60: ArcOfCircle CenterX=49.75 CenterY=-45.1479 CenterZ=0 NormalX=0 NormalY=0 NormalZ=1 AngleXU=0 Radius=0.4 StartAngle=5.49779 EndAngle=7.06858
    g61: LineSegment StartX=36.65 StartY=-51.3781 StartZ=0 EndX=36.65 EndY=-49.4468 EndZ=0
    g62: LineSegment StartX=49.35 StartY=-46.1135 StartZ=0 EndX=49.35 EndY=-44.1822 EndZ=0
    g63: LineSegment StartX=36.65 StartY=-49.4468 StartZ=0 EndX=49.35 EndY=-44.1822 EndZ=0
    g64: GeomPoint X=50.15 Y=-45.1479 Z=0
    g65: GeomPoint X=35.85 Y=-50.4125 Z=0
    g66: LineSegment StartX=35.85 StartY=-50.4125 StartZ=0 EndX=36.65 EndY=-50.4125 EndZ=0
    g67: LineSegment StartX=50.15 StartY=-45.1479 StartZ=0 EndX=49.35 EndY=-45.1479 EndZ=0
  constraints (171):
    c: Vertical(g0)
    c: Vertical(g1)
    c: Horizontal(g2)
    c: Symmetric(g2,g2,g-1)
    c: Horizontal(g3)
    c: Horizontal(g5)
    c: Horizontal(g6)
    c: PointOnObject(g7,g-2)
    c: Horizontal(g8)
    c: Horizontal(g9)
    c: Horizontal(g11)
    c: Coincident(g13,g-1)
    c: PointOnObject(g13,g-2)
    c: Tangent(g10,g14) = 1.5708
    c: Tangent(g11,g14) = 1.5708
    c: Tangent(g11,g15) = 1.5708
    c: Tangent(g12,g15) = 1.5708
    c: Tangent(g8,g16) = -1.5708
    c: Tangent(g0,g16) = 1.5708
    c: Tangent(g5,g17) = 1.5708
    c: Tangent(g0,g17) = 1.5708
    c: Tangent(g1,g18) = -1.5708
    c: Tangent(g6,g18) = -1.5708
    c: Tangent(g1,g19) = -1.5708
    c: Tangent(g9,g19) = 1.5708
    c: Equal(g15,g14)
    c: Symmetric(g11,g11,g13)
    c: Equal(g18,g19)
    c: Equal(g19,g16)
    c: Equal(g16,g17)
    c: PointOnObject(g20,g-2)
    c: PointOnObject(g20,g7)
    c: Coincident(g4,g8)
    c: Coincident(g4,g9)
    c: Coincident(g3,g6)
    c: Coincident(g3,g5)
    c: DistanceX(g2,g2) = 115
    c: Symmetric(g0,g0,g2)
    c: Symmetric(g1,g1,g2)
    c: Radius(g19) = 7
    c: DistanceY(g20,g11) = 170
    c: Radius(g15) = 5
    c: DistanceX(g11,g11) = 50
    c: Equal(g9,g8)
    c: Equal(g9,g6)
    c: Coincident(g21,g7)
    c: PointOnObject(g20,g21)
    c: Diameter(g21) = 225
    c: Vertical(g22)
    c: Vertical(g23)
    c: Vertical(g24)
    c: Vertical(g25)
    c: Equal(g5,g8)
    c: Equal(g10,g12)
    c: Tangent(g7,g26) = -1.5708
    c: Tangent(g23,g26) = 1.5708
    c: Tangent(g23,g27) = 1.5708
    c: Tangent(g6,g27) = 1.5708
    c: Tangent(g7,g28) = -1.5708
    c: Tangent(g24,g28) = 1.5708
    c: Tangent(g24,g29) = 1.5708
    c: Tangent(g5,g29) = -1.5708
    c: Equal(g29,g27)
    c: Radius(g27) = 2
    c: Equal(g26,g28)
    c: Radius(g26) = 2
    c: Tangent(g9,g30) = -1.5708
    c: Tangent(g22,g30) = -1.5708
    c: Tangent(g22,g31) = -1.5708
    c: Tangent(g12,g31) = 1.5708
    c: Tangent(g8,g32) = 1.5708
    c: Tangent(g25,g32) = 1.5708
    c: Tangent(g10,g33) = 1.5708
    c: Tangent(g25,g33) = 1.5708
    c: Equal(g30,g32)
    c: Equal(g31,g33)
    c: DistanceY(g23,g23) = 2
    c: DistanceY(g22,g22) = 15
    c: DistanceY(g6,g9) = 48
    c: DistanceX(g24,g23) = 155
    c: Radius(g30) = 2
    c: Radius(g31) = 2
    c: Coincident(g34,g22)
    c: Coincident(g34,g23)
    c: Coincident(g35,g25)
    c: Coincident(g35,g24)
    c: Coincident(g37,g28)
    c: Coincident(g37,g33)
    c: Coincident(g36,g31)
    c: Coincident(g36,g26)
    c: Coincident(g38,g7)
    c: PointOnObject(g38,g-2)
    c: Coincident(g38,g7)
    c: Vertical(g39)
    c: Vertical(g40)
    c: Coincident(g41,g39)
    c: Coincident(g41,g40)
    c: Horizontal(g41)
    c: Coincident(g42,g39)
    c: Horizontal(g42)
    c: DistanceY(g-1,g39) = 2
    c: DistanceY(g39,g-1) = 87
    c: PointOnObject(g44,g38)
    c: DistanceX(g-1,g44) = 43
    c: Coincident(g45,g44)
    c: Coincident(g45,g38)
    c: Coincident(g46,g44)
    c: PointOnObject(g46,g43)
    c: Parallel(g45,g46)
    c: Perpendicular(g46,g43)
    c: Distance(g46) = 1.6
    c: PointOnObject(g43,g-2)
    c: Coincident(g40,g43)
    c: Coincident(g47,g40)
    c: Coincident(g47,g38)
    c: Vertical(g47)
    c: Coincident(g48,g38)
    c: Coincident(g48,g43)
    c: DistanceX(g39,g43) = 2
    c: Coincident(g49,g43)
    c: PointOnObject(g49,g-2)
    c: PointOnObject(g42,g34)
    c: PointOnObject(g50,g34)
    c: Coincident(g50,g42)
    c: PointOnObject(g51,g13)
    c: Coincident(g51,g49)
    c: Coincident(g52,g51)
    c: Coincident(g52,g50)
    c: Coincident(g53,g51)
    c: Vertical(g53)
    c: Coincident(g54,g52)
    c: Vertical(g54)
    c: Equal(g51,g7)
    c: Equal(g52,g21)
    c: DistanceX(g51,g44) = 6.35
    c: DistanceX(g44,g52) = 6.35
    c: Equal(g54,g53)
    c: DistanceY(g54,g54) = 2.3
    c: PointOnObject(g49,g7)
    c: Coincident(g55,g53)
    c: Tangent(g55,g57) = 1.5708
    c: Tangent(g56,g57) = 1.5708
    c: Coincident(g58,g54)
    c: Tangent(g58,g60) = -1.5708
    c: Tangent(g59,g60) = -1.5708
    c: Coincident(g61,g53)
    c: Coincident(g61,g56)
    c: Vertical(g61)
    c: Coincident(g62,g54)
    c: Coincident(g62,g59)
    c: Vertical(g62)
    c: Equal(g58,g59)
    c: Equal(g55,g56)
    c: Equal(g60,g57)
    c: Coincident(g63,g56)
    c: Coincident(g63,g59)
    c: Angle(g59,g58) = 1.5708
    c: Angle(g55,g56) = 1.5708
    c: PointOnObject(g64,g60)
    c: PointOnObject(g65,g57)
    c: Coincident(g66,g65)
    c: PointOnObject(g66,g61)
    c: Horizontal(g66)
    c: PointOnObject(g57,g66)
    c: Coincident(g67,g64)
    c: PointOnObject(g67,g62)
    c: Horizontal(g67)
    c: PointOnObject(g60,g67)
    c: DistanceX(g67,g64) = 0.8
    c: Equal(g67,g66)
    c: Diameter(g60) = 0.8
FEATURE [Sketcher::SketchObject] Sketch089  label="Sketch_ClipsToTrim004"
  FullyConstrained = true
  MapMode = 5
  Placement = pos=(0,0,0) rot=(1,0,0;1.5708rad)
  Support = -> [XZ_Plane005]
  expr: Constraints[15] = <<params>>.std_wall_thick
  expr: Constraints[2] = <<params>>.xport_height_loc
  expr: Constraints[1] = <<params>>.xport_offset_loc
  expr: Constraints[0] = <<params>>.xport_plug_diam + 4 * <<params>>.xport_clip_size
  expr: Constraints[34] = <<params>>.std_wall_thick
  sketch-geometry (11):
    g0: Circle CenterX=43 CenterY=33.25 CenterZ=0 NormalX=0 NormalY=0 NormalZ=1 AngleXU=0 Radius=7.95
    g1: LineSegment StartX=35.1131 StartY=34.25 StartZ=0 EndX=50.8869 EndY=34.25 EndZ=0
    g2: LineSegment StartX=35.1131 StartY=32.25 StartZ=0 EndX=50.8869 EndY=32.25 EndZ=0
    g3: ArcOfCircle CenterX=43 CenterY=33.25 CenterZ=0 NormalX=0 NormalY=0 NormalZ=1 AngleXU=0 Radius=7.95 StartAngle=3.01547 EndAngle=3.26771
    g4: ArcOfCircle CenterX=43 CenterY=33.25 CenterZ=0 NormalX=0 NormalY=0 NormalZ=1 AngleXU=0 Radius=7.95 StartAngle=6.15707 EndAngle=6.40931
    g5: LineSegment StartX=35.1131 StartY=32.25 StartZ=0 EndX=42 EndY=32.25 EndZ=0
    g6: LineSegment StartX=44 StartY=32.25 StartZ=0 EndX=50.8869 EndY=32.25 EndZ=0
    g7: LineSegment StartX=43 StartY=33.25 StartZ=0 EndX=43 EndY=32.25 EndZ=0
    g8: LineSegment StartX=42 StartY=32.25 StartZ=0 EndX=42 EndY=25.3631 EndZ=0
    g9: LineSegment StartX=44 StartY=32.25 StartZ=0 EndX=44 EndY=25.3631 EndZ=0
    g10: ArcOfCircle CenterX=43 CenterY=33.25 CenterZ=0 NormalX=0 NormalY=0 NormalZ=1 AngleXU=0 Radius=7.95 StartAngle=4.58627 EndAngle=4.83851
  constraints (35):
    c: Diameter(g0) = 15.9
    c: DistanceX(g-1,g0) = 43
    c: DistanceY(g-1,g0) = 33.25
    c: PointOnObject(g1,g0)
    c: PointOnObject(g1,g0)
    c: Horizontal(g1)
    c: PointOnObject(g2,g0)
    c: Horizontal(g2)
    c: Symmetric(g1,g2,g0)
    c: Coincident(g3,g0)
    c: Coincident(g4,g3)
    c: Coincident(g3,g1)
    c: Coincident(g4,g1)
    c: PointOnObject(g4,g2)
    c: PointOnObject(g3,g2)
    c: DistanceY(g2,g1) = 2
    c: Horizontal(g5)
    c: Horizontal(g6)
    c: Coincident(g7,g3)
    c: PointOnObject(g7,g2)
    c: Vertical(g7)
    c: Symmetric(g5,g6,g7)
    c: PointOnObject(g5,g2)
    c: PointOnObject(g5,g0)
    c: PointOnObject(g6,g0)
    c: Coincident(g8,g5)
    c: PointOnObject(g8,g0)
    c: Vertical(g8)
    c: Coincident(g9,g6)
    c: Vertical(g9)
    c: PointOnObject(g9,g0)
    c: Coincident(g10,g3)
    c: Coincident(g10,g8)
    c: PointOnObject(g10,g9)
    c: DistanceX(g8,g9) = 2
FEATURE [Sketcher::SketchObject] Sketch090  label="Sketch_SplitPlug_P2_007"
  FullyConstrained = true
  MapMode = 5
  Placement = pos=(0,0,0) rot=(1,0,0;1.5708rad)
  Support = -> [XZ_Plane005]
  expr: Constraints[15] = <<params>>.std_wall_thick
  expr: Constraints[0] = <<params>>.xport_plug_diam + 4 * <<params>>.xport_clip_size
  expr: Constraints[1] = <<params>>.xport_offset_loc
  expr: Constraints[2] = <<params>>.xport_height_loc
  sketch-geometry (5):
    g0: Circle CenterX=43 CenterY=33.25 CenterZ=0 NormalX=0 NormalY=0 NormalZ=1 AngleXU=0 Radius=7.95
    g1: LineSegment StartX=35.1131 StartY=34.25 StartZ=0 EndX=50.8869 EndY=34.25 EndZ=0
    g2: LineSegment StartX=35.1131 StartY=32.25 StartZ=0 EndX=50.8869 EndY=32.25 EndZ=0
    g3: ArcOfCircle CenterX=43 CenterY=33.25 CenterZ=0 NormalX=0 NormalY=0 NormalZ=1 AngleXU=0 Radius=7.95 StartAngle=0.12612 EndAngle=3.01547
    g4: ArcOfCircle CenterX=43 CenterY=33.25 CenterZ=0 NormalX=0 NormalY=0 NormalZ=1 AngleXU=0 Radius=7.95 StartAngle=3.26771 EndAngle=6.15707
  constraints (16):
    c: Diameter(g0) = 15.9
    c: DistanceX(g-1,g0) = 43
    c: DistanceY(g-1,g0) = 33.25
    c: PointOnObject(g1,g0)
    c: PointOnObject(g1,g0)
    c: Horizontal(g1)
    c: PointOnObject(g2,g0)
    c: Horizontal(g2)
    c: Coincident(g3,g0)
    c: Coincident(g4,g3)
    c: Coincident(g3,g1)
    c: PointOnObject(g3,g1)
    c: Coincident(g4,g2)
    c: PointOnObject(g4,g2)
    c: Symmetric(g1,g2,g3)
    c: DistanceY(g2,g1) = 2
FEATURE [Sketcher::SketchObject] Sketch091  label="Sketch_SplitPlug_P3_007"
  FullyConstrained = true
  MapMode = 5
  Placement = pos=(0,0,0) rot=(1,0,0;1.5708rad)
  Support = -> [XZ_Plane005]
  expr: Constraints[15] = <<params>>.std_wall_thick
  expr: Constraints[0] = <<params>>.xport_plug_diam + 4 * <<params>>.xport_clip_size
  expr: Constraints[1] = <<params>>.xport_offset_loc
  expr: Constraints[2] = <<params>>.xport_height_loc
  sketch-geometry (8):
    g0: Circle CenterX=43 CenterY=33.25 CenterZ=0 NormalX=0 NormalY=0 NormalZ=1 AngleXU=0 Radius=7.95
    g1: LineSegment StartX=35.1131 StartY=34.25 StartZ=0 EndX=50.8869 EndY=34.25 EndZ=0
    g2: LineSegment StartX=35.1131 StartY=32.25 StartZ=0 EndX=50.8869 EndY=32.25 EndZ=0
    g3: ArcOfCircle CenterX=43 CenterY=33.25 CenterZ=0 NormalX=0 NormalY=0 NormalZ=1 AngleXU=0 Radius=7.95 StartAngle=0.12612 EndAngle=3.01547
    g4: ArcOfCircle CenterX=43 CenterY=33.25 CenterZ=0 NormalX=0 NormalY=0 NormalZ=1 AngleXU=0 Radius=7.95 StartAngle=3.26771 EndAngle=6.15707
    g5: ArcOfCircle CenterX=43 CenterY=33.25 CenterZ=0 NormalX=0 NormalY=0 NormalZ=1 AngleXU=0 Radius=7.95 StartAngle=1.5708 EndAngle=3.26771
    g6: LineSegment StartX=43 StartY=32.25 StartZ=0 EndX=43 EndY=41.2 EndZ=0
    g7: LineSegment StartX=43 StartY=32.25 StartZ=0 EndX=50.8869 EndY=32.25 EndZ=0
  constraints (26):
    c: Diameter(g0) = 15.9
    c: DistanceX(g-1,g0) = 43
    c: DistanceY(g-1,g0) = 33.25
    c: PointOnObject(g1,g0)
    c: PointOnObject(g1,g0)
    c: Horizontal(g1)
    c: PointOnObject(g2,g0)
    c: Horizontal(g2)
    c: Coincident(g3,g0)
    c: Coincident(g4,g3)
    c: Coincident(g3,g1)
    c: PointOnObject(g3,g1)
    c: Coincident(g4,g2)
    c: PointOnObject(g4,g2)
    c: Symmetric(g1,g2,g3)
    c: DistanceY(g2,g1) = 2
    c: Coincident(g5,g4)
    c: Coincident(g5,g4)
    c: PointOnObject(g6,g2)
    c: PointOnObject(g6,g3)
    c: Vertical(g6)
    c: PointOnObject(g4,g6)
    c: PointOnObject(g5,g6)
    c: Horizontal(g7)
    c: Coincident(g7,g6)
    c: PointOnObject(g7,g0)
FEATURE [Sketcher::SketchObject] Sketch092  label="Sketch_SplitPlug_P2_008"
  FullyConstrained = true
  MapMode = 5
  Placement = pos=(0,0,0) rot=(1,0,0;1.5708rad)
  Support = -> [XZ_Plane005]
  expr: Constraints[2] = <<params>>.xport_height_loc
  expr: Constraints[1] = <<params>>.xport_offset_loc
  expr: Constraints[0] = <<params>>.xport_plug_diam + 4 * <<params>>.xport_clip_size
  expr: Constraints[15] = <<params>>.std_wall_thick
  sketch-geometry (8):
    g0: Circle CenterX=43 CenterY=33.25 CenterZ=0 NormalX=0 NormalY=0 NormalZ=1 AngleXU=0 Radius=7.95
    g1: LineSegment StartX=35.1131 StartY=34.25 StartZ=0 EndX=50.8869 EndY=34.25 EndZ=0
    g2: LineSegment StartX=35.1131 StartY=32.25 StartZ=0 EndX=50.8869 EndY=32.25 EndZ=0
    g3: ArcOfCircle CenterX=43 CenterY=33.25 CenterZ=0 NormalX=0 NormalY=0 NormalZ=1 AngleXU=0 Radius=7.95 StartAngle=0.12612 EndAngle=3.01547
    g4: ArcOfCircle CenterX=43 CenterY=33.25 CenterZ=0 NormalX=0 NormalY=0 NormalZ=1 AngleXU=0 Radius=7.95 StartAngle=3.26771 EndAngle=6.15707
    g5: LineSegment StartX=35.1131 StartY=32.25 StartZ=0 EndX=43 EndY=32.25 EndZ=0
    g6: LineSegment StartX=43 StartY=32.25 StartZ=0 EndX=43 EndY=41.2 EndZ=0
    g7: ArcOfCircle CenterX=43 CenterY=33.25 CenterZ=0 NormalX=0 NormalY=0 NormalZ=1 AngleXU=0 Radius=7.95 StartAngle=6.15707 EndAngle=7.85398
  constraints (26):
    c: Diameter(g0) = 15.9
    c: DistanceX(g-1,g0) = 43
    c: DistanceY(g-1,g0) = 33.25
    c: PointOnObject(g1,g0)
    c: PointOnObject(g1,g0)
    c: Horizontal(g1)
    c: PointOnObject(g2,g0)
    c: Horizontal(g2)
    c: Coincident(g3,g0)
    c: Coincident(g4,g3)
    c: Coincident(g3,g1)
    c: PointOnObject(g3,g1)
    c: Coincident(g4,g2)
    c: PointOnObject(g4,g2)
    c: Symmetric(g1,g2,g3)
    c: DistanceY(g2,g1) = 2
    c: Horizontal(g5)
    c: PointOnObject(g6,g0)
    c: Vertical(g6)
    c: PointOnObject(g4,g6)
    c: Coincident(g6,g5)
    c: PointOnObject(g5,g2)
    c: PointOnObject(g5,g4)
    c: Coincident(g7,g4)
    c: Coincident(g7,g6)
    c: PointOnObject(g7,g2)
FEATURE [Sketcher::SketchObject] Sketch093  label="Sketch_SplitPlug_P1_004"
  FullyConstrained = true
  MapMode = 5
  Placement = pos=(0,0,0) rot=(1,0,0;1.5708rad)
  Support = -> [XZ_Plane005]
  expr: Constraints[0] = <<params>>.xport_plug_diam + 4 * <<params>>.xport_clip_size
  expr: Constraints[1] = <<params>>.xport_offset_loc
  expr: Constraints[2] = <<params>>.xport_height_loc
  expr: Constraints[6] = <<params>>.std_wall_thick / 2 + <<params>>.std_min_wall_thick
  sketch-geometry (3):
    g0: Circle CenterX=43 CenterY=33.25 CenterZ=0 NormalX=0 NormalY=0 NormalZ=1 AngleXU=0 Radius=7.95
    g1: LineSegment StartX=35.2565 StartY=35.05 StartZ=0 EndX=50.7435 EndY=35.05 EndZ=0
    g2: ArcOfCircle CenterX=43 CenterY=33.25 CenterZ=0 NormalX=0 NormalY=0 NormalZ=1 AngleXU=0 Radius=7.95 StartAngle=2.9132 EndAngle=6.51158
  constraints (10):
    c: Diameter(g0) = 15.9
    c: DistanceX(g-1,g0) = 43
    c: DistanceY(g-1,g0) = 33.25
    c: PointOnObject(g1,g0)
    c: PointOnObject(g1,g0)
    c: Horizontal(g1)
    c: DistanceY(g0,g1) = 1.8
    c: Coincident(g2,g0)
    c: Coincident(g2,g1)
    c: PointOnObject(g2,g1)
FEATURE [Sketcher::SketchObject] Sketch094  label="Sketch_SplitPlug_P3_008"
  FullyConstrained = true
  MapMode = 5
  Placement = pos=(0,0,0) rot=(1,0,0;1.5708rad)
  Support = -> [XZ_Plane005]
  expr: Constraints[2] = <<params>>.xport_height_loc
  expr: Constraints[1] = <<params>>.xport_offset_loc
  expr: Constraints[0] = <<params>>.xport_plug_diam + 4 * <<params>>.xport_clip_size
  expr: Constraints[15] = <<params>>.std_wall_thick
  sketch-geometry (5):
    g0: Circle CenterX=43 CenterY=33.25 CenterZ=0 NormalX=0 NormalY=0 NormalZ=1 AngleXU=0 Radius=7.95
    g1: LineSegment StartX=35.1131 StartY=34.25 StartZ=0 EndX=50.8869 EndY=34.25 EndZ=0
    g2: LineSegment StartX=35.1131 StartY=32.25 StartZ=0 EndX=50.8869 EndY=32.25 EndZ=0
    g3: ArcOfCircle CenterX=43 CenterY=33.25 CenterZ=0 NormalX=0 NormalY=0 NormalZ=1 AngleXU=0 Radius=7.95 StartAngle=0.12612 EndAngle=3.01547
    g4: ArcOfCircle CenterX=43 CenterY=33.25 CenterZ=0 NormalX=0 NormalY=0 NormalZ=1 AngleXU=0 Radius=7.95 StartAngle=3.26771 EndAngle=6.15707
  constraints (16):
    c: Diameter(g0) = 15.9
    c: DistanceX(g-1,g0) = 43
    c: DistanceY(g-1,g0) = 33.25
    c: PointOnObject(g1,g0)
    c: PointOnObject(g1,g0)
    c: Horizontal(g1)
    c: PointOnObject(g2,g0)
    c: Horizontal(g2)
    c: Coincident(g3,g0)
    c: Coincident(g4,g3)
    c: Coincident(g3,g1)
    c: PointOnObject(g3,g1)
    c: Coincident(g4,g2)
    c: PointOnObject(g4,g2)
    c: Symmetric(g1,g2,g3)
    c: DistanceY(g2,g1) = 2
FEATURE [Sketcher::SketchObject] Sketch095  label="Sketch_SplitPlug_P4_004"
  FullyConstrained = true
  MapMode = 5
  Placement = pos=(0,0,0) rot=(1,0,0;1.5708rad)
  Support = -> [XZ_Plane005]
  expr: Constraints[0] = <<params>>.xport_plug_diam + 4 * <<params>>.xport_clip_size
  expr: Constraints[1] = <<params>>.xport_offset_loc
  expr: Constraints[2] = <<params>>.xport_height_loc
  expr: Constraints[9] = <<params>>.std_wall_thick / 2 + <<params>>.std_min_wall_thick
  sketch-geometry (3):
    g0: Circle CenterX=43 CenterY=33.25 CenterZ=0 NormalX=0 NormalY=0 NormalZ=1 AngleXU=0 Radius=7.95
    g1: LineSegment StartX=35.2565 StartY=31.45 StartZ=0 EndX=50.7435 EndY=31.45 EndZ=0
    g2: ArcOfCircle CenterX=43 CenterY=33.25 CenterZ=0 NormalX=0 NormalY=0 NormalZ=1 AngleXU=0 Radius=7.95 StartAngle=6.05479 EndAngle=9.65317
  constraints (10):
    c: Diameter(g0) = 15.9
    c: DistanceX(g-1,g0) = 43
    c: DistanceY(g-1,g0) = 33.25
    c: PointOnObject(g1,g0)
    c: PointOnObject(g1,g0)
    c: Horizontal(g1)
    c: Coincident(g2,g0)
    c: Coincident(g2,g1)
    c: PointOnObject(g2,g1)
    c: DistanceY(g1,g2) = 1.8
FEATURE [Sketcher::SketchObject] Sketch096
  FullyConstrained = true
  MapMode = 5
  Placement = pos=(0,0,0) rot=(1,0,0;1.5708rad)
  Support = -> [XZ_Plane005]
  expr: Constraints[2] = <<params>>.xport_height_loc
  expr: Constraints[1] = <<params>>.xport_offset_loc
  expr: Constraints[0] = <<params>>.xport_plug_diam
  sketch-geometry (1):
    g0: Circle CenterX=43 CenterY=33.25 CenterZ=0 NormalX=0 NormalY=0 NormalZ=1 AngleXU=0 Radius=6.35
  constraints (3):
    c: Diameter(g0) = 12.7
    c: DistanceX(g-1,g0) = 43
    c: DistanceY(g-1,g0) = 33.25
FEATURE [PartDesign::Pad] Pad008  label="Pad_Plug003"
  Direction = (1,1,1)
  Length = 85
  Length2 = 100
  Placement = pos=(0,0,0) rot=(1,0,0;1.5708rad)
  Profile = -> Sketch096
  Type = 0
  expr: Length = <<params>>.plate_length / 2
FEATURE [PartDesign::Pad] Pad007  label="Pad_ClipsToTrim003"
  BaseFeature = -> Pad008
  Direction = (1,1,1)
  Length = 85
  Length2 = 100
  Placement = pos=(0,0,0) rot=(1,0,0;1.5708rad)
  Profile = -> Sketch089
  Type = 0
  expr: Length = <<params>>.plate_length / 2
FEATURE [PartDesign::Pocket] Pocket003  label="Pocket_HollowTube003"
  BaseFeature = -> Pad007
  Length = 5
  Length2 = 100
  Midplane = true
  Placement = pos=(0,0,0) rot=(1,0,0;1.5708rad)
  Profile = -> Sketch084
  Type = 1
FEATURE [PartDesign::SubtractiveLoft] SubtractiveLoft004  label="SubtractiveLoft_CutClips003"
  BaseFeature = -> Pocket003
  Closed = false
  Placement = pos=(0,0,0) rot=(1,0,0;1.5708rad)
  Profile = -> Sketch088
  Ruled = false
  Sections = -> [Sketch085]
FEATURE [PartDesign::Chamfer] Chamfer004  label="Chamfer_FrontEdge003"
  Angle = 45
  Base = -> SubtractiveLoft004 [Edge13,Edge17,Edge8]
  BaseFeature = -> SubtractiveLoft004
  ChamferType = 0
  FlipDirection = false
  Placement = pos=(0,0,0) rot=(1,0,0;1.5708rad)
  Size = 1
  Size2 = 1
  SupportTransform = false
FEATURE [PartDesign::Plane] DatumPlane014  label="Datum_ShellVert007"
  AttachmentOffset = pos=(0,0,10) rot=(0,0,1;0rad)
  Length = 90.001
  MapMode = 5
  Placement = pos=(0,0,10) rot=(0,0,1;0rad)
  ResizeMode = 0
  Support = -> [XY_Plane007]
  Width = 79.0384
  expr: .AttachmentOffset.Base.z = <<params>>.shell_vertheight
FEATURE [Sketcher::SketchObject] Sketch086  label="Sketch_Shell_Vert006"
  FullyConstrained = true
  MapMode = 5
  Placement = pos=(0,0,10) rot=(0,0,1;0rad)
  Support = -> [DatumPlane014]
  expr: Constraints[40] = <<params>>.plate_length
  expr: Constraints[65] = <<params>>.std_rad
  expr: Constraints[42] = <<params>>.tail_width
  expr: Constraints[78] = <<params>>.wheel_well_clearance
  expr: Constraints[79] = <<params>>.plate_width
  expr: Constraints[36] = <<params>>.wheel_well_plate_width
  expr: Constraints[47] = <<params>>.front_diameter
  expr: Constraints[63] = <<params>>.std_rad
  expr: Constraints[76] = <<params>>.front_vert_edge
  expr: Constraints[77] = <<params>>.back_vert_edge
  expr: Constraints[80] = <<params>>.std_rad
  expr: Constraints[81] = <<params>>.std_rad
  expr: Constraints[41] = <<params>>.tail_rad
  sketch-geometry (38):
    g0: LineSegment StartX=-57.5 StartY=17 StartZ=0 EndX=-57.5 EndY=-17 EndZ=0
    g1: LineSegment StartX=57.5 StartY=17 StartZ=0 EndX=57.5 EndY=-17 EndZ=0
    g2: LineSegment StartX=-57.5 StartY=0 StartZ=0 EndX=57.5 EndY=0 EndZ=0
    g3: LineSegment StartX=-64.5 StartY=-24 StartZ=0 EndX=64.5 EndY=-24 EndZ=0
    g4: LineSegment StartX=-64.5 StartY=24 StartZ=0 EndX=64.5 EndY=24 EndZ=0
    g5: LineSegment StartX=-64.5 StartY=-24 StartZ=0 EndX=-75.5 EndY=-24 EndZ=0
    g6: LineSegment StartX=64.5 StartY=-24 StartZ=0 EndX=75.5 EndY=-24 EndZ=0
    g7: ArcOfCircle CenterX=0 CenterY=52.6846 CenterZ=0 NormalX=0 NormalY=0 NormalZ=1 AngleXU=0 Radius=112.5 StartAngle=3.96017 EndAngle=5.4646
    g8: LineSegment StartX=-64.5 StartY=24 StartZ=0 EndX=-75.5 EndY=24 EndZ=0
    g9: LineSegment StartX=64.5 StartY=24 StartZ=0 EndX=75.5 EndY=24 EndZ=0
    g10: LineSegment StartX=-77.1162 StartY=42.1781 StartZ=0 EndX=-29.0404 EndY=108.13 EndZ=0
    g11: LineSegment StartX=-25 StartY=110.185 StartZ=0 EndX=25 EndY=110.185 EndZ=0
    g12: LineSegment StartX=29.0404 StartY=108.13 StartZ=0 EndX=77.1162 EndY=42.1781 EndZ=0
    g13: LineSegment StartX=0 StartY=0 StartZ=0 EndX=0 EndY=110.185 EndZ=0
    g14: ArcOfCircle CenterX=-25 CenterY=105.185 CenterZ=0 NormalX=0 NormalY=0 NormalZ=1 AngleXU=0 Radius=5 StartAngle=1.5708 EndAngle=2.5117
    g15: ArcOfCircle CenterX=25 CenterY=105.185 CenterZ=0 NormalX=0 NormalY=0 NormalZ=1 AngleXU=0 Radius=5 StartAngle=0.629894 EndAngle=1.5708
    g16: ArcOfCircle CenterX=-64.5 CenterY=17 CenterZ=0 NormalX=0 NormalY=0 NormalZ=1 AngleXU=0 Radius=7 StartAngle=0 EndAngle=1.5708
    g17: ArcOfCircle CenterX=-64.5 CenterY=-17 CenterZ=0 NormalX=0 NormalY=0 NormalZ=1 AngleXU=0 Radius=7 StartAngle=4.71239 EndAngle=6.28319
    g18: ArcOfCircle CenterX=64.5 CenterY=-17 CenterZ=0 NormalX=0 NormalY=0 NormalZ=1 AngleXU=0 Radius=7 StartAngle=3.14159 EndAngle=4.71239
    g19: ArcOfCircle CenterX=64.5 CenterY=17 CenterZ=0 NormalX=0 NormalY=0 NormalZ=1 AngleXU=0 Radius=7 StartAngle=1.5708 EndAngle=3.14159
    g20: GeomPoint X=0 Y=-59.8154 Z=0
    g21: Circle CenterX=0 CenterY=52.6846 CenterZ=0 NormalX=0 NormalY=0 NormalZ=1 AngleXU=0 Radius=112.5
    g22: LineSegment StartX=77.5 StartY=26 StartZ=0 EndX=77.5 EndY=41 EndZ=0
    g23: LineSegment StartX=77.5 StartY=-26 StartZ=0 EndX=77.5 EndY=-28 EndZ=0
    g24: LineSegment StartX=-77.5 StartY=-28 StartZ=0 EndX=-77.5 EndY=-26 EndZ=0
    g25: LineSegment StartX=-77.5 StartY=26 StartZ=0 EndX=-77.5 EndY=41 EndZ=0
    g26: ArcOfCircle CenterX=75.5 CenterY=-28 CenterZ=0 NormalX=0 NormalY=0 NormalZ=1 AngleXU=0 Radius=2 StartAngle=5.4646 EndAngle=6.28319
    g27: ArcOfCircle CenterX=75.5 CenterY=-26 CenterZ=0 NormalX=0 NormalY=0 NormalZ=1 AngleXU=0 Radius=2 StartAngle=-9e-16 EndAngle=1.5708
    g28: ArcOfCircle CenterX=-75.5 CenterY=-28 CenterZ=0 NormalX=0 NormalY=0 NormalZ=1 AngleXU=0 Radius=2 StartAngle=3.14159 EndAngle=3.96017
    g29: ArcOfCircle CenterX=-75.5 CenterY=-26 CenterZ=0 NormalX=0 NormalY=0 NormalZ=1 AngleXU=0 Radius=2 StartAngle=1.5708 EndAngle=3.14159
    g30: ArcOfCircle CenterX=75.5 CenterY=26 CenterZ=0 NormalX=0 NormalY=0 NormalZ=1 AngleXU=0 Radius=2 StartAngle=4.71239 EndAngle=6.28319
    g31: ArcOfCircle CenterX=75.5 CenterY=41 CenterZ=0 NormalX=0 NormalY=0 NormalZ=1 AngleXU=0 Radius=2 StartAngle=0 EndAngle=0.629894
    g32: ArcOfCircle CenterX=-75.5 CenterY=26 CenterZ=0 NormalX=0 NormalY=0 NormalZ=1 AngleXU=0 Radius=2 StartAngle=3.14159 EndAngle=4.71239
    g33: ArcOfCircle CenterX=-75.5 CenterY=41 CenterZ=0 NormalX=0 NormalY=0 NormalZ=1 AngleXU=0 Radius=2 StartAngle=2.5117 EndAngle=3.14159
    g34: LineSegment StartX=77.5 StartY=26 StartZ=0 EndX=77.5 EndY=-26 EndZ=0
    g35: LineSegment StartX=-77.5 StartY=26 StartZ=0 EndX=-77.5 EndY=-26 EndZ=0
    g36: LineSegment StartX=77.5 StartY=41 StartZ=0 EndX=77.5 EndY=-28 EndZ=0
    g37: LineSegment StartX=-77.5 StartY=41 StartZ=0 EndX=-77.5 EndY=-28 EndZ=0
  constraints (90):
    c: Vertical(g0)
    c: Vertical(g1)
    c: Horizontal(g2)
    c: Symmetric(g2,g2,g-1)
    c: Horizontal(g3)
    c: Horizontal(g5)
    c: Horizontal(g6)
    c: PointOnObject(g7,g-2)
    c: Horizontal(g8)
    c: Horizontal(g9)
    c: Horizontal(g11)
    c: Coincident(g13,g-1)
    c: PointOnObject(g13,g-2)
    c: Tangent(g10,g14) = 1.5708
    c: Tangent(g11,g14) = 1.5708
    c: Tangent(g11,g15) = 1.5708
    c: Tangent(g12,g15) = 1.5708
    c: Tangent(g8,g16) = -1.5708
    c: Tangent(g0,g16) = 1.5708
    c: Tangent(g5,g17) = 1.5708
    c: Tangent(g0,g17) = 1.5708
    c: Tangent(g1,g18) = -1.5708
    c: Tangent(g6,g18) = -1.5708
    c: Tangent(g1,g19) = -1.5708
    c: Tangent(g9,g19) = 1.5708
    c: Equal(g15,g14)
    c: Symmetric(g11,g11,g13)
    c: Equal(g18,g19)
    c: Equal(g19,g16)
    c: Equal(g16,g17)
    c: PointOnObject(g20,g-2)
    c: PointOnObject(g20,g7)
    c: Coincident(g4,g8)
    c: Coincident(g4,g9)
    c: Coincident(g3,g6)
    c: Coincident(g3,g5)
    c: DistanceX(g2,g2) = 115
    c: Symmetric(g0,g0,g2)
    c: Symmetric(g1,g1,g2)
    c: Radius(g19) = 7
    c: DistanceY(g20,g11) = 170
    c: Radius(g15) = 5
    c: DistanceX(g11,g11) = 50
    c: Equal(g9,g8)
    c: Equal(g9,g6)
    c: Coincident(g21,g7)
    c: PointOnObject(g20,g21)
    c: Diameter(g21) = 225
    c: Vertical(g22)
    c: Vertical(g23)
    c: Vertical(g24)
    c: Vertical(g25)
    c: Equal(g5,g8)
    c: Equal(g10,g12)
    c: Tangent(g7,g26) = -1.5708
    c: Tangent(g23,g26) = 1.5708
    c: Tangent(g23,g27) = 1.5708
    c: Tangent(g6,g27) = 1.5708
    c: Tangent(g7,g28) = -1.5708
    c: Tangent(g24,g28) = 1.5708
    c: Tangent(g24,g29) = 1.5708
    c: Tangent(g5,g29) = -1.5708
    c: Equal(g29,g27)
    c: Radius(g27) = 2
    c: Equal(g26,g28)
    c: Radius(g26) = 2
    c: Tangent(g9,g30) = -1.5708
    c: Tangent(g22,g30) = -1.5708
    c: Tangent(g22,g31) = -1.5708
    c: Tangent(g12,g31) = 1.5708
    c: Tangent(g8,g32) = 1.5708
    c: Tangent(g25,g32) = 1.5708
    c: Tangent(g10,g33) = 1.5708
    c: Tangent(g25,g33) = 1.5708
    c: Equal(g30,g32)
    c: Equal(g31,g33)
    c: DistanceY(g23,g23) = 2
    c: DistanceY(g22,g22) = 15
    c: DistanceY(g6,g9) = 48
    c: DistanceX(g24,g23) = 155
    c: Radius(g30) = 2
    c: Radius(g31) = 2
    c: Coincident(g34,g22)
    c: Coincident(g34,g23)
    c: Coincident(g35,g25)
    c: Coincident(g35,g24)
    c: Coincident(g37,g28)
    c: Coincident(g37,g33)
    c: Coincident(g36,g31)
    c: Coincident(g36,g26)
FEATURE [PartDesign::Plane] DatumPlane015  label="Datum_ShellTot007"
  AttachmentOffset = pos=(0,0,42) rot=(0,0,1;0rad)
  Length = 90.001
  MapMode = 5
  Placement = pos=(0,0,42) rot=(0,0,1;0rad)
  ResizeMode = 0
  Support = -> [XY_Plane007]
  Width = 79.0384
  expr: .AttachmentOffset.Base.z = <<params>>.shell_totheight
FEATURE [Sketcher::SketchObject] Sketch087  label="Sketch_Shell_Top006"
  FullyConstrained = true
  MapMode = 5
  Placement = pos=(0,0,42) rot=(0,0,1;0rad)
  Support = -> [DatumPlane015]
  expr: Constraints[41] = <<params>>.tail_rad
  expr: Constraints[76] = <<params>>.front_vert_edge
  expr: Constraints[47] = <<params>>.front_diameter
  expr: Constraints[36] = <<params>>.wheel_well_plate_width - 2 * Spreadsheet.shell_overhang_leng
  expr: Constraints[79] = <<params>>.plate_width
  expr: Constraints[42] = <<params>>.tail_width
  expr: Constraints[78] = <<params>>.wheel_well_clearance
  expr: Constraints[65] = <<params>>.std_rad
  expr: Constraints[40] = <<params>>.plate_length
  expr: Constraints[88] = Spreadsheet.shell_overhang_leng
  expr: Constraints[81] = <<params>>.std_rad
  expr: Constraints[63] = <<params>>.std_rad
  expr: Constraints[77] = <<params>>.back_vert_edge
  expr: Constraints[120] = Spreadsheet.shell_overhang_leng
  expr: Constraints[80] = <<params>>.std_rad
  expr: Constraints[119] = Spreadsheet.shell_overhang_leng
  expr: Constraints[123] = <<params>>.shell_overhang_leng
  sketch-geometry (52):
    g0: LineSegment StartX=-43.5 StartY=17 StartZ=0 EndX=-43.5 EndY=-17 EndZ=0
    g1: LineSegment StartX=43.5 StartY=17 StartZ=0 EndX=43.5 EndY=-17 EndZ=0
    g2: LineSegment StartX=-43.5 StartY=0 StartZ=0 EndX=43.5 EndY=0 EndZ=0
    g3: LineSegment StartX=-50.5 StartY=-24 StartZ=0 EndX=50.5 EndY=-24 EndZ=0
    g4: LineSegment StartX=-50.5 StartY=24 StartZ=0 EndX=50.5 EndY=24 EndZ=0
    g5: LineSegment StartX=-50.5 StartY=-24 StartZ=0 EndX=-75.5 EndY=-24 EndZ=0
    g6: LineSegment StartX=50.5 StartY=-24 StartZ=0 EndX=75.5 EndY=-24 EndZ=0
    g7: ArcOfCircle CenterX=0 CenterY=52.6846 CenterZ=0 NormalX=0 NormalY=0 NormalZ=1 AngleXU=0 Radius=112.5 StartAngle=3.96017 EndAngle=5.4646
    g8: LineSegment StartX=-50.5 StartY=24 StartZ=0 EndX=-75.5 EndY=24 EndZ=0
    g9: LineSegment StartX=50.5 StartY=24 StartZ=0 EndX=75.5 EndY=24 EndZ=0
    g10: LineSegment StartX=-77.1162 StartY=42.1781 StartZ=0 EndX=-29.0404 EndY=108.13 EndZ=0
    g11: LineSegment StartX=-25 StartY=110.185 StartZ=0 EndX=25 EndY=110.185 EndZ=0
    g12: LineSegment StartX=29.0404 StartY=108.13 StartZ=0 EndX=77.1162 EndY=42.1781 EndZ=0
    g13: LineSegment StartX=0 StartY=0 StartZ=0 EndX=0 EndY=110.185 EndZ=0
    g14: ArcOfCircle CenterX=-25 CenterY=105.185 CenterZ=0 NormalX=0 NormalY=0 NormalZ=1 AngleXU=0 Radius=5 StartAngle=1.5708 EndAngle=2.5117
    g15: ArcOfCircle CenterX=25 CenterY=105.185 CenterZ=0 NormalX=0 NormalY=0 NormalZ=1 AngleXU=0 Radius=5 StartAngle=0.629894 EndAngle=1.5708
    g16: ArcOfCircle CenterX=-50.5 CenterY=17 CenterZ=0 NormalX=0 NormalY=0 NormalZ=1 AngleXU=0 Radius=7 StartAngle=0 EndAngle=1.5708
    g17: ArcOfCircle CenterX=-50.5 CenterY=-17 CenterZ=0 NormalX=0 NormalY=0 NormalZ=1 AngleXU=0 Radius=7 StartAngle=4.71239 EndAngle=6.28319
    g18: ArcOfCircle CenterX=50.5 CenterY=-17 CenterZ=0 NormalX=0 NormalY=0 NormalZ=1 AngleXU=0 Radius=7 StartAngle=3.14159 EndAngle=4.71239
    g19: ArcOfCircle CenterX=50.5 CenterY=17 CenterZ=0 NormalX=0 NormalY=0 NormalZ=1 AngleXU=0 Radius=7 StartAngle=1.5708 EndAngle=3.14159
    g20: GeomPoint X=0 Y=-59.8154 Z=0
    g21: Circle CenterX=0 CenterY=52.6846 CenterZ=0 NormalX=0 NormalY=0 NormalZ=1 AngleXU=0 Radius=112.5
    g22: LineSegment StartX=77.5 StartY=26 StartZ=0 EndX=77.5 EndY=41 EndZ=0
    g23: LineSegment StartX=77.5 StartY=-26 StartZ=0 EndX=77.5 EndY=-28 EndZ=0
    g24: LineSegment StartX=-77.5 StartY=-28 StartZ=0 EndX=-77.5 EndY=-26 EndZ=0
    g25: LineSegment StartX=-77.5 StartY=26 StartZ=0 EndX=-77.5 EndY=41 EndZ=0
    g26: ArcOfCircle CenterX=75.5 CenterY=-28 CenterZ=0 NormalX=0 NormalY=0 NormalZ=1 AngleXU=0 Radius=2 StartAngle=5.4646 EndAngle=6.28319
    g27: ArcOfCircle CenterX=75.5 CenterY=-26 CenterZ=0 NormalX=0 NormalY=0 NormalZ=1 AngleXU=0 Radius=2 StartAngle=0 EndAngle=1.5708
    g28: ArcOfCircle CenterX=-75.5 CenterY=-28 CenterZ=0 NormalX=0 NormalY=0 NormalZ=1 AngleXU=0 Radius=2 StartAngle=3.14159 EndAngle=3.96017
    g29: ArcOfCircle CenterX=-75.5 CenterY=-26 CenterZ=0 NormalX=0 NormalY=0 NormalZ=1 AngleXU=0 Radius=2 StartAngle=1.5708 EndAngle=3.14159
    g30: ArcOfCircle CenterX=75.5 CenterY=26 CenterZ=0 NormalX=0 NormalY=0 NormalZ=1 AngleXU=0 Radius=2 StartAngle=4.71239 EndAngle=6.28319
    g31: ArcOfCircle CenterX=75.5 CenterY=41 CenterZ=0 NormalX=0 NormalY=0 NormalZ=1 AngleXU=0 Radius=2 StartAngle=4e-16 EndAngle=0.629894
    g32: ArcOfCircle CenterX=-75.5 CenterY=26 CenterZ=0 NormalX=0 NormalY=0 NormalZ=1 AngleXU=0 Radius=2 StartAngle=3.14159 EndAngle=4.71239
    g33: ArcOfCircle CenterX=-75.5 CenterY=41 CenterZ=0 NormalX=0 NormalY=0 NormalZ=1 AngleXU=0 Radius=2 StartAngle=2.5117 EndAngle=3.14159
    g34: LineSegment StartX=77.5 StartY=26 StartZ=0 EndX=77.5 EndY=-26 EndZ=0
    g35: LineSegment StartX=-77.5 StartY=26 StartZ=0 EndX=-77.5 EndY=-26 EndZ=0
    g36: LineSegment StartX=-17.8805 StartY=96.1846 StartZ=0 EndX=17.8805 EndY=96.1846 EndZ=0
    g37: GeomPoint X=0 Y=96.1846 Z=0
    g38: LineSegment StartX=-21.921 StartY=94.1299 StartZ=0 EndX=-63.1162 EndY=37.617 EndZ=0
    g39: LineSegment StartX=-63.5 StartY=36.4389 StartZ=0 EndX=-63.5 EndY=-24 EndZ=0
    g40: LineSegment StartX=21.921 StartY=94.1299 StartZ=0 EndX=63.1162 EndY=37.617 EndZ=0
    g41: LineSegment StartX=63.5 StartY=36.4389 StartZ=0 EndX=63.5 EndY=-24 EndZ=0
    g42: ArcOfCircle CenterX=0 CenterY=61.5293 CenterZ=0 NormalX=0 NormalY=0 NormalZ=1 AngleXU=0 Radius=107.345 StartAngle=4.08899 EndAngle=5.33579
    g43: LineSegment StartX=-63.5 StartY=36.4389 StartZ=0 EndX=63.5 EndY=36.4389 EndZ=0
    g44: GeomPoint X=0 Y=-45.8154 Z=0
    g45: ArcOfCircle CenterX=-17.8805 CenterY=91.1846 CenterZ=0 NormalX=0 NormalY=0 NormalZ=1 AngleXU=0 Radius=5 StartAngle=1.5708 EndAngle=2.5117
    g46: ArcOfCircle CenterX=17.8805 CenterY=91.1846 CenterZ=0 NormalX=0 NormalY=0 NormalZ=1 AngleXU=0 Radius=5 StartAngle=0.629894 EndAngle=1.5708
    g47: ArcOfCircle CenterX=61.5 CenterY=36.4389 CenterZ=0 NormalX=0 NormalY=0 NormalZ=1 AngleXU=0 Radius=2 StartAngle=-9e-16 EndAngle=0.629894
    g48: ArcOfCircle CenterX=-61.5 CenterY=36.4389 CenterZ=0 NormalX=0 NormalY=0 NormalZ=1 AngleXU=0 Radius=2 StartAngle=2.5117 EndAngle=3.14159
    g49: ArcOfCircle CenterX=61.5 CenterY=-24 CenterZ=0 NormalX=0 NormalY=0 NormalZ=1 AngleXU=0 Radius=2 StartAngle=5.33579 EndAngle=6.28319
    g50: ArcOfCircle CenterX=-61.5 CenterY=-24 CenterZ=0 NormalX=0 NormalY=0 NormalZ=1 AngleXU=0 Radius=2 StartAngle=3.14159 EndAngle=4.08899
    g51: LineSegment StartX=-29.0404 StartY=108.13 StartZ=0 EndX=-17.7272 EndY=99.883 EndZ=0
  constraints (125):
    c: Vertical(g0)
    c: Vertical(g1)
    c: Horizontal(g2)
    c: Symmetric(g2,g2,g-1)
    c: Horizontal(g3)
    c: Horizontal(g5)
    c: Horizontal(g6)
    c: PointOnObject(g7,g-2)
    c: Horizontal(g8)
    c: Horizontal(g9)
    c: Horizontal(g11)
    c: Coincident(g13,g-1)
    c: PointOnObject(g13,g-2)
    c: Tangent(g10,g14) = 1.5708
    c: Tangent(g11,g14) = 1.5708
    c: Tangent(g11,g15) = 1.5708
    c: Tangent(g12,g15) = 1.5708
    c: Tangent(g8,g16) = -1.5708
    c: Tangent(g0,g16) = 1.5708
    c: Tangent(g5,g17) = 1.5708
    c: Tangent(g0,g17) = 1.5708
    c: Tangent(g1,g18) = -1.5708
    c: Tangent(g6,g18) = -1.5708
    c: Tangent(g1,g19) = -1.5708
    c: Tangent(g9,g19) = 1.5708
    c: Equal(g15,g14)
    c: Symmetric(g11,g11,g13)
    c: Equal(g18,g19)
    c: Equal(g19,g16)
    c: Equal(g16,g17)
    c: PointOnObject(g20,g-2)
    c: PointOnObject(g20,g7)
    c: Coincident(g4,g8)
    c: Coincident(g4,g9)
    c: Coincident(g3,g6)
    c: Coincident(g3,g5)
    c: DistanceX(g2,g2) = 87
    c: Symmetric(g0,g0,g2)
    c: Symmetric(g1,g1,g2)
    c: Radius(g19) = 7
    c: DistanceY(g20,g11) = 170
    c: Radius(g15) = 5
    c: DistanceX(g11,g11) = 50
    c: Equal(g9,g8)
    c: Equal(g9,g6)
    c: Coincident(g21,g7)
    c: PointOnObject(g20,g21)
    c: Diameter(g21) = 225
    c: Vertical(g22)
    c: Vertical(g23)
    c: Vertical(g24)
    c: Vertical(g25)
    c: Equal(g5,g8)
    c: Equal(g10,g12)
    c: Tangent(g7,g26) = -1.5708
    c: Tangent(g23,g26) = 1.5708
    c: Tangent(g23,g27) = 1.5708
    c: Tangent(g6,g27) = 1.5708
    c: Tangent(g7,g28) = -1.5708
    c: Tangent(g24,g28) = 1.5708
    c: Tangent(g24,g29) = 1.5708
    c: Tangent(g5,g29) = -1.5708
    c: Equal(g29,g27)
    c: Radius(g27) = 2
    c: Equal(g26,g28)
    c: Radius(g26) = 2
    c: Tangent(g9,g30) = -1.5708
    c: Tangent(g22,g30) = -1.5708
    c: Tangent(g22,g31) = -1.5708
    c: Tangent(g12,g31) = 1.5708
    c: Tangent(g8,g32) = 1.5708
    c: Tangent(g25,g32) = 1.5708
    c: Tangent(g10,g33) = 1.5708
    c: Tangent(g25,g33) = 1.5708
    c: Equal(g30,g32)
    c: Equal(g31,g33)
    c: DistanceY(g23,g23) = 2
    c: DistanceY(g22,g22) = 15
    c: DistanceY(g6,g9) = 48
    c: DistanceX(g24,g23) = 155
    c: Radius(g30) = 2
    c: Radius(g31) = 2
    c: Coincident(g34,g22)
    c: Coincident(g34,g23)
    c: Coincident(g35,g25)
    c: Coincident(g35,g24)
    c: Horizontal(g36)
    c: PointOnObject(g37,g13)
    c: DistanceY(g37,g13) = 14
    c: Vertical(g39)
    c: Vertical(g41)
    c: PointOnObject(g42,g13)
    c: Horizontal(g43)
    c: Parallel(g40,g12)
    c: PointOnObject(g44,g-2)
    c: PointOnObject(g44,g42)
    c: Tangent(g38,g45) = -1.5708
    c: Tangent(g36,g45) = 1.5708
    c: Tangent(g40,g46) = 1.5708
    c: Tangent(g36,g46) = 1.5708
    c: Tangent(g41,g47) = 1.5708
    c: Tangent(g40,g47) = 1.5708
    c: Tangent(g39,g48) = -1.5708
    c: Tangent(g38,g48) = -1.5708
    c: Tangent(g42,g49) = -1.5708
    c: Tangent(g41,g49) = 1.5708
    c: Tangent(g42,g50) = -1.5708
    c: Tangent(g39,g50) = -1.5708
    c: Coincident(g43,g39)
    c: Coincident(g43,g41)
    c: Equal(g15,g46)
    c: Equal(g46,g45)
    c: Symmetric(g36,g36,g37)
    c: Equal(g31,g47)
    c: Equal(g26,g49)
    c: Equal(g50,g29)
    c: Equal(g48,g32)
    c: PointOnObject(g41,g6)
    c: PointOnObject(g50,g5)
    c: DistanceY(g20,g44) = 14
    c: DistanceX(g41,g22) = 14
    c: PointOnObject(g51,g38)
    c: Perpendicular(g38,g51)
    c: Distance(g51) = 14
    c: Coincident(g51,g10)
FEATURE [Sketcher::SketchObject] Sketch097  label="Sketch_HollowPlug004"
  FullyConstrained = true
  MapMode = 5
  Placement = pos=(0,0,0) rot=(1,0,0;1.5708rad)
  Support = -> [XZ_Plane006]
  expr: Constraints[0] = <<params>>.xport_plug_diam - 2 * <<params>>.xport_plug_wall_thick
  expr: Constraints[1] = <<params>>.xport_offset_loc
  expr: Constraints[2] = <<params>>.xport_height_loc
  sketch-geometry (1):
    g0: Circle CenterX=43 CenterY=33.25 CenterZ=0 NormalX=0 NormalY=0 NormalZ=1 AngleXU=0 Radius=5.55
  constraints (3):
    c: Diameter(g0) = 11.1
    c: DistanceX(g-1,g0) = 43
    c: DistanceY(g-1,g0) = 33.25
FEATURE [Sketcher::SketchObject] Sketch098  label="Sketch_Shell_Top_CutPlug004"
  FullyConstrained = true
  MapMode = 5
  Placement = pos=(0,0,42) rot=(0,0,1;0rad)
  expr: Constraints[142] = <<params>>.xport_plug_plate_thick
  expr: Constraints[79] = <<params>>.plate_width
  expr: Constraints[136] = <<params>>.xport_offset_loc
  expr: Constraints[120] = <<params>>.shell_overhang_leng
  expr: Constraints[77] = <<params>>.back_vert_edge
  expr: Constraints[155] = <<params>>.shell_wall_thick + <<params>>.std_tol_interfere
  expr: Constraints[63] = <<params>>.std_rad
  expr: Constraints[143] = <<params>>.std_wall_thick
  expr: Constraints[42] = <<params>>.tail_width
  expr: Constraints[78] = <<params>>.wheel_well_clearance
  expr: Constraints[153] = <<params>>.xport_plug_diam / 2
  expr: Constraints[152] = <<params>>.xport_plug_diam / 2
  expr: Constraints[80] = <<params>>.std_rad
  expr: Constraints[117] = <<params>>.shell_overhang_leng
  expr: Constraints[76] = <<params>>.front_vert_edge
  expr: Constraints[130] = <<params>>.plate_length / 2 + <<params>>.std_wall_thick
  expr: Constraints[41] = <<params>>.tail_rad
  expr: Constraints[187] = <<params>>.xport_clip_size
  expr: Constraints[129] = <<params>>.std_wall_thick
  expr: Constraints[40] = <<params>>.plate_length
  expr: Constraints[189] = <<params>>.shell_overhang_leng
  expr: Constraints[65] = <<params>>.std_rad
  expr: Constraints[186] = <<params>>.xport_clip_size
  expr: Constraints[81] = <<params>>.std_rad
  expr: Constraints[88] = Spreadsheet.shell_overhang_leng
  expr: Constraints[116] = Spreadsheet.shell_overhang_leng
  expr: Constraints[36] = <<params>>.wheel_well_plate_width - 2 * Spreadsheet.shell_overhang_leng
  expr: Constraints[47] = <<params>>.front_diameter
  sketch-geometry (80):
    g0: LineSegment StartX=-43.5 StartY=17 StartZ=0 EndX=-43.5 EndY=-17 EndZ=0
    g1: LineSegment StartX=43.5 StartY=17 StartZ=0 EndX=43.5 EndY=-17 EndZ=0
    g2: LineSegment StartX=-43.5 StartY=0 StartZ=0 EndX=43.5 EndY=0 EndZ=0
    g3: LineSegment StartX=-50.5 StartY=-24 StartZ=0 EndX=50.5 EndY=-24 EndZ=0
    g4: LineSegment StartX=-50.5 StartY=24 StartZ=0 EndX=50.5 EndY=24 EndZ=0
    g5: LineSegment StartX=-50.5 StartY=-24 StartZ=0 EndX=-75.5 EndY=-24 EndZ=0
    g6: LineSegment StartX=50.5 StartY=-24 StartZ=0 EndX=75.5 EndY=-24 EndZ=0
    g7: ArcOfCircle CenterX=0 CenterY=52.6846 CenterZ=0 NormalX=0 NormalY=0 NormalZ=1 AngleXU=0 Radius=112.5 StartAngle=3.96017 EndAngle=5.4646
    g8: LineSegment StartX=-50.5 StartY=24 StartZ=0 EndX=-75.5 EndY=24 EndZ=0
    g9: LineSegment StartX=50.5 StartY=24 StartZ=0 EndX=75.5 EndY=24 EndZ=0
    g10: LineSegment StartX=-77.1162 StartY=42.1781 StartZ=0 EndX=-29.0404 EndY=108.13 EndZ=0
    g11: LineSegment StartX=-25 StartY=110.185 StartZ=0 EndX=25 EndY=110.185 EndZ=0
    g12: LineSegment StartX=29.0404 StartY=108.13 StartZ=0 EndX=77.1162 EndY=42.1781 EndZ=0
    g13: LineSegment StartX=0 StartY=0 StartZ=0 EndX=0 EndY=110.185 EndZ=0
    g14: ArcOfCircle CenterX=-25 CenterY=105.185 CenterZ=0 NormalX=0 NormalY=0 NormalZ=1 AngleXU=0 Radius=5 StartAngle=1.5708 EndAngle=2.5117
    g15: ArcOfCircle CenterX=25 CenterY=105.185 CenterZ=0 NormalX=0 NormalY=0 NormalZ=1 AngleXU=0 Radius=5 StartAngle=0.629894 EndAngle=1.5708
    g16: ArcOfCircle CenterX=-50.5 CenterY=17 CenterZ=0 NormalX=0 NormalY=0 NormalZ=1 AngleXU=0 Radius=7 StartAngle=0 EndAngle=1.5708
    g17: ArcOfCircle CenterX=-50.5 CenterY=-17 CenterZ=0 NormalX=0 NormalY=0 NormalZ=1 AngleXU=0 Radius=7 StartAngle=4.71239 EndAngle=6.28319
    g18: ArcOfCircle CenterX=50.5 CenterY=-17 CenterZ=0 NormalX=0 NormalY=0 NormalZ=1 AngleXU=0 Radius=7 StartAngle=3.14159 EndAngle=4.71239
    g19: ArcOfCircle CenterX=50.5 CenterY=17 CenterZ=0 NormalX=0 NormalY=0 NormalZ=1 AngleXU=0 Radius=7 StartAngle=1.5708 EndAngle=3.14159
    g20: GeomPoint X=0 Y=-59.8154 Z=0
    g21: Circle CenterX=0 CenterY=52.6846 CenterZ=0 NormalX=0 NormalY=0 NormalZ=1 AngleXU=0 Radius=112.5
    g22: LineSegment StartX=77.5 StartY=26 StartZ=0 EndX=77.5 EndY=41 EndZ=0
    g23: LineSegment StartX=77.5 StartY=-26 StartZ=0 EndX=77.5 EndY=-28 EndZ=0
    g24: LineSegment StartX=-77.5 StartY=-28 StartZ=0 EndX=-77.5 EndY=-26 EndZ=0
    g25: LineSegment StartX=-77.5 StartY=26 StartZ=0 EndX=-77.5 EndY=41 EndZ=0
    g26: ArcOfCircle CenterX=75.5 CenterY=-28 CenterZ=0 NormalX=0 NormalY=0 NormalZ=1 AngleXU=0 Radius=2 StartAngle=5.4646 EndAngle=6.28319
    g27: ArcOfCircle CenterX=75.5 CenterY=-26 CenterZ=0 NormalX=0 NormalY=0 NormalZ=1 AngleXU=0 Radius=2 StartAngle=0 EndAngle=1.5708
    g28: ArcOfCircle CenterX=-75.5 CenterY=-28 CenterZ=0 NormalX=0 NormalY=0 NormalZ=1 AngleXU=0 Radius=2 StartAngle=3.14159 EndAngle=3.96017
    g29: ArcOfCircle CenterX=-75.5 CenterY=-26 CenterZ=0 NormalX=0 NormalY=0 NormalZ=1 AngleXU=0 Radius=2 StartAngle=1.5708 EndAngle=3.14159
    g30: ArcOfCircle CenterX=75.5 CenterY=26 CenterZ=0 NormalX=0 NormalY=0 NormalZ=1 AngleXU=0 Radius=2 StartAngle=4.71239 EndAngle=6.28319
    g31: ArcOfCircle CenterX=75.5 CenterY=41 CenterZ=0 NormalX=0 NormalY=0 NormalZ=1 AngleXU=0 Radius=2 StartAngle=9e-16 EndAngle=0.629894
    g32: ArcOfCircle CenterX=-75.5 CenterY=26 CenterZ=0 NormalX=0 NormalY=0 NormalZ=1 AngleXU=0 Radius=2 StartAngle=3.14159 EndAngle=4.71239
    g33: ArcOfCircle CenterX=-75.5 CenterY=41 CenterZ=0 NormalX=0 NormalY=0 NormalZ=1 AngleXU=0 Radius=2 StartAngle=2.5117 EndAngle=3.14159
    g34: LineSegment StartX=77.5 StartY=26 StartZ=0 EndX=77.5 EndY=-26 EndZ=0
    g35: LineSegment StartX=-77.5 StartY=26 StartZ=0 EndX=-77.5 EndY=-26 EndZ=0
    g36: LineSegment StartX=-17.8805 StartY=96.1846 StartZ=0 EndX=17.8805 EndY=96.1846 EndZ=0
    g37: GeomPoint X=0 Y=96.1846 Z=0
    g38: LineSegment StartX=-21.921 StartY=94.1299 StartZ=0 EndX=-63.1162 EndY=37.617 EndZ=0
    g39: LineSegment StartX=-63.5 StartY=36.4389 StartZ=0 EndX=-63.5 EndY=-21.6794 EndZ=0
    g40: LineSegment StartX=21.921 StartY=94.1299 StartZ=0 EndX=63.1162 EndY=37.617 EndZ=0
    g41: LineSegment StartX=63.5 StartY=36.4389 StartZ=0 EndX=63.5 EndY=-21.6794 EndZ=0
    g42: ArcOfCircle CenterX=0 CenterY=52.6846 CenterZ=0 NormalX=0 NormalY=0 NormalZ=1 AngleXU=0 Radius=98.5 StartAngle=4.02139 EndAngle=5.40339
    g43: LineSegment StartX=-63.5 StartY=36.4389 StartZ=0 EndX=63.5 EndY=36.4389 EndZ=0
    g44: GeomPoint X=0 Y=-45.8154 Z=0
    g45: ArcOfCircle CenterX=-17.8805 CenterY=91.1846 CenterZ=0 NormalX=0 NormalY=0 NormalZ=1 AngleXU=0 Radius=5 StartAngle=1.5708 EndAngle=2.5117
    g46: ArcOfCircle CenterX=17.8805 CenterY=91.1846 CenterZ=0 NormalX=0 NormalY=0 NormalZ=1 AngleXU=0 Radius=5 StartAngle=0.629894 EndAngle=1.5708
    g47: ArcOfCircle CenterX=61.5 CenterY=36.4389 CenterZ=0 NormalX=0 NormalY=0 NormalZ=1 AngleXU=0 Radius=2 StartAngle=0 EndAngle=0.629894
    g48: ArcOfCircle CenterX=-61.5 CenterY=36.4389 CenterZ=0 NormalX=0 NormalY=0 NormalZ=1 AngleXU=0 Radius=2 StartAngle=2.5117 EndAngle=3.14159
    g49: ArcOfCircle CenterX=61.5 CenterY=-21.6794 CenterZ=0 NormalX=0 NormalY=0 NormalZ=1 AngleXU=0 Radius=2 StartAngle=5.40339 EndAngle=6.28319
    g50: ArcOfCircle CenterX=-61.5 CenterY=-21.6794 CenterZ=0 NormalX=0 NormalY=0 NormalZ=1 AngleXU=0 Radius=2 StartAngle=3.14159 EndAngle=4.02139
    g51: LineSegment StartX=-29.0404 StartY=108.13 StartZ=0 EndX=-17.7272 EndY=99.883 EndZ=0
    g52: LineSegment StartX=-2 StartY=2 StartZ=0 EndX=-2 EndY=-87 EndZ=0
    g53: LineSegment StartX=-2 StartY=-87 StartZ=0 EndX=63.5 EndY=-87 EndZ=0
    g54: LineSegment StartX=63.5 StartY=-87 StartZ=0 EndX=63.5 EndY=-27.7653 EndZ=0
    g55: LineSegment StartX=63.5 StartY=2 StartZ=0 EndX=-2 EndY=2 EndZ=0
    g56: LineSegment StartX=0 StartY=-58.5771 StartZ=0 EndX=63.5 EndY=-27.7653 EndZ=0
    g57: LineSegment StartX=63.5 StartY=-22.6148 StartZ=0 EndX=63.5 EndY=-27.7653 EndZ=0
    g58: GeomPoint X=43 Y=-35.934 Z=0
    g59: LineSegment StartX=0 StartY=52.6846 StartZ=0 EndX=43 EndY=-35.934 EndZ=0
    g60: LineSegment StartX=43 StartY=-35.934 StartZ=0 EndX=43.6985 EndY=-37.3735 EndZ=0
    g61: LineSegment StartX=0 StartY=-58.5771 StartZ=0 EndX=-1.81e-14 EndY=-45.8154 EndZ=0
    g62: LineSegment StartX=63.5 StartY=2 StartZ=0 EndX=63.5 EndY=-22.6148 EndZ=0
    g63: LineSegment StartX=36.65 StartY=-38.7431 StartZ=0 EndX=36.65 EndY=-36.5431 EndZ=0
    g64: LineSegment StartX=49.35 StartY=-30.3611 StartZ=0 EndX=49.35 EndY=-32.5611 EndZ=0
    g65: LineSegment StartX=36.65 StartY=-36.5431 StartZ=0 EndX=35.9672 EndY=-35.8603 EndZ=0
    g66: LineSegment StartX=35.9672 StartY=-35.2946 StartZ=0 EndX=36.65 EndY=-34.6118 EndZ=0
    g67: LineSegment StartX=49.35 StartY=-30.3611 StartZ=0 EndX=50.0328 EndY=-29.6783 EndZ=0
    g68: LineSegment StartX=50.0328 StartY=-29.1126 StartZ=0 EndX=49.35 EndY=-28.4297 EndZ=0
    g69: LineSegment StartX=49.35 StartY=-28.4297 StartZ=0 EndX=36.65 EndY=-34.6118 EndZ=0
    g70: ArcOfCircle CenterX=36.25 CenterY=-35.5775 CenterZ=0 NormalX=0 NormalY=0 NormalZ=1 AngleXU=0 Radius=0.4 StartAngle=2.35619 EndAngle=3.92699
    g71: ArcOfCircle CenterX=49.75 CenterY=-29.3954 CenterZ=0 NormalX=0 NormalY=0 NormalZ=1 AngleXU=0 Radius=0.4 StartAngle=5.49779 EndAngle=7.06858
    g72: LineSegment StartX=36.65 StartY=-36.5431 StartZ=0 EndX=36.65 EndY=-34.6118 EndZ=0
    g73: GeomPoint X=35.85 Y=-35.5775 Z=0
    g74: GeomPoint X=50.15 Y=-29.3954 Z=0
    g75: LineSegment StartX=49.35 StartY=-30.3611 StartZ=0 EndX=49.35 EndY=-28.4297 EndZ=0
    g76: LineSegment StartX=50.15 StartY=-29.3954 StartZ=0 EndX=49.35 EndY=-29.3954 EndZ=0
    g77: LineSegment StartX=36.65 StartY=-35.5775 StartZ=0 EndX=35.85 EndY=-35.5775 EndZ=0
    g78: ArcOfCircle CenterX=0 CenterY=52.6846 CenterZ=0 NormalX=0 NormalY=0 NormalZ=1 AngleXU=0 Radius=98.5 StartAngle=4.71239 EndAngle=5.09364
    g79: ArcOfCircle CenterX=0 CenterY=52.6846 CenterZ=0 NormalX=0 NormalY=0 NormalZ=1 AngleXU=0 Radius=98.5 StartAngle=5.23716 EndAngle=5.41298
  constraints (201):
    c: Vertical(g0)
    c: Vertical(g1)
    c: Horizontal(g2)
    c: Symmetric(g2,g2,g-1)
    c: Horizontal(g3)
    c: Horizontal(g5)
    c: Horizontal(g6)
    c: PointOnObject(g7,g-2)
    c: Horizontal(g8)
    c: Horizontal(g9)
    c: Horizontal(g11)
    c: Coincident(g13,g-1)
    c: PointOnObject(g13,g-2)
    c: Tangent(g10,g14) = 1.5708
    c: Tangent(g11,g14) = 1.5708
    c: Tangent(g11,g15) = 1.5708
    c: Tangent(g12,g15) = 1.5708
    c: Tangent(g8,g16) = -1.5708
    c: Tangent(g0,g16) = 1.5708
    c: Tangent(g5,g17) = 1.5708
    c: Tangent(g0,g17) = 1.5708
    c: Tangent(g1,g18) = -1.5708
    c: Tangent(g6,g18) = -1.5708
    c: Tangent(g1,g19) = -1.5708
    c: Tangent(g9,g19) = 1.5708
    c: Equal(g15,g14)
    c: Symmetric(g11,g11,g13)
    c: Equal(g18,g19)
    c: Equal(g19,g16)
    c: Equal(g16,g17)
    c: PointOnObject(g20,g-2)
    c: PointOnObject(g20,g7)
    c: Coincident(g4,g8)
    c: Coincident(g4,g9)
    c: Coincident(g3,g6)
    c: Coincident(g3,g5)
    c: DistanceX(g2,g2) = 87
    c: Symmetric(g0,g0,g2)
    c: Symmetric(g1,g1,g2)
    c: Radius(g19) = 7
    c: DistanceY(g20,g11) = 170
    c: Radius(g15) = 5
    c: DistanceX(g11,g11) = 50
    c: Equal(g9,g8)
    c: Equal(g9,g6)
    c: Coincident(g21,g7)
    c: PointOnObject(g20,g21)
    c: Diameter(g21) = 225
    c: Vertical(g22)
    c: Vertical(g23)
    c: Vertical(g24)
    c: Vertical(g25)
    c: Equal(g5,g8)
    c: Equal(g10,g12)
    c: Tangent(g7,g26) = -1.5708
    c: Tangent(g23,g26) = 1.5708
    c: Tangent(g23,g27) = 1.5708
    c: Tangent(g6,g27) = 1.5708
    c: Tangent(g7,g28) = -1.5708
    c: Tangent(g24,g28) = 1.5708
    c: Tangent(g24,g29) = 1.5708
    c: Tangent(g5,g29) = -1.5708
    c: Equal(g29,g27)
    c: Radius(g27) = 2
    c: Equal(g26,g28)
    c: Radius(g26) = 2
    c: Tangent(g9,g30) = -1.5708
    c: Tangent(g22,g30) = -1.5708
    c: Tangent(g22,g31) = -1.5708
    c: Tangent(g12,g31) = 1.5708
    c: Tangent(g8,g32) = 1.5708
    c: Tangent(g25,g32) = 1.5708
    c: Tangent(g10,g33) = 1.5708
    c: Tangent(g25,g33) = 1.5708
    c: Equal(g30,g32)
    c: Equal(g31,g33)
    c: DistanceY(g23,g23) = 2
    c: DistanceY(g22,g22) = 15
    c: DistanceY(g6,g9) = 48
    c: DistanceX(g24,g23) = 155
    c: Radius(g30) = 2
    c: Radius(g31) = 2
    c: Coincident(g34,g22)
    c: Coincident(g34,g23)
    c: Coincident(g35,g25)
    c: Coincident(g35,g24)
    c: Horizontal(g36)
    c: PointOnObject(g37,g13)
    c: DistanceY(g37,g13) = 14
    c: Vertical(g39)
    c: Vertical(g41)
    c: Horizontal(g43)
    c: Parallel(g40,g12)
    c: PointOnObject(g44,g-2)
    c: PointOnObject(g44,g42)
    c: Tangent(g38,g45) = -1.5708
    c: Tangent(g36,g45) = 1.5708
    c: Tangent(g40,g46) = 1.5708
    c: Tangent(g36,g46) = 1.5708
    c: Tangent(g41,g47) = 1.5708
    c: Tangent(g40,g47) = 1.5708
    c: Tangent(g39,g48) = -1.5708
    c: Tangent(g38,g48) = -1.5708
    c: Tangent(g42,g49) = -1.5708
    c: Tangent(g41,g49) = 1.5708
    c: Tangent(g42,g50) = -1.5708
    c: Tangent(g39,g50) = -1.5708
    c: Coincident(g43,g39)
    c: Coincident(g43,g41)
    c: Equal(g15,g46)
    c: Equal(g46,g45)
    c: Symmetric(g36,g36,g37)
    c: Equal(g31,g47)
    c: Equal(g26,g49)
    c: Equal(g50,g29)
    c: Equal(g48,g32)
    c: DistanceY(g20,g44) = 14
    c: DistanceX(g41,g22) = 14
    c: PointOnObject(g51,g38)
    c: Perpendicular(g38,g51)
    c: Distance(g51) = 14
    c: Coincident(g51,g10)
    c: Vertical(g52)
    c: Coincident(g53,g52)
    c: Horizontal(g53)
    c: Coincident(g54,g53)
    c: Vertical(g54)
    c: Coincident(g55,g52)
    c: Horizontal(g55)
    c: DistanceY(g-1,g52) = 2
    c: DistanceY(g52,g-1) = 87
    c: Coincident(g54,g56)
    c: Coincident(g57,g54)
    c: Vertical(g57)
    c: PointOnObject(g56,g-2)
    c: PointOnObject(g58,g42)
    c: DistanceX(g-1,g58) = 43
    c: Coincident(g59,g58)
    c: Coincident(g60,g58)
    c: PointOnObject(g60,g56)
    c: Parallel(g60,g59)
    c: Perpendicular(g56,g60)
    c: Distance(g60) = 1.6
    c: DistanceX(g52,g-1) = 2
    c: Coincident(g61,g56)
    c: PointOnObject(g61,g-2)
    c: Vertical(g62)
    c: Coincident(g62,g55)
    c: PointOnObject(g55,g41)
    c: Vertical(g63)
    c: Vertical(g64)
    c: Equal(g64,g63)
    c: DistanceX(g63,g58) = 6.35
    c: DistanceX(g58,g64) = 6.35
    c: PointOnObject(g61,g42)
    c: DistanceY(g64,g64) = 2.2
    c: Coincident(g65,g63)
    c: Coincident(g67,g64)
    c: Coincident(g69,g68)
    c: Coincident(g69,g66)
    c: Tangent(g65,g70) = 1.5708
    c: Tangent(g66,g70) = 1.5708
    c: Tangent(g67,g71) = -1.5708
    c: Tangent(g68,g71) = -1.5708
    c: Coincident(g72,g63)
    c: Coincident(g72,g66)
    c: PointOnObject(g73,g70)
    c: PointOnObject(g74,g71)
    c: Coincident(g75,g64)
    c: Coincident(g75,g68)
    c: Vertical(g75)
    c: Coincident(g76,g74)
    c: PointOnObject(g76,g75)
    c: Horizontal(g76)
    c: PointOnObject(g71,g76)
    c: Equal(g67,g68)
    c: Equal(g68,g66)
    c: Equal(g65,g66)
    c: Equal(g71,g70)
    c: Vertical(g72)
    c: PointOnObject(g77,g72)
    c: Coincident(g77,g73)
    c: Horizontal(g77)
    c: PointOnObject(g70,g77)
    c: Angle(g65,g66) = 1.5708
    c: Angle(g68,g67) = 1.5708
    c: DistanceX(g76,g74) = 0.8
    c: Diameter(g71) = 0.8
    c: Coincident(g42,g7)
    c: DistanceX(g25,g39) = 14
    c: Coincident(g59,g7)
    c: Coincident(g57,g62)
    c: PointOnObject(g63,g42)
    c: PointOnObject(g64,g42)
    c: PointOnObject(g62,g42)
    c: Coincident(g78,g7)
    c: Coincident(g79,g78)
    c: Coincident(g79,g62)
    c: Coincident(g78,g61)
    c: PointOnObject(g78,g63)
    c: PointOnObject(g79,g64)
FEATURE [Sketcher::SketchObject] Sketch101  label="Sketch_Shell_Vert_CutPlug004"
  FullyConstrained = true
  MapMode = 5
  Placement = pos=(0,0,10) rot=(0,0,1;0rad)
  expr: Constraints[110] = <<params>>.xport_plug_plate_thick
  expr: Constraints[77] = <<params>>.back_vert_edge
  expr: Constraints[137] = <<params>>.shell_wall_thick + <<params>>.std_tol_clear
  expr: Constraints[134] = <<params>>.xport_plug_diam / 2
  expr: Constraints[47] = <<params>>.front_diameter
  expr: Constraints[170] = <<params>>.xport_clip_size
  expr: Constraints[63] = <<params>>.std_rad
  expr: Constraints[103] = <<params>>.xport_offset_loc
  expr: Constraints[101] = <<params>>.plate_length / 2 + <<params>>.std_wall_thick
  expr: Constraints[80] = <<params>>.std_rad
  expr: Constraints[36] = <<params>>.wheel_well_plate_width
  expr: Constraints[40] = <<params>>.plate_length
  expr: Constraints[65] = <<params>>.std_rad
  expr: Constraints[78] = <<params>>.wheel_well_clearance
  expr: Constraints[42] = <<params>>.tail_width
  expr: Constraints[135] = <<params>>.xport_plug_diam / 2
  expr: Constraints[79] = <<params>>.plate_width
  expr: Constraints[76] = <<params>>.front_vert_edge
  expr: Constraints[118] = <<params>>.std_wall_thick
  expr: Constraints[100] = <<params>>.std_wall_thick
  expr: Constraints[81] = <<params>>.std_rad
  expr: Constraints[41] = <<params>>.tail_rad
  expr: Constraints[168] = <<params>>.xport_clip_size
  sketch-geometry (68):
    g0: LineSegment StartX=-57.5 StartY=17 StartZ=0 EndX=-57.5 EndY=-17 EndZ=0
    g1: LineSegment StartX=57.5 StartY=17 StartZ=0 EndX=57.5 EndY=-17 EndZ=0
    g2: LineSegment StartX=-57.5 StartY=0 StartZ=0 EndX=57.5 EndY=0 EndZ=0
    g3: LineSegment StartX=-64.5 StartY=-24 StartZ=0 EndX=64.5 EndY=-24 EndZ=0
    g4: LineSegment StartX=-64.5 StartY=24 StartZ=0 EndX=64.5 EndY=24 EndZ=0
    g5: LineSegment StartX=-64.5 StartY=-24 StartZ=0 EndX=-75.5 EndY=-24 EndZ=0
    g6: LineSegment StartX=64.5 StartY=-24 StartZ=0 EndX=75.5 EndY=-24 EndZ=0
    g7: ArcOfCircle CenterX=0 CenterY=52.6846 CenterZ=0 NormalX=0 NormalY=0 NormalZ=1 AngleXU=0 Radius=112.5 StartAngle=3.96017 EndAngle=5.4646
    g8: LineSegment StartX=-64.5 StartY=24 StartZ=0 EndX=-75.5 EndY=24 EndZ=0
    g9: LineSegment StartX=64.5 StartY=24 StartZ=0 EndX=75.5 EndY=24 EndZ=0
    g10: LineSegment StartX=-77.1162 StartY=42.1781 StartZ=0 EndX=-29.0404 EndY=108.13 EndZ=0
    g11: LineSegment StartX=-25 StartY=110.185 StartZ=0 EndX=25 EndY=110.185 EndZ=0
    g12: LineSegment StartX=29.0404 StartY=108.13 StartZ=0 EndX=77.1162 EndY=42.1781 EndZ=0
    g13: LineSegment StartX=0 StartY=0 StartZ=0 EndX=0 EndY=110.185 EndZ=0
    g14: ArcOfCircle CenterX=-25 CenterY=105.185 CenterZ=0 NormalX=0 NormalY=0 NormalZ=1 AngleXU=0 Radius=5 StartAngle=1.5708 EndAngle=2.5117
    g15: ArcOfCircle CenterX=25 CenterY=105.185 CenterZ=0 NormalX=0 NormalY=0 NormalZ=1 AngleXU=0 Radius=5 StartAngle=0.629894 EndAngle=1.5708
    g16: ArcOfCircle CenterX=-64.5 CenterY=17 CenterZ=0 NormalX=0 NormalY=0 NormalZ=1 AngleXU=0 Radius=7 StartAngle=0 EndAngle=1.5708
    g17: ArcOfCircle CenterX=-64.5 CenterY=-17 CenterZ=0 NormalX=0 NormalY=0 NormalZ=1 AngleXU=0 Radius=7 StartAngle=4.71239 EndAngle=6.28319
    g18: ArcOfCircle CenterX=64.5 CenterY=-17 CenterZ=0 NormalX=0 NormalY=0 NormalZ=1 AngleXU=0 Radius=7 StartAngle=3.14159 EndAngle=4.71239
    g19: ArcOfCircle CenterX=64.5 CenterY=17 CenterZ=0 NormalX=0 NormalY=0 NormalZ=1 AngleXU=0 Radius=7 StartAngle=1.5708 EndAngle=3.14159
    g20: GeomPoint X=0 Y=-59.8154 Z=0
    g21: Circle CenterX=0 CenterY=52.6846 CenterZ=0 NormalX=0 NormalY=0 NormalZ=1 AngleXU=0 Radius=112.5
    g22: LineSegment StartX=77.5 StartY=26 StartZ=0 EndX=77.5 EndY=41 EndZ=0
    g23: LineSegment StartX=77.5 StartY=-26 StartZ=0 EndX=77.5 EndY=-28 EndZ=0
    g24: LineSegment StartX=-77.5 StartY=-28 StartZ=0 EndX=-77.5 EndY=-26 EndZ=0
    g25: LineSegment StartX=-77.5 StartY=26 StartZ=0 EndX=-77.5 EndY=41 EndZ=0
    g26: ArcOfCircle CenterX=75.5 CenterY=-28 CenterZ=0 NormalX=0 NormalY=0 NormalZ=1 AngleXU=0 Radius=2 StartAngle=5.4646 EndAngle=6.28319
    g27: ArcOfCircle CenterX=75.5 CenterY=-26 CenterZ=0 NormalX=0 NormalY=0 NormalZ=1 AngleXU=0 Radius=2 StartAngle=0 EndAngle=1.5708
    g28: ArcOfCircle CenterX=-75.5 CenterY=-28 CenterZ=0 NormalX=0 NormalY=0 NormalZ=1 AngleXU=0 Radius=2 StartAngle=3.14159 EndAngle=3.96017
    g29: ArcOfCircle CenterX=-75.5 CenterY=-26 CenterZ=0 NormalX=0 NormalY=0 NormalZ=1 AngleXU=0 Radius=2 StartAngle=1.5708 EndAngle=3.14159
    g30: ArcOfCircle CenterX=75.5 CenterY=26 CenterZ=0 NormalX=0 NormalY=0 NormalZ=1 AngleXU=0 Radius=2 StartAngle=4.71239 EndAngle=6.28319
    g31: ArcOfCircle CenterX=75.5 CenterY=41 CenterZ=0 NormalX=0 NormalY=0 NormalZ=1 AngleXU=0 Radius=2 StartAngle=4e-16 EndAngle=0.629894
    g32: ArcOfCircle CenterX=-75.5 CenterY=26 CenterZ=0 NormalX=0 NormalY=0 NormalZ=1 AngleXU=0 Radius=2 StartAngle=3.14159 EndAngle=4.71239
    g33: ArcOfCircle CenterX=-75.5 CenterY=41 CenterZ=0 NormalX=0 NormalY=0 NormalZ=1 AngleXU=0 Radius=2 StartAngle=2.5117 EndAngle=3.14159
    g34: LineSegment StartX=77.5 StartY=26 StartZ=0 EndX=77.5 EndY=-26 EndZ=0
    g35: LineSegment StartX=-77.5 StartY=26 StartZ=0 EndX=-77.5 EndY=-26 EndZ=0
    g36: LineSegment StartX=77.5 StartY=41 StartZ=0 EndX=77.5 EndY=-28 EndZ=0
    g37: LineSegment StartX=-77.5 StartY=41 StartZ=0 EndX=-77.5 EndY=-28 EndZ=0
    g38: ArcOfCircle CenterX=0 CenterY=52.6846 CenterZ=0 NormalX=0 NormalY=0 NormalZ=1 AngleXU=0 Radius=112.5 StartAngle=4.71239 EndAngle=5.4646
    g39: LineSegment StartX=-2 StartY=2 StartZ=0 EndX=-2 EndY=-87 EndZ=0
    g40: LineSegment StartX=76.8665 StartY=-38.9967 StartZ=0 EndX=76.8665 EndY=-87 EndZ=0
    g41: LineSegment StartX=-2 StartY=-87 StartZ=0 EndX=76.8665 EndY=-87 EndZ=0
    g42: LineSegment StartX=-2 StartY=2 StartZ=0 EndX=77.5 EndY=2 EndZ=0
    g43: LineSegment StartX=0 StartY=-70.7909 StartZ=0 EndX=76.8665 EndY=-38.9967 EndZ=0
    g44: GeomPoint X=43 Y=-51.2734 Z=0
    g45: LineSegment StartX=0 StartY=52.6846 StartZ=0 EndX=43 EndY=-51.2734 EndZ=0
    g46: LineSegment StartX=43.6116 StartY=-52.7519 StartZ=0 EndX=43 EndY=-51.2734 EndZ=0
    g47: LineSegment StartX=76.8665 StartY=-38.9967 StartZ=0 EndX=76.8665 EndY=-29.4604 EndZ=0
    g48: LineSegment StartX=-2.07e-14 StartY=-59.8154 StartZ=0 EndX=0 EndY=-70.7909 EndZ=0
    g49: LineSegment StartX=0 StartY=-70.7909 StartZ=0 EndX=-2.07e-14 EndY=-59.8154 EndZ=0
    g50: LineSegment StartX=77.5 StartY=2 StartZ=0 EndX=77.5 EndY=-28.863 EndZ=0
    g51: ArcOfCircle CenterX=0 CenterY=52.6846 CenterZ=0 NormalX=0 NormalY=0 NormalZ=1 AngleXU=0 Radius=112.5 StartAngle=4.71239 EndAngle=5.04422
    g52: ArcOfCircle CenterX=0 CenterY=52.6846 CenterZ=0 NormalX=0 NormalY=0 NormalZ=1 AngleXU=0 Radius=112.5 StartAngle=5.1665 EndAngle=5.47234
    g53: LineSegment StartX=36.65 StartY=-53.6781 StartZ=0 EndX=36.65 EndY=-51.3781 EndZ=0
    g54: LineSegment StartX=49.35 StartY=-48.4135 StartZ=0 EndX=49.35 EndY=-46.1135 EndZ=0
    g55: LineSegment StartX=36.65 StartY=-51.3781 StartZ=0 EndX=35.9672 EndY=-50.6953 EndZ=0
    g56: LineSegment StartX=35.9672 StartY=-50.1296 StartZ=0 EndX=36.65 EndY=-49.4468 EndZ=0
    g57: ArcOfCircle CenterX=36.25 CenterY=-50.4125 CenterZ=0 NormalX=0 NormalY=0 NormalZ=1 AngleXU=0 Radius=0.4 StartAngle=2.35619 EndAngle=3.92699
    g58: LineSegment StartX=49.35 StartY=-46.1135 StartZ=0 EndX=50.0328 EndY=-45.4307 EndZ=0
    g59: LineSegment StartX=50.0328 StartY=-44.865 StartZ=0 EndX=49.35 EndY=-44.1822 EndZ=0
    g60: ArcOfCircle CenterX=49.75 CenterY=-45.1479 CenterZ=0 NormalX=0 NormalY=0 NormalZ=1 AngleXU=0 Radius=0.4 StartAngle=5.49779 EndAngle=7.06858
    g61: LineSegment StartX=36.65 StartY=-51.3781 StartZ=0 EndX=36.65 EndY=-49.4468 EndZ=0
    g62: LineSegment StartX=49.35 StartY=-46.1135 StartZ=0 EndX=49.35 EndY=-44.1822 EndZ=0
    g63: LineSegment StartX=36.65 StartY=-49.4468 StartZ=0 EndX=49.35 EndY=-44.1822 EndZ=0
    g64: GeomPoint X=50.15 Y=-45.1479 Z=0
    g65: GeomPoint X=35.85 Y=-50.4125 Z=0
    g66: LineSegment StartX=35.85 StartY=-50.4125 StartZ=0 EndX=36.65 EndY=-50.4125 EndZ=0
    g67: LineSegment StartX=50.15 StartY=-45.1479 StartZ=0 EndX=49.35 EndY=-45.1479 EndZ=0
  constraints (171):
    c: Vertical(g0)
    c: Vertical(g1)
    c: Horizontal(g2)
    c: Symmetric(g2,g2,g-1)
    c: Horizontal(g3)
    c: Horizontal(g5)
    c: Horizontal(g6)
    c: PointOnObject(g7,g-2)
    c: Horizontal(g8)
    c: Horizontal(g9)
    c: Horizontal(g11)
    c: Coincident(g13,g-1)
    c: PointOnObject(g13,g-2)
    c: Tangent(g10,g14) = 1.5708
    c: Tangent(g11,g14) = 1.5708
    c: Tangent(g11,g15) = 1.5708
    c: Tangent(g12,g15) = 1.5708
    c: Tangent(g8,g16) = -1.5708
    c: Tangent(g0,g16) = 1.5708
    c: Tangent(g5,g17) = 1.5708
    c: Tangent(g0,g17) = 1.5708
    c: Tangent(g1,g18) = -1.5708
    c: Tangent(g6,g18) = -1.5708
    c: Tangent(g1,g19) = -1.5708
    c: Tangent(g9,g19) = 1.5708
    c: Equal(g15,g14)
    c: Symmetric(g11,g11,g13)
    c: Equal(g18,g19)
    c: Equal(g19,g16)
    c: Equal(g16,g17)
    c: PointOnObject(g20,g-2)
    c: PointOnObject(g20,g7)
    c: Coincident(g4,g8)
    c: Coincident(g4,g9)
    c: Coincident(g3,g6)
    c: Coincident(g3,g5)
    c: DistanceX(g2,g2) = 115
    c: Symmetric(g0,g0,g2)
    c: Symmetric(g1,g1,g2)
    c: Radius(g19) = 7
    c: DistanceY(g20,g11) = 170
    c: Radius(g15) = 5
    c: DistanceX(g11,g11) = 50
    c: Equal(g9,g8)
    c: Equal(g9,g6)
    c: Coincident(g21,g7)
    c: PointOnObject(g20,g21)
    c: Diameter(g21) = 225
    c: Vertical(g22)
    c: Vertical(g23)
    c: Vertical(g24)
    c: Vertical(g25)
    c: Equal(g5,g8)
    c: Equal(g10,g12)
    c: Tangent(g7,g26) = -1.5708
    c: Tangent(g23,g26) = 1.5708
    c: Tangent(g23,g27) = 1.5708
    c: Tangent(g6,g27) = 1.5708
    c: Tangent(g7,g28) = -1.5708
    c: Tangent(g24,g28) = 1.5708
    c: Tangent(g24,g29) = 1.5708
    c: Tangent(g5,g29) = -1.5708
    c: Equal(g29,g27)
    c: Radius(g27) = 2
    c: Equal(g26,g28)
    c: Radius(g26) = 2
    c: Tangent(g9,g30) = -1.5708
    c: Tangent(g22,g30) = -1.5708
    c: Tangent(g22,g31) = -1.5708
    c: Tangent(g12,g31) = 1.5708
    c: Tangent(g8,g32) = 1.5708
    c: Tangent(g25,g32) = 1.5708
    c: Tangent(g10,g33) = 1.5708
    c: Tangent(g25,g33) = 1.5708
    c: Equal(g30,g32)
    c: Equal(g31,g33)
    c: DistanceY(g23,g23) = 2
    c: DistanceY(g22,g22) = 15
    c: DistanceY(g6,g9) = 48
    c: DistanceX(g24,g23) = 155
    c: Radius(g30) = 2
    c: Radius(g31) = 2
    c: Coincident(g34,g22)
    c: Coincident(g34,g23)
    c: Coincident(g35,g25)
    c: Coincident(g35,g24)
    c: Coincident(g37,g28)
    c: Coincident(g37,g33)
    c: Coincident(g36,g31)
    c: Coincident(g36,g26)
    c: Coincident(g38,g7)
    c: PointOnObject(g38,g-2)
    c: Coincident(g38,g7)
    c: Vertical(g39)
    c: Vertical(g40)
    c: Coincident(g41,g39)
    c: Coincident(g41,g40)
    c: Horizontal(g41)
    c: Coincident(g42,g39)
    c: Horizontal(g42)
    c: DistanceY(g-1,g39) = 2
    c: DistanceY(g39,g-1) = 87
    c: PointOnObject(g44,g38)
    c: DistanceX(g-1,g44) = 43
    c: Coincident(g45,g44)
    c: Coincident(g45,g38)
    c: Coincident(g46,g44)
    c: PointOnObject(g46,g43)
    c: Parallel(g45,g46)
    c: Perpendicular(g46,g43)
    c: Distance(g46) = 1.6
    c: PointOnObject(g43,g-2)
    c: Coincident(g40,g43)
    c: Coincident(g47,g40)
    c: Coincident(g47,g38)
    c: Vertical(g47)
    c: Coincident(g48,g38)
    c: Coincident(g48,g43)
    c: DistanceX(g39,g43) = 2
    c: Coincident(g49,g43)
    c: PointOnObject(g49,g-2)
    c: PointOnObject(g42,g34)
    c: PointOnObject(g50,g34)
    c: Coincident(g50,g42)
    c: PointOnObject(g51,g13)
    c: Coincident(g51,g49)
    c: Coincident(g52,g51)
    c: Coincident(g52,g50)
    c: Coincident(g53,g51)
    c: Vertical(g53)
    c: Coincident(g54,g52)
    c: Vertical(g54)
    c: Equal(g51,g7)
    c: Equal(g52,g21)
    c: DistanceX(g51,g44) = 6.35
    c: DistanceX(g44,g52) = 6.35
    c: Equal(g54,g53)
    c: DistanceY(g54,g54) = 2.3
    c: PointOnObject(g49,g7)
    c: Coincident(g55,g53)
    c: Tangent(g55,g57) = 1.5708
    c: Tangent(g56,g57) = 1.5708
    c: Coincident(g58,g54)
    c: Tangent(g58,g60) = -1.5708
    c: Tangent(g59,g60) = -1.5708
    c: Coincident(g61,g53)
    c: Coincident(g61,g56)
    c: Vertical(g61)
    c: Coincident(g62,g54)
    c: Coincident(g62,g59)
    c: Vertical(g62)
    c: Equal(g58,g59)
    c: Equal(g55,g56)
    c: Equal(g60,g57)
    c: Coincident(g63,g56)
    c: Coincident(g63,g59)
    c: Angle(g59,g58) = 1.5708
    c: Angle(g55,g56) = 1.5708
    c: PointOnObject(g64,g60)
    c: PointOnObject(g65,g57)
    c: Coincident(g66,g65)
    c: PointOnObject(g66,g61)
    c: Horizontal(g66)
    c: PointOnObject(g57,g66)
    c: Coincident(g67,g64)
    c: PointOnObject(g67,g62)
    c: Horizontal(g67)
    c: PointOnObject(g60,g67)
    c: DistanceX(g67,g64) = 0.8
    c: Equal(g67,g66)
    c: Diameter(g60) = 0.8
FEATURE [Sketcher::SketchObject] Sketch102  label="Sketch_ClipsToTrim005"
  FullyConstrained = true
  MapMode = 5
  Placement = pos=(0,0,0) rot=(1,0,0;1.5708rad)
  Support = -> [XZ_Plane006]
  expr: Constraints[15] = <<params>>.std_wall_thick
  expr: Constraints[2] = <<params>>.xport_height_loc
  expr: Constraints[1] = <<params>>.xport_offset_loc
  expr: Constraints[0] = <<params>>.xport_plug_diam + 4 * <<params>>.xport_clip_size
  expr: Constraints[34] = <<params>>.std_wall_thick
  sketch-geometry (11):
    g0: Circle CenterX=43 CenterY=33.25 CenterZ=0 NormalX=0 NormalY=0 NormalZ=1 AngleXU=0 Radius=7.95
    g1: LineSegment StartX=35.1131 StartY=34.25 StartZ=0 EndX=50.8869 EndY=34.25 EndZ=0
    g2: LineSegment StartX=35.1131 StartY=32.25 StartZ=0 EndX=50.8869 EndY=32.25 EndZ=0
    g3: ArcOfCircle CenterX=43 CenterY=33.25 CenterZ=0 NormalX=0 NormalY=0 NormalZ=1 AngleXU=0 Radius=7.95 StartAngle=3.01547 EndAngle=3.26771
    g4: ArcOfCircle CenterX=43 CenterY=33.25 CenterZ=0 NormalX=0 NormalY=0 NormalZ=1 AngleXU=0 Radius=7.95 StartAngle=6.15707 EndAngle=6.40931
    g5: LineSegment StartX=35.1131 StartY=32.25 StartZ=0 EndX=42 EndY=32.25 EndZ=0
    g6: LineSegment StartX=44 StartY=32.25 StartZ=0 EndX=50.8869 EndY=32.25 EndZ=0
    g7: LineSegment StartX=43 StartY=33.25 StartZ=0 EndX=43 EndY=32.25 EndZ=0
    g8: LineSegment StartX=42 StartY=32.25 StartZ=0 EndX=42 EndY=25.3631 EndZ=0
    g9: LineSegment StartX=44 StartY=32.25 StartZ=0 EndX=44 EndY=25.3631 EndZ=0
    g10: ArcOfCircle CenterX=43 CenterY=33.25 CenterZ=0 NormalX=0 NormalY=0 NormalZ=1 AngleXU=0 Radius=7.95 StartAngle=4.58627 EndAngle=4.83851
  constraints (35):
    c: Diameter(g0) = 15.9
    c: DistanceX(g-1,g0) = 43
    c: DistanceY(g-1,g0) = 33.25
    c: PointOnObject(g1,g0)
    c: PointOnObject(g1,g0)
    c: Horizontal(g1)
    c: PointOnObject(g2,g0)
    c: Horizontal(g2)
    c: Symmetric(g1,g2,g0)
    c: Coincident(g3,g0)
    c: Coincident(g4,g3)
    c: Coincident(g3,g1)
    c: Coincident(g4,g1)
    c: PointOnObject(g4,g2)
    c: PointOnObject(g3,g2)
    c: DistanceY(g2,g1) = 2
    c: Horizontal(g5)
    c: Horizontal(g6)
    c: Coincident(g7,g3)
    c: PointOnObject(g7,g2)
    c: Vertical(g7)
    c: Symmetric(g5,g6,g7)
    c: PointOnObject(g5,g2)
    c: PointOnObject(g5,g0)
    c: PointOnObject(g6,g0)
    c: Coincident(g8,g5)
    c: PointOnObject(g8,g0)
    c: Vertical(g8)
    c: Coincident(g9,g6)
    c: Vertical(g9)
    c: PointOnObject(g9,g0)
    c: Coincident(g10,g3)
    c: Coincident(g10,g8)
    c: PointOnObject(g10,g9)
    c: DistanceX(g8,g9) = 2
FEATURE [Sketcher::SketchObject] Sketch103  label="Sketch_SplitPlug_P2_009"
  FullyConstrained = true
  MapMode = 5
  Placement = pos=(0,0,0) rot=(1,0,0;1.5708rad)
  Support = -> [XZ_Plane006]
  expr: Constraints[15] = <<params>>.std_wall_thick
  expr: Constraints[0] = <<params>>.xport_plug_diam + 4 * <<params>>.xport_clip_size
  expr: Constraints[1] = <<params>>.xport_offset_loc
  expr: Constraints[2] = <<params>>.xport_height_loc
  sketch-geometry (5):
    g0: Circle CenterX=43 CenterY=33.25 CenterZ=0 NormalX=0 NormalY=0 NormalZ=1 AngleXU=0 Radius=7.95
    g1: LineSegment StartX=35.1131 StartY=34.25 StartZ=0 EndX=50.8869 EndY=34.25 EndZ=0
    g2: LineSegment StartX=35.1131 StartY=32.25 StartZ=0 EndX=50.8869 EndY=32.25 EndZ=0
    g3: ArcOfCircle CenterX=43 CenterY=33.25 CenterZ=0 NormalX=0 NormalY=0 NormalZ=1 AngleXU=0 Radius=7.95 StartAngle=0.12612 EndAngle=3.01547
    g4: ArcOfCircle CenterX=43 CenterY=33.25 CenterZ=0 NormalX=0 NormalY=0 NormalZ=1 AngleXU=0 Radius=7.95 StartAngle=3.26771 EndAngle=6.15707
  constraints (16):
    c: Diameter(g0) = 15.9
    c: DistanceX(g-1,g0) = 43
    c: DistanceY(g-1,g0) = 33.25
    c: PointOnObject(g1,g0)
    c: PointOnObject(g1,g0)
    c: Horizontal(g1)
    c: PointOnObject(g2,g0)
    c: Horizontal(g2)
    c: Coincident(g3,g0)
    c: Coincident(g4,g3)
    c: Coincident(g3,g1)
    c: PointOnObject(g3,g1)
    c: Coincident(g4,g2)
    c: PointOnObject(g4,g2)
    c: Symmetric(g1,g2,g3)
    c: DistanceY(g2,g1) = 2
FEATURE [Sketcher::SketchObject] Sketch104  label="Sketch_SplitPlug_P3_009"
  FullyConstrained = true
  MapMode = 5
  Placement = pos=(0,0,0) rot=(1,0,0;1.5708rad)
  Support = -> [XZ_Plane006]
  expr: Constraints[15] = <<params>>.std_wall_thick
  expr: Constraints[0] = <<params>>.xport_plug_diam + 4 * <<params>>.xport_clip_size
  expr: Constraints[1] = <<params>>.xport_offset_loc
  expr: Constraints[2] = <<params>>.xport_height_loc
  sketch-geometry (8):
    g0: Circle CenterX=43 CenterY=33.25 CenterZ=0 NormalX=0 NormalY=0 NormalZ=1 AngleXU=0 Radius=7.95
    g1: LineSegment StartX=35.1131 StartY=34.25 StartZ=0 EndX=50.8869 EndY=34.25 EndZ=0
    g2: LineSegment StartX=35.1131 StartY=32.25 StartZ=0 EndX=50.8869 EndY=32.25 EndZ=0
    g3: ArcOfCircle CenterX=43 CenterY=33.25 CenterZ=0 NormalX=0 NormalY=0 NormalZ=1 AngleXU=0 Radius=7.95 StartAngle=0.12612 EndAngle=3.01547
    g4: ArcOfCircle CenterX=43 CenterY=33.25 CenterZ=0 NormalX=0 NormalY=0 NormalZ=1 AngleXU=0 Radius=7.95 StartAngle=3.26771 EndAngle=6.15707
    g5: ArcOfCircle CenterX=43 CenterY=33.25 CenterZ=0 NormalX=0 NormalY=0 NormalZ=1 AngleXU=0 Radius=7.95 StartAngle=1.5708 EndAngle=3.26771
    g6: LineSegment StartX=43 StartY=32.25 StartZ=0 EndX=43 EndY=41.2 EndZ=0
    g7: LineSegment StartX=43 StartY=32.25 StartZ=0 EndX=50.8869 EndY=32.25 EndZ=0
  constraints (26):
    c: Diameter(g0) = 15.9
    c: DistanceX(g-1,g0) = 43
    c: DistanceY(g-1,g0) = 33.25
    c: PointOnObject(g1,g0)
    c: PointOnObject(g1,g0)
    c: Horizontal(g1)
    c: PointOnObject(g2,g0)
    c: Horizontal(g2)
    c: Coincident(g3,g0)
    c: Coincident(g4,g3)
    c: Coincident(g3,g1)
    c: PointOnObject(g3,g1)
    c: Coincident(g4,g2)
    c: PointOnObject(g4,g2)
    c: Symmetric(g1,g2,g3)
    c: DistanceY(g2,g1) = 2
    c: Coincident(g5,g4)
    c: Coincident(g5,g4)
    c: PointOnObject(g6,g2)
    c: PointOnObject(g6,g3)
    c: Vertical(g6)
    c: PointOnObject(g4,g6)
    c: PointOnObject(g5,g6)
    c: Horizontal(g7)
    c: Coincident(g7,g6)
    c: PointOnObject(g7,g0)
FEATURE [Sketcher::SketchObject] Sketch105  label="Sketch_SplitPlug_P2_010"
  FullyConstrained = true
  MapMode = 5
  Placement = pos=(0,0,0) rot=(1,0,0;1.5708rad)
  Support = -> [XZ_Plane006]
  expr: Constraints[2] = <<params>>.xport_height_loc
  expr: Constraints[1] = <<params>>.xport_offset_loc
  expr: Constraints[0] = <<params>>.xport_plug_diam + 4 * <<params>>.xport_clip_size
  expr: Constraints[15] = <<params>>.std_wall_thick
  sketch-geometry (8):
    g0: Circle CenterX=43 CenterY=33.25 CenterZ=0 NormalX=0 NormalY=0 NormalZ=1 AngleXU=0 Radius=7.95
    g1: LineSegment StartX=35.1131 StartY=34.25 StartZ=0 EndX=50.8869 EndY=34.25 EndZ=0
    g2: LineSegment StartX=35.1131 StartY=32.25 StartZ=0 EndX=50.8869 EndY=32.25 EndZ=0
    g3: ArcOfCircle CenterX=43 CenterY=33.25 CenterZ=0 NormalX=0 NormalY=0 NormalZ=1 AngleXU=0 Radius=7.95 StartAngle=0.12612 EndAngle=3.01547
    g4: ArcOfCircle CenterX=43 CenterY=33.25 CenterZ=0 NormalX=0 NormalY=0 NormalZ=1 AngleXU=0 Radius=7.95 StartAngle=3.26771 EndAngle=6.15707
    g5: LineSegment StartX=35.1131 StartY=32.25 StartZ=0 EndX=43 EndY=32.25 EndZ=0
    g6: LineSegment StartX=43 StartY=32.25 StartZ=0 EndX=43 EndY=41.2 EndZ=0
    g7: ArcOfCircle CenterX=43 CenterY=33.25 CenterZ=0 NormalX=0 NormalY=0 NormalZ=1 AngleXU=0 Radius=7.95 StartAngle=6.15707 EndAngle=7.85398
  constraints (26):
    c: Diameter(g0) = 15.9
    c: DistanceX(g-1,g0) = 43
    c: DistanceY(g-1,g0) = 33.25
    c: PointOnObject(g1,g0)
    c: PointOnObject(g1,g0)
    c: Horizontal(g1)
    c: PointOnObject(g2,g0)
    c: Horizontal(g2)
    c: Coincident(g3,g0)
    c: Coincident(g4,g3)
    c: Coincident(g3,g1)
    c: PointOnObject(g3,g1)
    c: Coincident(g4,g2)
    c: PointOnObject(g4,g2)
    c: Symmetric(g1,g2,g3)
    c: DistanceY(g2,g1) = 2
    c: Horizontal(g5)
    c: PointOnObject(g6,g0)
    c: Vertical(g6)
    c: PointOnObject(g4,g6)
    c: Coincident(g6,g5)
    c: PointOnObject(g5,g2)
    c: PointOnObject(g5,g4)
    c: Coincident(g7,g4)
    c: Coincident(g7,g6)
    c: PointOnObject(g7,g2)
FEATURE [Sketcher::SketchObject] Sketch106  label="Sketch_SplitPlug_P1_005"
  FullyConstrained = true
  MapMode = 5
  Placement = pos=(0,0,0) rot=(1,0,0;1.5708rad)
  Support = -> [XZ_Plane006]
  expr: Constraints[0] = <<params>>.xport_plug_diam + 4 * <<params>>.xport_clip_size
  expr: Constraints[1] = <<params>>.xport_offset_loc
  expr: Constraints[2] = <<params>>.xport_height_loc
  expr: Constraints[6] = <<params>>.std_wall_thick / 2 + <<params>>.std_min_wall_thick
  sketch-geometry (3):
    g0: Circle CenterX=43 CenterY=33.25 CenterZ=0 NormalX=0 NormalY=0 NormalZ=1 AngleXU=0 Radius=7.95
    g1: LineSegment StartX=35.2565 StartY=35.05 StartZ=0 EndX=50.7435 EndY=35.05 EndZ=0
    g2: ArcOfCircle CenterX=43 CenterY=33.25 CenterZ=0 NormalX=0 NormalY=0 NormalZ=1 AngleXU=0 Radius=7.95 StartAngle=2.9132 EndAngle=6.51158
  constraints (10):
    c: Diameter(g0) = 15.9
    c: DistanceX(g-1,g0) = 43
    c: DistanceY(g-1,g0) = 33.25
    c: PointOnObject(g1,g0)
    c: PointOnObject(g1,g0)
    c: Horizontal(g1)
    c: DistanceY(g0,g1) = 1.8
    c: Coincident(g2,g0)
    c: Coincident(g2,g1)
    c: PointOnObject(g2,g1)
FEATURE [Sketcher::SketchObject] Sketch107  label="Sketch_SplitPlug_P3_010"
  FullyConstrained = true
  MapMode = 5
  Placement = pos=(0,0,0) rot=(1,0,0;1.5708rad)
  Support = -> [XZ_Plane006]
  expr: Constraints[2] = <<params>>.xport_height_loc
  expr: Constraints[1] = <<params>>.xport_offset_loc
  expr: Constraints[0] = <<params>>.xport_plug_diam + 4 * <<params>>.xport_clip_size
  expr: Constraints[15] = <<params>>.std_wall_thick
  sketch-geometry (5):
    g0: Circle CenterX=43 CenterY=33.25 CenterZ=0 NormalX=0 NormalY=0 NormalZ=1 AngleXU=0 Radius=7.95
    g1: LineSegment StartX=35.1131 StartY=34.25 StartZ=0 EndX=50.8869 EndY=34.25 EndZ=0
    g2: LineSegment StartX=35.1131 StartY=32.25 StartZ=0 EndX=50.8869 EndY=32.25 EndZ=0
    g3: ArcOfCircle CenterX=43 CenterY=33.25 CenterZ=0 NormalX=0 NormalY=0 NormalZ=1 AngleXU=0 Radius=7.95 StartAngle=0.12612 EndAngle=3.01547
    g4: ArcOfCircle CenterX=43 CenterY=33.25 CenterZ=0 NormalX=0 NormalY=0 NormalZ=1 AngleXU=0 Radius=7.95 StartAngle=3.26771 EndAngle=6.15707
  constraints (16):
    c: Diameter(g0) = 15.9
    c: DistanceX(g-1,g0) = 43
    c: DistanceY(g-1,g0) = 33.25
    c: PointOnObject(g1,g0)
    c: PointOnObject(g1,g0)
    c: Horizontal(g1)
    c: PointOnObject(g2,g0)
    c: Horizontal(g2)
    c: Coincident(g3,g0)
    c: Coincident(g4,g3)
    c: Coincident(g3,g1)
    c: PointOnObject(g3,g1)
    c: Coincident(g4,g2)
    c: PointOnObject(g4,g2)
    c: Symmetric(g1,g2,g3)
    c: DistanceY(g2,g1) = 2
FEATURE [Sketcher::SketchObject] Sketch108  label="Sketch_SplitPlug_P4_005"
  FullyConstrained = true
  MapMode = 5
  Placement = pos=(0,0,0) rot=(1,0,0;1.5708rad)
  Support = -> [XZ_Plane006]
  expr: Constraints[0] = <<params>>.xport_plug_diam + 4 * <<params>>.xport_clip_size
  expr: Constraints[1] = <<params>>.xport_offset_loc
  expr: Constraints[2] = <<params>>.xport_height_loc
  expr: Constraints[9] = <<params>>.std_wall_thick / 2 + <<params>>.std_min_wall_thick
  sketch-geometry (3):
    g0: Circle CenterX=43 CenterY=33.25 CenterZ=0 NormalX=0 NormalY=0 NormalZ=1 AngleXU=0 Radius=7.95
    g1: LineSegment StartX=35.2565 StartY=31.45 StartZ=0 EndX=50.7435 EndY=31.45 EndZ=0
    g2: ArcOfCircle CenterX=43 CenterY=33.25 CenterZ=0 NormalX=0 NormalY=0 NormalZ=1 AngleXU=0 Radius=7.95 StartAngle=6.05479 EndAngle=9.65317
  constraints (10):
    c: Diameter(g0) = 15.9
    c: DistanceX(g-1,g0) = 43
    c: DistanceY(g-1,g0) = 33.25
    c: PointOnObject(g1,g0)
    c: PointOnObject(g1,g0)
    c: Horizontal(g1)
    c: Coincident(g2,g0)
    c: Coincident(g2,g1)
    c: PointOnObject(g2,g1)
    c: DistanceY(g1,g2) = 1.8
FEATURE [Sketcher::SketchObject] Sketch109
  FullyConstrained = true
  MapMode = 5
  Placement = pos=(0,0,0) rot=(1,0,0;1.5708rad)
  Support = -> [XZ_Plane006]
  expr: Constraints[2] = <<params>>.xport_height_loc
  expr: Constraints[1] = <<params>>.xport_offset_loc
  expr: Constraints[0] = <<params>>.xport_plug_diam
  sketch-geometry (1):
    g0: Circle CenterX=43 CenterY=33.25 CenterZ=0 NormalX=0 NormalY=0 NormalZ=1 AngleXU=0 Radius=6.35
  constraints (3):
    c: Diameter(g0) = 12.7
    c: DistanceX(g-1,g0) = 43
    c: DistanceY(g-1,g0) = 33.25
FEATURE [PartDesign::Pad] Pad010  label="Pad_Plug004"
  Direction = (1,1,1)
  Length = 85
  Length2 = 100
  Placement = pos=(0,0,0) rot=(1,0,0;1.5708rad)
  Profile = -> Sketch109
  Type = 0
  expr: Length = <<params>>.plate_length / 2
FEATURE [PartDesign::Pad] Pad009  label="Pad_ClipsToTrim004"
  BaseFeature = -> Pad010
  Direction = (1,1,1)
  Length = 85
  Length2 = 100
  Placement = pos=(0,0,0) rot=(1,0,0;1.5708rad)
  Profile = -> Sketch102
  Type = 0
  expr: Length = <<params>>.plate_length / 2
FEATURE [PartDesign::Pocket] Pocket004  label="Pocket_HollowTube004"
  BaseFeature = -> Pad009
  Length = 5
  Length2 = 100
  Midplane = true
  Placement = pos=(0,0,0) rot=(1,0,0;1.5708rad)
  Profile = -> Sketch097
  Type = 1
FEATURE [PartDesign::SubtractiveLoft] SubtractiveLoft005  label="SubtractiveLoft_CutClips004"
  BaseFeature = -> Pocket004
  Closed = false
  Placement = pos=(0,0,0) rot=(1,0,0;1.5708rad)
  Profile = -> Sketch101
  Ruled = false
  Sections = -> [Sketch098]
FEATURE [PartDesign::Chamfer] Chamfer005  label="Chamfer_FrontEdge004"
  Angle = 45
  Base = -> SubtractiveLoft005 [Edge13,Edge17,Edge8]
  BaseFeature = -> SubtractiveLoft005
  ChamferType = 0
  FlipDirection = false
  Placement = pos=(0,0,0) rot=(1,0,0;1.5708rad)
  Size = 1
  Size2 = 1
  SupportTransform = false
FEATURE [PartDesign::Plane] DatumPlane018  label="Datum_ShellVert009"
  AttachmentOffset = pos=(0,0,10) rot=(0,0,1;0rad)
  Length = 88.617
  MapMode = 5
  Placement = pos=(0,0,10) rot=(0,0,1;0rad)
  ResizeMode = 0
  Support = -> [XY_Plane009]
  Width = 85.741
  expr: .AttachmentOffset.Base.z = <<params>>.shell_vertheight
FEATURE [Sketcher::SketchObject] Sketch099  label="Sketch_Shell_Vert007"
  FullyConstrained = true
  MapMode = 5
  Placement = pos=(0,0,10) rot=(0,0,1;0rad)
  Support = -> [DatumPlane018]
  expr: Constraints[40] = <<params>>.plate_length
  expr: Constraints[65] = <<params>>.std_rad
  expr: Constraints[42] = <<params>>.tail_width
  expr: Constraints[78] = <<params>>.wheel_well_clearance
  expr: Constraints[79] = <<params>>.plate_width
  expr: Constraints[36] = <<params>>.wheel_well_plate_width
  expr: Constraints[47] = <<params>>.front_diameter
  expr: Constraints[63] = <<params>>.std_rad
  expr: Constraints[76] = <<params>>.front_vert_edge
  expr: Constraints[77] = <<params>>.back_vert_edge
  expr: Constraints[80] = <<params>>.std_rad
  expr: Constraints[81] = <<params>>.std_rad
  expr: Constraints[41] = <<params>>.tail_rad
  sketch-geometry (38):
    g0: LineSegment StartX=-57.5 StartY=17 StartZ=0 EndX=-57.5 EndY=-17 EndZ=0
    g1: LineSegment StartX=57.5 StartY=17 StartZ=0 EndX=57.5 EndY=-17 EndZ=0
    g2: LineSegment StartX=-57.5 StartY=0 StartZ=0 EndX=57.5 EndY=0 EndZ=0
    g3: LineSegment StartX=-64.5 StartY=-24 StartZ=0 EndX=64.5 EndY=-24 EndZ=0
    g4: LineSegment StartX=-64.5 StartY=24 StartZ=0 EndX=64.5 EndY=24 EndZ=0
    g5: LineSegment StartX=-64.5 StartY=-24 StartZ=0 EndX=-75.5 EndY=-24 EndZ=0
    g6: LineSegment StartX=64.5 StartY=-24 StartZ=0 EndX=75.5 EndY=-24 EndZ=0
    g7: ArcOfCircle CenterX=0 CenterY=52.6846 CenterZ=0 NormalX=0 NormalY=0 NormalZ=1 AngleXU=0 Radius=112.5 StartAngle=3.96017 EndAngle=5.4646
    g8: LineSegment StartX=-64.5 StartY=24 StartZ=0 EndX=-75.5 EndY=24 EndZ=0
    g9: LineSegment StartX=64.5 StartY=24 StartZ=0 EndX=75.5 EndY=24 EndZ=0
    g10: LineSegment StartX=-77.1162 StartY=42.1781 StartZ=0 EndX=-29.0404 EndY=108.13 EndZ=0
    g11: LineSegment StartX=-25 StartY=110.185 StartZ=0 EndX=25 EndY=110.185 EndZ=0
    g12: LineSegment StartX=29.0404 StartY=108.13 StartZ=0 EndX=77.1162 EndY=42.1781 EndZ=0
    g13: LineSegment StartX=0 StartY=0 StartZ=0 EndX=0 EndY=110.185 EndZ=0
    g14: ArcOfCircle CenterX=-25 CenterY=105.185 CenterZ=0 NormalX=0 NormalY=0 NormalZ=1 AngleXU=0 Radius=5 StartAngle=1.5708 EndAngle=2.5117
    g15: ArcOfCircle CenterX=25 CenterY=105.185 CenterZ=0 NormalX=0 NormalY=0 NormalZ=1 AngleXU=0 Radius=5 StartAngle=0.629894 EndAngle=1.5708
    g16: ArcOfCircle CenterX=-64.5 CenterY=17 CenterZ=0 NormalX=0 NormalY=0 NormalZ=1 AngleXU=0 Radius=7 StartAngle=0 EndAngle=1.5708
    g17: ArcOfCircle CenterX=-64.5 CenterY=-17 CenterZ=0 NormalX=0 NormalY=0 NormalZ=1 AngleXU=0 Radius=7 StartAngle=4.71239 EndAngle=6.28319
    g18: ArcOfCircle CenterX=64.5 CenterY=-17 CenterZ=0 NormalX=0 NormalY=0 NormalZ=1 AngleXU=0 Radius=7 StartAngle=3.14159 EndAngle=4.71239
    g19: ArcOfCircle CenterX=64.5 CenterY=17 CenterZ=0 NormalX=0 NormalY=0 NormalZ=1 AngleXU=0 Radius=7 StartAngle=1.5708 EndAngle=3.14159
    g20: GeomPoint X=0 Y=-59.8154 Z=0
    g21: Circle CenterX=0 CenterY=52.6846 CenterZ=0 NormalX=0 NormalY=0 NormalZ=1 AngleXU=0 Radius=112.5
    g22: LineSegment StartX=77.5 StartY=26 StartZ=0 EndX=77.5 EndY=41 EndZ=0
    g23: LineSegment StartX=77.5 StartY=-26 StartZ=0 EndX=77.5 EndY=-28 EndZ=0
    g24: LineSegment StartX=-77.5 StartY=-28 StartZ=0 EndX=-77.5 EndY=-26 EndZ=0
    g25: LineSegment StartX=-77.5 StartY=26 StartZ=0 EndX=-77.5 EndY=41 EndZ=0
    g26: ArcOfCircle CenterX=75.5 CenterY=-28 CenterZ=0 NormalX=0 NormalY=0 NormalZ=1 AngleXU=0 Radius=2 StartAngle=5.4646 EndAngle=6.28319
    g27: ArcOfCircle CenterX=75.5 CenterY=-26 CenterZ=0 NormalX=0 NormalY=0 NormalZ=1 AngleXU=0 Radius=2 StartAngle=-9e-16 EndAngle=1.5708
    g28: ArcOfCircle CenterX=-75.5 CenterY=-28 CenterZ=0 NormalX=0 NormalY=0 NormalZ=1 AngleXU=0 Radius=2 StartAngle=3.14159 EndAngle=3.96017
    g29: ArcOfCircle CenterX=-75.5 CenterY=-26 CenterZ=0 NormalX=0 NormalY=0 NormalZ=1 AngleXU=0 Radius=2 StartAngle=1.5708 EndAngle=3.14159
    g30: ArcOfCircle CenterX=75.5 CenterY=26 CenterZ=0 NormalX=0 NormalY=0 NormalZ=1 AngleXU=0 Radius=2 StartAngle=4.71239 EndAngle=6.28319
    g31: ArcOfCircle CenterX=75.5 CenterY=41 CenterZ=0 NormalX=0 NormalY=0 NormalZ=1 AngleXU=0 Radius=2 StartAngle=0 EndAngle=0.629894
    g32: ArcOfCircle CenterX=-75.5 CenterY=26 CenterZ=0 NormalX=0 NormalY=0 NormalZ=1 AngleXU=0 Radius=2 StartAngle=3.14159 EndAngle=4.71239
    g33: ArcOfCircle CenterX=-75.5 CenterY=41 CenterZ=0 NormalX=0 NormalY=0 NormalZ=1 AngleXU=0 Radius=2 StartAngle=2.5117 EndAngle=3.14159
    g34: LineSegment StartX=77.5 StartY=26 StartZ=0 EndX=77.5 EndY=-26 EndZ=0
    g35: LineSegment StartX=-77.5 StartY=26 StartZ=0 EndX=-77.5 EndY=-26 EndZ=0
    g36: LineSegment StartX=77.5 StartY=41 StartZ=0 EndX=77.5 EndY=-28 EndZ=0
    g37: LineSegment StartX=-77.5 StartY=41 StartZ=0 EndX=-77.5 EndY=-28 EndZ=0
  constraints (90):
    c: Vertical(g0)
    c: Vertical(g1)
    c: Horizontal(g2)
    c: Symmetric(g2,g2,g-1)
    c: Horizontal(g3)
    c: Horizontal(g5)
    c: Horizontal(g6)
    c: PointOnObject(g7,g-2)
    c: Horizontal(g8)
    c: Horizontal(g9)
    c: Horizontal(g11)
    c: Coincident(g13,g-1)
    c: PointOnObject(g13,g-2)
    c: Tangent(g10,g14) = 1.5708
    c: Tangent(g11,g14) = 1.5708
    c: Tangent(g11,g15) = 1.5708
    c: Tangent(g12,g15) = 1.5708
    c: Tangent(g8,g16) = -1.5708
    c: Tangent(g0,g16) = 1.5708
    c: Tangent(g5,g17) = 1.5708
    c: Tangent(g0,g17) = 1.5708
    c: Tangent(g1,g18) = -1.5708
    c: Tangent(g6,g18) = -1.5708
    c: Tangent(g1,g19) = -1.5708
    c: Tangent(g9,g19) = 1.5708
    c: Equal(g15,g14)
    c: Symmetric(g11,g11,g13)
    c: Equal(g18,g19)
    c: Equal(g19,g16)
    c: Equal(g16,g17)
    c: PointOnObject(g20,g-2)
    c: PointOnObject(g20,g7)
    c: Coincident(g4,g8)
    c: Coincident(g4,g9)
    c: Coincident(g3,g6)
    c: Coincident(g3,g5)
    c: DistanceX(g2,g2) = 115
    c: Symmetric(g0,g0,g2)
    c: Symmetric(g1,g1,g2)
    c: Radius(g19) = 7
    c: DistanceY(g20,g11) = 170
    c: Radius(g15) = 5
    c: DistanceX(g11,g11) = 50
    c: Equal(g9,g8)
    c: Equal(g9,g6)
    c: Coincident(g21,g7)
    c: PointOnObject(g20,g21)
    c: Diameter(g21) = 225
    c: Vertical(g22)
    c: Vertical(g23)
    c: Vertical(g24)
    c: Vertical(g25)
    c: Equal(g5,g8)
    c: Equal(g10,g12)
    c: Tangent(g7,g26) = -1.5708
    c: Tangent(g23,g26) = 1.5708
    c: Tangent(g23,g27) = 1.5708
    c: Tangent(g6,g27) = 1.5708
    c: Tangent(g7,g28) = -1.5708
    c: Tangent(g24,g28) = 1.5708
    c: Tangent(g24,g29) = 1.5708
    c: Tangent(g5,g29) = -1.5708
    c: Equal(g29,g27)
    c: Radius(g27) = 2
    c: Equal(g26,g28)
    c: Radius(g26) = 2
    c: Tangent(g9,g30) = -1.5708
    c: Tangent(g22,g30) = -1.5708
    c: Tangent(g22,g31) = -1.5708
    c: Tangent(g12,g31) = 1.5708
    c: Tangent(g8,g32) = 1.5708
    c: Tangent(g25,g32) = 1.5708
    c: Tangent(g10,g33) = 1.5708
    c: Tangent(g25,g33) = 1.5708
    c: Equal(g30,g32)
    c: Equal(g31,g33)
    c: DistanceY(g23,g23) = 2
    c: DistanceY(g22,g22) = 15
    c: DistanceY(g6,g9) = 48
    c: DistanceX(g24,g23) = 155
    c: Radius(g30) = 2
    c: Radius(g31) = 2
    c: Coincident(g34,g22)
    c: Coincident(g34,g23)
    c: Coincident(g35,g25)
    c: Coincident(g35,g24)
    c: Coincident(g37,g28)
    c: Coincident(g37,g33)
    c: Coincident(g36,g31)
    c: Coincident(g36,g26)
FEATURE [PartDesign::Plane] DatumPlane019  label="Datum_ShellTot009"
  AttachmentOffset = pos=(0,0,42) rot=(0,0,1;0rad)
  Length = 88.617
  MapMode = 5
  Placement = pos=(0,0,42) rot=(0,0,1;0rad)
  ResizeMode = 0
  Support = -> [XY_Plane009]
  Width = 85.741
  expr: .AttachmentOffset.Base.z = <<params>>.shell_totheight
FEATURE [Sketcher::SketchObject] Sketch100  label="Sketch_Shell_Top007"
  FullyConstrained = true
  MapMode = 5
  Placement = pos=(0,0,42) rot=(0,0,1;0rad)
  Support = -> [DatumPlane019]
  expr: Constraints[41] = <<params>>.tail_rad
  expr: Constraints[76] = <<params>>.front_vert_edge
  expr: Constraints[47] = <<params>>.front_diameter
  expr: Constraints[36] = <<params>>.wheel_well_plate_width - 2 * Spreadsheet.shell_overhang_leng
  expr: Constraints[79] = <<params>>.plate_width
  expr: Constraints[42] = <<params>>.tail_width
  expr: Constraints[78] = <<params>>.wheel_well_clearance
  expr: Constraints[65] = <<params>>.std_rad
  expr: Constraints[40] = <<params>>.plate_length
  expr: Constraints[88] = Spreadsheet.shell_overhang_leng
  expr: Constraints[81] = <<params>>.std_rad
  expr: Constraints[63] = <<params>>.std_rad
  expr: Constraints[77] = <<params>>.back_vert_edge
  expr: Constraints[120] = Spreadsheet.shell_overhang_leng
  expr: Constraints[80] = <<params>>.std_rad
  expr: Constraints[119] = Spreadsheet.shell_overhang_leng
  expr: Constraints[123] = <<params>>.shell_overhang_leng
  sketch-geometry (52):
    g0: LineSegment StartX=-43.5 StartY=17 StartZ=0 EndX=-43.5 EndY=-17 EndZ=0
    g1: LineSegment StartX=43.5 StartY=17 StartZ=0 EndX=43.5 EndY=-17 EndZ=0
    g2: LineSegment StartX=-43.5 StartY=0 StartZ=0 EndX=43.5 EndY=0 EndZ=0
    g3: LineSegment StartX=-50.5 StartY=-24 StartZ=0 EndX=50.5 EndY=-24 EndZ=0
    g4: LineSegment StartX=-50.5 StartY=24 StartZ=0 EndX=50.5 EndY=24 EndZ=0
    g5: LineSegment StartX=-50.5 StartY=-24 StartZ=0 EndX=-75.5 EndY=-24 EndZ=0
    g6: LineSegment StartX=50.5 StartY=-24 StartZ=0 EndX=75.5 EndY=-24 EndZ=0
    g7: ArcOfCircle CenterX=0 CenterY=52.6846 CenterZ=0 NormalX=0 NormalY=0 NormalZ=1 AngleXU=0 Radius=112.5 StartAngle=3.96017 EndAngle=5.4646
    g8: LineSegment StartX=-50.5 StartY=24 StartZ=0 EndX=-75.5 EndY=24 EndZ=0
    g9: LineSegment StartX=50.5 StartY=24 StartZ=0 EndX=75.5 EndY=24 EndZ=0
    g10: LineSegment StartX=-77.1162 StartY=42.1781 StartZ=0 EndX=-29.0404 EndY=108.13 EndZ=0
    g11: LineSegment StartX=-25 StartY=110.185 StartZ=0 EndX=25 EndY=110.185 EndZ=0
    g12: LineSegment StartX=29.0404 StartY=108.13 StartZ=0 EndX=77.1162 EndY=42.1781 EndZ=0
    g13: LineSegment StartX=0 StartY=0 StartZ=0 EndX=0 EndY=110.185 EndZ=0
    g14: ArcOfCircle CenterX=-25 CenterY=105.185 CenterZ=0 NormalX=0 NormalY=0 NormalZ=1 AngleXU=0 Radius=5 StartAngle=1.5708 EndAngle=2.5117
    g15: ArcOfCircle CenterX=25 CenterY=105.185 CenterZ=0 NormalX=0 NormalY=0 NormalZ=1 AngleXU=0 Radius=5 StartAngle=0.629894 EndAngle=1.5708
    g16: ArcOfCircle CenterX=-50.5 CenterY=17 CenterZ=0 NormalX=0 NormalY=0 NormalZ=1 AngleXU=0 Radius=7 StartAngle=0 EndAngle=1.5708
    g17: ArcOfCircle CenterX=-50.5 CenterY=-17 CenterZ=0 NormalX=0 NormalY=0 NormalZ=1 AngleXU=0 Radius=7 StartAngle=4.71239 EndAngle=6.28319
    g18: ArcOfCircle CenterX=50.5 CenterY=-17 CenterZ=0 NormalX=0 NormalY=0 NormalZ=1 AngleXU=0 Radius=7 StartAngle=3.14159 EndAngle=4.71239
    g19: ArcOfCircle CenterX=50.5 CenterY=17 CenterZ=0 NormalX=0 NormalY=0 NormalZ=1 AngleXU=0 Radius=7 StartAngle=1.5708 EndAngle=3.14159
    g20: GeomPoint X=0 Y=-59.8154 Z=0
    g21: Circle CenterX=0 CenterY=52.6846 CenterZ=0 NormalX=0 NormalY=0 NormalZ=1 AngleXU=0 Radius=112.5
    g22: LineSegment StartX=77.5 StartY=26 StartZ=0 EndX=77.5 EndY=41 EndZ=0
    g23: LineSegment StartX=77.5 StartY=-26 StartZ=0 EndX=77.5 EndY=-28 EndZ=0
    g24: LineSegment StartX=-77.5 StartY=-28 StartZ=0 EndX=-77.5 EndY=-26 EndZ=0
    g25: LineSegment StartX=-77.5 StartY=26 StartZ=0 EndX=-77.5 EndY=41 EndZ=0
    g26: ArcOfCircle CenterX=75.5 CenterY=-28 CenterZ=0 NormalX=0 NormalY=0 NormalZ=1 AngleXU=0 Radius=2 StartAngle=5.4646 EndAngle=6.28319
    g27: ArcOfCircle CenterX=75.5 CenterY=-26 CenterZ=0 NormalX=0 NormalY=0 NormalZ=1 AngleXU=0 Radius=2 StartAngle=0 EndAngle=1.5708
    g28: ArcOfCircle CenterX=-75.5 CenterY=-28 CenterZ=0 NormalX=0 NormalY=0 NormalZ=1 AngleXU=0 Radius=2 StartAngle=3.14159 EndAngle=3.96017
    g29: ArcOfCircle CenterX=-75.5 CenterY=-26 CenterZ=0 NormalX=0 NormalY=0 NormalZ=1 AngleXU=0 Radius=2 StartAngle=1.5708 EndAngle=3.14159
    g30: ArcOfCircle CenterX=75.5 CenterY=26 CenterZ=0 NormalX=0 NormalY=0 NormalZ=1 AngleXU=0 Radius=2 StartAngle=4.71239 EndAngle=6.28319
    g31: ArcOfCircle CenterX=75.5 CenterY=41 CenterZ=0 NormalX=0 NormalY=0 NormalZ=1 AngleXU=0 Radius=2 StartAngle=4e-16 EndAngle=0.629894
    g32: ArcOfCircle CenterX=-75.5 CenterY=26 CenterZ=0 NormalX=0 NormalY=0 NormalZ=1 AngleXU=0 Radius=2 StartAngle=3.14159 EndAngle=4.71239
    g33: ArcOfCircle CenterX=-75.5 CenterY=41 CenterZ=0 NormalX=0 NormalY=0 NormalZ=1 AngleXU=0 Radius=2 StartAngle=2.5117 EndAngle=3.14159
    g34: LineSegment StartX=77.5 StartY=26 StartZ=0 EndX=77.5 EndY=-26 EndZ=0
    g35: LineSegment StartX=-77.5 StartY=26 StartZ=0 EndX=-77.5 EndY=-26 EndZ=0
    g36: LineSegment StartX=-17.8805 StartY=96.1846 StartZ=0 EndX=17.8805 EndY=96.1846 EndZ=0
    g37: GeomPoint X=0 Y=96.1846 Z=0
    g38: LineSegment StartX=-21.921 StartY=94.1299 StartZ=0 EndX=-63.1162 EndY=37.617 EndZ=0
    g39: LineSegment StartX=-63.5 StartY=36.4389 StartZ=0 EndX=-63.5 EndY=-24 EndZ=0
    g40: LineSegment StartX=21.921 StartY=94.1299 StartZ=0 EndX=63.1162 EndY=37.617 EndZ=0
    g41: LineSegment StartX=63.5 StartY=36.4389 StartZ=0 EndX=63.5 EndY=-24 EndZ=0
    g42: ArcOfCircle CenterX=0 CenterY=61.5293 CenterZ=0 NormalX=0 NormalY=0 NormalZ=1 AngleXU=0 Radius=107.345 StartAngle=4.08899 EndAngle=5.33579
    g43: LineSegment StartX=-63.5 StartY=36.4389 StartZ=0 EndX=63.5 EndY=36.4389 EndZ=0
    g44: GeomPoint X=0 Y=-45.8154 Z=0
    g45: ArcOfCircle CenterX=-17.8805 CenterY=91.1846 CenterZ=0 NormalX=0 NormalY=0 NormalZ=1 AngleXU=0 Radius=5 StartAngle=1.5708 EndAngle=2.5117
    g46: ArcOfCircle CenterX=17.8805 CenterY=91.1846 CenterZ=0 NormalX=0 NormalY=0 NormalZ=1 AngleXU=0 Radius=5 StartAngle=0.629894 EndAngle=1.5708
    g47: ArcOfCircle CenterX=61.5 CenterY=36.4389 CenterZ=0 NormalX=0 NormalY=0 NormalZ=1 AngleXU=0 Radius=2 StartAngle=-9e-16 EndAngle=0.629894
    g48: ArcOfCircle CenterX=-61.5 CenterY=36.4389 CenterZ=0 NormalX=0 NormalY=0 NormalZ=1 AngleXU=0 Radius=2 StartAngle=2.5117 EndAngle=3.14159
    g49: ArcOfCircle CenterX=61.5 CenterY=-24 CenterZ=0 NormalX=0 NormalY=0 NormalZ=1 AngleXU=0 Radius=2 StartAngle=5.33579 EndAngle=6.28319
    g50: ArcOfCircle CenterX=-61.5 CenterY=-24 CenterZ=0 NormalX=0 NormalY=0 NormalZ=1 AngleXU=0 Radius=2 StartAngle=3.14159 EndAngle=4.08899
    g51: LineSegment StartX=-29.0404 StartY=108.13 StartZ=0 EndX=-17.7272 EndY=99.883 EndZ=0
  constraints (125):
    c: Vertical(g0)
    c: Vertical(g1)
    c: Horizontal(g2)
    c: Symmetric(g2,g2,g-1)
    c: Horizontal(g3)
    c: Horizontal(g5)
    c: Horizontal(g6)
    c: PointOnObject(g7,g-2)
    c: Horizontal(g8)
    c: Horizontal(g9)
    c: Horizontal(g11)
    c: Coincident(g13,g-1)
    c: PointOnObject(g13,g-2)
    c: Tangent(g10,g14) = 1.5708
    c: Tangent(g11,g14) = 1.5708
    c: Tangent(g11,g15) = 1.5708
    c: Tangent(g12,g15) = 1.5708
    c: Tangent(g8,g16) = -1.5708
    c: Tangent(g0,g16) = 1.5708
    c: Tangent(g5,g17) = 1.5708
    c: Tangent(g0,g17) = 1.5708
    c: Tangent(g1,g18) = -1.5708
    c: Tangent(g6,g18) = -1.5708
    c: Tangent(g1,g19) = -1.5708
    c: Tangent(g9,g19) = 1.5708
    c: Equal(g15,g14)
    c: Symmetric(g11,g11,g13)
    c: Equal(g18,g19)
    c: Equal(g19,g16)
    c: Equal(g16,g17)
    c: PointOnObject(g20,g-2)
    c: PointOnObject(g20,g7)
    c: Coincident(g4,g8)
    c: Coincident(g4,g9)
    c: Coincident(g3,g6)
    c: Coincident(g3,g5)
    c: DistanceX(g2,g2) = 87
    c: Symmetric(g0,g0,g2)
    c: Symmetric(g1,g1,g2)
    c: Radius(g19) = 7
    c: DistanceY(g20,g11) = 170
    c: Radius(g15) = 5
    c: DistanceX(g11,g11) = 50
    c: Equal(g9,g8)
    c: Equal(g9,g6)
    c: Coincident(g21,g7)
    c: PointOnObject(g20,g21)
    c: Diameter(g21) = 225
    c: Vertical(g22)
    c: Vertical(g23)
    c: Vertical(g24)
    c: Vertical(g25)
    c: Equal(g5,g8)
    c: Equal(g10,g12)
    c: Tangent(g7,g26) = -1.5708
    c: Tangent(g23,g26) = 1.5708
    c: Tangent(g23,g27) = 1.5708
    c: Tangent(g6,g27) = 1.5708
    c: Tangent(g7,g28) = -1.5708
    c: Tangent(g24,g28) = 1.5708
    c: Tangent(g24,g29) = 1.5708
    c: Tangent(g5,g29) = -1.5708
    c: Equal(g29,g27)
    c: Radius(g27) = 2
    c: Equal(g26,g28)
    c: Radius(g26) = 2
    c: Tangent(g9,g30) = -1.5708
    c: Tangent(g22,g30) = -1.5708
    c: Tangent(g22,g31) = -1.5708
    c: Tangent(g12,g31) = 1.5708
    c: Tangent(g8,g32) = 1.5708
    c: Tangent(g25,g32) = 1.5708
    c: Tangent(g10,g33) = 1.5708
    c: Tangent(g25,g33) = 1.5708
    c: Equal(g30,g32)
    c: Equal(g31,g33)
    c: DistanceY(g23,g23) = 2
    c: DistanceY(g22,g22) = 15
    c: DistanceY(g6,g9) = 48
    c: DistanceX(g24,g23) = 155
    c: Radius(g30) = 2
    c: Radius(g31) = 2
    c: Coincident(g34,g22)
    c: Coincident(g34,g23)
    c: Coincident(g35,g25)
    c: Coincident(g35,g24)
    c: Horizontal(g36)
    c: PointOnObject(g37,g13)
    c: DistanceY(g37,g13) = 14
    c: Vertical(g39)
    c: Vertical(g41)
    c: PointOnObject(g42,g13)
    c: Horizontal(g43)
    c: Parallel(g40,g12)
    c: PointOnObject(g44,g-2)
    c: PointOnObject(g44,g42)
    c: Tangent(g38,g45) = -1.5708
    c: Tangent(g36,g45) = 1.5708
    c: Tangent(g40,g46) = 1.5708
    c: Tangent(g36,g46) = 1.5708
    c: Tangent(g41,g47) = 1.5708
    c: Tangent(g40,g47) = 1.5708
    c: Tangent(g39,g48) = -1.5708
    c: Tangent(g38,g48) = -1.5708
    c: Tangent(g42,g49) = -1.5708
    c: Tangent(g41,g49) = 1.5708
    c: Tangent(g42,g50) = -1.5708
    c: Tangent(g39,g50) = -1.5708
    c: Coincident(g43,g39)
    c: Coincident(g43,g41)
    c: Equal(g15,g46)
    c: Equal(g46,g45)
    c: Symmetric(g36,g36,g37)
    c: Equal(g31,g47)
    c: Equal(g26,g49)
    c: Equal(g50,g29)
    c: Equal(g48,g32)
    c: PointOnObject(g41,g6)
    c: PointOnObject(g50,g5)
    c: DistanceY(g20,g44) = 14
    c: DistanceX(g41,g22) = 14
    c: PointOnObject(g51,g38)
    c: Perpendicular(g38,g51)
    c: Distance(g51) = 14
    c: Coincident(g51,g10)
FEATURE [PartDesign::Pocket] Pocket005
  BaseFeature = -> Chamfer002
  Length = 5
  Length2 = 100
  Midplane = true
  Placement = pos=(0,0,0) rot=(1,0,0;1.5708rad)
  Profile = -> Sketch067
  Type = 1
FEATURE [PartDesign::Body] Body002  label="PB3D_XPort_CoverPlug_P1"
  Group = -> [DatumPlane006,DatumPlane007,Sketch060,Sketch061,Sketch070,Pad004,Sketch062,Sketch059,Sketch058,Sketch063,Pad003,Pocket001,SubtractiveLoft002,Sketch067,Sketch064,Sketch066,Sketch068,Sketch065,Sketch069,Chamfer002,Pocket005]
  Origin = -> Origin003
  Tip = -> Pocket005
FEATURE [PartDesign::Pocket] Pocket006
  BaseFeature = -> Chamfer003
  Length = 5
  Length2 = 100
  Midplane = true
  Placement = pos=(0,0,0) rot=(1,0,0;1.5708rad)
  Profile = -> Sketch077
  Type = 1
FEATURE [PartDesign::Pocket] Pocket007
  BaseFeature = -> Pocket006
  Length = 5
  Length2 = 100
  Midplane = true
  Placement = pos=(0,0,0) rot=(1,0,0;1.5708rad)
  Profile = -> Sketch079
  Type = 1
FEATURE [PartDesign::Body] Body003  label="PB3D_XPort_CoverPlug_P2"
  Group = -> [DatumPlane010,DatumPlane011,Sketch073,Sketch074,Sketch083,Pad006,Sketch075,Sketch072,Sketch071,Sketch076,Pad005,Pocket002,SubtractiveLoft003,Sketch080,Sketch077,Sketch079,Sketch081,Sketch078,Sketch082,Chamfer003,Pocket006,Pocket007]
  Origin = -> Origin004
  Tip = -> Pocket007
FEATURE [PartDesign::Pocket] Pocket008
  BaseFeature = -> Chamfer004
  Length = 5
  Length2 = 100
  Midplane = true
  Placement = pos=(0,0,0) rot=(1,0,0;1.5708rad)
  Profile = -> Sketch094
  Type = 1
FEATURE [PartDesign::Pocket] Pocket009
  BaseFeature = -> Pocket008
  Length = 5
  Length2 = 100
  Midplane = true
  Placement = pos=(0,0,0) rot=(1,0,0;1.5708rad)
  Profile = -> Sketch091
  Type = 1
FEATURE [PartDesign::Body] Body004  label="PB3D_XPort_CoverPlug_P3"
  Group = -> [DatumPlane014,DatumPlane015,Sketch086,Sketch087,Sketch096,Pad008,Sketch088,Sketch085,Sketch084,Sketch089,Pad007,Pocket003,SubtractiveLoft004,Sketch093,Sketch090,Sketch092,Sketch094,Sketch091,Sketch095,Chamfer004,Pocket008,Pocket009]
  Origin = -> Origin005
  Tip = -> Pocket009
FEATURE [PartDesign::Pocket] Pocket010
  BaseFeature = -> Chamfer005
  Length = 5
  Length2 = 100
  Midplane = true
  Placement = pos=(0,0,0) rot=(1,0,0;1.5708rad)
  Profile = -> Sketch108
  Type = 1
FEATURE [PartDesign::Body] Body005  label="PB3D_XPort_CoverPlug_P4"
  Group = -> [DatumPlane018,DatumPlane019,Sketch099,Sketch100,Sketch109,Pad010,Sketch101,Sketch098,Sketch097,Sketch102,Pad009,Pocket004,SubtractiveLoft005,Sketch106,Sketch103,Sketch105,Sketch107,Sketch104,Sketch108,Chamfer005,Pocket010]
  Origin = -> Origin006
  Tip = -> Pocket010
FEATURE [PartDesign::Boolean] Boolean
  BaseFeature = -> Chamfer
  Group = -> [Body002]
  Type = 0
FEATURE [PartDesign::Boolean] Boolean001
  BaseFeature = -> Boolean
  Group = -> [Body003]
  Type = 0
FEATURE [PartDesign::Boolean] Boolean002
  BaseFeature = -> Boolean001
  Group = -> [Body004]
  Type = 0
FEATURE [PartDesign::Boolean] Boolean003
  BaseFeature = -> Boolean002
  Group = -> [Body005]
  Type = 0
FEATURE [PartDesign::Body] Body  label="PB3D_XPort_Cover_L"
  Group = -> [DatumPlane,DatumPlane001,Sketch002,Sketch003,Sketch,Pad,SubtractiveLoft,Sketch009,Sketch010,Sketch013,Chamfer,Boolean,Boolean001,Boolean002,Boolean003]
  Origin = -> Origin001
  Tip = -> Boolean003
FEATURE [App::Part] Part  label="PB3D_Part_XPort_Cover"
  Group = -> [Body,Body001]
  Origin = -> Origin
FEATURE [Part::Mirroring] Part__Mirroring  label="PB3D_XPort_Cover_R"
  Base = (0,0,0)
  Normal = (1,0,0)
  Source = -> Body
FEATURE [Mesh::Feature] Mesh  label="PB3D_XPort_Cover_L (Meshed)"
FEATURE [Mesh::Feature] Mesh001  label="PB3D_XPort_Cover_R (Meshed)"
